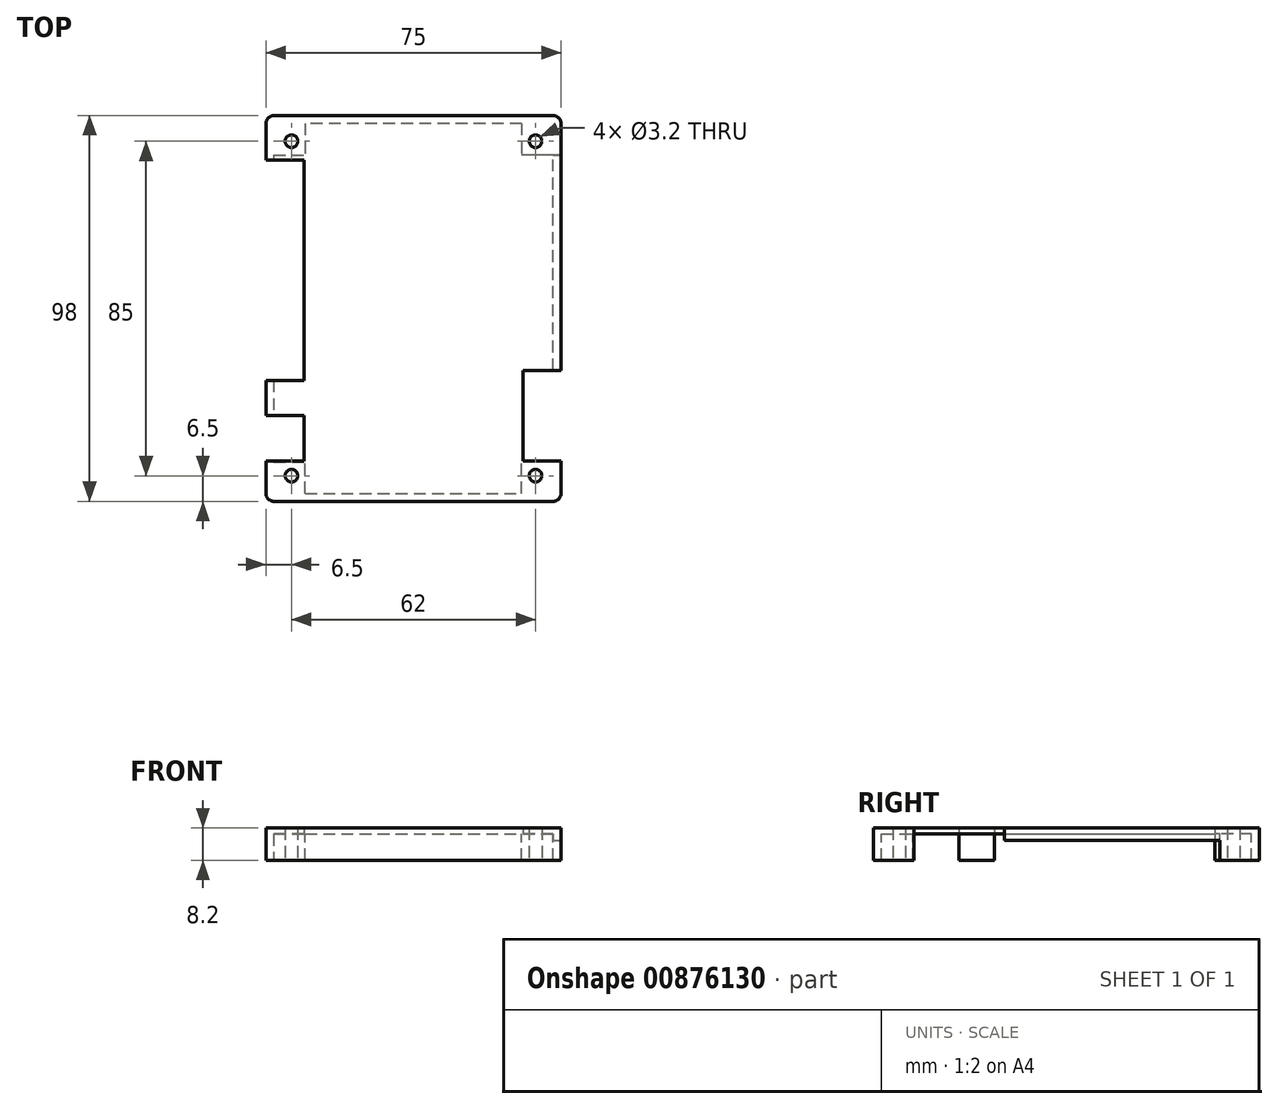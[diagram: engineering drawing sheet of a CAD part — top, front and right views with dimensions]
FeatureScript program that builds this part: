
annotation { "Feature Type Name" : "Feature", "Feature Type Description" : "" }
export const myFeature = defineFeature(function(context is Context, id is Id, definition is map)
    precondition{}
    {
        {
            var Q0;
            Q0=qCreatedBy(makeId("Top.planeOp"),FACE);
            var sketch = newSketch(context, id + "F0", { "sketchPlane" : qUnion([Q0])});
            skLineSegment(sketch, "E0", {"start": v(-9.05, 33.9) * mm, "end": v(-6.45, 33.9) * mm});
            skLineSegment(sketch, "E1", {"start": v(-6.45, 33.9) * mm, "end": v(-6.45, 30.1) * mm});
            skLineSegment(sketch, "E2", {"start": v(-6.45, 30.1) * mm, "end": v(-9.05, 30.1) * mm});
            skLineSegment(sketch, "E3", {"start": v(-9.05, 30.1) * mm, "end": v(-9.05, 33.9) * mm});
            skLineSegment(sketch, "E4", {"start": v(20.45, 33.9) * mm, "end": v(23.05, 33.9) * mm});
            skLineSegment(sketch, "E5", {"start": v(23.05, 33.9) * mm, "end": v(23.05, 30.1) * mm});
            skLineSegment(sketch, "E6", {"start": v(23.05, 30.1) * mm, "end": v(20.45, 30.1) * mm});
            skLineSegment(sketch, "E7", {"start": v(20.45, 30.1) * mm, "end": v(20.45, 33.9) * mm});
            skLineSegment(sketch, "E8", {"start": v(1.5, 35.5) * mm, "end": v(12.5, 35.5) * mm});
            skLineSegment(sketch, "E9", {"start": v(12.5, 35.5) * mm, "end": v(12.5, 28.5) * mm});
            skLineSegment(sketch, "E10", {"start": v(12.5, 28.5) * mm, "end": v(1.5, 28.5) * mm});
            skLineSegment(sketch, "E11", {"start": v(1.5, 28.5) * mm, "end": v(1.5, 35.5) * mm});
            skLineSegment(sketch, "E12", {"start": v(-5.5, 39) * mm, "end": v(-5.5, 37) * mm});
            skLineSegment(sketch, "E13", {"start": v(-4.5, 38) * mm, "end": v(-6.5, 38) * mm});
            skLineSegment(sketch, "E14", {"start": v(7, 32.5) * mm, "end": v(7, 31.5) * mm});
            skLineSegment(sketch, "E15", {"start": v(7.5, 32) * mm, "end": v(6.5, 32) * mm});
            skLineSegment(sketch, "E16", {"start": v(18, 40) * mm, "end": v(-4, 40) * mm});
            skLineSegment(sketch, "E17", {"start": v(-4, 40) * mm, "end": v(-4, 25.75) * mm});
            skLineSegment(sketch, "E18", {"start": v(-4, 25.75) * mm, "end": v(-2.25, 24) * mm});
            skLineSegment(sketch, "E19", {"start": v(-2.25, 24) * mm, "end": v(18, 24) * mm});
            skLineSegment(sketch, "E20", {"start": v(18, 24) * mm, "end": v(18, 40) * mm});
            skLineSegment(sketch, "E21", {"start": v(-7.2, 34.4) * mm, "end": v(-7.2, 36) * mm});
            skLineSegment(sketch, "E22", {"start": v(-7.2, 36) * mm, "end": v(-4, 36) * mm});
            skLineSegment(sketch, "E23", {"start": v(-7.2, 29.6) * mm, "end": v(-7.2, 28) * mm});
            skLineSegment(sketch, "E24", {"start": v(-7.2, 28) * mm, "end": v(-4, 28) * mm});
            skLineSegment(sketch, "E25", {"start": v(21.2, 29.6) * mm, "end": v(21.2, 28) * mm});
            skLineSegment(sketch, "E26", {"start": v(21.2, 28) * mm, "end": v(18, 28) * mm});
            skLineSegment(sketch, "E27", {"start": v(21.2, 34.4) * mm, "end": v(21.2, 36) * mm});
            skLineSegment(sketch, "E28", {"start": v(21.2, 36) * mm, "end": v(18, 36) * mm});
            skArc(sketch, "E29", {"start": v(13, 40) * mm, "mid": v(17, 32) * mm, "end": v(13, 24) * mm});
            skArc(sketch, "E30", {"start": v(1, 40) * mm, "mid": v(-3, 32) * mm, "end": v(1, 24) * mm});
            skArc(sketch, "E31", {"start": v(17, 32) * mm, "mid": v(7, 42) * mm, "end": v(-3, 32) * mm});
            skArc(sketch, "E32", {"start": v(-3, 32) * mm, "mid": v(7, 22) * mm, "end": v(17, 32) * mm});
            skCircle(sketch, "E33", {"center": v(29, 41) * mm, "radius": 1.65 * mm});
            skArc(sketch, "E34", {"start": v(29.64, 41) * mm, "mid": v(29, 41.63) * mm, "end": v(28.37, 41) * mm});
            skArc(sketch, "E35", {"start": v(28.37, 41) * mm, "mid": v(29, 40.37) * mm, "end": v(29.64, 41) * mm});
            skCircle(sketch, "E36", {"center": v(-33, 41) * mm, "radius": 1.65 * mm});
            skArc(sketch, "E37", {"start": v(-32.37, 41) * mm, "mid": v(-33, 41.63) * mm, "end": v(-33.63, 41) * mm});
            skArc(sketch, "E38", {"start": v(-33.63, 41) * mm, "mid": v(-33, 40.37) * mm, "end": v(-32.37, 41) * mm});
            skCircle(sketch, "E39", {"center": v(29, -44) * mm, "radius": 1.65 * mm});
            skArc(sketch, "E40", {"start": v(29.64, -44) * mm, "mid": v(29, -43.37) * mm, "end": v(28.37, -44) * mm});
            skArc(sketch, "E41", {"start": v(28.37, -44) * mm, "mid": v(29, -44.63) * mm, "end": v(29.64, -44) * mm});
            skCircle(sketch, "E42", {"center": v(-33, -44) * mm, "radius": 1.65 * mm});
            skArc(sketch, "E43", {"start": v(-32.37, -44) * mm, "mid": v(-33, -43.37) * mm, "end": v(-33.63, -44) * mm});
            skArc(sketch, "E44", {"start": v(-33.63, -44) * mm, "mid": v(-33, -44.63) * mm, "end": v(-32.37, -44) * mm});
            skLineSegment(sketch, "E45", {"start": v(-12.64, 32.77) * mm, "end": v(-12.64, 30.73) * mm});
            skLineSegment(sketch, "E46", {"start": v(-12.64, 30.73) * mm, "end": v(-14.16, 30.73) * mm});
            skLineSegment(sketch, "E47", {"start": v(-14.16, 30.73) * mm, "end": v(-14.16, 32.77) * mm});
            skLineSegment(sketch, "E48", {"start": v(-14.16, 32.77) * mm, "end": v(-12.64, 32.77) * mm});
            skLineSegment(sketch, "E49", {"start": v(-15.84, 32.77) * mm, "end": v(-15.84, 30.73) * mm});
            skLineSegment(sketch, "E50", {"start": v(-15.84, 30.73) * mm, "end": v(-17.36, 30.73) * mm});
            skLineSegment(sketch, "E51", {"start": v(-17.36, 30.73) * mm, "end": v(-17.36, 32.77) * mm});
            skLineSegment(sketch, "E52", {"start": v(-17.36, 32.77) * mm, "end": v(-15.84, 32.77) * mm});
            skLineSegment(sketch, "E53", {"start": v(-12.2, 30.35) * mm, "end": v(-12.2, 33.15) * mm});
            skLineSegment(sketch, "E54", {"start": v(-12.2, 33.15) * mm, "end": v(-17.8, 33.15) * mm});
            skLineSegment(sketch, "E55", {"start": v(-17.8, 33.15) * mm, "end": v(-17.8, 30.35) * mm});
            skLineSegment(sketch, "E56", {"start": v(-17.8, 30.35) * mm, "end": v(-12.2, 30.35) * mm});
            skLineSegment(sketch, "E57", {"start": v(-14.62, 31.75) * mm, "end": v(-15.38, 31.75) * mm});
            skLineSegment(sketch, "E58", {"start": v(-15, 31.37) * mm, "end": v(-15, 32.13) * mm});
            skLineSegment(sketch, "E59", {"start": v(-12.2, 33.15) * mm, "end": v(-12.56, 33.15) * mm});
            skLineSegment(sketch, "E60", {"start": v(-12.56, 33.15) * mm, "end": v(-12.56, 30.58) * mm});
            skLineSegment(sketch, "E61", {"start": v(-12.56, 30.58) * mm, "end": v(-12.56, 30.35) * mm});
            skLineSegment(sketch, "E62", {"start": v(-12.56, 30.35) * mm, "end": v(-12.2, 30.35) * mm});
            skLineSegment(sketch, "E63", {"start": v(-12.2, 30.35) * mm, "end": v(-12.2, 30.6) * mm});
            skLineSegment(sketch, "E64", {"start": v(-12.2, 30.6) * mm, "end": v(-12.2, 33.15) * mm});
            skLineSegment(sketch, "E65", {"start": v(-12.64, 29.52) * mm, "end": v(-12.64, 27.48) * mm});
            skLineSegment(sketch, "E66", {"start": v(-12.64, 27.48) * mm, "end": v(-14.16, 27.48) * mm});
            skLineSegment(sketch, "E67", {"start": v(-14.16, 27.48) * mm, "end": v(-14.16, 29.52) * mm});
            skLineSegment(sketch, "E68", {"start": v(-14.16, 29.52) * mm, "end": v(-12.64, 29.52) * mm});
            skLineSegment(sketch, "E69", {"start": v(-15.84, 29.52) * mm, "end": v(-15.84, 27.48) * mm});
            skLineSegment(sketch, "E70", {"start": v(-15.84, 27.48) * mm, "end": v(-17.36, 27.48) * mm});
            skLineSegment(sketch, "E71", {"start": v(-17.36, 27.48) * mm, "end": v(-17.36, 29.52) * mm});
            skLineSegment(sketch, "E72", {"start": v(-17.36, 29.52) * mm, "end": v(-15.84, 29.52) * mm});
            skLineSegment(sketch, "E73", {"start": v(-12.2, 27.1) * mm, "end": v(-12.2, 29.9) * mm});
            skLineSegment(sketch, "E74", {"start": v(-12.2, 29.9) * mm, "end": v(-17.8, 29.9) * mm});
            skLineSegment(sketch, "E75", {"start": v(-17.8, 29.9) * mm, "end": v(-17.8, 27.1) * mm});
            skLineSegment(sketch, "E76", {"start": v(-17.8, 27.1) * mm, "end": v(-12.2, 27.1) * mm});
            skLineSegment(sketch, "E77", {"start": v(-14.62, 28.5) * mm, "end": v(-15.38, 28.5) * mm});
            skLineSegment(sketch, "E78", {"start": v(-15, 28.12) * mm, "end": v(-15, 28.88) * mm});
            skLineSegment(sketch, "E79", {"start": v(-12.2, 29.9) * mm, "end": v(-12.56, 29.9) * mm});
            skLineSegment(sketch, "E80", {"start": v(-12.56, 29.9) * mm, "end": v(-12.56, 27.33) * mm});
            skLineSegment(sketch, "E81", {"start": v(-12.56, 27.33) * mm, "end": v(-12.56, 27.1) * mm});
            skLineSegment(sketch, "E82", {"start": v(-12.56, 27.1) * mm, "end": v(-12.2, 27.1) * mm});
            skLineSegment(sketch, "E83", {"start": v(-12.2, 27.1) * mm, "end": v(-12.2, 27.36) * mm});
            skLineSegment(sketch, "E84", {"start": v(-12.2, 27.36) * mm, "end": v(-12.2, 29.9) * mm});
            skLineSegment(sketch, "E85", {"start": v(-12.64, 16.77) * mm, "end": v(-12.64, 14.73) * mm});
            skLineSegment(sketch, "E86", {"start": v(-12.64, 14.73) * mm, "end": v(-14.16, 14.73) * mm});
            skLineSegment(sketch, "E87", {"start": v(-14.16, 14.73) * mm, "end": v(-14.16, 16.77) * mm});
            skLineSegment(sketch, "E88", {"start": v(-14.16, 16.77) * mm, "end": v(-12.64, 16.77) * mm});
            skLineSegment(sketch, "E89", {"start": v(-15.84, 16.77) * mm, "end": v(-15.84, 14.73) * mm});
            skLineSegment(sketch, "E90", {"start": v(-15.84, 14.73) * mm, "end": v(-17.36, 14.73) * mm});
            skLineSegment(sketch, "E91", {"start": v(-17.36, 14.73) * mm, "end": v(-17.36, 16.77) * mm});
            skLineSegment(sketch, "E92", {"start": v(-17.36, 16.77) * mm, "end": v(-15.84, 16.77) * mm});
            skLineSegment(sketch, "E93", {"start": v(-12.2, 14.35) * mm, "end": v(-12.2, 17.15) * mm});
            skLineSegment(sketch, "E94", {"start": v(-12.2, 17.15) * mm, "end": v(-17.8, 17.15) * mm});
            skLineSegment(sketch, "E95", {"start": v(-17.8, 17.15) * mm, "end": v(-17.8, 14.35) * mm});
            skLineSegment(sketch, "E96", {"start": v(-17.8, 14.35) * mm, "end": v(-12.2, 14.35) * mm});
            skLineSegment(sketch, "E97", {"start": v(-14.62, 15.75) * mm, "end": v(-15.38, 15.75) * mm});
            skLineSegment(sketch, "E98", {"start": v(-15, 15.37) * mm, "end": v(-15, 16.13) * mm});
            skLineSegment(sketch, "E99", {"start": v(-12.2, 17.15) * mm, "end": v(-12.56, 17.15) * mm});
            skLineSegment(sketch, "E100", {"start": v(-12.56, 17.15) * mm, "end": v(-12.56, 14.58) * mm});
            skLineSegment(sketch, "E101", {"start": v(-12.56, 14.58) * mm, "end": v(-12.56, 14.35) * mm});
            skLineSegment(sketch, "E102", {"start": v(-12.56, 14.35) * mm, "end": v(-12.2, 14.35) * mm});
            skLineSegment(sketch, "E103", {"start": v(-12.2, 14.35) * mm, "end": v(-12.2, 14.6) * mm});
            skLineSegment(sketch, "E104", {"start": v(-12.2, 14.6) * mm, "end": v(-12.2, 17.15) * mm});
            skLineSegment(sketch, "E105", {"start": v(-12.64, 13.52) * mm, "end": v(-12.64, 11.48) * mm});
            skLineSegment(sketch, "E106", {"start": v(-12.64, 11.48) * mm, "end": v(-14.16, 11.48) * mm});
            skLineSegment(sketch, "E107", {"start": v(-14.16, 11.48) * mm, "end": v(-14.16, 13.52) * mm});
            skLineSegment(sketch, "E108", {"start": v(-14.16, 13.52) * mm, "end": v(-12.64, 13.52) * mm});
            skLineSegment(sketch, "E109", {"start": v(-15.84, 13.52) * mm, "end": v(-15.84, 11.48) * mm});
            skLineSegment(sketch, "E110", {"start": v(-15.84, 11.48) * mm, "end": v(-17.36, 11.48) * mm});
            skLineSegment(sketch, "E111", {"start": v(-17.36, 11.48) * mm, "end": v(-17.36, 13.52) * mm});
            skLineSegment(sketch, "E112", {"start": v(-17.36, 13.52) * mm, "end": v(-15.84, 13.52) * mm});
            skLineSegment(sketch, "E113", {"start": v(-12.2, 11.1) * mm, "end": v(-12.2, 13.9) * mm});
            skLineSegment(sketch, "E114", {"start": v(-12.2, 13.9) * mm, "end": v(-17.8, 13.9) * mm});
            skLineSegment(sketch, "E115", {"start": v(-17.8, 13.9) * mm, "end": v(-17.8, 11.1) * mm});
            skLineSegment(sketch, "E116", {"start": v(-17.8, 11.1) * mm, "end": v(-12.2, 11.1) * mm});
            skLineSegment(sketch, "E117", {"start": v(-14.62, 12.5) * mm, "end": v(-15.38, 12.5) * mm});
            skLineSegment(sketch, "E118", {"start": v(-15, 12.12) * mm, "end": v(-15, 12.88) * mm});
            skLineSegment(sketch, "E119", {"start": v(-12.2, 13.9) * mm, "end": v(-12.56, 13.9) * mm});
            skLineSegment(sketch, "E120", {"start": v(-12.56, 13.9) * mm, "end": v(-12.56, 11.33) * mm});
            skLineSegment(sketch, "E121", {"start": v(-12.56, 11.33) * mm, "end": v(-12.56, 11.1) * mm});
            skLineSegment(sketch, "E122", {"start": v(-12.56, 11.1) * mm, "end": v(-12.2, 11.1) * mm});
            skLineSegment(sketch, "E123", {"start": v(-12.2, 11.1) * mm, "end": v(-12.2, 11.36) * mm});
            skLineSegment(sketch, "E124", {"start": v(-12.2, 11.36) * mm, "end": v(-12.2, 13.9) * mm});
            skLineSegment(sketch, "E125", {"start": v(-12.64, 0.77) * mm, "end": v(-12.64, -1.27) * mm});
            skLineSegment(sketch, "E126", {"start": v(-12.64, -1.27) * mm, "end": v(-14.16, -1.27) * mm});
            skLineSegment(sketch, "E127", {"start": v(-14.16, -1.27) * mm, "end": v(-14.16, 0.77) * mm});
            skLineSegment(sketch, "E128", {"start": v(-14.16, 0.77) * mm, "end": v(-12.64, 0.77) * mm});
            skLineSegment(sketch, "E129", {"start": v(-15.84, 0.77) * mm, "end": v(-15.84, -1.27) * mm});
            skLineSegment(sketch, "E130", {"start": v(-15.84, -1.27) * mm, "end": v(-17.36, -1.27) * mm});
            skLineSegment(sketch, "E131", {"start": v(-17.36, -1.27) * mm, "end": v(-17.36, 0.77) * mm});
            skLineSegment(sketch, "E132", {"start": v(-17.36, 0.77) * mm, "end": v(-15.84, 0.77) * mm});
            skLineSegment(sketch, "E133", {"start": v(-12.2, -1.65) * mm, "end": v(-12.2, 1.15) * mm});
            skLineSegment(sketch, "E134", {"start": v(-12.2, 1.15) * mm, "end": v(-17.8, 1.15) * mm});
            skLineSegment(sketch, "E135", {"start": v(-17.8, 1.15) * mm, "end": v(-17.8, -1.65) * mm});
            skLineSegment(sketch, "E136", {"start": v(-17.8, -1.65) * mm, "end": v(-12.2, -1.65) * mm});
            skLineSegment(sketch, "E137", {"start": v(-14.62, -0.25) * mm, "end": v(-15.38, -0.25) * mm});
            skLineSegment(sketch, "E138", {"start": v(-15, -0.63) * mm, "end": v(-15, 0.13) * mm});
            skLineSegment(sketch, "E139", {"start": v(-12.2, 1.15) * mm, "end": v(-12.56, 1.15) * mm});
            skLineSegment(sketch, "E140", {"start": v(-12.56, 1.15) * mm, "end": v(-12.56, -1.42) * mm});
            skLineSegment(sketch, "E141", {"start": v(-12.56, -1.42) * mm, "end": v(-12.56, -1.65) * mm});
            skLineSegment(sketch, "E142", {"start": v(-12.56, -1.65) * mm, "end": v(-12.2, -1.65) * mm});
            skLineSegment(sketch, "E143", {"start": v(-12.2, -1.65) * mm, "end": v(-12.2, -1.4) * mm});
            skLineSegment(sketch, "E144", {"start": v(-12.2, -1.4) * mm, "end": v(-12.2, 1.15) * mm});
            skLineSegment(sketch, "E145", {"start": v(-12.64, -2.48) * mm, "end": v(-12.64, -4.52) * mm});
            skLineSegment(sketch, "E146", {"start": v(-12.64, -4.52) * mm, "end": v(-14.16, -4.52) * mm});
            skLineSegment(sketch, "E147", {"start": v(-14.16, -4.52) * mm, "end": v(-14.16, -2.48) * mm});
            skLineSegment(sketch, "E148", {"start": v(-14.16, -2.48) * mm, "end": v(-12.64, -2.48) * mm});
            skLineSegment(sketch, "E149", {"start": v(-15.84, -2.48) * mm, "end": v(-15.84, -4.52) * mm});
            skLineSegment(sketch, "E150", {"start": v(-15.84, -4.52) * mm, "end": v(-17.36, -4.52) * mm});
            skLineSegment(sketch, "E151", {"start": v(-17.36, -4.52) * mm, "end": v(-17.36, -2.48) * mm});
            skLineSegment(sketch, "E152", {"start": v(-17.36, -2.48) * mm, "end": v(-15.84, -2.48) * mm});
            skLineSegment(sketch, "E153", {"start": v(-12.2, -4.9) * mm, "end": v(-12.2, -2.1) * mm});
            skLineSegment(sketch, "E154", {"start": v(-12.2, -2.1) * mm, "end": v(-17.8, -2.1) * mm});
            skLineSegment(sketch, "E155", {"start": v(-17.8, -2.1) * mm, "end": v(-17.8, -4.9) * mm});
            skLineSegment(sketch, "E156", {"start": v(-17.8, -4.9) * mm, "end": v(-12.2, -4.9) * mm});
            skLineSegment(sketch, "E157", {"start": v(-14.62, -3.5) * mm, "end": v(-15.38, -3.5) * mm});
            skLineSegment(sketch, "E158", {"start": v(-15, -3.88) * mm, "end": v(-15, -3.12) * mm});
            skLineSegment(sketch, "E159", {"start": v(-12.2, -2.1) * mm, "end": v(-12.56, -2.1) * mm});
            skLineSegment(sketch, "E160", {"start": v(-12.56, -2.1) * mm, "end": v(-12.56, -4.67) * mm});
            skLineSegment(sketch, "E161", {"start": v(-12.56, -4.67) * mm, "end": v(-12.56, -4.9) * mm});
            skLineSegment(sketch, "E162", {"start": v(-12.56, -4.9) * mm, "end": v(-12.2, -4.9) * mm});
            skLineSegment(sketch, "E163", {"start": v(-12.2, -4.9) * mm, "end": v(-12.2, -4.64) * mm});
            skLineSegment(sketch, "E164", {"start": v(-12.2, -4.64) * mm, "end": v(-12.2, -2.1) * mm});
            skLineSegment(sketch, "E165", {"start": v(-12.64, -15.23) * mm, "end": v(-12.64, -17.27) * mm});
            skLineSegment(sketch, "E166", {"start": v(-12.64, -17.27) * mm, "end": v(-14.16, -17.27) * mm});
            skLineSegment(sketch, "E167", {"start": v(-14.16, -17.27) * mm, "end": v(-14.16, -15.23) * mm});
            skLineSegment(sketch, "E168", {"start": v(-14.16, -15.23) * mm, "end": v(-12.64, -15.23) * mm});
            skLineSegment(sketch, "E169", {"start": v(-15.84, -15.23) * mm, "end": v(-15.84, -17.27) * mm});
            skLineSegment(sketch, "E170", {"start": v(-15.84, -17.27) * mm, "end": v(-17.36, -17.27) * mm});
            skLineSegment(sketch, "E171", {"start": v(-17.36, -17.27) * mm, "end": v(-17.36, -15.23) * mm});
            skLineSegment(sketch, "E172", {"start": v(-17.36, -15.23) * mm, "end": v(-15.84, -15.23) * mm});
            skLineSegment(sketch, "E173", {"start": v(-12.2, -17.65) * mm, "end": v(-12.2, -14.85) * mm});
            skLineSegment(sketch, "E174", {"start": v(-12.2, -14.85) * mm, "end": v(-17.8, -14.85) * mm});
            skLineSegment(sketch, "E175", {"start": v(-17.8, -14.85) * mm, "end": v(-17.8, -17.65) * mm});
            skLineSegment(sketch, "E176", {"start": v(-17.8, -17.65) * mm, "end": v(-12.2, -17.65) * mm});
            skLineSegment(sketch, "E177", {"start": v(-14.62, -16.25) * mm, "end": v(-15.38, -16.25) * mm});
            skLineSegment(sketch, "E178", {"start": v(-15, -16.63) * mm, "end": v(-15, -15.87) * mm});
            skLineSegment(sketch, "E179", {"start": v(-12.2, -14.85) * mm, "end": v(-12.56, -14.85) * mm});
            skLineSegment(sketch, "E180", {"start": v(-12.56, -14.85) * mm, "end": v(-12.56, -17.42) * mm});
            skLineSegment(sketch, "E181", {"start": v(-12.56, -17.42) * mm, "end": v(-12.56, -17.65) * mm});
            skLineSegment(sketch, "E182", {"start": v(-12.56, -17.65) * mm, "end": v(-12.2, -17.65) * mm});
            skLineSegment(sketch, "E183", {"start": v(-12.2, -17.65) * mm, "end": v(-12.2, -17.4) * mm});
            skLineSegment(sketch, "E184", {"start": v(-12.2, -17.4) * mm, "end": v(-12.2, -14.85) * mm});
            skLineSegment(sketch, "E185", {"start": v(-5.5, -3.75) * mm, "end": v(-7.5, -3.75) * mm});
            skLineSegment(sketch, "E186", {"start": v(-7.5, -3.75) * mm, "end": v(-7.5, 1.75) * mm});
            skLineSegment(sketch, "E187", {"start": v(-7.5, 1.75) * mm, "end": v(-5.5, 1.75) * mm});
            skLineSegment(sketch, "E188", {"start": v(-5.5, 1.75) * mm, "end": v(-5.5, -3.75) * mm});
            skLineSegment(sketch, "E189", {"start": v(-5.5, 5.25) * mm, "end": v(-7.5, 5.25) * mm});
            skLineSegment(sketch, "E190", {"start": v(-7.5, 5.25) * mm, "end": v(-7.5, 10.75) * mm});
            skLineSegment(sketch, "E191", {"start": v(-7.5, 10.75) * mm, "end": v(-5.5, 10.75) * mm});
            skLineSegment(sketch, "E192", {"start": v(-5.5, 10.75) * mm, "end": v(-5.5, 5.25) * mm});
            skLineSegment(sketch, "E193", {"start": v(-9, -1.5) * mm, "end": v(-9, 8.5) * mm});
            skArc(sketch, "E194", {"start": v(-7.75, -2.75) * mm, "mid": v(-8.63, -2.38) * mm, "end": v(-9, -1.5) * mm});
            skArc(sketch, "E195", {"start": v(-7.75, 9.75) * mm, "mid": v(-8.63, 9.38) * mm, "end": v(-9, 8.5) * mm});
            skLineSegment(sketch, "E196", {"start": v(-4, 8.5) * mm, "end": v(-4, -1.5) * mm});
            skArc(sketch, "E197", {"start": v(-5.25, -2.75) * mm, "mid": v(-4.37, -2.38) * mm, "end": v(-4, -1.5) * mm});
            skArc(sketch, "E198", {"start": v(-5.25, 9.75) * mm, "mid": v(-4.37, 9.38) * mm, "end": v(-4, 8.5) * mm});
            skLineSegment(sketch, "E199", {"start": v(-6.5, 3) * mm, "end": v(-6.5, 4) * mm});
            skLineSegment(sketch, "E200", {"start": v(-7, 3.5) * mm, "end": v(-6, 3.5) * mm});
            skLineSegment(sketch, "E201", {"start": v(-9.45, -36.25) * mm, "end": v(-9.45, -37.75) * mm});
            skLineSegment(sketch, "E202", {"start": v(-9.45, -37.75) * mm, "end": v(-11.05, -37.75) * mm});
            skLineSegment(sketch, "E203", {"start": v(-11.05, -37.75) * mm, "end": v(-11.05, -36.25) * mm});
            skLineSegment(sketch, "E204", {"start": v(-11.05, -36.25) * mm, "end": v(-9.45, -36.25) * mm});
            skLineSegment(sketch, "E205", {"start": v(-11.95, -36.25) * mm, "end": v(-11.95, -37.75) * mm});
            skLineSegment(sketch, "E206", {"start": v(-11.95, -37.75) * mm, "end": v(-13.55, -37.75) * mm});
            skLineSegment(sketch, "E207", {"start": v(-13.55, -37.75) * mm, "end": v(-13.55, -36.25) * mm});
            skLineSegment(sketch, "E208", {"start": v(-13.55, -36.25) * mm, "end": v(-11.95, -36.25) * mm});
            skLineSegment(sketch, "E209", {"start": v(-9, -38) * mm, "end": v(-9, -36) * mm});
            skLineSegment(sketch, "E210", {"start": v(-9, -36) * mm, "end": v(-13.75, -36) * mm});
            skLineSegment(sketch, "E211", {"start": v(-13.75, -36) * mm, "end": v(-13.75, -38) * mm});
            skLineSegment(sketch, "E212", {"start": v(-13.75, -38) * mm, "end": v(-9, -38) * mm});
            skLineSegment(sketch, "E213", {"start": v(-9.25, -38) * mm, "end": v(-9.25, -36) * mm});
            skArc(sketch, "E214", {"start": v(-11.25, -37) * mm, "mid": v(-11.5, -36.75) * mm, "end": v(-11.75, -37) * mm});
            skArc(sketch, "E215", {"start": v(-11.75, -37) * mm, "mid": v(-11.5, -37.25) * mm, "end": v(-11.25, -37) * mm});
            skLineSegment(sketch, "E216", {"start": v(-9.12, -38) * mm, "end": v(-9.12, -36) * mm});
            skLineSegment(sketch, "E217", {"start": v(-8.5, -38.25) * mm, "end": v(-9, -38.25) * mm});
            skLineSegment(sketch, "E218", {"start": v(-8.75, -38.5) * mm, "end": v(-8.75, -38) * mm});
            skLineSegment(sketch, "E219", {"start": v(-9.45, -33.75) * mm, "end": v(-9.45, -35.25) * mm});
            skLineSegment(sketch, "E220", {"start": v(-9.45, -35.25) * mm, "end": v(-11.05, -35.25) * mm});
            skLineSegment(sketch, "E221", {"start": v(-11.05, -35.25) * mm, "end": v(-11.05, -33.75) * mm});
            skLineSegment(sketch, "E222", {"start": v(-11.05, -33.75) * mm, "end": v(-9.45, -33.75) * mm});
            skLineSegment(sketch, "E223", {"start": v(-11.95, -33.75) * mm, "end": v(-11.95, -35.25) * mm});
            skLineSegment(sketch, "E224", {"start": v(-11.95, -35.25) * mm, "end": v(-13.55, -35.25) * mm});
            skLineSegment(sketch, "E225", {"start": v(-13.55, -35.25) * mm, "end": v(-13.55, -33.75) * mm});
            skLineSegment(sketch, "E226", {"start": v(-13.55, -33.75) * mm, "end": v(-11.95, -33.75) * mm});
            skLineSegment(sketch, "E227", {"start": v(-9, -35.5) * mm, "end": v(-9, -33.5) * mm});
            skLineSegment(sketch, "E228", {"start": v(-9, -33.5) * mm, "end": v(-13.75, -33.5) * mm});
            skLineSegment(sketch, "E229", {"start": v(-13.75, -33.5) * mm, "end": v(-13.75, -35.5) * mm});
            skLineSegment(sketch, "E230", {"start": v(-13.75, -35.5) * mm, "end": v(-9, -35.5) * mm});
            skLineSegment(sketch, "E231", {"start": v(-9.25, -35.5) * mm, "end": v(-9.25, -33.5) * mm});
            skArc(sketch, "E232", {"start": v(-11.25, -34.5) * mm, "mid": v(-11.5, -34.25) * mm, "end": v(-11.75, -34.5) * mm});
            skArc(sketch, "E233", {"start": v(-11.75, -34.5) * mm, "mid": v(-11.5, -34.75) * mm, "end": v(-11.25, -34.5) * mm});
            skLineSegment(sketch, "E234", {"start": v(-9.12, -35.5) * mm, "end": v(-9.12, -33.5) * mm});
            skLineSegment(sketch, "E235", {"start": v(-8.5, -35.75) * mm, "end": v(-9, -35.75) * mm});
            skLineSegment(sketch, "E236", {"start": v(-8.75, -36) * mm, "end": v(-8.75, -35.5) * mm});
            skLineSegment(sketch, "E237", {"start": v(-1.95, -34) * mm, "end": v(-1.95, -38) * mm});
            skLineSegment(sketch, "E238", {"start": v(-1.95, -38) * mm, "end": v(-3.45, -38) * mm});
            skLineSegment(sketch, "E239", {"start": v(-3.45, -38) * mm, "end": v(-3.45, -34) * mm});
            skLineSegment(sketch, "E240", {"start": v(-3.45, -34) * mm, "end": v(-1.95, -34) * mm});
            skLineSegment(sketch, "E241", {"start": v(-5.55, -34) * mm, "end": v(-5.55, -38) * mm});
            skLineSegment(sketch, "E242", {"start": v(-5.55, -38) * mm, "end": v(-7.05, -38) * mm});
            skLineSegment(sketch, "E243", {"start": v(-7.05, -38) * mm, "end": v(-7.05, -34) * mm});
            skLineSegment(sketch, "E244", {"start": v(-7.05, -34) * mm, "end": v(-5.55, -34) * mm});
            skLineSegment(sketch, "E245", {"start": v(-4, -36) * mm, "end": v(-5, -36) * mm});
            skLineSegment(sketch, "E246", {"start": v(-4.5, -36.5) * mm, "end": v(-4.5, -35.5) * mm});
            skLineSegment(sketch, "E247", {"start": v(-1.75, -38.5) * mm, "end": v(-1.75, -33.5) * mm});
            skLineSegment(sketch, "E248", {"start": v(-1.75, -33.5) * mm, "end": v(-7.25, -33.5) * mm});
            skLineSegment(sketch, "E249", {"start": v(-7.25, -33.5) * mm, "end": v(-7.25, -38.5) * mm});
            skLineSegment(sketch, "E250", {"start": v(-7.25, -38.5) * mm, "end": v(-1.75, -38.5) * mm});
            skLineSegment(sketch, "E251", {"start": v(-29.15, -38.15) * mm, "end": v(-29.15, -35.85) * mm});
            skLineSegment(sketch, "E252", {"start": v(-29.15, -35.85) * mm, "end": v(-26.85, -35.85) * mm});
            skLineSegment(sketch, "E253", {"start": v(-26.85, -35.85) * mm, "end": v(-26.85, -38.15) * mm});
            skLineSegment(sketch, "E254", {"start": v(-26.85, -38.15) * mm, "end": v(-29.15, -38.15) * mm});
            skLineSegment(sketch, "E255", {"start": v(-25.15, -38.15) * mm, "end": v(-25.15, -35.85) * mm});
            skLineSegment(sketch, "E256", {"start": v(-25.15, -35.85) * mm, "end": v(-22.85, -35.85) * mm});
            skLineSegment(sketch, "E257", {"start": v(-22.85, -35.85) * mm, "end": v(-22.85, -38.15) * mm});
            skLineSegment(sketch, "E258", {"start": v(-22.85, -38.15) * mm, "end": v(-25.15, -38.15) * mm});
            skLineSegment(sketch, "E259", {"start": v(-26.5, -37) * mm, "end": v(-25.5, -37) * mm});
            skLineSegment(sketch, "E260", {"start": v(-26, -36.5) * mm, "end": v(-26, -37.5) * mm});
            skLineSegment(sketch, "E261", {"start": v(-29.75, -35) * mm, "end": v(-22.5, -35) * mm});
            skLineSegment(sketch, "E262", {"start": v(-22.5, -35) * mm, "end": v(-22.5, -39) * mm});
            skLineSegment(sketch, "E263", {"start": v(-22.5, -39) * mm, "end": v(-29.75, -39) * mm});
            skLineSegment(sketch, "E264", {"start": v(-29.75, -39) * mm, "end": v(-29.75, -35) * mm});
            skLineSegment(sketch, "E265", {"start": v(-29.75, -35.25) * mm, "end": v(-29.75, -38.75) * mm});
            skLineSegment(sketch, "E266", {"start": v(-29.75, -38.75) * mm, "end": v(-29.75, -39) * mm});
            skLineSegment(sketch, "E267", {"start": v(-29.75, -39) * mm, "end": v(-29.25, -39) * mm});
            skLineSegment(sketch, "E268", {"start": v(-29.25, -39) * mm, "end": v(-29.25, -38.75) * mm});
            skLineSegment(sketch, "E269", {"start": v(-29.25, -38.75) * mm, "end": v(-29.25, -38.25) * mm});
            skLineSegment(sketch, "E270", {"start": v(-29.25, -38.25) * mm, "end": v(-29.25, -35.75) * mm});
            skLineSegment(sketch, "E271", {"start": v(-29.25, -35.75) * mm, "end": v(-29.25, -35.25) * mm});
            skLineSegment(sketch, "E272", {"start": v(-29.25, -35.25) * mm, "end": v(-29.25, -35) * mm});
            skLineSegment(sketch, "E273", {"start": v(-29.25, -35) * mm, "end": v(-29.5, -35) * mm});
            skLineSegment(sketch, "E274", {"start": v(-29.5, -35) * mm, "end": v(-29.75, -35) * mm});
            skLineSegment(sketch, "E275", {"start": v(-29.75, -35) * mm, "end": v(-29.75, -35.25) * mm});
            skLineSegment(sketch, "E276", {"start": v(-29.15, -33.65) * mm, "end": v(-29.15, -31.35) * mm});
            skLineSegment(sketch, "E277", {"start": v(-29.15, -31.35) * mm, "end": v(-26.85, -31.35) * mm});
            skLineSegment(sketch, "E278", {"start": v(-26.85, -31.35) * mm, "end": v(-26.85, -33.65) * mm});
            skLineSegment(sketch, "E279", {"start": v(-26.85, -33.65) * mm, "end": v(-29.15, -33.65) * mm});
            skLineSegment(sketch, "E280", {"start": v(-25.15, -33.65) * mm, "end": v(-25.15, -31.35) * mm});
            skLineSegment(sketch, "E281", {"start": v(-25.15, -31.35) * mm, "end": v(-22.85, -31.35) * mm});
            skLineSegment(sketch, "E282", {"start": v(-22.85, -31.35) * mm, "end": v(-22.85, -33.65) * mm});
            skLineSegment(sketch, "E283", {"start": v(-22.85, -33.65) * mm, "end": v(-25.15, -33.65) * mm});
            skLineSegment(sketch, "E284", {"start": v(-26.5, -32.5) * mm, "end": v(-25.5, -32.5) * mm});
            skLineSegment(sketch, "E285", {"start": v(-26, -32) * mm, "end": v(-26, -33) * mm});
            skLineSegment(sketch, "E286", {"start": v(-29.75, -30.5) * mm, "end": v(-22.5, -30.5) * mm});
            skLineSegment(sketch, "E287", {"start": v(-22.5, -30.5) * mm, "end": v(-22.5, -34.5) * mm});
            skLineSegment(sketch, "E288", {"start": v(-22.5, -34.5) * mm, "end": v(-29.75, -34.5) * mm});
            skLineSegment(sketch, "E289", {"start": v(-29.75, -34.5) * mm, "end": v(-29.75, -30.5) * mm});
            skLineSegment(sketch, "E290", {"start": v(-29.75, -30.75) * mm, "end": v(-29.75, -34.25) * mm});
            skLineSegment(sketch, "E291", {"start": v(-29.75, -34.25) * mm, "end": v(-29.75, -34.5) * mm});
            skLineSegment(sketch, "E292", {"start": v(-29.75, -34.5) * mm, "end": v(-29.25, -34.5) * mm});
            skLineSegment(sketch, "E293", {"start": v(-29.25, -34.5) * mm, "end": v(-29.25, -34.25) * mm});
            skLineSegment(sketch, "E294", {"start": v(-29.25, -34.25) * mm, "end": v(-29.25, -33.75) * mm});
            skLineSegment(sketch, "E295", {"start": v(-29.25, -33.75) * mm, "end": v(-29.25, -31.25) * mm});
            skLineSegment(sketch, "E296", {"start": v(-29.25, -31.25) * mm, "end": v(-29.25, -30.75) * mm});
            skLineSegment(sketch, "E297", {"start": v(-29.25, -30.75) * mm, "end": v(-29.25, -30.5) * mm});
            skLineSegment(sketch, "E298", {"start": v(-29.25, -30.5) * mm, "end": v(-29.5, -30.5) * mm});
            skLineSegment(sketch, "E299", {"start": v(-29.5, -30.5) * mm, "end": v(-29.75, -30.5) * mm});
            skLineSegment(sketch, "E300", {"start": v(-29.75, -30.5) * mm, "end": v(-29.75, -30.75) * mm});
            skCircle(sketch, "E301", {"center": v(-33, 30.5) * mm, "radius": 1.5 * mm});
            skCircle(sketch, "E302", {"center": v(-33, 34) * mm, "radius": 1.5 * mm});
            skLineSegment(sketch, "E303", {"start": v(-30.3, 35.75) * mm, "end": v(-36.8, 35.75) * mm});
            skLineSegment(sketch, "E304", {"start": v(-36.8, 35.75) * mm, "end": v(-36.8, 28.75) * mm});
            skLineSegment(sketch, "E305", {"start": v(-36.8, 28.75) * mm, "end": v(-30.3, 28.75) * mm});
            skLineSegment(sketch, "E306", {"start": v(-30.3, 28.75) * mm, "end": v(-30.3, 35.75) * mm});
            skLineSegment(sketch, "E307", {"start": v(-36.25, 35.75) * mm, "end": v(-36.25, 28.75) * mm});
            skLineSegment(sketch, "E308", {"start": v(-35.25, 35.75) * mm, "end": v(-35.25, 28.75) * mm});
            skLineSegment(sketch, "E309", {"start": v(-35, 35.75) * mm, "end": v(-35, 36.15) * mm});
            skLineSegment(sketch, "E310", {"start": v(-35, 36.15) * mm, "end": v(-34.25, 36.15) * mm});
            skLineSegment(sketch, "E311", {"start": v(-34.25, 36.15) * mm, "end": v(-34.25, 35.75) * mm});
            skCircle(sketch, "E312", {"center": v(-33, 22.5) * mm, "radius": 1.5 * mm});
            skCircle(sketch, "E313", {"center": v(-33, 26) * mm, "radius": 1.5 * mm});
            skLineSegment(sketch, "E314", {"start": v(-30.3, 27.75) * mm, "end": v(-36.8, 27.75) * mm});
            skLineSegment(sketch, "E315", {"start": v(-36.8, 27.75) * mm, "end": v(-36.8, 20.75) * mm});
            skLineSegment(sketch, "E316", {"start": v(-36.8, 20.75) * mm, "end": v(-30.3, 20.75) * mm});
            skLineSegment(sketch, "E317", {"start": v(-30.3, 20.75) * mm, "end": v(-30.3, 27.75) * mm});
            skLineSegment(sketch, "E318", {"start": v(-36.25, 27.75) * mm, "end": v(-36.25, 20.75) * mm});
            skLineSegment(sketch, "E319", {"start": v(-35.25, 27.75) * mm, "end": v(-35.25, 20.75) * mm});
            skLineSegment(sketch, "E320", {"start": v(-35, 27.75) * mm, "end": v(-35, 28.15) * mm});
            skLineSegment(sketch, "E321", {"start": v(-35, 28.15) * mm, "end": v(-34.25, 28.15) * mm});
            skLineSegment(sketch, "E322", {"start": v(-34.25, 28.15) * mm, "end": v(-34.25, 27.75) * mm});
            skCircle(sketch, "E323", {"center": v(-33, -1.5) * mm, "radius": 1.5 * mm});
            skCircle(sketch, "E324", {"center": v(-33, 2) * mm, "radius": 1.5 * mm});
            skLineSegment(sketch, "E325", {"start": v(-30.3, 3.75) * mm, "end": v(-36.8, 3.75) * mm});
            skLineSegment(sketch, "E326", {"start": v(-36.8, 3.75) * mm, "end": v(-36.8, -3.25) * mm});
            skLineSegment(sketch, "E327", {"start": v(-36.8, -3.25) * mm, "end": v(-30.3, -3.25) * mm});
            skLineSegment(sketch, "E328", {"start": v(-30.3, -3.25) * mm, "end": v(-30.3, 3.75) * mm});
            skLineSegment(sketch, "E329", {"start": v(-36.25, 3.75) * mm, "end": v(-36.25, -3.25) * mm});
            skLineSegment(sketch, "E330", {"start": v(-35.25, 3.75) * mm, "end": v(-35.25, -3.25) * mm});
            skLineSegment(sketch, "E331", {"start": v(-35, 3.75) * mm, "end": v(-35, 4.15) * mm});
            skLineSegment(sketch, "E332", {"start": v(-35, 4.15) * mm, "end": v(-34.25, 4.15) * mm});
            skLineSegment(sketch, "E333", {"start": v(-34.25, 4.15) * mm, "end": v(-34.25, 3.75) * mm});
            skCircle(sketch, "E334", {"center": v(29, -34.5) * mm, "radius": 1.5 * mm});
            skCircle(sketch, "E335", {"center": v(29, -38) * mm, "radius": 1.5 * mm});
            skLineSegment(sketch, "E336", {"start": v(26.3, -39.75) * mm, "end": v(32.8, -39.75) * mm});
            skLineSegment(sketch, "E337", {"start": v(32.8, -39.75) * mm, "end": v(32.8, -32.75) * mm});
            skLineSegment(sketch, "E338", {"start": v(32.8, -32.75) * mm, "end": v(26.3, -32.75) * mm});
            skLineSegment(sketch, "E339", {"start": v(26.3, -32.75) * mm, "end": v(26.3, -39.75) * mm});
            skLineSegment(sketch, "E340", {"start": v(32.25, -39.75) * mm, "end": v(32.25, -32.75) * mm});
            skLineSegment(sketch, "E341", {"start": v(31.25, -39.75) * mm, "end": v(31.25, -32.75) * mm});
            skLineSegment(sketch, "E342", {"start": v(31, -39.75) * mm, "end": v(31, -40.15) * mm});
            skLineSegment(sketch, "E343", {"start": v(31, -40.15) * mm, "end": v(30.25, -40.15) * mm});
            skLineSegment(sketch, "E344", {"start": v(30.25, -40.15) * mm, "end": v(30.25, -39.75) * mm});
            skCircle(sketch, "E345", {"center": v(-33, -17.5) * mm, "radius": 1.5 * mm});
            skCircle(sketch, "E346", {"center": v(-33, -14) * mm, "radius": 1.5 * mm});
            skLineSegment(sketch, "E347", {"start": v(-30.3, -12.25) * mm, "end": v(-36.8, -12.25) * mm});
            skLineSegment(sketch, "E348", {"start": v(-36.8, -12.25) * mm, "end": v(-36.8, -19.25) * mm});
            skLineSegment(sketch, "E349", {"start": v(-36.8, -19.25) * mm, "end": v(-30.3, -19.25) * mm});
            skLineSegment(sketch, "E350", {"start": v(-30.3, -19.25) * mm, "end": v(-30.3, -12.25) * mm});
            skLineSegment(sketch, "E351", {"start": v(-36.25, -12.25) * mm, "end": v(-36.25, -19.25) * mm});
            skLineSegment(sketch, "E352", {"start": v(-35.25, -12.25) * mm, "end": v(-35.25, -19.25) * mm});
            skLineSegment(sketch, "E353", {"start": v(-35, -12.25) * mm, "end": v(-35, -11.85) * mm});
            skLineSegment(sketch, "E354", {"start": v(-35, -11.85) * mm, "end": v(-34.25, -11.85) * mm});
            skLineSegment(sketch, "E355", {"start": v(-34.25, -11.85) * mm, "end": v(-34.25, -12.25) * mm});
            skCircle(sketch, "E356", {"center": v(-33, 14.5) * mm, "radius": 1.5 * mm});
            skCircle(sketch, "E357", {"center": v(-33, 18) * mm, "radius": 1.5 * mm});
            skLineSegment(sketch, "E358", {"start": v(-30.3, 19.75) * mm, "end": v(-36.8, 19.75) * mm});
            skLineSegment(sketch, "E359", {"start": v(-36.8, 19.75) * mm, "end": v(-36.8, 12.75) * mm});
            skLineSegment(sketch, "E360", {"start": v(-36.8, 12.75) * mm, "end": v(-30.3, 12.75) * mm});
            skLineSegment(sketch, "E361", {"start": v(-30.3, 12.75) * mm, "end": v(-30.3, 19.75) * mm});
            skLineSegment(sketch, "E362", {"start": v(-36.25, 19.75) * mm, "end": v(-36.25, 12.75) * mm});
            skLineSegment(sketch, "E363", {"start": v(-35.25, 19.75) * mm, "end": v(-35.25, 12.75) * mm});
            skLineSegment(sketch, "E364", {"start": v(-35, 19.75) * mm, "end": v(-35, 20.15) * mm});
            skLineSegment(sketch, "E365", {"start": v(-35, 20.15) * mm, "end": v(-34.25, 20.15) * mm});
            skLineSegment(sketch, "E366", {"start": v(-34.25, 20.15) * mm, "end": v(-34.25, 19.75) * mm});
            skCircle(sketch, "E367", {"center": v(-33, 6.5) * mm, "radius": 1.5 * mm});
            skCircle(sketch, "E368", {"center": v(-33, 10) * mm, "radius": 1.5 * mm});
            skLineSegment(sketch, "E369", {"start": v(-30.3, 11.75) * mm, "end": v(-36.8, 11.75) * mm});
            skLineSegment(sketch, "E370", {"start": v(-36.8, 11.75) * mm, "end": v(-36.8, 4.75) * mm});
            skLineSegment(sketch, "E371", {"start": v(-36.8, 4.75) * mm, "end": v(-30.3, 4.75) * mm});
            skLineSegment(sketch, "E372", {"start": v(-30.3, 4.75) * mm, "end": v(-30.3, 11.75) * mm});
            skLineSegment(sketch, "E373", {"start": v(-36.25, 11.75) * mm, "end": v(-36.25, 4.75) * mm});
            skLineSegment(sketch, "E374", {"start": v(-35.25, 11.75) * mm, "end": v(-35.25, 4.75) * mm});
            skLineSegment(sketch, "E375", {"start": v(-35, 11.75) * mm, "end": v(-35, 12.15) * mm});
            skLineSegment(sketch, "E376", {"start": v(-35, 12.15) * mm, "end": v(-34.25, 12.15) * mm});
            skLineSegment(sketch, "E377", {"start": v(-34.25, 12.15) * mm, "end": v(-34.25, 11.75) * mm});
            skCircle(sketch, "E378", {"center": v(-33, -9.5) * mm, "radius": 1.5 * mm});
            skCircle(sketch, "E379", {"center": v(-33, -6) * mm, "radius": 1.5 * mm});
            skLineSegment(sketch, "E380", {"start": v(-30.3, -4.25) * mm, "end": v(-36.8, -4.25) * mm});
            skLineSegment(sketch, "E381", {"start": v(-36.8, -4.25) * mm, "end": v(-36.8, -11.25) * mm});
            skLineSegment(sketch, "E382", {"start": v(-36.8, -11.25) * mm, "end": v(-30.3, -11.25) * mm});
            skLineSegment(sketch, "E383", {"start": v(-30.3, -11.25) * mm, "end": v(-30.3, -4.25) * mm});
            skLineSegment(sketch, "E384", {"start": v(-36.25, -4.25) * mm, "end": v(-36.25, -11.25) * mm});
            skLineSegment(sketch, "E385", {"start": v(-35.25, -4.25) * mm, "end": v(-35.25, -11.25) * mm});
            skLineSegment(sketch, "E386", {"start": v(-35, -4.25) * mm, "end": v(-35, -3.85) * mm});
            skLineSegment(sketch, "E387", {"start": v(-35, -3.85) * mm, "end": v(-34.25, -3.85) * mm});
            skLineSegment(sketch, "E388", {"start": v(-34.25, -3.85) * mm, "end": v(-34.25, -4.25) * mm});
            skCircle(sketch, "E389", {"center": v(-33, -34.5) * mm, "radius": 1.5 * mm});
            skCircle(sketch, "E390", {"center": v(-33, -31) * mm, "radius": 1.5 * mm});
            skCircle(sketch, "E391", {"center": v(-33, -38) * mm, "radius": 1.5 * mm});
            skLineSegment(sketch, "E392", {"start": v(-30.3, -29.25) * mm, "end": v(-36.8, -29.25) * mm});
            skLineSegment(sketch, "E393", {"start": v(-36.8, -29.25) * mm, "end": v(-36.8, -39.75) * mm});
            skLineSegment(sketch, "E394", {"start": v(-36.8, -39.75) * mm, "end": v(-30.3, -39.75) * mm});
            skLineSegment(sketch, "E395", {"start": v(-30.3, -39.75) * mm, "end": v(-30.3, -29.25) * mm});
            skLineSegment(sketch, "E396", {"start": v(-36.25, -29.25) * mm, "end": v(-36.25, -39.75) * mm});
            skLineSegment(sketch, "E397", {"start": v(-35.25, -29.25) * mm, "end": v(-35.25, -39.75) * mm});
            skLineSegment(sketch, "E398", {"start": v(-35, -29.25) * mm, "end": v(-35, -28.85) * mm});
            skLineSegment(sketch, "E399", {"start": v(-35, -28.85) * mm, "end": v(-34.25, -28.85) * mm});
            skLineSegment(sketch, "E400", {"start": v(-34.25, -28.85) * mm, "end": v(-34.25, -29.25) * mm});
            skLineSegment(sketch, "E401", {"start": v(29.26, -0.76) * mm, "end": v(27.74, -0.76) * mm});
            skLineSegment(sketch, "E402", {"start": v(27.74, -0.76) * mm, "end": v(27.74, 0.76) * mm});
            skLineSegment(sketch, "E403", {"start": v(27.74, 0.76) * mm, "end": v(29.26, 0.76) * mm});
            skLineSegment(sketch, "E404", {"start": v(29.26, 0.76) * mm, "end": v(29.26, -0.76) * mm});
            skCircle(sketch, "E405", {"center": v(28.5, 2.5) * mm, "radius": 0.76 * mm});
            skCircle(sketch, "E406", {"center": v(28.5, 5) * mm, "radius": 0.76 * mm});
            skCircle(sketch, "E407", {"center": v(28.5, 7.5) * mm, "radius": 0.76 * mm});
            skLineSegment(sketch, "E408", {"start": v(28.2, -2.5) * mm, "end": v(35.1, -2.5) * mm});
            skLineSegment(sketch, "E409", {"start": v(35.1, -2.5) * mm, "end": v(35.1, 10) * mm});
            skLineSegment(sketch, "E410", {"start": v(35.1, 10) * mm, "end": v(27.2, 10) * mm});
            skLineSegment(sketch, "E411", {"start": v(27.2, 10) * mm, "end": v(27.2, -1.5) * mm});
            skLineSegment(sketch, "E412", {"start": v(27.2, -1.5) * mm, "end": v(28.2, -2.5) * mm});
            skLineSegment(sketch, "E413", {"start": v(29.26, 12.74) * mm, "end": v(27.74, 12.74) * mm});
            skLineSegment(sketch, "E414", {"start": v(27.74, 12.74) * mm, "end": v(27.74, 14.26) * mm});
            skLineSegment(sketch, "E415", {"start": v(27.74, 14.26) * mm, "end": v(29.26, 14.26) * mm});
            skLineSegment(sketch, "E416", {"start": v(29.26, 14.26) * mm, "end": v(29.26, 12.74) * mm});
            skCircle(sketch, "E417", {"center": v(28.5, 16) * mm, "radius": 0.76 * mm});
            skCircle(sketch, "E418", {"center": v(28.5, 18.5) * mm, "radius": 0.76 * mm});
            skCircle(sketch, "E419", {"center": v(28.5, 21) * mm, "radius": 0.76 * mm});
            skLineSegment(sketch, "E420", {"start": v(28.2, 11) * mm, "end": v(35.1, 11) * mm});
            skLineSegment(sketch, "E421", {"start": v(35.1, 11) * mm, "end": v(35.1, 23.5) * mm});
            skLineSegment(sketch, "E422", {"start": v(35.1, 23.5) * mm, "end": v(27.2, 23.5) * mm});
            skLineSegment(sketch, "E423", {"start": v(27.2, 23.5) * mm, "end": v(27.2, 12) * mm});
            skLineSegment(sketch, "E424", {"start": v(27.2, 12) * mm, "end": v(28.2, 11) * mm});
            skLineSegment(sketch, "E425", {"start": v(29.26, 26.24) * mm, "end": v(27.74, 26.24) * mm});
            skLineSegment(sketch, "E426", {"start": v(27.74, 26.24) * mm, "end": v(27.74, 27.76) * mm});
            skLineSegment(sketch, "E427", {"start": v(27.74, 27.76) * mm, "end": v(29.26, 27.76) * mm});
            skLineSegment(sketch, "E428", {"start": v(29.26, 27.76) * mm, "end": v(29.26, 26.24) * mm});
            skCircle(sketch, "E429", {"center": v(28.5, 29.5) * mm, "radius": 0.76 * mm});
            skCircle(sketch, "E430", {"center": v(28.5, 32) * mm, "radius": 0.76 * mm});
            skCircle(sketch, "E431", {"center": v(28.5, 34.5) * mm, "radius": 0.76 * mm});
            skLineSegment(sketch, "E432", {"start": v(28.2, 24.5) * mm, "end": v(35.1, 24.5) * mm});
            skLineSegment(sketch, "E433", {"start": v(35.1, 24.5) * mm, "end": v(35.1, 37) * mm});
            skLineSegment(sketch, "E434", {"start": v(35.1, 37) * mm, "end": v(27.2, 37) * mm});
            skLineSegment(sketch, "E435", {"start": v(27.2, 37) * mm, "end": v(27.2, 25.5) * mm});
            skLineSegment(sketch, "E436", {"start": v(27.2, 25.5) * mm, "end": v(28.2, 24.5) * mm});
            skLineSegment(sketch, "E437", {"start": v(29.26, -14.26) * mm, "end": v(27.74, -14.26) * mm});
            skLineSegment(sketch, "E438", {"start": v(27.74, -14.26) * mm, "end": v(27.74, -12.74) * mm});
            skLineSegment(sketch, "E439", {"start": v(27.74, -12.74) * mm, "end": v(29.26, -12.74) * mm});
            skLineSegment(sketch, "E440", {"start": v(29.26, -12.74) * mm, "end": v(29.26, -14.26) * mm});
            skCircle(sketch, "E441", {"center": v(28.5, -11) * mm, "radius": 0.76 * mm});
            skCircle(sketch, "E442", {"center": v(28.5, -8.5) * mm, "radius": 0.76 * mm});
            skCircle(sketch, "E443", {"center": v(28.5, -6) * mm, "radius": 0.76 * mm});
            skLineSegment(sketch, "E444", {"start": v(28.2, -16) * mm, "end": v(35.1, -16) * mm});
            skLineSegment(sketch, "E445", {"start": v(35.1, -16) * mm, "end": v(35.1, -3.5) * mm});
            skLineSegment(sketch, "E446", {"start": v(35.1, -3.5) * mm, "end": v(27.2, -3.5) * mm});
            skLineSegment(sketch, "E447", {"start": v(27.2, -3.5) * mm, "end": v(27.2, -15) * mm});
            skLineSegment(sketch, "E448", {"start": v(27.2, -15) * mm, "end": v(28.2, -16) * mm});
            skCircle(sketch, "E449", {"center": v(29, -26.5) * mm, "radius": 1.5 * mm});
            skCircle(sketch, "E450", {"center": v(29, -30) * mm, "radius": 1.5 * mm});
            skCircle(sketch, "E451", {"center": v(29, -23) * mm, "radius": 1.5 * mm});
            skCircle(sketch, "E452", {"center": v(29, -19.5) * mm, "radius": 1.5 * mm});
            skLineSegment(sketch, "E453", {"start": v(26.3, -31.75) * mm, "end": v(32.8, -31.75) * mm});
            skLineSegment(sketch, "E454", {"start": v(32.8, -31.75) * mm, "end": v(32.8, -17.75) * mm});
            skLineSegment(sketch, "E455", {"start": v(32.8, -17.75) * mm, "end": v(26.3, -17.75) * mm});
            skLineSegment(sketch, "E456", {"start": v(26.3, -17.75) * mm, "end": v(26.3, -31.75) * mm});
            skLineSegment(sketch, "E457", {"start": v(32.25, -31.75) * mm, "end": v(32.25, -17.75) * mm});
            skLineSegment(sketch, "E458", {"start": v(31.25, -31.75) * mm, "end": v(31.25, -17.75) * mm});
            skLineSegment(sketch, "E459", {"start": v(31, -31.75) * mm, "end": v(31, -32.15) * mm});
            skLineSegment(sketch, "E460", {"start": v(31, -32.15) * mm, "end": v(30.25, -32.15) * mm});
            skLineSegment(sketch, "E461", {"start": v(30.25, -32.15) * mm, "end": v(30.25, -31.75) * mm});
            skLineSegment(sketch, "E462", {"start": v(16.24, 17.24) * mm, "end": v(16.24, 18.76) * mm});
            skLineSegment(sketch, "E463", {"start": v(16.24, 18.76) * mm, "end": v(17.76, 18.76) * mm});
            skLineSegment(sketch, "E464", {"start": v(17.76, 18.76) * mm, "end": v(17.76, 17.24) * mm});
            skLineSegment(sketch, "E465", {"start": v(17.76, 17.24) * mm, "end": v(16.24, 17.24) * mm});
            skCircle(sketch, "E466", {"center": v(14.5, 18) * mm, "radius": 0.76 * mm});
            skCircle(sketch, "E467", {"center": v(12, 18) * mm, "radius": 0.76 * mm});
            skCircle(sketch, "E468", {"center": v(9.5, 18) * mm, "radius": 0.76 * mm});
            skLineSegment(sketch, "E469", {"start": v(7.05, 14.62) * mm, "end": v(19.45, 14.62) * mm});
            skLineSegment(sketch, "E470", {"start": v(19.45, 14.62) * mm, "end": v(19.45, 19.52) * mm});
            skLineSegment(sketch, "E471", {"start": v(19.45, 19.52) * mm, "end": v(7.05, 19.52) * mm});
            skLineSegment(sketch, "E472", {"start": v(7.05, 19.52) * mm, "end": v(7.05, 14.62) * mm});
            skLineSegment(sketch, "E473", {"start": v(8.05, 19.52) * mm, "end": v(7.05, 18.52) * mm});
            skLineSegment(sketch, "E474", {"start": v(18.45, 19.52) * mm, "end": v(19.45, 18.52) * mm});
            skLineSegment(sketch, "E475", {"start": v(16.35, -39.1) * mm, "end": v(13.65, -39.1) * mm});
            skLineSegment(sketch, "E476", {"start": v(13.65, -39.1) * mm, "end": v(13.65, -37.9) * mm});
            skLineSegment(sketch, "E477", {"start": v(13.65, -37.9) * mm, "end": v(16.35, -37.9) * mm});
            skLineSegment(sketch, "E478", {"start": v(16.35, -37.9) * mm, "end": v(16.35, -39.1) * mm});
            skLineSegment(sketch, "E479", {"start": v(16.35, -36.1) * mm, "end": v(13.65, -36.1) * mm});
            skLineSegment(sketch, "E480", {"start": v(13.65, -36.1) * mm, "end": v(13.65, -34.9) * mm});
            skLineSegment(sketch, "E481", {"start": v(13.65, -34.9) * mm, "end": v(16.35, -34.9) * mm});
            skLineSegment(sketch, "E482", {"start": v(16.35, -34.9) * mm, "end": v(16.35, -36.1) * mm});
            skArc(sketch, "E483", {"start": v(16.6, -39) * mm, "mid": v(16.5, -39.25) * mm, "end": v(16.25, -39.35) * mm});
            skLineSegment(sketch, "E484", {"start": v(13.75, -39.35) * mm, "end": v(16.25, -39.35) * mm});
            skArc(sketch, "E485", {"start": v(13.75, -39.35) * mm, "mid": v(13.5, -39.25) * mm, "end": v(13.4, -39) * mm});
            skLineSegment(sketch, "E486", {"start": v(16.6, -35) * mm, "end": v(16.6, -39) * mm});
            skLineSegment(sketch, "E487", {"start": v(13.4, -39) * mm, "end": v(13.4, -35) * mm});
            skArc(sketch, "E488", {"start": v(15.2, -37) * mm, "mid": v(15, -36.8) * mm, "end": v(14.8, -37) * mm});
            skArc(sketch, "E489", {"start": v(14.8, -37) * mm, "mid": v(15, -37.2) * mm, "end": v(15.2, -37) * mm});
            skArc(sketch, "E490", {"start": v(16.25, -34.65) * mm, "mid": v(16.5, -34.75) * mm, "end": v(16.6, -35) * mm});
            skArc(sketch, "E491", {"start": v(13.4, -35) * mm, "mid": v(13.5, -34.75) * mm, "end": v(13.75, -34.65) * mm});
            skLineSegment(sketch, "E492", {"start": v(16.25, -34.65) * mm, "end": v(13.75, -34.65) * mm});
            skLineSegment(sketch, "E493", {"start": v(20.35, -39.1) * mm, "end": v(17.65, -39.1) * mm});
            skLineSegment(sketch, "E494", {"start": v(17.65, -39.1) * mm, "end": v(17.65, -37.9) * mm});
            skLineSegment(sketch, "E495", {"start": v(17.65, -37.9) * mm, "end": v(20.35, -37.9) * mm});
            skLineSegment(sketch, "E496", {"start": v(20.35, -37.9) * mm, "end": v(20.35, -39.1) * mm});
            skLineSegment(sketch, "E497", {"start": v(20.35, -36.1) * mm, "end": v(17.65, -36.1) * mm});
            skLineSegment(sketch, "E498", {"start": v(17.65, -36.1) * mm, "end": v(17.65, -34.9) * mm});
            skLineSegment(sketch, "E499", {"start": v(17.65, -34.9) * mm, "end": v(20.35, -34.9) * mm});
            skLineSegment(sketch, "E500", {"start": v(20.35, -34.9) * mm, "end": v(20.35, -36.1) * mm});
            skArc(sketch, "E501", {"start": v(20.6, -39) * mm, "mid": v(20.5, -39.25) * mm, "end": v(20.25, -39.35) * mm});
            skLineSegment(sketch, "E502", {"start": v(17.75, -39.35) * mm, "end": v(20.25, -39.35) * mm});
            skArc(sketch, "E503", {"start": v(17.75, -39.35) * mm, "mid": v(17.5, -39.25) * mm, "end": v(17.4, -39) * mm});
            skLineSegment(sketch, "E504", {"start": v(20.6, -35) * mm, "end": v(20.6, -39) * mm});
            skLineSegment(sketch, "E505", {"start": v(17.4, -39) * mm, "end": v(17.4, -35) * mm});
            skArc(sketch, "E506", {"start": v(19.2, -37) * mm, "mid": v(19, -36.8) * mm, "end": v(18.8, -37) * mm});
            skArc(sketch, "E507", {"start": v(18.8, -37) * mm, "mid": v(19, -37.2) * mm, "end": v(19.2, -37) * mm});
            skArc(sketch, "E508", {"start": v(20.25, -34.65) * mm, "mid": v(20.5, -34.75) * mm, "end": v(20.6, -35) * mm});
            skArc(sketch, "E509", {"start": v(17.4, -35) * mm, "mid": v(17.5, -34.75) * mm, "end": v(17.75, -34.65) * mm});
            skLineSegment(sketch, "E510", {"start": v(20.25, -34.65) * mm, "end": v(17.75, -34.65) * mm});
            skLineSegment(sketch, "E511", {"start": v(12.35, -39.1) * mm, "end": v(9.65, -39.1) * mm});
            skLineSegment(sketch, "E512", {"start": v(9.65, -39.1) * mm, "end": v(9.65, -37.9) * mm});
            skLineSegment(sketch, "E513", {"start": v(9.65, -37.9) * mm, "end": v(12.35, -37.9) * mm});
            skLineSegment(sketch, "E514", {"start": v(12.35, -37.9) * mm, "end": v(12.35, -39.1) * mm});
            skLineSegment(sketch, "E515", {"start": v(12.35, -36.1) * mm, "end": v(9.65, -36.1) * mm});
            skLineSegment(sketch, "E516", {"start": v(9.65, -36.1) * mm, "end": v(9.65, -34.9) * mm});
            skLineSegment(sketch, "E517", {"start": v(9.65, -34.9) * mm, "end": v(12.35, -34.9) * mm});
            skLineSegment(sketch, "E518", {"start": v(12.35, -34.9) * mm, "end": v(12.35, -36.1) * mm});
            skArc(sketch, "E519", {"start": v(12.6, -39) * mm, "mid": v(12.5, -39.25) * mm, "end": v(12.25, -39.35) * mm});
            skLineSegment(sketch, "E520", {"start": v(9.75, -39.35) * mm, "end": v(12.25, -39.35) * mm});
            skArc(sketch, "E521", {"start": v(9.75, -39.35) * mm, "mid": v(9.5, -39.25) * mm, "end": v(9.4, -39) * mm});
            skLineSegment(sketch, "E522", {"start": v(12.6, -35) * mm, "end": v(12.6, -39) * mm});
            skLineSegment(sketch, "E523", {"start": v(9.4, -39) * mm, "end": v(9.4, -35) * mm});
            skArc(sketch, "E524", {"start": v(11.2, -37) * mm, "mid": v(11, -36.8) * mm, "end": v(10.8, -37) * mm});
            skArc(sketch, "E525", {"start": v(10.8, -37) * mm, "mid": v(11, -37.2) * mm, "end": v(11.2, -37) * mm});
            skArc(sketch, "E526", {"start": v(12.25, -34.65) * mm, "mid": v(12.5, -34.75) * mm, "end": v(12.6, -35) * mm});
            skArc(sketch, "E527", {"start": v(9.4, -35) * mm, "mid": v(9.5, -34.75) * mm, "end": v(9.75, -34.65) * mm});
            skLineSegment(sketch, "E528", {"start": v(12.25, -34.65) * mm, "end": v(9.75, -34.65) * mm});
            skLineSegment(sketch, "E529", {"start": v(-9.4, -38.65) * mm, "end": v(-9.4, -41.35) * mm});
            skLineSegment(sketch, "E530", {"start": v(-9.4, -41.35) * mm, "end": v(-10.6, -41.35) * mm});
            skLineSegment(sketch, "E531", {"start": v(-10.6, -41.35) * mm, "end": v(-10.6, -38.65) * mm});
            skLineSegment(sketch, "E532", {"start": v(-10.6, -38.65) * mm, "end": v(-9.4, -38.65) * mm});
            skLineSegment(sketch, "E533", {"start": v(-12.4, -38.65) * mm, "end": v(-12.4, -41.35) * mm});
            skLineSegment(sketch, "E534", {"start": v(-12.4, -41.35) * mm, "end": v(-13.6, -41.35) * mm});
            skLineSegment(sketch, "E535", {"start": v(-13.6, -41.35) * mm, "end": v(-13.6, -38.65) * mm});
            skLineSegment(sketch, "E536", {"start": v(-13.6, -38.65) * mm, "end": v(-12.4, -38.65) * mm});
            skArc(sketch, "E537", {"start": v(-9.5, -38.4) * mm, "mid": v(-9.25, -38.5) * mm, "end": v(-9.15, -38.75) * mm});
            skLineSegment(sketch, "E538", {"start": v(-9.15, -41.25) * mm, "end": v(-9.15, -38.75) * mm});
            skArc(sketch, "E539", {"start": v(-9.15, -41.25) * mm, "mid": v(-9.25, -41.5) * mm, "end": v(-9.5, -41.6) * mm});
            skLineSegment(sketch, "E540", {"start": v(-13.5, -38.4) * mm, "end": v(-9.5, -38.4) * mm});
            skLineSegment(sketch, "E541", {"start": v(-9.5, -41.6) * mm, "end": v(-13.5, -41.6) * mm});
            skArc(sketch, "E542", {"start": v(-11.3, -40) * mm, "mid": v(-11.5, -39.8) * mm, "end": v(-11.7, -40) * mm});
            skArc(sketch, "E543", {"start": v(-11.7, -40) * mm, "mid": v(-11.5, -40.2) * mm, "end": v(-11.3, -40) * mm});
            skArc(sketch, "E544", {"start": v(-13.85, -38.75) * mm, "mid": v(-13.75, -38.5) * mm, "end": v(-13.5, -38.4) * mm});
            skArc(sketch, "E545", {"start": v(-13.5, -41.6) * mm, "mid": v(-13.75, -41.5) * mm, "end": v(-13.85, -41.25) * mm});
            skLineSegment(sketch, "E546", {"start": v(-13.85, -38.75) * mm, "end": v(-13.85, -41.25) * mm});
            skLineSegment(sketch, "E547", {"start": v(3.35, -46.1) * mm, "end": v(0.65, -46.1) * mm});
            skLineSegment(sketch, "E548", {"start": v(0.65, -46.1) * mm, "end": v(0.65, -44.9) * mm});
            skLineSegment(sketch, "E549", {"start": v(0.65, -44.9) * mm, "end": v(3.35, -44.9) * mm});
            skLineSegment(sketch, "E550", {"start": v(3.35, -44.9) * mm, "end": v(3.35, -46.1) * mm});
            skLineSegment(sketch, "E551", {"start": v(3.35, -43.1) * mm, "end": v(0.65, -43.1) * mm});
            skLineSegment(sketch, "E552", {"start": v(0.65, -43.1) * mm, "end": v(0.65, -41.9) * mm});
            skLineSegment(sketch, "E553", {"start": v(0.65, -41.9) * mm, "end": v(3.35, -41.9) * mm});
            skLineSegment(sketch, "E554", {"start": v(3.35, -41.9) * mm, "end": v(3.35, -43.1) * mm});
            skArc(sketch, "E555", {"start": v(3.6, -46) * mm, "mid": v(3.5, -46.25) * mm, "end": v(3.25, -46.35) * mm});
            skLineSegment(sketch, "E556", {"start": v(0.75, -46.35) * mm, "end": v(3.25, -46.35) * mm});
            skArc(sketch, "E557", {"start": v(0.75, -46.35) * mm, "mid": v(0.5, -46.25) * mm, "end": v(0.4, -46) * mm});
            skLineSegment(sketch, "E558", {"start": v(3.6, -42) * mm, "end": v(3.6, -46) * mm});
            skLineSegment(sketch, "E559", {"start": v(0.4, -46) * mm, "end": v(0.4, -42) * mm});
            skArc(sketch, "E560", {"start": v(2.2, -44) * mm, "mid": v(2, -43.8) * mm, "end": v(1.8, -44) * mm});
            skArc(sketch, "E561", {"start": v(1.8, -44) * mm, "mid": v(2, -44.2) * mm, "end": v(2.2, -44) * mm});
            skArc(sketch, "E562", {"start": v(3.25, -41.65) * mm, "mid": v(3.5, -41.75) * mm, "end": v(3.6, -42) * mm});
            skArc(sketch, "E563", {"start": v(0.4, -42) * mm, "mid": v(0.5, -41.75) * mm, "end": v(0.75, -41.65) * mm});
            skLineSegment(sketch, "E564", {"start": v(3.25, -41.65) * mm, "end": v(0.75, -41.65) * mm});
            skLineSegment(sketch, "E565", {"start": v(15.1, -10.65) * mm, "end": v(15.1, -13.35) * mm});
            skLineSegment(sketch, "E566", {"start": v(15.1, -13.35) * mm, "end": v(13.9, -13.35) * mm});
            skLineSegment(sketch, "E567", {"start": v(13.9, -13.35) * mm, "end": v(13.9, -10.65) * mm});
            skLineSegment(sketch, "E568", {"start": v(13.9, -10.65) * mm, "end": v(15.1, -10.65) * mm});
            skLineSegment(sketch, "E569", {"start": v(12.1, -10.65) * mm, "end": v(12.1, -13.35) * mm});
            skLineSegment(sketch, "E570", {"start": v(12.1, -13.35) * mm, "end": v(10.9, -13.35) * mm});
            skLineSegment(sketch, "E571", {"start": v(10.9, -13.35) * mm, "end": v(10.9, -10.65) * mm});
            skLineSegment(sketch, "E572", {"start": v(10.9, -10.65) * mm, "end": v(12.1, -10.65) * mm});
            skArc(sketch, "E573", {"start": v(15, -10.4) * mm, "mid": v(15.25, -10.5) * mm, "end": v(15.35, -10.75) * mm});
            skLineSegment(sketch, "E574", {"start": v(15.35, -13.25) * mm, "end": v(15.35, -10.75) * mm});
            skArc(sketch, "E575", {"start": v(15.35, -13.25) * mm, "mid": v(15.25, -13.5) * mm, "end": v(15, -13.6) * mm});
            skLineSegment(sketch, "E576", {"start": v(11, -10.4) * mm, "end": v(15, -10.4) * mm});
            skLineSegment(sketch, "E577", {"start": v(15, -13.6) * mm, "end": v(11, -13.6) * mm});
            skArc(sketch, "E578", {"start": v(13.2, -12) * mm, "mid": v(13, -11.8) * mm, "end": v(12.8, -12) * mm});
            skArc(sketch, "E579", {"start": v(12.8, -12) * mm, "mid": v(13, -12.2) * mm, "end": v(13.2, -12) * mm});
            skArc(sketch, "E580", {"start": v(10.65, -10.75) * mm, "mid": v(10.75, -10.5) * mm, "end": v(11, -10.4) * mm});
            skArc(sketch, "E581", {"start": v(11, -13.6) * mm, "mid": v(10.75, -13.5) * mm, "end": v(10.65, -13.25) * mm});
            skLineSegment(sketch, "E582", {"start": v(10.65, -10.75) * mm, "end": v(10.65, -13.25) * mm});
            skLineSegment(sketch, "E583", {"start": v(24.15, -32.15) * mm, "end": v(21.85, -32.15) * mm});
            skLineSegment(sketch, "E584", {"start": v(21.85, -32.15) * mm, "end": v(21.85, -29.85) * mm});
            skLineSegment(sketch, "E585", {"start": v(21.85, -29.85) * mm, "end": v(24.15, -29.85) * mm});
            skLineSegment(sketch, "E586", {"start": v(24.15, -29.85) * mm, "end": v(24.15, -32.15) * mm});
            skLineSegment(sketch, "E587", {"start": v(24.15, -28.15) * mm, "end": v(21.85, -28.15) * mm});
            skLineSegment(sketch, "E588", {"start": v(21.85, -28.15) * mm, "end": v(21.85, -25.85) * mm});
            skLineSegment(sketch, "E589", {"start": v(21.85, -25.85) * mm, "end": v(24.15, -25.85) * mm});
            skLineSegment(sketch, "E590", {"start": v(24.15, -25.85) * mm, "end": v(24.15, -28.15) * mm});
            skLineSegment(sketch, "E591", {"start": v(23, -29) * mm, "end": v(23.62, -29.63) * mm});
            skLineSegment(sketch, "E592", {"start": v(23.62, -29.63) * mm, "end": v(22.38, -29.63) * mm});
            skLineSegment(sketch, "E593", {"start": v(22.38, -29.63) * mm, "end": v(23, -29) * mm});
            skLineSegment(sketch, "E594", {"start": v(22, -28.75) * mm, "end": v(22.25, -29) * mm});
            skLineSegment(sketch, "E595", {"start": v(22.25, -29) * mm, "end": v(23.75, -29) * mm});
            skLineSegment(sketch, "E596", {"start": v(23.75, -29) * mm, "end": v(24, -29.25) * mm});
            skLineSegment(sketch, "E597", {"start": v(21, -32.38) * mm, "end": v(21, -25.63) * mm});
            skLineSegment(sketch, "E598", {"start": v(21, -25.63) * mm, "end": v(25, -25.63) * mm});
            skLineSegment(sketch, "E599", {"start": v(25, -25.63) * mm, "end": v(25, -32.38) * mm});
            skLineSegment(sketch, "E600", {"start": v(25, -32.38) * mm, "end": v(21, -32.38) * mm});
            skLineSegment(sketch, "E601", {"start": v(23, -29) * mm, "end": v(22.38, -28.38) * mm});
            skLineSegment(sketch, "E602", {"start": v(22.38, -28.38) * mm, "end": v(23.62, -28.38) * mm});
            skLineSegment(sketch, "E603", {"start": v(23.62, -28.38) * mm, "end": v(23, -29) * mm});
            skLineSegment(sketch, "E604", {"start": v(21.85, -17.85) * mm, "end": v(24.15, -17.85) * mm});
            skLineSegment(sketch, "E605", {"start": v(24.15, -17.85) * mm, "end": v(24.15, -20.15) * mm});
            skLineSegment(sketch, "E606", {"start": v(24.15, -20.15) * mm, "end": v(21.85, -20.15) * mm});
            skLineSegment(sketch, "E607", {"start": v(21.85, -20.15) * mm, "end": v(21.85, -17.85) * mm});
            skLineSegment(sketch, "E608", {"start": v(21.85, -21.85) * mm, "end": v(24.15, -21.85) * mm});
            skLineSegment(sketch, "E609", {"start": v(24.15, -21.85) * mm, "end": v(24.15, -24.15) * mm});
            skLineSegment(sketch, "E610", {"start": v(24.15, -24.15) * mm, "end": v(21.85, -24.15) * mm});
            skLineSegment(sketch, "E611", {"start": v(21.85, -24.15) * mm, "end": v(21.85, -21.85) * mm});
            skLineSegment(sketch, "E612", {"start": v(23, -21) * mm, "end": v(22.38, -20.38) * mm});
            skLineSegment(sketch, "E613", {"start": v(22.38, -20.38) * mm, "end": v(23.62, -20.38) * mm});
            skLineSegment(sketch, "E614", {"start": v(23.62, -20.38) * mm, "end": v(23, -21) * mm});
            skLineSegment(sketch, "E615", {"start": v(24, -21.25) * mm, "end": v(23.75, -21) * mm});
            skLineSegment(sketch, "E616", {"start": v(23.75, -21) * mm, "end": v(22.25, -21) * mm});
            skLineSegment(sketch, "E617", {"start": v(22.25, -21) * mm, "end": v(22, -20.75) * mm});
            skLineSegment(sketch, "E618", {"start": v(25, -17.62) * mm, "end": v(25, -24.38) * mm});
            skLineSegment(sketch, "E619", {"start": v(25, -24.38) * mm, "end": v(21, -24.38) * mm});
            skLineSegment(sketch, "E620", {"start": v(21, -24.38) * mm, "end": v(21, -17.62) * mm});
            skLineSegment(sketch, "E621", {"start": v(21, -17.62) * mm, "end": v(25, -17.62) * mm});
            skLineSegment(sketch, "E622", {"start": v(23, -21) * mm, "end": v(23.62, -21.63) * mm});
            skLineSegment(sketch, "E623", {"start": v(23.62, -21.63) * mm, "end": v(22.38, -21.63) * mm});
            skLineSegment(sketch, "E624", {"start": v(22.38, -21.63) * mm, "end": v(23, -21) * mm});
            skLineSegment(sketch, "E625", {"start": v(-6.4, -43.15) * mm, "end": v(-5.2, -43.15) * mm});
            skLineSegment(sketch, "E626", {"start": v(-5.2, -43.15) * mm, "end": v(-5.2, -43.85) * mm});
            skLineSegment(sketch, "E627", {"start": v(-5.2, -43.85) * mm, "end": v(-6.4, -43.85) * mm});
            skLineSegment(sketch, "E628", {"start": v(-6.4, -43.85) * mm, "end": v(-6.4, -43.15) * mm});
            skLineSegment(sketch, "E629", {"start": v(-6.4, -42.2) * mm, "end": v(-5.2, -42.2) * mm});
            skLineSegment(sketch, "E630", {"start": v(-5.2, -42.2) * mm, "end": v(-5.2, -42.9) * mm});
            skLineSegment(sketch, "E631", {"start": v(-5.2, -42.9) * mm, "end": v(-6.4, -42.9) * mm});
            skLineSegment(sketch, "E632", {"start": v(-6.4, -42.9) * mm, "end": v(-6.4, -42.2) * mm});
            skLineSegment(sketch, "E633", {"start": v(-6.4, -44.1) * mm, "end": v(-5.2, -44.1) * mm});
            skLineSegment(sketch, "E634", {"start": v(-5.2, -44.1) * mm, "end": v(-5.2, -44.8) * mm});
            skLineSegment(sketch, "E635", {"start": v(-5.2, -44.8) * mm, "end": v(-6.4, -44.8) * mm});
            skLineSegment(sketch, "E636", {"start": v(-6.4, -44.8) * mm, "end": v(-6.4, -44.1) * mm});
            skLineSegment(sketch, "E637", {"start": v(-3.8, -42.2) * mm, "end": v(-2.6, -42.2) * mm});
            skLineSegment(sketch, "E638", {"start": v(-2.6, -42.2) * mm, "end": v(-2.6, -42.9) * mm});
            skLineSegment(sketch, "E639", {"start": v(-2.6, -42.9) * mm, "end": v(-3.8, -42.9) * mm});
            skLineSegment(sketch, "E640", {"start": v(-3.8, -42.9) * mm, "end": v(-3.8, -42.2) * mm});
            skLineSegment(sketch, "E641", {"start": v(-3.8, -43.15) * mm, "end": v(-2.6, -43.15) * mm});
            skLineSegment(sketch, "E642", {"start": v(-2.6, -43.15) * mm, "end": v(-2.6, -43.85) * mm});
            skLineSegment(sketch, "E643", {"start": v(-2.6, -43.85) * mm, "end": v(-3.8, -43.85) * mm});
            skLineSegment(sketch, "E644", {"start": v(-3.8, -43.85) * mm, "end": v(-3.8, -43.15) * mm});
            skLineSegment(sketch, "E645", {"start": v(-3.8, -44.1) * mm, "end": v(-2.6, -44.1) * mm});
            skLineSegment(sketch, "E646", {"start": v(-2.6, -44.1) * mm, "end": v(-2.6, -44.8) * mm});
            skLineSegment(sketch, "E647", {"start": v(-2.6, -44.8) * mm, "end": v(-3.8, -44.8) * mm});
            skLineSegment(sketch, "E648", {"start": v(-3.8, -44.8) * mm, "end": v(-3.8, -44.1) * mm});
            skLineSegment(sketch, "E649", {"start": v(-4.5, -43) * mm, "end": v(-4.5, -44) * mm});
            skLineSegment(sketch, "E650", {"start": v(-4, -43.5) * mm, "end": v(-5, -43.5) * mm});
            skLineSegment(sketch, "E651", {"start": v(-3, -42) * mm, "end": v(-3, -41.88) * mm});
            skLineSegment(sketch, "E652", {"start": v(-3, -41.88) * mm, "end": v(-6, -41.88) * mm});
            skLineSegment(sketch, "E653", {"start": v(-6, -41.88) * mm, "end": v(-6, -42) * mm});
            skLineSegment(sketch, "E654", {"start": v(-3, -45) * mm, "end": v(-3, -45.12) * mm});
            skLineSegment(sketch, "E655", {"start": v(-3, -45.12) * mm, "end": v(-6, -45.12) * mm});
            skLineSegment(sketch, "E656", {"start": v(-6, -45.12) * mm, "end": v(-6, -45) * mm});
            skArc(sketch, "E657", {"start": v(-6.25, -41.75) * mm, "mid": v(-6.5, -41.5) * mm, "end": v(-6.75, -41.75) * mm});
            skArc(sketch, "E658", {"start": v(-6.75, -41.75) * mm, "mid": v(-6.5, -42) * mm, "end": v(-6.25, -41.75) * mm});
            skLineSegment(sketch, "E659", {"start": v(0.44, 6) * mm, "end": v(1.96, 6) * mm});
            skArc(sketch, "E660", {"start": v(1.96, 6) * mm, "mid": v(2.15, 5.8) * mm, "end": v(1.96, 5.61) * mm});
            skLineSegment(sketch, "E661", {"start": v(1.96, 5.61) * mm, "end": v(0.44, 5.61) * mm});
            skArc(sketch, "E662", {"start": v(0.44, 5.61) * mm, "mid": v(0.25, 5.8) * mm, "end": v(0.44, 6) * mm});
            skLineSegment(sketch, "E663", {"start": v(1.96, -2) * mm, "end": v(0.44, -2) * mm});
            skArc(sketch, "E664", {"start": v(0.44, -2) * mm, "mid": v(0.25, -1.8) * mm, "end": v(0.44, -1.61) * mm});
            skLineSegment(sketch, "E665", {"start": v(0.44, -1.61) * mm, "end": v(1.96, -1.61) * mm});
            skArc(sketch, "E666", {"start": v(1.96, -1.61) * mm, "mid": v(2.15, -1.8) * mm, "end": v(1.96, -2) * mm});
            skLineSegment(sketch, "E667", {"start": v(3, -4.56) * mm, "end": v(3, -3.04) * mm});
            skArc(sketch, "E668", {"start": v(3, -3.04) * mm, "mid": v(3.2, -2.85) * mm, "end": v(3.39, -3.04) * mm});
            skLineSegment(sketch, "E669", {"start": v(3.39, -3.04) * mm, "end": v(3.39, -4.56) * mm});
            skArc(sketch, "E670", {"start": v(3.39, -4.56) * mm, "mid": v(3.2, -4.75) * mm, "end": v(3, -4.56) * mm});
            skLineSegment(sketch, "E671", {"start": v(11, -3.04) * mm, "end": v(11, -4.56) * mm});
            skArc(sketch, "E672", {"start": v(11, -4.56) * mm, "mid": v(10.8, -4.75) * mm, "end": v(10.61, -4.56) * mm});
            skLineSegment(sketch, "E673", {"start": v(10.61, -4.56) * mm, "end": v(10.61, -3.04) * mm});
            skArc(sketch, "E674", {"start": v(10.61, -3.04) * mm, "mid": v(10.8, -2.85) * mm, "end": v(11, -3.04) * mm});
            skLineSegment(sketch, "E675", {"start": v(13.56, -2) * mm, "end": v(12.04, -2) * mm});
            skArc(sketch, "E676", {"start": v(12.04, -2) * mm, "mid": v(11.85, -1.8) * mm, "end": v(12.04, -1.61) * mm});
            skLineSegment(sketch, "E677", {"start": v(12.04, -1.61) * mm, "end": v(13.56, -1.61) * mm});
            skArc(sketch, "E678", {"start": v(13.56, -1.61) * mm, "mid": v(13.75, -1.8) * mm, "end": v(13.56, -2) * mm});
            skLineSegment(sketch, "E679", {"start": v(12.04, 6) * mm, "end": v(13.56, 6) * mm});
            skArc(sketch, "E680", {"start": v(13.56, 6) * mm, "mid": v(13.75, 5.8) * mm, "end": v(13.56, 5.61) * mm});
            skLineSegment(sketch, "E681", {"start": v(13.56, 5.61) * mm, "end": v(12.04, 5.61) * mm});
            skArc(sketch, "E682", {"start": v(12.04, 5.61) * mm, "mid": v(11.85, 5.8) * mm, "end": v(12.04, 6) * mm});
            skLineSegment(sketch, "E683", {"start": v(11, 8.56) * mm, "end": v(11, 7.04) * mm});
            skArc(sketch, "E684", {"start": v(11, 7.04) * mm, "mid": v(10.8, 6.85) * mm, "end": v(10.61, 7.04) * mm});
            skLineSegment(sketch, "E685", {"start": v(10.61, 7.04) * mm, "end": v(10.61, 8.56) * mm});
            skArc(sketch, "E686", {"start": v(10.61, 8.56) * mm, "mid": v(10.8, 8.75) * mm, "end": v(11, 8.56) * mm});
            skLineSegment(sketch, "E687", {"start": v(3, 7.04) * mm, "end": v(3, 8.56) * mm});
            skArc(sketch, "E688", {"start": v(3, 8.56) * mm, "mid": v(3.2, 8.75) * mm, "end": v(3.39, 8.56) * mm});
            skLineSegment(sketch, "E689", {"start": v(3.39, 8.56) * mm, "end": v(3.39, 7.04) * mm});
            skArc(sketch, "E690", {"start": v(3.39, 7.04) * mm, "mid": v(3.2, 6.85) * mm, "end": v(3, 7.04) * mm});
            skLineSegment(sketch, "E691", {"start": v(0.37, 5.38) * mm, "end": v(2.03, 5.38) * mm});
            skArc(sketch, "E692", {"start": v(2.03, 5.38) * mm, "mid": v(2.15, 5.25) * mm, "end": v(2.03, 5.12) * mm});
            skLineSegment(sketch, "E693", {"start": v(2.03, 5.12) * mm, "end": v(0.37, 5.12) * mm});
            skArc(sketch, "E694", {"start": v(0.37, 5.12) * mm, "mid": v(0.25, 5.25) * mm, "end": v(0.37, 5.38) * mm});
            skLineSegment(sketch, "E695", {"start": v(0.37, 4.88) * mm, "end": v(2.03, 4.88) * mm});
            skArc(sketch, "E696", {"start": v(2.03, 4.88) * mm, "mid": v(2.15, 4.75) * mm, "end": v(2.03, 4.62) * mm});
            skLineSegment(sketch, "E697", {"start": v(2.03, 4.62) * mm, "end": v(0.37, 4.62) * mm});
            skArc(sketch, "E698", {"start": v(0.37, 4.62) * mm, "mid": v(0.25, 4.75) * mm, "end": v(0.37, 4.88) * mm});
            skLineSegment(sketch, "E699", {"start": v(0.37, 4.38) * mm, "end": v(2.03, 4.38) * mm});
            skArc(sketch, "E700", {"start": v(2.03, 4.38) * mm, "mid": v(2.15, 4.25) * mm, "end": v(2.03, 4.12) * mm});
            skLineSegment(sketch, "E701", {"start": v(2.03, 4.12) * mm, "end": v(0.37, 4.12) * mm});
            skArc(sketch, "E702", {"start": v(0.37, 4.12) * mm, "mid": v(0.25, 4.25) * mm, "end": v(0.37, 4.38) * mm});
            skLineSegment(sketch, "E703", {"start": v(0.37, 3.88) * mm, "end": v(2.03, 3.88) * mm});
            skArc(sketch, "E704", {"start": v(2.03, 3.88) * mm, "mid": v(2.15, 3.75) * mm, "end": v(2.03, 3.62) * mm});
            skLineSegment(sketch, "E705", {"start": v(2.03, 3.62) * mm, "end": v(0.37, 3.62) * mm});
            skArc(sketch, "E706", {"start": v(0.37, 3.62) * mm, "mid": v(0.25, 3.75) * mm, "end": v(0.37, 3.88) * mm});
            skLineSegment(sketch, "E707", {"start": v(0.37, 3.38) * mm, "end": v(2.03, 3.38) * mm});
            skArc(sketch, "E708", {"start": v(2.03, 3.38) * mm, "mid": v(2.15, 3.25) * mm, "end": v(2.03, 3.12) * mm});
            skLineSegment(sketch, "E709", {"start": v(2.03, 3.12) * mm, "end": v(0.37, 3.12) * mm});
            skArc(sketch, "E710", {"start": v(0.37, 3.12) * mm, "mid": v(0.25, 3.25) * mm, "end": v(0.37, 3.38) * mm});
            skLineSegment(sketch, "E711", {"start": v(0.37, 2.88) * mm, "end": v(2.03, 2.88) * mm});
            skArc(sketch, "E712", {"start": v(2.03, 2.88) * mm, "mid": v(2.15, 2.75) * mm, "end": v(2.03, 2.62) * mm});
            skLineSegment(sketch, "E713", {"start": v(2.03, 2.62) * mm, "end": v(0.37, 2.62) * mm});
            skArc(sketch, "E714", {"start": v(0.37, 2.62) * mm, "mid": v(0.25, 2.75) * mm, "end": v(0.37, 2.88) * mm});
            skLineSegment(sketch, "E715", {"start": v(0.37, 2.38) * mm, "end": v(2.03, 2.38) * mm});
            skArc(sketch, "E716", {"start": v(2.03, 2.38) * mm, "mid": v(2.15, 2.25) * mm, "end": v(2.03, 2.12) * mm});
            skLineSegment(sketch, "E717", {"start": v(2.03, 2.12) * mm, "end": v(0.37, 2.12) * mm});
            skArc(sketch, "E718", {"start": v(0.37, 2.12) * mm, "mid": v(0.25, 2.25) * mm, "end": v(0.37, 2.38) * mm});
            skLineSegment(sketch, "E719", {"start": v(0.37, 1.88) * mm, "end": v(2.03, 1.88) * mm});
            skArc(sketch, "E720", {"start": v(2.03, 1.88) * mm, "mid": v(2.15, 1.75) * mm, "end": v(2.03, 1.62) * mm});
            skLineSegment(sketch, "E721", {"start": v(2.03, 1.62) * mm, "end": v(0.37, 1.62) * mm});
            skArc(sketch, "E722", {"start": v(0.37, 1.62) * mm, "mid": v(0.25, 1.75) * mm, "end": v(0.37, 1.88) * mm});
            skLineSegment(sketch, "E723", {"start": v(0.37, 1.38) * mm, "end": v(2.03, 1.38) * mm});
            skArc(sketch, "E724", {"start": v(2.03, 1.38) * mm, "mid": v(2.15, 1.25) * mm, "end": v(2.03, 1.12) * mm});
            skLineSegment(sketch, "E725", {"start": v(2.03, 1.12) * mm, "end": v(0.37, 1.12) * mm});
            skArc(sketch, "E726", {"start": v(0.37, 1.12) * mm, "mid": v(0.25, 1.25) * mm, "end": v(0.37, 1.38) * mm});
            skLineSegment(sketch, "E727", {"start": v(0.37, 0.88) * mm, "end": v(2.03, 0.88) * mm});
            skArc(sketch, "E728", {"start": v(2.03, 0.88) * mm, "mid": v(2.15, 0.75) * mm, "end": v(2.03, 0.62) * mm});
            skLineSegment(sketch, "E729", {"start": v(2.03, 0.62) * mm, "end": v(0.37, 0.62) * mm});
            skArc(sketch, "E730", {"start": v(0.37, 0.62) * mm, "mid": v(0.25, 0.75) * mm, "end": v(0.37, 0.88) * mm});
            skLineSegment(sketch, "E731", {"start": v(0.37, 0.38) * mm, "end": v(2.03, 0.38) * mm});
            skArc(sketch, "E732", {"start": v(2.03, 0.38) * mm, "mid": v(2.15, 0.25) * mm, "end": v(2.03, 0.12) * mm});
            skLineSegment(sketch, "E733", {"start": v(2.03, 0.12) * mm, "end": v(0.37, 0.12) * mm});
            skArc(sketch, "E734", {"start": v(0.37, 0.12) * mm, "mid": v(0.25, 0.25) * mm, "end": v(0.37, 0.38) * mm});
            skLineSegment(sketch, "E735", {"start": v(0.37, -0.12) * mm, "end": v(2.03, -0.12) * mm});
            skArc(sketch, "E736", {"start": v(2.03, -0.12) * mm, "mid": v(2.15, -0.25) * mm, "end": v(2.03, -0.38) * mm});
            skLineSegment(sketch, "E737", {"start": v(2.03, -0.38) * mm, "end": v(0.37, -0.38) * mm});
            skArc(sketch, "E738", {"start": v(0.37, -0.38) * mm, "mid": v(0.25, -0.25) * mm, "end": v(0.37, -0.12) * mm});
            skLineSegment(sketch, "E739", {"start": v(0.37, -0.62) * mm, "end": v(2.03, -0.62) * mm});
            skArc(sketch, "E740", {"start": v(2.03, -0.62) * mm, "mid": v(2.15, -0.75) * mm, "end": v(2.03, -0.88) * mm});
            skLineSegment(sketch, "E741", {"start": v(2.03, -0.88) * mm, "end": v(0.37, -0.88) * mm});
            skArc(sketch, "E742", {"start": v(0.37, -0.88) * mm, "mid": v(0.25, -0.75) * mm, "end": v(0.37, -0.62) * mm});
            skLineSegment(sketch, "E743", {"start": v(0.37, -1.12) * mm, "end": v(2.03, -1.12) * mm});
            skArc(sketch, "E744", {"start": v(2.03, -1.12) * mm, "mid": v(2.15, -1.25) * mm, "end": v(2.03, -1.38) * mm});
            skLineSegment(sketch, "E745", {"start": v(2.03, -1.38) * mm, "end": v(0.37, -1.38) * mm});
            skArc(sketch, "E746", {"start": v(0.37, -1.38) * mm, "mid": v(0.25, -1.25) * mm, "end": v(0.37, -1.12) * mm});
            skLineSegment(sketch, "E747", {"start": v(11.97, -1.12) * mm, "end": v(13.63, -1.12) * mm});
            skArc(sketch, "E748", {"start": v(13.63, -1.12) * mm, "mid": v(13.75, -1.25) * mm, "end": v(13.63, -1.38) * mm});
            skLineSegment(sketch, "E749", {"start": v(13.63, -1.38) * mm, "end": v(11.97, -1.38) * mm});
            skArc(sketch, "E750", {"start": v(11.97, -1.38) * mm, "mid": v(11.85, -1.25) * mm, "end": v(11.97, -1.12) * mm});
            skLineSegment(sketch, "E751", {"start": v(11.97, -0.62) * mm, "end": v(13.63, -0.62) * mm});
            skArc(sketch, "E752", {"start": v(13.63, -0.62) * mm, "mid": v(13.75, -0.75) * mm, "end": v(13.63, -0.88) * mm});
            skLineSegment(sketch, "E753", {"start": v(13.63, -0.88) * mm, "end": v(11.97, -0.88) * mm});
            skArc(sketch, "E754", {"start": v(11.97, -0.88) * mm, "mid": v(11.85, -0.75) * mm, "end": v(11.97, -0.62) * mm});
            skLineSegment(sketch, "E755", {"start": v(11.97, -0.12) * mm, "end": v(13.63, -0.12) * mm});
            skArc(sketch, "E756", {"start": v(13.63, -0.12) * mm, "mid": v(13.75, -0.25) * mm, "end": v(13.63, -0.38) * mm});
            skLineSegment(sketch, "E757", {"start": v(13.63, -0.38) * mm, "end": v(11.97, -0.38) * mm});
            skArc(sketch, "E758", {"start": v(11.97, -0.38) * mm, "mid": v(11.85, -0.25) * mm, "end": v(11.97, -0.12) * mm});
            skLineSegment(sketch, "E759", {"start": v(11.97, 0.38) * mm, "end": v(13.63, 0.38) * mm});
            skArc(sketch, "E760", {"start": v(13.63, 0.38) * mm, "mid": v(13.75, 0.25) * mm, "end": v(13.63, 0.12) * mm});
            skLineSegment(sketch, "E761", {"start": v(13.63, 0.12) * mm, "end": v(11.97, 0.12) * mm});
            skArc(sketch, "E762", {"start": v(11.97, 0.12) * mm, "mid": v(11.85, 0.25) * mm, "end": v(11.97, 0.38) * mm});
            skLineSegment(sketch, "E763", {"start": v(11.97, 0.88) * mm, "end": v(13.63, 0.88) * mm});
            skArc(sketch, "E764", {"start": v(13.63, 0.88) * mm, "mid": v(13.75, 0.75) * mm, "end": v(13.63, 0.62) * mm});
            skLineSegment(sketch, "E765", {"start": v(13.63, 0.62) * mm, "end": v(11.97, 0.62) * mm});
            skArc(sketch, "E766", {"start": v(11.97, 0.62) * mm, "mid": v(11.85, 0.75) * mm, "end": v(11.97, 0.88) * mm});
            skLineSegment(sketch, "E767", {"start": v(11.97, 1.38) * mm, "end": v(13.63, 1.38) * mm});
            skArc(sketch, "E768", {"start": v(13.63, 1.38) * mm, "mid": v(13.75, 1.25) * mm, "end": v(13.63, 1.12) * mm});
            skLineSegment(sketch, "E769", {"start": v(13.63, 1.12) * mm, "end": v(11.97, 1.12) * mm});
            skArc(sketch, "E770", {"start": v(11.97, 1.12) * mm, "mid": v(11.85, 1.25) * mm, "end": v(11.97, 1.38) * mm});
            skLineSegment(sketch, "E771", {"start": v(11.97, 1.88) * mm, "end": v(13.63, 1.88) * mm});
            skArc(sketch, "E772", {"start": v(13.63, 1.88) * mm, "mid": v(13.75, 1.75) * mm, "end": v(13.63, 1.62) * mm});
            skLineSegment(sketch, "E773", {"start": v(13.63, 1.62) * mm, "end": v(11.97, 1.62) * mm});
            skArc(sketch, "E774", {"start": v(11.97, 1.62) * mm, "mid": v(11.85, 1.75) * mm, "end": v(11.97, 1.88) * mm});
            skLineSegment(sketch, "E775", {"start": v(11.97, 2.38) * mm, "end": v(13.63, 2.38) * mm});
            skArc(sketch, "E776", {"start": v(13.63, 2.38) * mm, "mid": v(13.75, 2.25) * mm, "end": v(13.63, 2.12) * mm});
            skLineSegment(sketch, "E777", {"start": v(13.63, 2.12) * mm, "end": v(11.97, 2.12) * mm});
            skArc(sketch, "E778", {"start": v(11.97, 2.12) * mm, "mid": v(11.85, 2.25) * mm, "end": v(11.97, 2.38) * mm});
            skLineSegment(sketch, "E779", {"start": v(11.97, 2.88) * mm, "end": v(13.63, 2.88) * mm});
            skArc(sketch, "E780", {"start": v(13.63, 2.88) * mm, "mid": v(13.75, 2.75) * mm, "end": v(13.63, 2.62) * mm});
            skLineSegment(sketch, "E781", {"start": v(13.63, 2.62) * mm, "end": v(11.97, 2.62) * mm});
            skArc(sketch, "E782", {"start": v(11.97, 2.62) * mm, "mid": v(11.85, 2.75) * mm, "end": v(11.97, 2.88) * mm});
            skLineSegment(sketch, "E783", {"start": v(11.97, 3.38) * mm, "end": v(13.63, 3.38) * mm});
            skArc(sketch, "E784", {"start": v(13.63, 3.38) * mm, "mid": v(13.75, 3.25) * mm, "end": v(13.63, 3.12) * mm});
            skLineSegment(sketch, "E785", {"start": v(13.63, 3.12) * mm, "end": v(11.97, 3.12) * mm});
            skArc(sketch, "E786", {"start": v(11.97, 3.12) * mm, "mid": v(11.85, 3.25) * mm, "end": v(11.97, 3.38) * mm});
            skLineSegment(sketch, "E787", {"start": v(11.97, 3.88) * mm, "end": v(13.63, 3.88) * mm});
            skArc(sketch, "E788", {"start": v(13.63, 3.88) * mm, "mid": v(13.75, 3.75) * mm, "end": v(13.63, 3.62) * mm});
            skLineSegment(sketch, "E789", {"start": v(13.63, 3.62) * mm, "end": v(11.97, 3.62) * mm});
            skArc(sketch, "E790", {"start": v(11.97, 3.62) * mm, "mid": v(11.85, 3.75) * mm, "end": v(11.97, 3.88) * mm});
            skLineSegment(sketch, "E791", {"start": v(11.97, 4.38) * mm, "end": v(13.63, 4.38) * mm});
            skArc(sketch, "E792", {"start": v(13.63, 4.38) * mm, "mid": v(13.75, 4.25) * mm, "end": v(13.63, 4.12) * mm});
            skLineSegment(sketch, "E793", {"start": v(13.63, 4.12) * mm, "end": v(11.97, 4.12) * mm});
            skArc(sketch, "E794", {"start": v(11.97, 4.12) * mm, "mid": v(11.85, 4.25) * mm, "end": v(11.97, 4.38) * mm});
            skLineSegment(sketch, "E795", {"start": v(11.97, 4.88) * mm, "end": v(13.63, 4.88) * mm});
            skArc(sketch, "E796", {"start": v(13.63, 4.88) * mm, "mid": v(13.75, 4.75) * mm, "end": v(13.63, 4.62) * mm});
            skLineSegment(sketch, "E797", {"start": v(13.63, 4.62) * mm, "end": v(11.97, 4.62) * mm});
            skArc(sketch, "E798", {"start": v(11.97, 4.62) * mm, "mid": v(11.85, 4.75) * mm, "end": v(11.97, 4.88) * mm});
            skLineSegment(sketch, "E799", {"start": v(11.97, 5.38) * mm, "end": v(13.63, 5.38) * mm});
            skArc(sketch, "E800", {"start": v(13.63, 5.38) * mm, "mid": v(13.75, 5.25) * mm, "end": v(13.63, 5.12) * mm});
            skLineSegment(sketch, "E801", {"start": v(13.63, 5.12) * mm, "end": v(11.97, 5.12) * mm});
            skArc(sketch, "E802", {"start": v(11.97, 5.12) * mm, "mid": v(11.85, 5.25) * mm, "end": v(11.97, 5.38) * mm});
            skLineSegment(sketch, "E803", {"start": v(3.88, -2.97) * mm, "end": v(3.88, -4.63) * mm});
            skArc(sketch, "E804", {"start": v(3.88, -4.63) * mm, "mid": v(3.75, -4.75) * mm, "end": v(3.62, -4.63) * mm});
            skLineSegment(sketch, "E805", {"start": v(3.62, -4.63) * mm, "end": v(3.62, -2.97) * mm});
            skArc(sketch, "E806", {"start": v(3.62, -2.97) * mm, "mid": v(3.75, -2.85) * mm, "end": v(3.88, -2.97) * mm});
            skLineSegment(sketch, "E807", {"start": v(4.38, -2.97) * mm, "end": v(4.38, -4.63) * mm});
            skArc(sketch, "E808", {"start": v(4.38, -4.63) * mm, "mid": v(4.25, -4.75) * mm, "end": v(4.12, -4.63) * mm});
            skLineSegment(sketch, "E809", {"start": v(4.12, -4.63) * mm, "end": v(4.12, -2.97) * mm});
            skArc(sketch, "E810", {"start": v(4.12, -2.97) * mm, "mid": v(4.25, -2.85) * mm, "end": v(4.38, -2.97) * mm});
            skLineSegment(sketch, "E811", {"start": v(4.88, -2.97) * mm, "end": v(4.88, -4.63) * mm});
            skArc(sketch, "E812", {"start": v(4.88, -4.63) * mm, "mid": v(4.75, -4.75) * mm, "end": v(4.62, -4.63) * mm});
            skLineSegment(sketch, "E813", {"start": v(4.62, -4.63) * mm, "end": v(4.62, -2.97) * mm});
            skArc(sketch, "E814", {"start": v(4.62, -2.97) * mm, "mid": v(4.75, -2.85) * mm, "end": v(4.88, -2.97) * mm});
            skLineSegment(sketch, "E815", {"start": v(5.38, -2.97) * mm, "end": v(5.38, -4.63) * mm});
            skArc(sketch, "E816", {"start": v(5.38, -4.63) * mm, "mid": v(5.25, -4.75) * mm, "end": v(5.12, -4.63) * mm});
            skLineSegment(sketch, "E817", {"start": v(5.12, -4.63) * mm, "end": v(5.12, -2.97) * mm});
            skArc(sketch, "E818", {"start": v(5.12, -2.97) * mm, "mid": v(5.25, -2.85) * mm, "end": v(5.38, -2.97) * mm});
            skLineSegment(sketch, "E819", {"start": v(5.88, -2.97) * mm, "end": v(5.88, -4.63) * mm});
            skArc(sketch, "E820", {"start": v(5.88, -4.63) * mm, "mid": v(5.75, -4.75) * mm, "end": v(5.62, -4.63) * mm});
            skLineSegment(sketch, "E821", {"start": v(5.62, -4.63) * mm, "end": v(5.62, -2.97) * mm});
            skArc(sketch, "E822", {"start": v(5.62, -2.97) * mm, "mid": v(5.75, -2.85) * mm, "end": v(5.88, -2.97) * mm});
            skLineSegment(sketch, "E823", {"start": v(6.38, -2.97) * mm, "end": v(6.38, -4.63) * mm});
            skArc(sketch, "E824", {"start": v(6.38, -4.63) * mm, "mid": v(6.25, -4.75) * mm, "end": v(6.12, -4.63) * mm});
            skLineSegment(sketch, "E825", {"start": v(6.12, -4.63) * mm, "end": v(6.12, -2.97) * mm});
            skArc(sketch, "E826", {"start": v(6.12, -2.97) * mm, "mid": v(6.25, -2.85) * mm, "end": v(6.38, -2.97) * mm});
            skLineSegment(sketch, "E827", {"start": v(6.88, -2.97) * mm, "end": v(6.88, -4.63) * mm});
            skArc(sketch, "E828", {"start": v(6.88, -4.63) * mm, "mid": v(6.75, -4.75) * mm, "end": v(6.62, -4.63) * mm});
            skLineSegment(sketch, "E829", {"start": v(6.62, -4.63) * mm, "end": v(6.62, -2.97) * mm});
            skArc(sketch, "E830", {"start": v(6.62, -2.97) * mm, "mid": v(6.75, -2.85) * mm, "end": v(6.88, -2.97) * mm});
            skLineSegment(sketch, "E831", {"start": v(7.38, -2.97) * mm, "end": v(7.38, -4.63) * mm});
            skArc(sketch, "E832", {"start": v(7.38, -4.63) * mm, "mid": v(7.25, -4.75) * mm, "end": v(7.12, -4.63) * mm});
            skLineSegment(sketch, "E833", {"start": v(7.12, -4.63) * mm, "end": v(7.12, -2.97) * mm});
            skArc(sketch, "E834", {"start": v(7.12, -2.97) * mm, "mid": v(7.25, -2.85) * mm, "end": v(7.38, -2.97) * mm});
            skLineSegment(sketch, "E835", {"start": v(7.88, -2.97) * mm, "end": v(7.88, -4.63) * mm});
            skArc(sketch, "E836", {"start": v(7.88, -4.63) * mm, "mid": v(7.75, -4.75) * mm, "end": v(7.62, -4.63) * mm});
            skLineSegment(sketch, "E837", {"start": v(7.62, -4.63) * mm, "end": v(7.62, -2.97) * mm});
            skArc(sketch, "E838", {"start": v(7.62, -2.97) * mm, "mid": v(7.75, -2.85) * mm, "end": v(7.88, -2.97) * mm});
            skLineSegment(sketch, "E839", {"start": v(8.38, -2.97) * mm, "end": v(8.38, -4.63) * mm});
            skArc(sketch, "E840", {"start": v(8.38, -4.63) * mm, "mid": v(8.25, -4.75) * mm, "end": v(8.12, -4.63) * mm});
            skLineSegment(sketch, "E841", {"start": v(8.12, -4.63) * mm, "end": v(8.12, -2.97) * mm});
            skArc(sketch, "E842", {"start": v(8.12, -2.97) * mm, "mid": v(8.25, -2.85) * mm, "end": v(8.38, -2.97) * mm});
            skLineSegment(sketch, "E843", {"start": v(8.88, -2.97) * mm, "end": v(8.88, -4.63) * mm});
            skArc(sketch, "E844", {"start": v(8.88, -4.63) * mm, "mid": v(8.75, -4.75) * mm, "end": v(8.62, -4.63) * mm});
            skLineSegment(sketch, "E845", {"start": v(8.62, -4.63) * mm, "end": v(8.62, -2.97) * mm});
            skArc(sketch, "E846", {"start": v(8.62, -2.97) * mm, "mid": v(8.75, -2.85) * mm, "end": v(8.88, -2.97) * mm});
            skLineSegment(sketch, "E847", {"start": v(9.38, -2.97) * mm, "end": v(9.38, -4.63) * mm});
            skArc(sketch, "E848", {"start": v(9.38, -4.63) * mm, "mid": v(9.25, -4.75) * mm, "end": v(9.12, -4.63) * mm});
            skLineSegment(sketch, "E849", {"start": v(9.12, -4.63) * mm, "end": v(9.12, -2.97) * mm});
            skArc(sketch, "E850", {"start": v(9.12, -2.97) * mm, "mid": v(9.25, -2.85) * mm, "end": v(9.38, -2.97) * mm});
            skLineSegment(sketch, "E851", {"start": v(9.88, -2.97) * mm, "end": v(9.88, -4.63) * mm});
            skArc(sketch, "E852", {"start": v(9.88, -4.63) * mm, "mid": v(9.75, -4.75) * mm, "end": v(9.62, -4.63) * mm});
            skLineSegment(sketch, "E853", {"start": v(9.62, -4.63) * mm, "end": v(9.62, -2.97) * mm});
            skArc(sketch, "E854", {"start": v(9.62, -2.97) * mm, "mid": v(9.75, -2.85) * mm, "end": v(9.88, -2.97) * mm});
            skLineSegment(sketch, "E855", {"start": v(10.38, -2.97) * mm, "end": v(10.38, -4.63) * mm});
            skArc(sketch, "E856", {"start": v(10.38, -4.63) * mm, "mid": v(10.25, -4.75) * mm, "end": v(10.12, -4.63) * mm});
            skLineSegment(sketch, "E857", {"start": v(10.12, -4.63) * mm, "end": v(10.12, -2.97) * mm});
            skArc(sketch, "E858", {"start": v(10.12, -2.97) * mm, "mid": v(10.25, -2.85) * mm, "end": v(10.38, -2.97) * mm});
            skLineSegment(sketch, "E859", {"start": v(10.38, 8.63) * mm, "end": v(10.38, 6.97) * mm});
            skArc(sketch, "E860", {"start": v(10.38, 6.97) * mm, "mid": v(10.25, 6.85) * mm, "end": v(10.12, 6.97) * mm});
            skLineSegment(sketch, "E861", {"start": v(10.12, 6.97) * mm, "end": v(10.12, 8.63) * mm});
            skArc(sketch, "E862", {"start": v(10.12, 8.63) * mm, "mid": v(10.25, 8.75) * mm, "end": v(10.38, 8.63) * mm});
            skLineSegment(sketch, "E863", {"start": v(9.88, 8.63) * mm, "end": v(9.88, 6.97) * mm});
            skArc(sketch, "E864", {"start": v(9.88, 6.97) * mm, "mid": v(9.75, 6.85) * mm, "end": v(9.62, 6.97) * mm});
            skLineSegment(sketch, "E865", {"start": v(9.62, 6.97) * mm, "end": v(9.62, 8.63) * mm});
            skArc(sketch, "E866", {"start": v(9.62, 8.63) * mm, "mid": v(9.75, 8.75) * mm, "end": v(9.88, 8.63) * mm});
            skLineSegment(sketch, "E867", {"start": v(9.38, 8.63) * mm, "end": v(9.38, 6.97) * mm});
            skArc(sketch, "E868", {"start": v(9.38, 6.97) * mm, "mid": v(9.25, 6.85) * mm, "end": v(9.12, 6.97) * mm});
            skLineSegment(sketch, "E869", {"start": v(9.12, 6.97) * mm, "end": v(9.12, 8.63) * mm});
            skArc(sketch, "E870", {"start": v(9.12, 8.63) * mm, "mid": v(9.25, 8.75) * mm, "end": v(9.38, 8.63) * mm});
            skLineSegment(sketch, "E871", {"start": v(8.88, 8.63) * mm, "end": v(8.88, 6.97) * mm});
            skArc(sketch, "E872", {"start": v(8.88, 6.97) * mm, "mid": v(8.75, 6.85) * mm, "end": v(8.62, 6.97) * mm});
            skLineSegment(sketch, "E873", {"start": v(8.62, 6.97) * mm, "end": v(8.62, 8.63) * mm});
            skArc(sketch, "E874", {"start": v(8.62, 8.63) * mm, "mid": v(8.75, 8.75) * mm, "end": v(8.88, 8.63) * mm});
            skLineSegment(sketch, "E875", {"start": v(8.38, 8.63) * mm, "end": v(8.38, 6.97) * mm});
            skArc(sketch, "E876", {"start": v(8.38, 6.97) * mm, "mid": v(8.25, 6.85) * mm, "end": v(8.12, 6.97) * mm});
            skLineSegment(sketch, "E877", {"start": v(8.12, 6.97) * mm, "end": v(8.12, 8.63) * mm});
            skArc(sketch, "E878", {"start": v(8.12, 8.63) * mm, "mid": v(8.25, 8.75) * mm, "end": v(8.38, 8.63) * mm});
            skLineSegment(sketch, "E879", {"start": v(7.88, 8.63) * mm, "end": v(7.88, 6.97) * mm});
            skArc(sketch, "E880", {"start": v(7.88, 6.97) * mm, "mid": v(7.75, 6.85) * mm, "end": v(7.62, 6.97) * mm});
            skLineSegment(sketch, "E881", {"start": v(7.62, 6.97) * mm, "end": v(7.62, 8.63) * mm});
            skArc(sketch, "E882", {"start": v(7.62, 8.63) * mm, "mid": v(7.75, 8.75) * mm, "end": v(7.88, 8.63) * mm});
            skLineSegment(sketch, "E883", {"start": v(7.38, 8.63) * mm, "end": v(7.38, 6.97) * mm});
            skArc(sketch, "E884", {"start": v(7.38, 6.97) * mm, "mid": v(7.25, 6.85) * mm, "end": v(7.12, 6.97) * mm});
            skLineSegment(sketch, "E885", {"start": v(7.12, 6.97) * mm, "end": v(7.12, 8.63) * mm});
            skArc(sketch, "E886", {"start": v(7.12, 8.63) * mm, "mid": v(7.25, 8.75) * mm, "end": v(7.38, 8.63) * mm});
            skLineSegment(sketch, "E887", {"start": v(6.88, 8.63) * mm, "end": v(6.88, 6.97) * mm});
            skArc(sketch, "E888", {"start": v(6.88, 6.97) * mm, "mid": v(6.75, 6.85) * mm, "end": v(6.62, 6.97) * mm});
            skLineSegment(sketch, "E889", {"start": v(6.62, 6.97) * mm, "end": v(6.62, 8.63) * mm});
            skArc(sketch, "E890", {"start": v(6.62, 8.63) * mm, "mid": v(6.75, 8.75) * mm, "end": v(6.88, 8.63) * mm});
            skLineSegment(sketch, "E891", {"start": v(6.38, 8.63) * mm, "end": v(6.38, 6.97) * mm});
            skArc(sketch, "E892", {"start": v(6.38, 6.97) * mm, "mid": v(6.25, 6.85) * mm, "end": v(6.12, 6.97) * mm});
            skLineSegment(sketch, "E893", {"start": v(6.12, 6.97) * mm, "end": v(6.12, 8.63) * mm});
            skArc(sketch, "E894", {"start": v(6.12, 8.63) * mm, "mid": v(6.25, 8.75) * mm, "end": v(6.38, 8.63) * mm});
            skLineSegment(sketch, "E895", {"start": v(5.88, 8.63) * mm, "end": v(5.88, 6.97) * mm});
            skArc(sketch, "E896", {"start": v(5.88, 6.97) * mm, "mid": v(5.75, 6.85) * mm, "end": v(5.62, 6.97) * mm});
            skLineSegment(sketch, "E897", {"start": v(5.62, 6.97) * mm, "end": v(5.62, 8.63) * mm});
            skArc(sketch, "E898", {"start": v(5.62, 8.63) * mm, "mid": v(5.75, 8.75) * mm, "end": v(5.88, 8.63) * mm});
            skLineSegment(sketch, "E899", {"start": v(5.38, 8.63) * mm, "end": v(5.38, 6.97) * mm});
            skArc(sketch, "E900", {"start": v(5.38, 6.97) * mm, "mid": v(5.25, 6.85) * mm, "end": v(5.12, 6.97) * mm});
            skLineSegment(sketch, "E901", {"start": v(5.12, 6.97) * mm, "end": v(5.12, 8.63) * mm});
            skArc(sketch, "E902", {"start": v(5.12, 8.63) * mm, "mid": v(5.25, 8.75) * mm, "end": v(5.38, 8.63) * mm});
            skLineSegment(sketch, "E903", {"start": v(4.88, 8.63) * mm, "end": v(4.88, 6.97) * mm});
            skArc(sketch, "E904", {"start": v(4.88, 6.97) * mm, "mid": v(4.75, 6.85) * mm, "end": v(4.62, 6.97) * mm});
            skLineSegment(sketch, "E905", {"start": v(4.62, 6.97) * mm, "end": v(4.62, 8.63) * mm});
            skArc(sketch, "E906", {"start": v(4.62, 8.63) * mm, "mid": v(4.75, 8.75) * mm, "end": v(4.88, 8.63) * mm});
            skLineSegment(sketch, "E907", {"start": v(4.38, 8.63) * mm, "end": v(4.38, 6.97) * mm});
            skArc(sketch, "E908", {"start": v(4.38, 6.97) * mm, "mid": v(4.25, 6.85) * mm, "end": v(4.12, 6.97) * mm});
            skLineSegment(sketch, "E909", {"start": v(4.12, 6.97) * mm, "end": v(4.12, 8.63) * mm});
            skArc(sketch, "E910", {"start": v(4.12, 8.63) * mm, "mid": v(4.25, 8.75) * mm, "end": v(4.38, 8.63) * mm});
            skLineSegment(sketch, "E911", {"start": v(3.88, 8.63) * mm, "end": v(3.88, 6.97) * mm});
            skArc(sketch, "E912", {"start": v(3.88, 6.97) * mm, "mid": v(3.75, 6.85) * mm, "end": v(3.62, 6.97) * mm});
            skLineSegment(sketch, "E913", {"start": v(3.62, 6.97) * mm, "end": v(3.62, 8.63) * mm});
            skArc(sketch, "E914", {"start": v(3.62, 8.63) * mm, "mid": v(3.75, 8.75) * mm, "end": v(3.88, 8.63) * mm});
            skLineSegment(sketch, "E915", {"start": v(6.4, 2) * mm, "end": v(7.6, 2) * mm});
            skLineSegment(sketch, "E916", {"start": v(7, 2.6) * mm, "end": v(7, 1.4) * mm});
            skLineSegment(sketch, "E917", {"start": v(0, 3.75) * mm, "end": v(-0.5, 3.75) * mm});
            skLineSegment(sketch, "E918", {"start": v(0, -1.25) * mm, "end": v(-0.5, -1.25) * mm});
            skArc(sketch, "E919", {"start": v(0, 5.75) * mm, "mid": v(-0.25, 6) * mm, "end": v(-0.5, 5.75) * mm});
            skArc(sketch, "E920", {"start": v(-0.5, 5.75) * mm, "mid": v(-0.25, 5.5) * mm, "end": v(0, 5.75) * mm});
            skLineSegment(sketch, "E921", {"start": v(7.25, -5) * mm, "end": v(7.25, -5.5) * mm});
            skLineSegment(sketch, "E922", {"start": v(14, -0.75) * mm, "end": v(14.5, -0.75) * mm});
            skLineSegment(sketch, "E923", {"start": v(14, 4.25) * mm, "end": v(14.5, 4.25) * mm});
            skLineSegment(sketch, "E924", {"start": v(3, 6.5) * mm, "end": v(2.5, 6) * mm});
            skLineSegment(sketch, "E925", {"start": v(2.5, 6) * mm, "end": v(2.5, -2.5) * mm});
            skLineSegment(sketch, "E926", {"start": v(2.5, -2.5) * mm, "end": v(11.5, -2.5) * mm});
            skLineSegment(sketch, "E927", {"start": v(11.5, -2.5) * mm, "end": v(11.5, 6.5) * mm});
            skLineSegment(sketch, "E928", {"start": v(11.5, 6.5) * mm, "end": v(3, 6.5) * mm});
            skArc(sketch, "E929", {"start": v(4, 5.5) * mm, "mid": v(3.5, 6) * mm, "end": v(3, 5.5) * mm});
            skArc(sketch, "E930", {"start": v(3, 5.5) * mm, "mid": v(3.5, 5) * mm, "end": v(4, 5.5) * mm});
            skLineSegment(sketch, "E931", {"start": v(0, 1.25) * mm, "end": v(-0.5, 1.5) * mm});
            skLineSegment(sketch, "E932", {"start": v(-0.5, 1.5) * mm, "end": v(-0.5, 1) * mm});
            skLineSegment(sketch, "E933", {"start": v(-0.5, 1) * mm, "end": v(0, 1.25) * mm});
            skLineSegment(sketch, "E934", {"start": v(4.75, -5) * mm, "end": v(4.5, -5.5) * mm});
            skLineSegment(sketch, "E935", {"start": v(4.5, -5.5) * mm, "end": v(5, -5.5) * mm});
            skLineSegment(sketch, "E936", {"start": v(5, -5.5) * mm, "end": v(4.75, -5) * mm});
            skLineSegment(sketch, "E937", {"start": v(9.75, -5) * mm, "end": v(9.5, -5.5) * mm});
            skLineSegment(sketch, "E938", {"start": v(9.5, -5.5) * mm, "end": v(10, -5.5) * mm});
            skLineSegment(sketch, "E939", {"start": v(10, -5.5) * mm, "end": v(9.75, -5) * mm});
            skLineSegment(sketch, "E940", {"start": v(14, 1.75) * mm, "end": v(14.5, 2) * mm});
            skLineSegment(sketch, "E941", {"start": v(14.5, 2) * mm, "end": v(14.5, 1.5) * mm});
            skLineSegment(sketch, "E942", {"start": v(14.5, 1.5) * mm, "end": v(14, 1.75) * mm});
            skLineSegment(sketch, "E943", {"start": v(13.97, -20.8) * mm, "end": v(12.44, -20.8) * mm});
            skArc(sketch, "E944", {"start": v(12.44, -20.8) * mm, "mid": v(12.2, -20.55) * mm, "end": v(12.44, -20.3) * mm});
            skLineSegment(sketch, "E945", {"start": v(12.44, -20.3) * mm, "end": v(13.97, -20.3) * mm});
            skArc(sketch, "E946", {"start": v(13.97, -20.3) * mm, "mid": v(14.22, -20.55) * mm, "end": v(13.97, -20.8) * mm});
            skLineSegment(sketch, "E947", {"start": v(13.97, -22.08) * mm, "end": v(12.44, -22.08) * mm});
            skArc(sketch, "E948", {"start": v(12.44, -22.08) * mm, "mid": v(12.2, -21.82) * mm, "end": v(12.44, -21.57) * mm});
            skLineSegment(sketch, "E949", {"start": v(12.44, -21.57) * mm, "end": v(13.97, -21.57) * mm});
            skArc(sketch, "E950", {"start": v(13.97, -21.57) * mm, "mid": v(14.22, -21.82) * mm, "end": v(13.97, -22.08) * mm});
            skLineSegment(sketch, "E951", {"start": v(13.97, -23.35) * mm, "end": v(12.44, -23.35) * mm});
            skArc(sketch, "E952", {"start": v(12.44, -23.35) * mm, "mid": v(12.2, -23.1) * mm, "end": v(12.44, -22.84) * mm});
            skLineSegment(sketch, "E953", {"start": v(12.44, -22.84) * mm, "end": v(13.97, -22.84) * mm});
            skArc(sketch, "E954", {"start": v(13.97, -22.84) * mm, "mid": v(14.22, -23.1) * mm, "end": v(13.97, -23.35) * mm});
            skLineSegment(sketch, "E955", {"start": v(13.97, -24.62) * mm, "end": v(12.44, -24.62) * mm});
            skArc(sketch, "E956", {"start": v(12.44, -24.62) * mm, "mid": v(12.2, -24.36) * mm, "end": v(12.44, -24.11) * mm});
            skLineSegment(sketch, "E957", {"start": v(12.44, -24.11) * mm, "end": v(13.97, -24.11) * mm});
            skArc(sketch, "E958", {"start": v(13.97, -24.11) * mm, "mid": v(14.22, -24.36) * mm, "end": v(13.97, -24.62) * mm});
            skLineSegment(sketch, "E959", {"start": v(13.97, -25.89) * mm, "end": v(12.44, -25.89) * mm});
            skArc(sketch, "E960", {"start": v(12.44, -25.89) * mm, "mid": v(12.2, -25.64) * mm, "end": v(12.44, -25.38) * mm});
            skLineSegment(sketch, "E961", {"start": v(12.44, -25.38) * mm, "end": v(13.97, -25.38) * mm});
            skArc(sketch, "E962", {"start": v(13.97, -25.38) * mm, "mid": v(14.22, -25.64) * mm, "end": v(13.97, -25.89) * mm});
            skLineSegment(sketch, "E963", {"start": v(13.97, -27.16) * mm, "end": v(12.44, -27.16) * mm});
            skArc(sketch, "E964", {"start": v(12.44, -27.16) * mm, "mid": v(12.2, -26.9) * mm, "end": v(12.44, -26.65) * mm});
            skLineSegment(sketch, "E965", {"start": v(12.44, -26.65) * mm, "end": v(13.97, -26.65) * mm});
            skArc(sketch, "E966", {"start": v(13.97, -26.65) * mm, "mid": v(14.22, -26.9) * mm, "end": v(13.97, -27.16) * mm});
            skLineSegment(sketch, "E967", {"start": v(13.97, -28.43) * mm, "end": v(12.44, -28.43) * mm});
            skArc(sketch, "E968", {"start": v(12.44, -28.43) * mm, "mid": v(12.2, -28.18) * mm, "end": v(12.44, -27.92) * mm});
            skLineSegment(sketch, "E969", {"start": v(12.44, -27.92) * mm, "end": v(13.97, -27.92) * mm});
            skArc(sketch, "E970", {"start": v(13.97, -27.92) * mm, "mid": v(14.22, -28.18) * mm, "end": v(13.97, -28.43) * mm});
            skLineSegment(sketch, "E971", {"start": v(13.97, -29.7) * mm, "end": v(12.44, -29.7) * mm});
            skArc(sketch, "E972", {"start": v(12.44, -29.7) * mm, "mid": v(12.2, -29.45) * mm, "end": v(12.44, -29.2) * mm});
            skLineSegment(sketch, "E973", {"start": v(12.44, -29.2) * mm, "end": v(13.97, -29.2) * mm});
            skArc(sketch, "E974", {"start": v(13.97, -29.2) * mm, "mid": v(14.22, -29.45) * mm, "end": v(13.97, -29.7) * mm});
            skLineSegment(sketch, "E975", {"start": v(19.56, -29.7) * mm, "end": v(18.03, -29.7) * mm});
            skArc(sketch, "E976", {"start": v(18.03, -29.7) * mm, "mid": v(17.78, -29.45) * mm, "end": v(18.03, -29.2) * mm});
            skLineSegment(sketch, "E977", {"start": v(18.03, -29.2) * mm, "end": v(19.56, -29.2) * mm});
            skArc(sketch, "E978", {"start": v(19.56, -29.2) * mm, "mid": v(19.8, -29.45) * mm, "end": v(19.56, -29.7) * mm});
            skLineSegment(sketch, "E979", {"start": v(19.56, -28.43) * mm, "end": v(18.03, -28.43) * mm});
            skArc(sketch, "E980", {"start": v(18.03, -28.43) * mm, "mid": v(17.78, -28.18) * mm, "end": v(18.03, -27.92) * mm});
            skLineSegment(sketch, "E981", {"start": v(18.03, -27.92) * mm, "end": v(19.56, -27.92) * mm});
            skArc(sketch, "E982", {"start": v(19.56, -27.92) * mm, "mid": v(19.8, -28.18) * mm, "end": v(19.56, -28.43) * mm});
            skLineSegment(sketch, "E983", {"start": v(19.56, -27.16) * mm, "end": v(18.03, -27.16) * mm});
            skArc(sketch, "E984", {"start": v(18.03, -27.16) * mm, "mid": v(17.78, -26.9) * mm, "end": v(18.03, -26.65) * mm});
            skLineSegment(sketch, "E985", {"start": v(18.03, -26.65) * mm, "end": v(19.56, -26.65) * mm});
            skArc(sketch, "E986", {"start": v(19.56, -26.65) * mm, "mid": v(19.8, -26.9) * mm, "end": v(19.56, -27.16) * mm});
            skLineSegment(sketch, "E987", {"start": v(19.56, -25.89) * mm, "end": v(18.03, -25.89) * mm});
            skArc(sketch, "E988", {"start": v(18.03, -25.89) * mm, "mid": v(17.78, -25.64) * mm, "end": v(18.03, -25.38) * mm});
            skLineSegment(sketch, "E989", {"start": v(18.03, -25.38) * mm, "end": v(19.56, -25.38) * mm});
            skArc(sketch, "E990", {"start": v(19.56, -25.38) * mm, "mid": v(19.8, -25.64) * mm, "end": v(19.56, -25.89) * mm});
            skLineSegment(sketch, "E991", {"start": v(19.56, -24.62) * mm, "end": v(18.03, -24.62) * mm});
            skArc(sketch, "E992", {"start": v(18.03, -24.62) * mm, "mid": v(17.78, -24.36) * mm, "end": v(18.03, -24.11) * mm});
            skLineSegment(sketch, "E993", {"start": v(18.03, -24.11) * mm, "end": v(19.56, -24.11) * mm});
            skArc(sketch, "E994", {"start": v(19.56, -24.11) * mm, "mid": v(19.8, -24.36) * mm, "end": v(19.56, -24.62) * mm});
            skLineSegment(sketch, "E995", {"start": v(19.56, -23.35) * mm, "end": v(18.03, -23.35) * mm});
            skArc(sketch, "E996", {"start": v(18.03, -23.35) * mm, "mid": v(17.78, -23.1) * mm, "end": v(18.03, -22.84) * mm});
            skLineSegment(sketch, "E997", {"start": v(18.03, -22.84) * mm, "end": v(19.56, -22.84) * mm});
            skArc(sketch, "E998", {"start": v(19.56, -22.84) * mm, "mid": v(19.8, -23.1) * mm, "end": v(19.56, -23.35) * mm});
            skLineSegment(sketch, "E999", {"start": v(19.56, -22.08) * mm, "end": v(18.03, -22.08) * mm});
            skArc(sketch, "E1000", {"start": v(18.03, -22.08) * mm, "mid": v(17.78, -21.82) * mm, "end": v(18.03, -21.57) * mm});
            skLineSegment(sketch, "E1001", {"start": v(18.03, -21.57) * mm, "end": v(19.56, -21.57) * mm});
            skArc(sketch, "E1002", {"start": v(19.56, -21.57) * mm, "mid": v(19.8, -21.82) * mm, "end": v(19.56, -22.08) * mm});
            skLineSegment(sketch, "E1003", {"start": v(19.56, -20.8) * mm, "end": v(18.03, -20.8) * mm});
            skArc(sketch, "E1004", {"start": v(18.03, -20.8) * mm, "mid": v(17.78, -20.55) * mm, "end": v(18.03, -20.3) * mm});
            skLineSegment(sketch, "E1005", {"start": v(18.03, -20.3) * mm, "end": v(19.56, -20.3) * mm});
            skArc(sketch, "E1006", {"start": v(19.56, -20.3) * mm, "mid": v(19.8, -20.55) * mm, "end": v(19.56, -20.8) * mm});
            skLineSegment(sketch, "E1007", {"start": v(12.06, -25.64) * mm, "end": v(11.55, -25.64) * mm});
            skLineSegment(sketch, "E1008", {"start": v(16.63, -19.92) * mm, "end": v(16, -20.55) * mm});
            skLineSegment(sketch, "E1009", {"start": v(16, -20.55) * mm, "end": v(15.37, -19.92) * mm});
            skLineSegment(sketch, "E1010", {"start": v(16, -24.36) * mm, "end": v(16, -25.64) * mm});
            skLineSegment(sketch, "E1011", {"start": v(16.63, -25) * mm, "end": v(15.37, -25) * mm});
            skLineSegment(sketch, "E1012", {"start": v(20.45, -21.82) * mm, "end": v(19.94, -21.82) * mm});
            skArc(sketch, "E1013", {"start": v(12.06, -20.55) * mm, "mid": v(11.8, -20.3) * mm, "end": v(11.55, -20.55) * mm});
            skArc(sketch, "E1014", {"start": v(11.55, -20.55) * mm, "mid": v(11.8, -20.8) * mm, "end": v(12.06, -20.55) * mm});
            skLineSegment(sketch, "E1015", {"start": v(19.94, -28.18) * mm, "end": v(20.45, -27.92) * mm});
            skLineSegment(sketch, "E1016", {"start": v(20.45, -27.92) * mm, "end": v(20.45, -28.43) * mm});
            skLineSegment(sketch, "E1017", {"start": v(20.45, -28.43) * mm, "end": v(19.94, -28.18) * mm});
            skLineSegment(sketch, "E1018", {"start": v(14.6, -19.92) * mm, "end": v(17.4, -19.92) * mm});
            skLineSegment(sketch, "E1019", {"start": v(17.4, -19.92) * mm, "end": v(17.4, -30.08) * mm});
            skLineSegment(sketch, "E1020", {"start": v(17.4, -30.08) * mm, "end": v(14.6, -30.08) * mm});
            skLineSegment(sketch, "E1021", {"start": v(14.6, -30.08) * mm, "end": v(14.6, -19.92) * mm});
            skLineSegment(sketch, "E1022", {"start": v(1.6, 13.05) * mm, "end": v(-0.4, 13.05) * mm});
            skLineSegment(sketch, "E1023", {"start": v(-0.4, 13.05) * mm, "end": v(-0.4, 14.35) * mm});
            skLineSegment(sketch, "E1024", {"start": v(-0.4, 14.35) * mm, "end": v(1.6, 14.35) * mm});
            skLineSegment(sketch, "E1025", {"start": v(1.6, 14.35) * mm, "end": v(1.6, 13.05) * mm});
            skLineSegment(sketch, "E1026", {"start": v(-1.6, 13.05) * mm, "end": v(-3.6, 13.05) * mm});
            skLineSegment(sketch, "E1027", {"start": v(-3.6, 13.05) * mm, "end": v(-3.6, 14.35) * mm});
            skLineSegment(sketch, "E1028", {"start": v(-3.6, 14.35) * mm, "end": v(-1.6, 14.35) * mm});
            skLineSegment(sketch, "E1029", {"start": v(-1.6, 14.35) * mm, "end": v(-1.6, 13.05) * mm});
            skLineSegment(sketch, "E1030", {"start": v(-1.6, 18.65) * mm, "end": v(-3.6, 18.65) * mm});
            skLineSegment(sketch, "E1031", {"start": v(-3.6, 18.65) * mm, "end": v(-3.6, 19.95) * mm});
            skLineSegment(sketch, "E1032", {"start": v(-3.6, 19.95) * mm, "end": v(-1.6, 19.95) * mm});
            skLineSegment(sketch, "E1033", {"start": v(-1.6, 19.95) * mm, "end": v(-1.6, 18.65) * mm});
            skLineSegment(sketch, "E1034", {"start": v(1.6, 18.65) * mm, "end": v(-0.4, 18.65) * mm});
            skLineSegment(sketch, "E1035", {"start": v(-0.4, 18.65) * mm, "end": v(-0.4, 19.95) * mm});
            skLineSegment(sketch, "E1036", {"start": v(-0.4, 19.95) * mm, "end": v(1.6, 19.95) * mm});
            skLineSegment(sketch, "E1037", {"start": v(1.6, 19.95) * mm, "end": v(1.6, 18.65) * mm});
            skLineSegment(sketch, "E1038", {"start": v(-3, 12.9) * mm, "end": v(-3, 12.5) * mm});
            skLineSegment(sketch, "E1039", {"start": v(-3, 12.5) * mm, "end": v(1, 12.5) * mm});
            skLineSegment(sketch, "E1040", {"start": v(1, 12.5) * mm, "end": v(1, 12.9) * mm});
            skLineSegment(sketch, "E1041", {"start": v(-3, 14.5) * mm, "end": v(-3, 18.5) * mm});
            skLineSegment(sketch, "E1042", {"start": v(-3, 20.1) * mm, "end": v(-3, 20.5) * mm});
            skLineSegment(sketch, "E1043", {"start": v(-3, 20.5) * mm, "end": v(1, 20.5) * mm});
            skLineSegment(sketch, "E1044", {"start": v(1, 20.5) * mm, "end": v(1, 20.1) * mm});
            skLineSegment(sketch, "E1045", {"start": v(1, 18.5) * mm, "end": v(1, 14.5) * mm});
            skLineSegment(sketch, "E1046", {"start": v(-1, 16) * mm, "end": v(-1, 17) * mm});
            skLineSegment(sketch, "E1047", {"start": v(-1.5, 16.5) * mm, "end": v(-0.5, 16.5) * mm});
            skLineSegment(sketch, "E1048", {"start": v(-1.25, 14.75) * mm, "end": v(-0.75, 14.75) * mm});
            skLineSegment(sketch, "E1049", {"start": v(-0.75, 14.75) * mm, "end": v(-0.75, 15.75) * mm});
            skLineSegment(sketch, "E1050", {"start": v(-0.75, 15.75) * mm, "end": v(-1.25, 15.75) * mm});
            skLineSegment(sketch, "E1051", {"start": v(-1.25, 15.75) * mm, "end": v(-1.25, 14.75) * mm});
            skLineSegment(sketch, "E1052", {"start": v(-1.63, 14.75) * mm, "end": v(-1.63, 15.75) * mm});
            skLineSegment(sketch, "E1053", {"start": v(-0.38, 14.75) * mm, "end": v(-0.38, 15.75) * mm});
            skLineSegment(sketch, "E1054", {"start": v(-0.38, 15.25) * mm, "end": v(0.5, 15.25) * mm});
            skLineSegment(sketch, "E1055", {"start": v(0.5, 15.25) * mm, "end": v(0.5, 14.5) * mm});
            skLineSegment(sketch, "E1056", {"start": v(-1.63, 15.25) * mm, "end": v(-2.5, 15.25) * mm});
            skLineSegment(sketch, "E1057", {"start": v(-2.5, 15.25) * mm, "end": v(-2.5, 14.5) * mm});
            skLineSegment(sketch, "E1058", {"start": v(25, 3.75) * mm, "end": v(26, 3.75) * mm});
            skLineSegment(sketch, "E1059", {"start": v(26, 3.75) * mm, "end": v(26, 2.75) * mm});
            skLineSegment(sketch, "E1060", {"start": v(26, 2.75) * mm, "end": v(25, 2.75) * mm});
            skLineSegment(sketch, "E1061", {"start": v(25, 2.75) * mm, "end": v(25, 3.75) * mm});
            skLineSegment(sketch, "E1062", {"start": v(25, 2.25) * mm, "end": v(26, 2.25) * mm});
            skLineSegment(sketch, "E1063", {"start": v(26, 2.25) * mm, "end": v(26, 1.25) * mm});
            skLineSegment(sketch, "E1064", {"start": v(26, 1.25) * mm, "end": v(25, 1.25) * mm});
            skLineSegment(sketch, "E1065", {"start": v(25, 1.25) * mm, "end": v(25, 2.25) * mm});
            skLineSegment(sketch, "E1066", {"start": v(26.2, 2.7) * mm, "end": v(26.2, 4) * mm});
            skLineSegment(sketch, "E1067", {"start": v(26.2, 4) * mm, "end": v(24.8, 4) * mm});
            skLineSegment(sketch, "E1068", {"start": v(24.8, 4) * mm, "end": v(24.8, 2.7) * mm});
            skArc(sketch, "E1069", {"start": v(24.8, 2.7) * mm, "mid": v(25, 2.5) * mm, "end": v(24.8, 2.3) * mm});
            skArc(sketch, "E1070", {"start": v(25.6, 2.5) * mm, "mid": v(25.5, 2.6) * mm, "end": v(25.4, 2.5) * mm});
            skArc(sketch, "E1071", {"start": v(25.4, 2.5) * mm, "mid": v(25.5, 2.4) * mm, "end": v(25.6, 2.5) * mm});
            skArc(sketch, "E1072", {"start": v(26.2, 2.7) * mm, "mid": v(26, 2.5) * mm, "end": v(26.2, 2.3) * mm});
            skLineSegment(sketch, "E1073", {"start": v(24.8, 2.3) * mm, "end": v(24.8, 1) * mm});
            skLineSegment(sketch, "E1074", {"start": v(24.8, 1) * mm, "end": v(26.2, 1) * mm});
            skLineSegment(sketch, "E1075", {"start": v(26.2, 1) * mm, "end": v(26.2, 2.3) * mm});
            skLineSegment(sketch, "E1076", {"start": v(-26.75, 33.75) * mm, "end": v(-26.75, 34.75) * mm});
            skLineSegment(sketch, "E1077", {"start": v(-26.75, 34.75) * mm, "end": v(-25.75, 34.75) * mm});
            skLineSegment(sketch, "E1078", {"start": v(-25.75, 34.75) * mm, "end": v(-25.75, 33.75) * mm});
            skLineSegment(sketch, "E1079", {"start": v(-25.75, 33.75) * mm, "end": v(-26.75, 33.75) * mm});
            skLineSegment(sketch, "E1080", {"start": v(-25.25, 33.75) * mm, "end": v(-25.25, 34.75) * mm});
            skLineSegment(sketch, "E1081", {"start": v(-25.25, 34.75) * mm, "end": v(-24.25, 34.75) * mm});
            skLineSegment(sketch, "E1082", {"start": v(-24.25, 34.75) * mm, "end": v(-24.25, 33.75) * mm});
            skLineSegment(sketch, "E1083", {"start": v(-24.25, 33.75) * mm, "end": v(-25.25, 33.75) * mm});
            skLineSegment(sketch, "E1084", {"start": v(-25.7, 34.95) * mm, "end": v(-27, 34.95) * mm});
            skLineSegment(sketch, "E1085", {"start": v(-27, 34.95) * mm, "end": v(-27, 33.55) * mm});
            skLineSegment(sketch, "E1086", {"start": v(-27, 33.55) * mm, "end": v(-25.7, 33.55) * mm});
            skArc(sketch, "E1087", {"start": v(-25.7, 33.55) * mm, "mid": v(-25.5, 33.75) * mm, "end": v(-25.3, 33.55) * mm});
            skArc(sketch, "E1088", {"start": v(-25.4, 34.25) * mm, "mid": v(-25.5, 34.35) * mm, "end": v(-25.6, 34.25) * mm});
            skArc(sketch, "E1089", {"start": v(-25.6, 34.25) * mm, "mid": v(-25.5, 34.15) * mm, "end": v(-25.4, 34.25) * mm});
            skArc(sketch, "E1090", {"start": v(-25.7, 34.95) * mm, "mid": v(-25.5, 34.75) * mm, "end": v(-25.3, 34.95) * mm});
            skLineSegment(sketch, "E1091", {"start": v(-25.3, 33.55) * mm, "end": v(-24, 33.55) * mm});
            skLineSegment(sketch, "E1092", {"start": v(-24, 33.55) * mm, "end": v(-24, 34.95) * mm});
            skLineSegment(sketch, "E1093", {"start": v(-24, 34.95) * mm, "end": v(-25.3, 34.95) * mm});
            skLineSegment(sketch, "E1094", {"start": v(-9.75, 21.5) * mm, "end": v(-9.75, 22.5) * mm});
            skLineSegment(sketch, "E1095", {"start": v(-9.75, 22.5) * mm, "end": v(-8.75, 22.5) * mm});
            skLineSegment(sketch, "E1096", {"start": v(-8.75, 22.5) * mm, "end": v(-8.75, 21.5) * mm});
            skLineSegment(sketch, "E1097", {"start": v(-8.75, 21.5) * mm, "end": v(-9.75, 21.5) * mm});
            skLineSegment(sketch, "E1098", {"start": v(-8.25, 21.5) * mm, "end": v(-8.25, 22.5) * mm});
            skLineSegment(sketch, "E1099", {"start": v(-8.25, 22.5) * mm, "end": v(-7.25, 22.5) * mm});
            skLineSegment(sketch, "E1100", {"start": v(-7.25, 22.5) * mm, "end": v(-7.25, 21.5) * mm});
            skLineSegment(sketch, "E1101", {"start": v(-7.25, 21.5) * mm, "end": v(-8.25, 21.5) * mm});
            skLineSegment(sketch, "E1102", {"start": v(-8.7, 22.7) * mm, "end": v(-10, 22.7) * mm});
            skLineSegment(sketch, "E1103", {"start": v(-10, 22.7) * mm, "end": v(-10, 21.3) * mm});
            skLineSegment(sketch, "E1104", {"start": v(-10, 21.3) * mm, "end": v(-8.7, 21.3) * mm});
            skArc(sketch, "E1105", {"start": v(-8.7, 21.3) * mm, "mid": v(-8.5, 21.5) * mm, "end": v(-8.3, 21.3) * mm});
            skArc(sketch, "E1106", {"start": v(-8.4, 22) * mm, "mid": v(-8.5, 22.1) * mm, "end": v(-8.6, 22) * mm});
            skArc(sketch, "E1107", {"start": v(-8.6, 22) * mm, "mid": v(-8.5, 21.9) * mm, "end": v(-8.4, 22) * mm});
            skArc(sketch, "E1108", {"start": v(-8.7, 22.7) * mm, "mid": v(-8.5, 22.5) * mm, "end": v(-8.3, 22.7) * mm});
            skLineSegment(sketch, "E1109", {"start": v(-8.3, 21.3) * mm, "end": v(-7, 21.3) * mm});
            skLineSegment(sketch, "E1110", {"start": v(-7, 21.3) * mm, "end": v(-7, 22.7) * mm});
            skLineSegment(sketch, "E1111", {"start": v(-7, 22.7) * mm, "end": v(-8.3, 22.7) * mm});
            skLineSegment(sketch, "E1112", {"start": v(-12.25, -7) * mm, "end": v(-12.25, -6) * mm});
            skLineSegment(sketch, "E1113", {"start": v(-12.25, -6) * mm, "end": v(-11.25, -6) * mm});
            skLineSegment(sketch, "E1114", {"start": v(-11.25, -6) * mm, "end": v(-11.25, -7) * mm});
            skLineSegment(sketch, "E1115", {"start": v(-11.25, -7) * mm, "end": v(-12.25, -7) * mm});
            skLineSegment(sketch, "E1116", {"start": v(-10.75, -7) * mm, "end": v(-10.75, -6) * mm});
            skLineSegment(sketch, "E1117", {"start": v(-10.75, -6) * mm, "end": v(-9.75, -6) * mm});
            skLineSegment(sketch, "E1118", {"start": v(-9.75, -6) * mm, "end": v(-9.75, -7) * mm});
            skLineSegment(sketch, "E1119", {"start": v(-9.75, -7) * mm, "end": v(-10.75, -7) * mm});
            skLineSegment(sketch, "E1120", {"start": v(-11.2, -5.8) * mm, "end": v(-12.5, -5.8) * mm});
            skLineSegment(sketch, "E1121", {"start": v(-12.5, -5.8) * mm, "end": v(-12.5, -7.2) * mm});
            skLineSegment(sketch, "E1122", {"start": v(-12.5, -7.2) * mm, "end": v(-11.2, -7.2) * mm});
            skArc(sketch, "E1123", {"start": v(-11.2, -7.2) * mm, "mid": v(-11, -7) * mm, "end": v(-10.8, -7.2) * mm});
            skArc(sketch, "E1124", {"start": v(-10.9, -6.5) * mm, "mid": v(-11, -6.4) * mm, "end": v(-11.1, -6.5) * mm});
            skArc(sketch, "E1125", {"start": v(-11.1, -6.5) * mm, "mid": v(-11, -6.6) * mm, "end": v(-10.9, -6.5) * mm});
            skArc(sketch, "E1126", {"start": v(-11.2, -5.8) * mm, "mid": v(-11, -6) * mm, "end": v(-10.8, -5.8) * mm});
            skLineSegment(sketch, "E1127", {"start": v(-10.8, -7.2) * mm, "end": v(-9.5, -7.2) * mm});
            skLineSegment(sketch, "E1128", {"start": v(-9.5, -7.2) * mm, "end": v(-9.5, -5.8) * mm});
            skLineSegment(sketch, "E1129", {"start": v(-9.5, -5.8) * mm, "end": v(-10.8, -5.8) * mm});
            skLineSegment(sketch, "E1130", {"start": v(-1.25, -40) * mm, "end": v(-1.25, -41) * mm});
            skLineSegment(sketch, "E1131", {"start": v(-1.25, -41) * mm, "end": v(-2.25, -41) * mm});
            skLineSegment(sketch, "E1132", {"start": v(-2.25, -41) * mm, "end": v(-2.25, -40) * mm});
            skLineSegment(sketch, "E1133", {"start": v(-2.25, -40) * mm, "end": v(-1.25, -40) * mm});
            skLineSegment(sketch, "E1134", {"start": v(-2.75, -40) * mm, "end": v(-2.75, -41) * mm});
            skLineSegment(sketch, "E1135", {"start": v(-2.75, -41) * mm, "end": v(-3.75, -41) * mm});
            skLineSegment(sketch, "E1136", {"start": v(-3.75, -41) * mm, "end": v(-3.75, -40) * mm});
            skLineSegment(sketch, "E1137", {"start": v(-3.75, -40) * mm, "end": v(-2.75, -40) * mm});
            skLineSegment(sketch, "E1138", {"start": v(-2.3, -41.2) * mm, "end": v(-1, -41.2) * mm});
            skLineSegment(sketch, "E1139", {"start": v(-1, -41.2) * mm, "end": v(-1, -39.8) * mm});
            skLineSegment(sketch, "E1140", {"start": v(-1, -39.8) * mm, "end": v(-2.3, -39.8) * mm});
            skArc(sketch, "E1141", {"start": v(-2.3, -39.8) * mm, "mid": v(-2.5, -40) * mm, "end": v(-2.7, -39.8) * mm});
            skArc(sketch, "E1142", {"start": v(-2.4, -40.5) * mm, "mid": v(-2.5, -40.4) * mm, "end": v(-2.6, -40.5) * mm});
            skArc(sketch, "E1143", {"start": v(-2.6, -40.5) * mm, "mid": v(-2.5, -40.6) * mm, "end": v(-2.4, -40.5) * mm});
            skArc(sketch, "E1144", {"start": v(-2.3, -41.2) * mm, "mid": v(-2.5, -41) * mm, "end": v(-2.7, -41.2) * mm});
            skLineSegment(sketch, "E1145", {"start": v(-2.7, -39.8) * mm, "end": v(-4, -39.8) * mm});
            skLineSegment(sketch, "E1146", {"start": v(-4, -39.8) * mm, "end": v(-4, -41.2) * mm});
            skLineSegment(sketch, "E1147", {"start": v(-4, -41.2) * mm, "end": v(-2.7, -41.2) * mm});
            skLineSegment(sketch, "E1148", {"start": v(-5.75, -17) * mm, "end": v(-5.75, -18) * mm});
            skLineSegment(sketch, "E1149", {"start": v(-5.75, -18) * mm, "end": v(-6.75, -18) * mm});
            skLineSegment(sketch, "E1150", {"start": v(-6.75, -18) * mm, "end": v(-6.75, -17) * mm});
            skLineSegment(sketch, "E1151", {"start": v(-6.75, -17) * mm, "end": v(-5.75, -17) * mm});
            skLineSegment(sketch, "E1152", {"start": v(-7.25, -17) * mm, "end": v(-7.25, -18) * mm});
            skLineSegment(sketch, "E1153", {"start": v(-7.25, -18) * mm, "end": v(-8.25, -18) * mm});
            skLineSegment(sketch, "E1154", {"start": v(-8.25, -18) * mm, "end": v(-8.25, -17) * mm});
            skLineSegment(sketch, "E1155", {"start": v(-8.25, -17) * mm, "end": v(-7.25, -17) * mm});
            skLineSegment(sketch, "E1156", {"start": v(-6.8, -18.2) * mm, "end": v(-5.5, -18.2) * mm});
            skLineSegment(sketch, "E1157", {"start": v(-5.5, -18.2) * mm, "end": v(-5.5, -16.8) * mm});
            skLineSegment(sketch, "E1158", {"start": v(-5.5, -16.8) * mm, "end": v(-6.8, -16.8) * mm});
            skArc(sketch, "E1159", {"start": v(-6.8, -16.8) * mm, "mid": v(-7, -17) * mm, "end": v(-7.2, -16.8) * mm});
            skArc(sketch, "E1160", {"start": v(-6.9, -17.5) * mm, "mid": v(-7, -17.4) * mm, "end": v(-7.1, -17.5) * mm});
            skArc(sketch, "E1161", {"start": v(-7.1, -17.5) * mm, "mid": v(-7, -17.6) * mm, "end": v(-6.9, -17.5) * mm});
            skArc(sketch, "E1162", {"start": v(-6.8, -18.2) * mm, "mid": v(-7, -18) * mm, "end": v(-7.2, -18.2) * mm});
            skLineSegment(sketch, "E1163", {"start": v(-7.2, -16.8) * mm, "end": v(-8.5, -16.8) * mm});
            skLineSegment(sketch, "E1164", {"start": v(-8.5, -16.8) * mm, "end": v(-8.5, -18.2) * mm});
            skLineSegment(sketch, "E1165", {"start": v(-8.5, -18.2) * mm, "end": v(-7.2, -18.2) * mm});
            skLineSegment(sketch, "E1166", {"start": v(-21.5, 33) * mm, "end": v(-20.5, 33) * mm});
            skLineSegment(sketch, "E1167", {"start": v(-20.5, 33) * mm, "end": v(-20.5, 32) * mm});
            skLineSegment(sketch, "E1168", {"start": v(-20.5, 32) * mm, "end": v(-21.5, 32) * mm});
            skLineSegment(sketch, "E1169", {"start": v(-21.5, 32) * mm, "end": v(-21.5, 33) * mm});
            skLineSegment(sketch, "E1170", {"start": v(-21.5, 31.5) * mm, "end": v(-20.5, 31.5) * mm});
            skLineSegment(sketch, "E1171", {"start": v(-20.5, 31.5) * mm, "end": v(-20.5, 30.5) * mm});
            skLineSegment(sketch, "E1172", {"start": v(-20.5, 30.5) * mm, "end": v(-21.5, 30.5) * mm});
            skLineSegment(sketch, "E1173", {"start": v(-21.5, 30.5) * mm, "end": v(-21.5, 31.5) * mm});
            skLineSegment(sketch, "E1174", {"start": v(-20.3, 31.95) * mm, "end": v(-20.3, 33.25) * mm});
            skLineSegment(sketch, "E1175", {"start": v(-20.3, 33.25) * mm, "end": v(-21.7, 33.25) * mm});
            skLineSegment(sketch, "E1176", {"start": v(-21.7, 33.25) * mm, "end": v(-21.7, 31.95) * mm});
            skArc(sketch, "E1177", {"start": v(-21.7, 31.95) * mm, "mid": v(-21.5, 31.75) * mm, "end": v(-21.7, 31.55) * mm});
            skArc(sketch, "E1178", {"start": v(-20.9, 31.75) * mm, "mid": v(-21, 31.85) * mm, "end": v(-21.1, 31.75) * mm});
            skArc(sketch, "E1179", {"start": v(-21.1, 31.75) * mm, "mid": v(-21, 31.65) * mm, "end": v(-20.9, 31.75) * mm});
            skArc(sketch, "E1180", {"start": v(-20.3, 31.95) * mm, "mid": v(-20.5, 31.75) * mm, "end": v(-20.3, 31.55) * mm});
            skLineSegment(sketch, "E1181", {"start": v(-21.7, 31.55) * mm, "end": v(-21.7, 30.25) * mm});
            skLineSegment(sketch, "E1182", {"start": v(-21.7, 30.25) * mm, "end": v(-20.3, 30.25) * mm});
            skLineSegment(sketch, "E1183", {"start": v(-20.3, 30.25) * mm, "end": v(-20.3, 31.55) * mm});
            skLineSegment(sketch, "E1184", {"start": v(-20.5, 27.25) * mm, "end": v(-21.5, 27.25) * mm});
            skLineSegment(sketch, "E1185", {"start": v(-21.5, 27.25) * mm, "end": v(-21.5, 28.25) * mm});
            skLineSegment(sketch, "E1186", {"start": v(-21.5, 28.25) * mm, "end": v(-20.5, 28.25) * mm});
            skLineSegment(sketch, "E1187", {"start": v(-20.5, 28.25) * mm, "end": v(-20.5, 27.25) * mm});
            skLineSegment(sketch, "E1188", {"start": v(-20.5, 28.75) * mm, "end": v(-21.5, 28.75) * mm});
            skLineSegment(sketch, "E1189", {"start": v(-21.5, 28.75) * mm, "end": v(-21.5, 29.75) * mm});
            skLineSegment(sketch, "E1190", {"start": v(-21.5, 29.75) * mm, "end": v(-20.5, 29.75) * mm});
            skLineSegment(sketch, "E1191", {"start": v(-20.5, 29.75) * mm, "end": v(-20.5, 28.75) * mm});
            skLineSegment(sketch, "E1192", {"start": v(-21.7, 28.3) * mm, "end": v(-21.7, 27) * mm});
            skLineSegment(sketch, "E1193", {"start": v(-21.7, 27) * mm, "end": v(-20.3, 27) * mm});
            skLineSegment(sketch, "E1194", {"start": v(-20.3, 27) * mm, "end": v(-20.3, 28.3) * mm});
            skArc(sketch, "E1195", {"start": v(-20.3, 28.3) * mm, "mid": v(-20.5, 28.5) * mm, "end": v(-20.3, 28.7) * mm});
            skArc(sketch, "E1196", {"start": v(-20.9, 28.5) * mm, "mid": v(-21, 28.6) * mm, "end": v(-21.1, 28.5) * mm});
            skArc(sketch, "E1197", {"start": v(-21.1, 28.5) * mm, "mid": v(-21, 28.4) * mm, "end": v(-20.9, 28.5) * mm});
            skArc(sketch, "E1198", {"start": v(-21.7, 28.3) * mm, "mid": v(-21.5, 28.5) * mm, "end": v(-21.7, 28.7) * mm});
            skLineSegment(sketch, "E1199", {"start": v(-20.3, 28.7) * mm, "end": v(-20.3, 30) * mm});
            skLineSegment(sketch, "E1200", {"start": v(-20.3, 30) * mm, "end": v(-21.7, 30) * mm});
            skLineSegment(sketch, "E1201", {"start": v(-21.7, 30) * mm, "end": v(-21.7, 28.7) * mm});
            skLineSegment(sketch, "E1202", {"start": v(-21.5, 17) * mm, "end": v(-20.5, 17) * mm});
            skLineSegment(sketch, "E1203", {"start": v(-20.5, 17) * mm, "end": v(-20.5, 16) * mm});
            skLineSegment(sketch, "E1204", {"start": v(-20.5, 16) * mm, "end": v(-21.5, 16) * mm});
            skLineSegment(sketch, "E1205", {"start": v(-21.5, 16) * mm, "end": v(-21.5, 17) * mm});
            skLineSegment(sketch, "E1206", {"start": v(-21.5, 15.5) * mm, "end": v(-20.5, 15.5) * mm});
            skLineSegment(sketch, "E1207", {"start": v(-20.5, 15.5) * mm, "end": v(-20.5, 14.5) * mm});
            skLineSegment(sketch, "E1208", {"start": v(-20.5, 14.5) * mm, "end": v(-21.5, 14.5) * mm});
            skLineSegment(sketch, "E1209", {"start": v(-21.5, 14.5) * mm, "end": v(-21.5, 15.5) * mm});
            skLineSegment(sketch, "E1210", {"start": v(-20.3, 15.95) * mm, "end": v(-20.3, 17.25) * mm});
            skLineSegment(sketch, "E1211", {"start": v(-20.3, 17.25) * mm, "end": v(-21.7, 17.25) * mm});
            skLineSegment(sketch, "E1212", {"start": v(-21.7, 17.25) * mm, "end": v(-21.7, 15.95) * mm});
            skArc(sketch, "E1213", {"start": v(-21.7, 15.95) * mm, "mid": v(-21.5, 15.75) * mm, "end": v(-21.7, 15.55) * mm});
            skArc(sketch, "E1214", {"start": v(-20.9, 15.75) * mm, "mid": v(-21, 15.85) * mm, "end": v(-21.1, 15.75) * mm});
            skArc(sketch, "E1215", {"start": v(-21.1, 15.75) * mm, "mid": v(-21, 15.65) * mm, "end": v(-20.9, 15.75) * mm});
            skArc(sketch, "E1216", {"start": v(-20.3, 15.95) * mm, "mid": v(-20.5, 15.75) * mm, "end": v(-20.3, 15.55) * mm});
            skLineSegment(sketch, "E1217", {"start": v(-21.7, 15.55) * mm, "end": v(-21.7, 14.25) * mm});
            skLineSegment(sketch, "E1218", {"start": v(-21.7, 14.25) * mm, "end": v(-20.3, 14.25) * mm});
            skLineSegment(sketch, "E1219", {"start": v(-20.3, 14.25) * mm, "end": v(-20.3, 15.55) * mm});
            skLineSegment(sketch, "E1220", {"start": v(-20.5, 11.25) * mm, "end": v(-21.5, 11.25) * mm});
            skLineSegment(sketch, "E1221", {"start": v(-21.5, 11.25) * mm, "end": v(-21.5, 12.25) * mm});
            skLineSegment(sketch, "E1222", {"start": v(-21.5, 12.25) * mm, "end": v(-20.5, 12.25) * mm});
            skLineSegment(sketch, "E1223", {"start": v(-20.5, 12.25) * mm, "end": v(-20.5, 11.25) * mm});
            skLineSegment(sketch, "E1224", {"start": v(-20.5, 12.75) * mm, "end": v(-21.5, 12.75) * mm});
            skLineSegment(sketch, "E1225", {"start": v(-21.5, 12.75) * mm, "end": v(-21.5, 13.75) * mm});
            skLineSegment(sketch, "E1226", {"start": v(-21.5, 13.75) * mm, "end": v(-20.5, 13.75) * mm});
            skLineSegment(sketch, "E1227", {"start": v(-20.5, 13.75) * mm, "end": v(-20.5, 12.75) * mm});
            skLineSegment(sketch, "E1228", {"start": v(-21.7, 12.3) * mm, "end": v(-21.7, 11) * mm});
            skLineSegment(sketch, "E1229", {"start": v(-21.7, 11) * mm, "end": v(-20.3, 11) * mm});
            skLineSegment(sketch, "E1230", {"start": v(-20.3, 11) * mm, "end": v(-20.3, 12.3) * mm});
            skArc(sketch, "E1231", {"start": v(-20.3, 12.3) * mm, "mid": v(-20.5, 12.5) * mm, "end": v(-20.3, 12.7) * mm});
            skArc(sketch, "E1232", {"start": v(-20.9, 12.5) * mm, "mid": v(-21, 12.6) * mm, "end": v(-21.1, 12.5) * mm});
            skArc(sketch, "E1233", {"start": v(-21.1, 12.5) * mm, "mid": v(-21, 12.4) * mm, "end": v(-20.9, 12.5) * mm});
            skArc(sketch, "E1234", {"start": v(-21.7, 12.3) * mm, "mid": v(-21.5, 12.5) * mm, "end": v(-21.7, 12.7) * mm});
            skLineSegment(sketch, "E1235", {"start": v(-20.3, 12.7) * mm, "end": v(-20.3, 14) * mm});
            skLineSegment(sketch, "E1236", {"start": v(-20.3, 14) * mm, "end": v(-21.7, 14) * mm});
            skLineSegment(sketch, "E1237", {"start": v(-21.7, 14) * mm, "end": v(-21.7, 12.7) * mm});
            skLineSegment(sketch, "E1238", {"start": v(-21.5, 1) * mm, "end": v(-20.5, 1) * mm});
            skLineSegment(sketch, "E1239", {"start": v(-20.5, 1) * mm, "end": v(-20.5, 0) * mm});
            skLineSegment(sketch, "E1240", {"start": v(-20.5, 0) * mm, "end": v(-21.5, 0) * mm});
            skLineSegment(sketch, "E1241", {"start": v(-21.5, 0) * mm, "end": v(-21.5, 1) * mm});
            skLineSegment(sketch, "E1242", {"start": v(-21.5, -0.5) * mm, "end": v(-20.5, -0.5) * mm});
            skLineSegment(sketch, "E1243", {"start": v(-20.5, -0.5) * mm, "end": v(-20.5, -1.5) * mm});
            skLineSegment(sketch, "E1244", {"start": v(-20.5, -1.5) * mm, "end": v(-21.5, -1.5) * mm});
            skLineSegment(sketch, "E1245", {"start": v(-21.5, -1.5) * mm, "end": v(-21.5, -0.5) * mm});
            skLineSegment(sketch, "E1246", {"start": v(-20.3, -0.05) * mm, "end": v(-20.3, 1.25) * mm});
            skLineSegment(sketch, "E1247", {"start": v(-20.3, 1.25) * mm, "end": v(-21.7, 1.25) * mm});
            skLineSegment(sketch, "E1248", {"start": v(-21.7, 1.25) * mm, "end": v(-21.7, -0.05) * mm});
            skArc(sketch, "E1249", {"start": v(-21.7, -0.05) * mm, "mid": v(-21.5, -0.25) * mm, "end": v(-21.7, -0.45) * mm});
            skArc(sketch, "E1250", {"start": v(-20.9, -0.25) * mm, "mid": v(-21, -0.15) * mm, "end": v(-21.1, -0.25) * mm});
            skArc(sketch, "E1251", {"start": v(-21.1, -0.25) * mm, "mid": v(-21, -0.35) * mm, "end": v(-20.9, -0.25) * mm});
            skArc(sketch, "E1252", {"start": v(-20.3, -0.05) * mm, "mid": v(-20.5, -0.25) * mm, "end": v(-20.3, -0.45) * mm});
            skLineSegment(sketch, "E1253", {"start": v(-21.7, -0.45) * mm, "end": v(-21.7, -1.75) * mm});
            skLineSegment(sketch, "E1254", {"start": v(-21.7, -1.75) * mm, "end": v(-20.3, -1.75) * mm});
            skLineSegment(sketch, "E1255", {"start": v(-20.3, -1.75) * mm, "end": v(-20.3, -0.45) * mm});
            skLineSegment(sketch, "E1256", {"start": v(-20.5, -4.75) * mm, "end": v(-21.5, -4.75) * mm});
            skLineSegment(sketch, "E1257", {"start": v(-21.5, -4.75) * mm, "end": v(-21.5, -3.75) * mm});
            skLineSegment(sketch, "E1258", {"start": v(-21.5, -3.75) * mm, "end": v(-20.5, -3.75) * mm});
            skLineSegment(sketch, "E1259", {"start": v(-20.5, -3.75) * mm, "end": v(-20.5, -4.75) * mm});
            skLineSegment(sketch, "E1260", {"start": v(-20.5, -3.25) * mm, "end": v(-21.5, -3.25) * mm});
            skLineSegment(sketch, "E1261", {"start": v(-21.5, -3.25) * mm, "end": v(-21.5, -2.25) * mm});
            skLineSegment(sketch, "E1262", {"start": v(-21.5, -2.25) * mm, "end": v(-20.5, -2.25) * mm});
            skLineSegment(sketch, "E1263", {"start": v(-20.5, -2.25) * mm, "end": v(-20.5, -3.25) * mm});
            skLineSegment(sketch, "E1264", {"start": v(-21.7, -3.7) * mm, "end": v(-21.7, -5) * mm});
            skLineSegment(sketch, "E1265", {"start": v(-21.7, -5) * mm, "end": v(-20.3, -5) * mm});
            skLineSegment(sketch, "E1266", {"start": v(-20.3, -5) * mm, "end": v(-20.3, -3.7) * mm});
            skArc(sketch, "E1267", {"start": v(-20.3, -3.7) * mm, "mid": v(-20.5, -3.5) * mm, "end": v(-20.3, -3.3) * mm});
            skArc(sketch, "E1268", {"start": v(-20.9, -3.5) * mm, "mid": v(-21, -3.4) * mm, "end": v(-21.1, -3.5) * mm});
            skArc(sketch, "E1269", {"start": v(-21.1, -3.5) * mm, "mid": v(-21, -3.6) * mm, "end": v(-20.9, -3.5) * mm});
            skArc(sketch, "E1270", {"start": v(-21.7, -3.7) * mm, "mid": v(-21.5, -3.5) * mm, "end": v(-21.7, -3.3) * mm});
            skLineSegment(sketch, "E1271", {"start": v(-20.3, -3.3) * mm, "end": v(-20.3, -2) * mm});
            skLineSegment(sketch, "E1272", {"start": v(-20.3, -2) * mm, "end": v(-21.7, -2) * mm});
            skLineSegment(sketch, "E1273", {"start": v(-21.7, -2) * mm, "end": v(-21.7, -3.3) * mm});
            skLineSegment(sketch, "E1274", {"start": v(21.5, -10.5) * mm, "end": v(20.5, -10.5) * mm});
            skLineSegment(sketch, "E1275", {"start": v(20.5, -10.5) * mm, "end": v(20.5, -9.5) * mm});
            skLineSegment(sketch, "E1276", {"start": v(20.5, -9.5) * mm, "end": v(21.5, -9.5) * mm});
            skLineSegment(sketch, "E1277", {"start": v(21.5, -9.5) * mm, "end": v(21.5, -10.5) * mm});
            skLineSegment(sketch, "E1278", {"start": v(21.5, -9) * mm, "end": v(20.5, -9) * mm});
            skLineSegment(sketch, "E1279", {"start": v(20.5, -9) * mm, "end": v(20.5, -8) * mm});
            skLineSegment(sketch, "E1280", {"start": v(20.5, -8) * mm, "end": v(21.5, -8) * mm});
            skLineSegment(sketch, "E1281", {"start": v(21.5, -8) * mm, "end": v(21.5, -9) * mm});
            skLineSegment(sketch, "E1282", {"start": v(20.3, -9.45) * mm, "end": v(20.3, -10.75) * mm});
            skLineSegment(sketch, "E1283", {"start": v(20.3, -10.75) * mm, "end": v(21.7, -10.75) * mm});
            skLineSegment(sketch, "E1284", {"start": v(21.7, -10.75) * mm, "end": v(21.7, -9.45) * mm});
            skArc(sketch, "E1285", {"start": v(21.7, -9.45) * mm, "mid": v(21.5, -9.25) * mm, "end": v(21.7, -9.05) * mm});
            skArc(sketch, "E1286", {"start": v(21.1, -9.25) * mm, "mid": v(21, -9.15) * mm, "end": v(20.9, -9.25) * mm});
            skArc(sketch, "E1287", {"start": v(20.9, -9.25) * mm, "mid": v(21, -9.35) * mm, "end": v(21.1, -9.25) * mm});
            skArc(sketch, "E1288", {"start": v(20.3, -9.45) * mm, "mid": v(20.5, -9.25) * mm, "end": v(20.3, -9.05) * mm});
            skLineSegment(sketch, "E1289", {"start": v(21.7, -9.05) * mm, "end": v(21.7, -7.75) * mm});
            skLineSegment(sketch, "E1290", {"start": v(21.7, -7.75) * mm, "end": v(20.3, -7.75) * mm});
            skLineSegment(sketch, "E1291", {"start": v(20.3, -7.75) * mm, "end": v(20.3, -9.05) * mm});
            skLineSegment(sketch, "E1292", {"start": v(-10.5, -42.25) * mm, "end": v(-9.5, -42.25) * mm});
            skLineSegment(sketch, "E1293", {"start": v(-9.5, -42.25) * mm, "end": v(-9.5, -43.25) * mm});
            skLineSegment(sketch, "E1294", {"start": v(-9.5, -43.25) * mm, "end": v(-10.5, -43.25) * mm});
            skLineSegment(sketch, "E1295", {"start": v(-10.5, -43.25) * mm, "end": v(-10.5, -42.25) * mm});
            skLineSegment(sketch, "E1296", {"start": v(-10.5, -43.75) * mm, "end": v(-9.5, -43.75) * mm});
            skLineSegment(sketch, "E1297", {"start": v(-9.5, -43.75) * mm, "end": v(-9.5, -44.75) * mm});
            skLineSegment(sketch, "E1298", {"start": v(-9.5, -44.75) * mm, "end": v(-10.5, -44.75) * mm});
            skLineSegment(sketch, "E1299", {"start": v(-10.5, -44.75) * mm, "end": v(-10.5, -43.75) * mm});
            skLineSegment(sketch, "E1300", {"start": v(-9.3, -43.3) * mm, "end": v(-9.3, -42) * mm});
            skLineSegment(sketch, "E1301", {"start": v(-9.3, -42) * mm, "end": v(-10.7, -42) * mm});
            skLineSegment(sketch, "E1302", {"start": v(-10.7, -42) * mm, "end": v(-10.7, -43.3) * mm});
            skArc(sketch, "E1303", {"start": v(-10.7, -43.3) * mm, "mid": v(-10.5, -43.5) * mm, "end": v(-10.7, -43.7) * mm});
            skArc(sketch, "E1304", {"start": v(-9.9, -43.5) * mm, "mid": v(-10, -43.4) * mm, "end": v(-10.1, -43.5) * mm});
            skArc(sketch, "E1305", {"start": v(-10.1, -43.5) * mm, "mid": v(-10, -43.6) * mm, "end": v(-9.9, -43.5) * mm});
            skArc(sketch, "E1306", {"start": v(-9.3, -43.3) * mm, "mid": v(-9.5, -43.5) * mm, "end": v(-9.3, -43.7) * mm});
            skLineSegment(sketch, "E1307", {"start": v(-10.7, -43.7) * mm, "end": v(-10.7, -45) * mm});
            skLineSegment(sketch, "E1308", {"start": v(-10.7, -45) * mm, "end": v(-9.3, -45) * mm});
            skLineSegment(sketch, "E1309", {"start": v(-9.3, -45) * mm, "end": v(-9.3, -43.7) * mm});
            skLineSegment(sketch, "E1310", {"start": v(-11, -44.75) * mm, "end": v(-12, -44.75) * mm});
            skLineSegment(sketch, "E1311", {"start": v(-12, -44.75) * mm, "end": v(-12, -43.75) * mm});
            skLineSegment(sketch, "E1312", {"start": v(-12, -43.75) * mm, "end": v(-11, -43.75) * mm});
            skLineSegment(sketch, "E1313", {"start": v(-11, -43.75) * mm, "end": v(-11, -44.75) * mm});
            skLineSegment(sketch, "E1314", {"start": v(-11, -43.25) * mm, "end": v(-12, -43.25) * mm});
            skLineSegment(sketch, "E1315", {"start": v(-12, -43.25) * mm, "end": v(-12, -42.25) * mm});
            skLineSegment(sketch, "E1316", {"start": v(-12, -42.25) * mm, "end": v(-11, -42.25) * mm});
            skLineSegment(sketch, "E1317", {"start": v(-11, -42.25) * mm, "end": v(-11, -43.25) * mm});
            skLineSegment(sketch, "E1318", {"start": v(-12.2, -43.7) * mm, "end": v(-12.2, -45) * mm});
            skLineSegment(sketch, "E1319", {"start": v(-12.2, -45) * mm, "end": v(-10.8, -45) * mm});
            skLineSegment(sketch, "E1320", {"start": v(-10.8, -45) * mm, "end": v(-10.8, -43.7) * mm});
            skArc(sketch, "E1321", {"start": v(-10.8, -43.7) * mm, "mid": v(-11, -43.5) * mm, "end": v(-10.8, -43.3) * mm});
            skArc(sketch, "E1322", {"start": v(-11.4, -43.5) * mm, "mid": v(-11.5, -43.4) * mm, "end": v(-11.6, -43.5) * mm});
            skArc(sketch, "E1323", {"start": v(-11.6, -43.5) * mm, "mid": v(-11.5, -43.6) * mm, "end": v(-11.4, -43.5) * mm});
            skArc(sketch, "E1324", {"start": v(-12.2, -43.7) * mm, "mid": v(-12, -43.5) * mm, "end": v(-12.2, -43.3) * mm});
            skLineSegment(sketch, "E1325", {"start": v(-10.8, -43.3) * mm, "end": v(-10.8, -42) * mm});
            skLineSegment(sketch, "E1326", {"start": v(-10.8, -42) * mm, "end": v(-12.2, -42) * mm});
            skLineSegment(sketch, "E1327", {"start": v(-12.2, -42) * mm, "end": v(-12.2, -43.3) * mm});
            skLineSegment(sketch, "E1328", {"start": v(-9, -42.25) * mm, "end": v(-8, -42.25) * mm});
            skLineSegment(sketch, "E1329", {"start": v(-8, -42.25) * mm, "end": v(-8, -43.25) * mm});
            skLineSegment(sketch, "E1330", {"start": v(-8, -43.25) * mm, "end": v(-9, -43.25) * mm});
            skLineSegment(sketch, "E1331", {"start": v(-9, -43.25) * mm, "end": v(-9, -42.25) * mm});
            skLineSegment(sketch, "E1332", {"start": v(-9, -43.75) * mm, "end": v(-8, -43.75) * mm});
            skLineSegment(sketch, "E1333", {"start": v(-8, -43.75) * mm, "end": v(-8, -44.75) * mm});
            skLineSegment(sketch, "E1334", {"start": v(-8, -44.75) * mm, "end": v(-9, -44.75) * mm});
            skLineSegment(sketch, "E1335", {"start": v(-9, -44.75) * mm, "end": v(-9, -43.75) * mm});
            skLineSegment(sketch, "E1336", {"start": v(-7.8, -43.3) * mm, "end": v(-7.8, -42) * mm});
            skLineSegment(sketch, "E1337", {"start": v(-7.8, -42) * mm, "end": v(-9.2, -42) * mm});
            skLineSegment(sketch, "E1338", {"start": v(-9.2, -42) * mm, "end": v(-9.2, -43.3) * mm});
            skArc(sketch, "E1339", {"start": v(-9.2, -43.3) * mm, "mid": v(-9, -43.5) * mm, "end": v(-9.2, -43.7) * mm});
            skArc(sketch, "E1340", {"start": v(-8.4, -43.5) * mm, "mid": v(-8.5, -43.4) * mm, "end": v(-8.6, -43.5) * mm});
            skArc(sketch, "E1341", {"start": v(-8.6, -43.5) * mm, "mid": v(-8.5, -43.6) * mm, "end": v(-8.4, -43.5) * mm});
            skArc(sketch, "E1342", {"start": v(-7.8, -43.3) * mm, "mid": v(-8, -43.5) * mm, "end": v(-7.8, -43.7) * mm});
            skLineSegment(sketch, "E1343", {"start": v(-9.2, -43.7) * mm, "end": v(-9.2, -45) * mm});
            skLineSegment(sketch, "E1344", {"start": v(-9.2, -45) * mm, "end": v(-7.8, -45) * mm});
            skLineSegment(sketch, "E1345", {"start": v(-7.8, -45) * mm, "end": v(-7.8, -43.7) * mm});
            skLineSegment(sketch, "E1346", {"start": v(-0.5, -45.25) * mm, "end": v(-1.5, -45.25) * mm});
            skLineSegment(sketch, "E1347", {"start": v(-1.5, -45.25) * mm, "end": v(-1.5, -44.25) * mm});
            skLineSegment(sketch, "E1348", {"start": v(-1.5, -44.25) * mm, "end": v(-0.5, -44.25) * mm});
            skLineSegment(sketch, "E1349", {"start": v(-0.5, -44.25) * mm, "end": v(-0.5, -45.25) * mm});
            skLineSegment(sketch, "E1350", {"start": v(-0.5, -43.75) * mm, "end": v(-1.5, -43.75) * mm});
            skLineSegment(sketch, "E1351", {"start": v(-1.5, -43.75) * mm, "end": v(-1.5, -42.75) * mm});
            skLineSegment(sketch, "E1352", {"start": v(-1.5, -42.75) * mm, "end": v(-0.5, -42.75) * mm});
            skLineSegment(sketch, "E1353", {"start": v(-0.5, -42.75) * mm, "end": v(-0.5, -43.75) * mm});
            skLineSegment(sketch, "E1354", {"start": v(-1.7, -44.2) * mm, "end": v(-1.7, -45.5) * mm});
            skLineSegment(sketch, "E1355", {"start": v(-1.7, -45.5) * mm, "end": v(-0.3, -45.5) * mm});
            skLineSegment(sketch, "E1356", {"start": v(-0.3, -45.5) * mm, "end": v(-0.3, -44.2) * mm});
            skArc(sketch, "E1357", {"start": v(-0.3, -44.2) * mm, "mid": v(-0.5, -44) * mm, "end": v(-0.3, -43.8) * mm});
            skArc(sketch, "E1358", {"start": v(-0.9, -44) * mm, "mid": v(-1, -43.9) * mm, "end": v(-1.1, -44) * mm});
            skArc(sketch, "E1359", {"start": v(-1.1, -44) * mm, "mid": v(-1, -44.1) * mm, "end": v(-0.9, -44) * mm});
            skArc(sketch, "E1360", {"start": v(-1.7, -44.2) * mm, "mid": v(-1.5, -44) * mm, "end": v(-1.7, -43.8) * mm});
            skLineSegment(sketch, "E1361", {"start": v(-0.3, -43.8) * mm, "end": v(-0.3, -42.5) * mm});
            skLineSegment(sketch, "E1362", {"start": v(-0.3, -42.5) * mm, "end": v(-1.7, -42.5) * mm});
            skLineSegment(sketch, "E1363", {"start": v(-1.7, -42.5) * mm, "end": v(-1.7, -43.8) * mm});
            skLineSegment(sketch, "E1364", {"start": v(-20.25, -44) * mm, "end": v(-20.25, -43) * mm});
            skLineSegment(sketch, "E1365", {"start": v(-20.25, -43) * mm, "end": v(-19.25, -43) * mm});
            skLineSegment(sketch, "E1366", {"start": v(-19.25, -43) * mm, "end": v(-19.25, -44) * mm});
            skLineSegment(sketch, "E1367", {"start": v(-19.25, -44) * mm, "end": v(-20.25, -44) * mm});
            skLineSegment(sketch, "E1368", {"start": v(-18.75, -44) * mm, "end": v(-18.75, -43) * mm});
            skLineSegment(sketch, "E1369", {"start": v(-18.75, -43) * mm, "end": v(-17.75, -43) * mm});
            skLineSegment(sketch, "E1370", {"start": v(-17.75, -43) * mm, "end": v(-17.75, -44) * mm});
            skLineSegment(sketch, "E1371", {"start": v(-17.75, -44) * mm, "end": v(-18.75, -44) * mm});
            skLineSegment(sketch, "E1372", {"start": v(-19.2, -42.8) * mm, "end": v(-20.5, -42.8) * mm});
            skLineSegment(sketch, "E1373", {"start": v(-20.5, -42.8) * mm, "end": v(-20.5, -44.2) * mm});
            skLineSegment(sketch, "E1374", {"start": v(-20.5, -44.2) * mm, "end": v(-19.2, -44.2) * mm});
            skArc(sketch, "E1375", {"start": v(-19.2, -44.2) * mm, "mid": v(-19, -44) * mm, "end": v(-18.8, -44.2) * mm});
            skArc(sketch, "E1376", {"start": v(-18.9, -43.5) * mm, "mid": v(-19, -43.4) * mm, "end": v(-19.1, -43.5) * mm});
            skArc(sketch, "E1377", {"start": v(-19.1, -43.5) * mm, "mid": v(-19, -43.6) * mm, "end": v(-18.9, -43.5) * mm});
            skArc(sketch, "E1378", {"start": v(-19.2, -42.8) * mm, "mid": v(-19, -43) * mm, "end": v(-18.8, -42.8) * mm});
            skLineSegment(sketch, "E1379", {"start": v(-18.8, -44.2) * mm, "end": v(-17.5, -44.2) * mm});
            skLineSegment(sketch, "E1380", {"start": v(-17.5, -44.2) * mm, "end": v(-17.5, -42.8) * mm});
            skLineSegment(sketch, "E1381", {"start": v(-17.5, -42.8) * mm, "end": v(-18.8, -42.8) * mm});
            skLineSegment(sketch, "E1382", {"start": v(-26.75, 9.75) * mm, "end": v(-26.75, 10.75) * mm});
            skLineSegment(sketch, "E1383", {"start": v(-26.75, 10.75) * mm, "end": v(-25.75, 10.75) * mm});
            skLineSegment(sketch, "E1384", {"start": v(-25.75, 10.75) * mm, "end": v(-25.75, 9.75) * mm});
            skLineSegment(sketch, "E1385", {"start": v(-25.75, 9.75) * mm, "end": v(-26.75, 9.75) * mm});
            skLineSegment(sketch, "E1386", {"start": v(-25.25, 9.75) * mm, "end": v(-25.25, 10.75) * mm});
            skLineSegment(sketch, "E1387", {"start": v(-25.25, 10.75) * mm, "end": v(-24.25, 10.75) * mm});
            skLineSegment(sketch, "E1388", {"start": v(-24.25, 10.75) * mm, "end": v(-24.25, 9.75) * mm});
            skLineSegment(sketch, "E1389", {"start": v(-24.25, 9.75) * mm, "end": v(-25.25, 9.75) * mm});
            skLineSegment(sketch, "E1390", {"start": v(-25.7, 10.95) * mm, "end": v(-27, 10.95) * mm});
            skLineSegment(sketch, "E1391", {"start": v(-27, 10.95) * mm, "end": v(-27, 9.55) * mm});
            skLineSegment(sketch, "E1392", {"start": v(-27, 9.55) * mm, "end": v(-25.7, 9.55) * mm});
            skArc(sketch, "E1393", {"start": v(-25.7, 9.55) * mm, "mid": v(-25.5, 9.75) * mm, "end": v(-25.3, 9.55) * mm});
            skArc(sketch, "E1394", {"start": v(-25.4, 10.25) * mm, "mid": v(-25.5, 10.35) * mm, "end": v(-25.6, 10.25) * mm});
            skArc(sketch, "E1395", {"start": v(-25.6, 10.25) * mm, "mid": v(-25.5, 10.15) * mm, "end": v(-25.4, 10.25) * mm});
            skArc(sketch, "E1396", {"start": v(-25.7, 10.95) * mm, "mid": v(-25.5, 10.75) * mm, "end": v(-25.3, 10.95) * mm});
            skLineSegment(sketch, "E1397", {"start": v(-25.3, 9.55) * mm, "end": v(-24, 9.55) * mm});
            skLineSegment(sketch, "E1398", {"start": v(-24, 9.55) * mm, "end": v(-24, 10.95) * mm});
            skLineSegment(sketch, "E1399", {"start": v(-24, 10.95) * mm, "end": v(-25.3, 10.95) * mm});
            skLineSegment(sketch, "E1400", {"start": v(-24.25, 6.25) * mm, "end": v(-24.25, 5.25) * mm});
            skLineSegment(sketch, "E1401", {"start": v(-24.25, 5.25) * mm, "end": v(-25.25, 5.25) * mm});
            skLineSegment(sketch, "E1402", {"start": v(-25.25, 5.25) * mm, "end": v(-25.25, 6.25) * mm});
            skLineSegment(sketch, "E1403", {"start": v(-25.25, 6.25) * mm, "end": v(-24.25, 6.25) * mm});
            skLineSegment(sketch, "E1404", {"start": v(-25.75, 6.25) * mm, "end": v(-25.75, 5.25) * mm});
            skLineSegment(sketch, "E1405", {"start": v(-25.75, 5.25) * mm, "end": v(-26.75, 5.25) * mm});
            skLineSegment(sketch, "E1406", {"start": v(-26.75, 5.25) * mm, "end": v(-26.75, 6.25) * mm});
            skLineSegment(sketch, "E1407", {"start": v(-26.75, 6.25) * mm, "end": v(-25.75, 6.25) * mm});
            skLineSegment(sketch, "E1408", {"start": v(-25.3, 5.05) * mm, "end": v(-24, 5.05) * mm});
            skLineSegment(sketch, "E1409", {"start": v(-24, 5.05) * mm, "end": v(-24, 6.45) * mm});
            skLineSegment(sketch, "E1410", {"start": v(-24, 6.45) * mm, "end": v(-25.3, 6.45) * mm});
            skArc(sketch, "E1411", {"start": v(-25.3, 6.45) * mm, "mid": v(-25.5, 6.25) * mm, "end": v(-25.7, 6.45) * mm});
            skArc(sketch, "E1412", {"start": v(-25.4, 5.75) * mm, "mid": v(-25.5, 5.85) * mm, "end": v(-25.6, 5.75) * mm});
            skArc(sketch, "E1413", {"start": v(-25.6, 5.75) * mm, "mid": v(-25.5, 5.65) * mm, "end": v(-25.4, 5.75) * mm});
            skArc(sketch, "E1414", {"start": v(-25.3, 5.05) * mm, "mid": v(-25.5, 5.25) * mm, "end": v(-25.7, 5.05) * mm});
            skLineSegment(sketch, "E1415", {"start": v(-25.7, 6.45) * mm, "end": v(-27, 6.45) * mm});
            skLineSegment(sketch, "E1416", {"start": v(-27, 6.45) * mm, "end": v(-27, 5.05) * mm});
            skLineSegment(sketch, "E1417", {"start": v(-27, 5.05) * mm, "end": v(-25.7, 5.05) * mm});
            skLineSegment(sketch, "E1418", {"start": v(20.5, -12.25) * mm, "end": v(21.5, -12.25) * mm});
            skLineSegment(sketch, "E1419", {"start": v(21.5, -12.25) * mm, "end": v(21.5, -13.25) * mm});
            skLineSegment(sketch, "E1420", {"start": v(21.5, -13.25) * mm, "end": v(20.5, -13.25) * mm});
            skLineSegment(sketch, "E1421", {"start": v(20.5, -13.25) * mm, "end": v(20.5, -12.25) * mm});
            skLineSegment(sketch, "E1422", {"start": v(20.5, -13.75) * mm, "end": v(21.5, -13.75) * mm});
            skLineSegment(sketch, "E1423", {"start": v(21.5, -13.75) * mm, "end": v(21.5, -14.75) * mm});
            skLineSegment(sketch, "E1424", {"start": v(21.5, -14.75) * mm, "end": v(20.5, -14.75) * mm});
            skLineSegment(sketch, "E1425", {"start": v(20.5, -14.75) * mm, "end": v(20.5, -13.75) * mm});
            skLineSegment(sketch, "E1426", {"start": v(21.7, -13.3) * mm, "end": v(21.7, -12) * mm});
            skLineSegment(sketch, "E1427", {"start": v(21.7, -12) * mm, "end": v(20.3, -12) * mm});
            skLineSegment(sketch, "E1428", {"start": v(20.3, -12) * mm, "end": v(20.3, -13.3) * mm});
            skArc(sketch, "E1429", {"start": v(20.3, -13.3) * mm, "mid": v(20.5, -13.5) * mm, "end": v(20.3, -13.7) * mm});
            skArc(sketch, "E1430", {"start": v(21.1, -13.5) * mm, "mid": v(21, -13.4) * mm, "end": v(20.9, -13.5) * mm});
            skArc(sketch, "E1431", {"start": v(20.9, -13.5) * mm, "mid": v(21, -13.6) * mm, "end": v(21.1, -13.5) * mm});
            skArc(sketch, "E1432", {"start": v(21.7, -13.3) * mm, "mid": v(21.5, -13.5) * mm, "end": v(21.7, -13.7) * mm});
            skLineSegment(sketch, "E1433", {"start": v(20.3, -13.7) * mm, "end": v(20.3, -15) * mm});
            skLineSegment(sketch, "E1434", {"start": v(20.3, -15) * mm, "end": v(21.7, -15) * mm});
            skLineSegment(sketch, "E1435", {"start": v(21.7, -15) * mm, "end": v(21.7, -13.7) * mm});
            skLineSegment(sketch, "E1436", {"start": v(20.5, -2.25) * mm, "end": v(21.5, -2.25) * mm});
            skLineSegment(sketch, "E1437", {"start": v(21.5, -2.25) * mm, "end": v(21.5, -3.25) * mm});
            skLineSegment(sketch, "E1438", {"start": v(21.5, -3.25) * mm, "end": v(20.5, -3.25) * mm});
            skLineSegment(sketch, "E1439", {"start": v(20.5, -3.25) * mm, "end": v(20.5, -2.25) * mm});
            skLineSegment(sketch, "E1440", {"start": v(20.5, -3.75) * mm, "end": v(21.5, -3.75) * mm});
            skLineSegment(sketch, "E1441", {"start": v(21.5, -3.75) * mm, "end": v(21.5, -4.75) * mm});
            skLineSegment(sketch, "E1442", {"start": v(21.5, -4.75) * mm, "end": v(20.5, -4.75) * mm});
            skLineSegment(sketch, "E1443", {"start": v(20.5, -4.75) * mm, "end": v(20.5, -3.75) * mm});
            skLineSegment(sketch, "E1444", {"start": v(21.7, -3.3) * mm, "end": v(21.7, -2) * mm});
            skLineSegment(sketch, "E1445", {"start": v(21.7, -2) * mm, "end": v(20.3, -2) * mm});
            skLineSegment(sketch, "E1446", {"start": v(20.3, -2) * mm, "end": v(20.3, -3.3) * mm});
            skArc(sketch, "E1447", {"start": v(20.3, -3.3) * mm, "mid": v(20.5, -3.5) * mm, "end": v(20.3, -3.7) * mm});
            skArc(sketch, "E1448", {"start": v(21.1, -3.5) * mm, "mid": v(21, -3.4) * mm, "end": v(20.9, -3.5) * mm});
            skArc(sketch, "E1449", {"start": v(20.9, -3.5) * mm, "mid": v(21, -3.6) * mm, "end": v(21.1, -3.5) * mm});
            skArc(sketch, "E1450", {"start": v(21.7, -3.3) * mm, "mid": v(21.5, -3.5) * mm, "end": v(21.7, -3.7) * mm});
            skLineSegment(sketch, "E1451", {"start": v(20.3, -3.7) * mm, "end": v(20.3, -5) * mm});
            skLineSegment(sketch, "E1452", {"start": v(20.3, -5) * mm, "end": v(21.7, -5) * mm});
            skLineSegment(sketch, "E1453", {"start": v(21.7, -5) * mm, "end": v(21.7, -3.7) * mm});
            skLineSegment(sketch, "E1454", {"start": v(25, 30.75) * mm, "end": v(26, 30.75) * mm});
            skLineSegment(sketch, "E1455", {"start": v(26, 30.75) * mm, "end": v(26, 29.75) * mm});
            skLineSegment(sketch, "E1456", {"start": v(26, 29.75) * mm, "end": v(25, 29.75) * mm});
            skLineSegment(sketch, "E1457", {"start": v(25, 29.75) * mm, "end": v(25, 30.75) * mm});
            skLineSegment(sketch, "E1458", {"start": v(25, 29.25) * mm, "end": v(26, 29.25) * mm});
            skLineSegment(sketch, "E1459", {"start": v(26, 29.25) * mm, "end": v(26, 28.25) * mm});
            skLineSegment(sketch, "E1460", {"start": v(26, 28.25) * mm, "end": v(25, 28.25) * mm});
            skLineSegment(sketch, "E1461", {"start": v(25, 28.25) * mm, "end": v(25, 29.25) * mm});
            skLineSegment(sketch, "E1462", {"start": v(26.2, 29.7) * mm, "end": v(26.2, 31) * mm});
            skLineSegment(sketch, "E1463", {"start": v(26.2, 31) * mm, "end": v(24.8, 31) * mm});
            skLineSegment(sketch, "E1464", {"start": v(24.8, 31) * mm, "end": v(24.8, 29.7) * mm});
            skArc(sketch, "E1465", {"start": v(24.8, 29.7) * mm, "mid": v(25, 29.5) * mm, "end": v(24.8, 29.3) * mm});
            skArc(sketch, "E1466", {"start": v(25.6, 29.5) * mm, "mid": v(25.5, 29.6) * mm, "end": v(25.4, 29.5) * mm});
            skArc(sketch, "E1467", {"start": v(25.4, 29.5) * mm, "mid": v(25.5, 29.4) * mm, "end": v(25.6, 29.5) * mm});
            skArc(sketch, "E1468", {"start": v(26.2, 29.7) * mm, "mid": v(26, 29.5) * mm, "end": v(26.2, 29.3) * mm});
            skLineSegment(sketch, "E1469", {"start": v(24.8, 29.3) * mm, "end": v(24.8, 28) * mm});
            skLineSegment(sketch, "E1470", {"start": v(24.8, 28) * mm, "end": v(26.2, 28) * mm});
            skLineSegment(sketch, "E1471", {"start": v(26.2, 28) * mm, "end": v(26.2, 29.3) * mm});
            skLineSegment(sketch, "E1472", {"start": v(25, 17.25) * mm, "end": v(26, 17.25) * mm});
            skLineSegment(sketch, "E1473", {"start": v(26, 17.25) * mm, "end": v(26, 16.25) * mm});
            skLineSegment(sketch, "E1474", {"start": v(26, 16.25) * mm, "end": v(25, 16.25) * mm});
            skLineSegment(sketch, "E1475", {"start": v(25, 16.25) * mm, "end": v(25, 17.25) * mm});
            skLineSegment(sketch, "E1476", {"start": v(25, 15.75) * mm, "end": v(26, 15.75) * mm});
            skLineSegment(sketch, "E1477", {"start": v(26, 15.75) * mm, "end": v(26, 14.75) * mm});
            skLineSegment(sketch, "E1478", {"start": v(26, 14.75) * mm, "end": v(25, 14.75) * mm});
            skLineSegment(sketch, "E1479", {"start": v(25, 14.75) * mm, "end": v(25, 15.75) * mm});
            skLineSegment(sketch, "E1480", {"start": v(26.2, 16.2) * mm, "end": v(26.2, 17.5) * mm});
            skLineSegment(sketch, "E1481", {"start": v(26.2, 17.5) * mm, "end": v(24.8, 17.5) * mm});
            skLineSegment(sketch, "E1482", {"start": v(24.8, 17.5) * mm, "end": v(24.8, 16.2) * mm});
            skArc(sketch, "E1483", {"start": v(24.8, 16.2) * mm, "mid": v(25, 16) * mm, "end": v(24.8, 15.8) * mm});
            skArc(sketch, "E1484", {"start": v(25.6, 16) * mm, "mid": v(25.5, 16.1) * mm, "end": v(25.4, 16) * mm});
            skArc(sketch, "E1485", {"start": v(25.4, 16) * mm, "mid": v(25.5, 15.9) * mm, "end": v(25.6, 16) * mm});
            skArc(sketch, "E1486", {"start": v(26.2, 16.2) * mm, "mid": v(26, 16) * mm, "end": v(26.2, 15.8) * mm});
            skLineSegment(sketch, "E1487", {"start": v(24.8, 15.8) * mm, "end": v(24.8, 14.5) * mm});
            skLineSegment(sketch, "E1488", {"start": v(24.8, 14.5) * mm, "end": v(26.2, 14.5) * mm});
            skLineSegment(sketch, "E1489", {"start": v(26.2, 14.5) * mm, "end": v(26.2, 15.8) * mm});
            skLineSegment(sketch, "E1490", {"start": v(22.75, -7) * mm, "end": v(22.75, -6) * mm});
            skLineSegment(sketch, "E1491", {"start": v(22.75, -6) * mm, "end": v(23.75, -6) * mm});
            skLineSegment(sketch, "E1492", {"start": v(23.75, -6) * mm, "end": v(23.75, -7) * mm});
            skLineSegment(sketch, "E1493", {"start": v(23.75, -7) * mm, "end": v(22.75, -7) * mm});
            skLineSegment(sketch, "E1494", {"start": v(24.25, -7) * mm, "end": v(24.25, -6) * mm});
            skLineSegment(sketch, "E1495", {"start": v(24.25, -6) * mm, "end": v(25.25, -6) * mm});
            skLineSegment(sketch, "E1496", {"start": v(25.25, -6) * mm, "end": v(25.25, -7) * mm});
            skLineSegment(sketch, "E1497", {"start": v(25.25, -7) * mm, "end": v(24.25, -7) * mm});
            skLineSegment(sketch, "E1498", {"start": v(23.8, -5.8) * mm, "end": v(22.5, -5.8) * mm});
            skLineSegment(sketch, "E1499", {"start": v(22.5, -5.8) * mm, "end": v(22.5, -7.2) * mm});
            skLineSegment(sketch, "E1500", {"start": v(22.5, -7.2) * mm, "end": v(23.8, -7.2) * mm});
            skArc(sketch, "E1501", {"start": v(23.8, -7.2) * mm, "mid": v(24, -7) * mm, "end": v(24.2, -7.2) * mm});
            skArc(sketch, "E1502", {"start": v(24.1, -6.5) * mm, "mid": v(24, -6.4) * mm, "end": v(23.9, -6.5) * mm});
            skArc(sketch, "E1503", {"start": v(23.9, -6.5) * mm, "mid": v(24, -6.6) * mm, "end": v(24.1, -6.5) * mm});
            skArc(sketch, "E1504", {"start": v(23.8, -5.8) * mm, "mid": v(24, -6) * mm, "end": v(24.2, -5.8) * mm});
            skLineSegment(sketch, "E1505", {"start": v(24.2, -7.2) * mm, "end": v(25.5, -7.2) * mm});
            skLineSegment(sketch, "E1506", {"start": v(25.5, -7.2) * mm, "end": v(25.5, -5.8) * mm});
            skLineSegment(sketch, "E1507", {"start": v(25.5, -5.8) * mm, "end": v(24.2, -5.8) * mm});
            skLineSegment(sketch, "E1508", {"start": v(-24.25, -8.25) * mm, "end": v(-24.25, -9.25) * mm});
            skLineSegment(sketch, "E1509", {"start": v(-24.25, -9.25) * mm, "end": v(-25.25, -9.25) * mm});
            skLineSegment(sketch, "E1510", {"start": v(-25.25, -9.25) * mm, "end": v(-25.25, -8.25) * mm});
            skLineSegment(sketch, "E1511", {"start": v(-25.25, -8.25) * mm, "end": v(-24.25, -8.25) * mm});
            skLineSegment(sketch, "E1512", {"start": v(-25.75, -8.25) * mm, "end": v(-25.75, -9.25) * mm});
            skLineSegment(sketch, "E1513", {"start": v(-25.75, -9.25) * mm, "end": v(-26.75, -9.25) * mm});
            skLineSegment(sketch, "E1514", {"start": v(-26.75, -9.25) * mm, "end": v(-26.75, -8.25) * mm});
            skLineSegment(sketch, "E1515", {"start": v(-26.75, -8.25) * mm, "end": v(-25.75, -8.25) * mm});
            skLineSegment(sketch, "E1516", {"start": v(-25.3, -9.45) * mm, "end": v(-24, -9.45) * mm});
            skLineSegment(sketch, "E1517", {"start": v(-24, -9.45) * mm, "end": v(-24, -8.05) * mm});
            skLineSegment(sketch, "E1518", {"start": v(-24, -8.05) * mm, "end": v(-25.3, -8.05) * mm});
            skArc(sketch, "E1519", {"start": v(-25.3, -8.05) * mm, "mid": v(-25.5, -8.25) * mm, "end": v(-25.7, -8.05) * mm});
            skArc(sketch, "E1520", {"start": v(-25.4, -8.75) * mm, "mid": v(-25.5, -8.65) * mm, "end": v(-25.6, -8.75) * mm});
            skArc(sketch, "E1521", {"start": v(-25.6, -8.75) * mm, "mid": v(-25.5, -8.85) * mm, "end": v(-25.4, -8.75) * mm});
            skArc(sketch, "E1522", {"start": v(-25.3, -9.45) * mm, "mid": v(-25.5, -9.25) * mm, "end": v(-25.7, -9.45) * mm});
            skLineSegment(sketch, "E1523", {"start": v(-25.7, -8.05) * mm, "end": v(-27, -8.05) * mm});
            skLineSegment(sketch, "E1524", {"start": v(-27, -8.05) * mm, "end": v(-27, -9.45) * mm});
            skLineSegment(sketch, "E1525", {"start": v(-27, -9.45) * mm, "end": v(-25.7, -9.45) * mm});
            skLineSegment(sketch, "E1526", {"start": v(-24.25, 30.25) * mm, "end": v(-24.25, 29.25) * mm});
            skLineSegment(sketch, "E1527", {"start": v(-24.25, 29.25) * mm, "end": v(-25.25, 29.25) * mm});
            skLineSegment(sketch, "E1528", {"start": v(-25.25, 29.25) * mm, "end": v(-25.25, 30.25) * mm});
            skLineSegment(sketch, "E1529", {"start": v(-25.25, 30.25) * mm, "end": v(-24.25, 30.25) * mm});
            skLineSegment(sketch, "E1530", {"start": v(-25.75, 30.25) * mm, "end": v(-25.75, 29.25) * mm});
            skLineSegment(sketch, "E1531", {"start": v(-25.75, 29.25) * mm, "end": v(-26.75, 29.25) * mm});
            skLineSegment(sketch, "E1532", {"start": v(-26.75, 29.25) * mm, "end": v(-26.75, 30.25) * mm});
            skLineSegment(sketch, "E1533", {"start": v(-26.75, 30.25) * mm, "end": v(-25.75, 30.25) * mm});
            skLineSegment(sketch, "E1534", {"start": v(-25.3, 29.05) * mm, "end": v(-24, 29.05) * mm});
            skLineSegment(sketch, "E1535", {"start": v(-24, 29.05) * mm, "end": v(-24, 30.45) * mm});
            skLineSegment(sketch, "E1536", {"start": v(-24, 30.45) * mm, "end": v(-25.3, 30.45) * mm});
            skArc(sketch, "E1537", {"start": v(-25.3, 30.45) * mm, "mid": v(-25.5, 30.25) * mm, "end": v(-25.7, 30.45) * mm});
            skArc(sketch, "E1538", {"start": v(-25.4, 29.75) * mm, "mid": v(-25.5, 29.85) * mm, "end": v(-25.6, 29.75) * mm});
            skArc(sketch, "E1539", {"start": v(-25.6, 29.75) * mm, "mid": v(-25.5, 29.65) * mm, "end": v(-25.4, 29.75) * mm});
            skArc(sketch, "E1540", {"start": v(-25.3, 29.05) * mm, "mid": v(-25.5, 29.25) * mm, "end": v(-25.7, 29.05) * mm});
            skLineSegment(sketch, "E1541", {"start": v(-25.7, 30.45) * mm, "end": v(-27, 30.45) * mm});
            skLineSegment(sketch, "E1542", {"start": v(-27, 30.45) * mm, "end": v(-27, 29.05) * mm});
            skLineSegment(sketch, "E1543", {"start": v(-27, 29.05) * mm, "end": v(-25.7, 29.05) * mm});
            skLineSegment(sketch, "E1544", {"start": v(-26.75, 25.75) * mm, "end": v(-26.75, 26.75) * mm});
            skLineSegment(sketch, "E1545", {"start": v(-26.75, 26.75) * mm, "end": v(-25.75, 26.75) * mm});
            skLineSegment(sketch, "E1546", {"start": v(-25.75, 26.75) * mm, "end": v(-25.75, 25.75) * mm});
            skLineSegment(sketch, "E1547", {"start": v(-25.75, 25.75) * mm, "end": v(-26.75, 25.75) * mm});
            skLineSegment(sketch, "E1548", {"start": v(-25.25, 25.75) * mm, "end": v(-25.25, 26.75) * mm});
            skLineSegment(sketch, "E1549", {"start": v(-25.25, 26.75) * mm, "end": v(-24.25, 26.75) * mm});
            skLineSegment(sketch, "E1550", {"start": v(-24.25, 26.75) * mm, "end": v(-24.25, 25.75) * mm});
            skLineSegment(sketch, "E1551", {"start": v(-24.25, 25.75) * mm, "end": v(-25.25, 25.75) * mm});
            skLineSegment(sketch, "E1552", {"start": v(-25.7, 26.95) * mm, "end": v(-27, 26.95) * mm});
            skLineSegment(sketch, "E1553", {"start": v(-27, 26.95) * mm, "end": v(-27, 25.55) * mm});
            skLineSegment(sketch, "E1554", {"start": v(-27, 25.55) * mm, "end": v(-25.7, 25.55) * mm});
            skArc(sketch, "E1555", {"start": v(-25.7, 25.55) * mm, "mid": v(-25.5, 25.75) * mm, "end": v(-25.3, 25.55) * mm});
            skArc(sketch, "E1556", {"start": v(-25.4, 26.25) * mm, "mid": v(-25.5, 26.35) * mm, "end": v(-25.6, 26.25) * mm});
            skArc(sketch, "E1557", {"start": v(-25.6, 26.25) * mm, "mid": v(-25.5, 26.15) * mm, "end": v(-25.4, 26.25) * mm});
            skArc(sketch, "E1558", {"start": v(-25.7, 26.95) * mm, "mid": v(-25.5, 26.75) * mm, "end": v(-25.3, 26.95) * mm});
            skLineSegment(sketch, "E1559", {"start": v(-25.3, 25.55) * mm, "end": v(-24, 25.55) * mm});
            skLineSegment(sketch, "E1560", {"start": v(-24, 25.55) * mm, "end": v(-24, 26.95) * mm});
            skLineSegment(sketch, "E1561", {"start": v(-24, 26.95) * mm, "end": v(-25.3, 26.95) * mm});
            skLineSegment(sketch, "E1562", {"start": v(-24.25, 22.25) * mm, "end": v(-24.25, 21.25) * mm});
            skLineSegment(sketch, "E1563", {"start": v(-24.25, 21.25) * mm, "end": v(-25.25, 21.25) * mm});
            skLineSegment(sketch, "E1564", {"start": v(-25.25, 21.25) * mm, "end": v(-25.25, 22.25) * mm});
            skLineSegment(sketch, "E1565", {"start": v(-25.25, 22.25) * mm, "end": v(-24.25, 22.25) * mm});
            skLineSegment(sketch, "E1566", {"start": v(-25.75, 22.25) * mm, "end": v(-25.75, 21.25) * mm});
            skLineSegment(sketch, "E1567", {"start": v(-25.75, 21.25) * mm, "end": v(-26.75, 21.25) * mm});
            skLineSegment(sketch, "E1568", {"start": v(-26.75, 21.25) * mm, "end": v(-26.75, 22.25) * mm});
            skLineSegment(sketch, "E1569", {"start": v(-26.75, 22.25) * mm, "end": v(-25.75, 22.25) * mm});
            skLineSegment(sketch, "E1570", {"start": v(-25.3, 21.05) * mm, "end": v(-24, 21.05) * mm});
            skLineSegment(sketch, "E1571", {"start": v(-24, 21.05) * mm, "end": v(-24, 22.45) * mm});
            skLineSegment(sketch, "E1572", {"start": v(-24, 22.45) * mm, "end": v(-25.3, 22.45) * mm});
            skArc(sketch, "E1573", {"start": v(-25.3, 22.45) * mm, "mid": v(-25.5, 22.25) * mm, "end": v(-25.7, 22.45) * mm});
            skArc(sketch, "E1574", {"start": v(-25.4, 21.75) * mm, "mid": v(-25.5, 21.85) * mm, "end": v(-25.6, 21.75) * mm});
            skArc(sketch, "E1575", {"start": v(-25.6, 21.75) * mm, "mid": v(-25.5, 21.65) * mm, "end": v(-25.4, 21.75) * mm});
            skArc(sketch, "E1576", {"start": v(-25.3, 21.05) * mm, "mid": v(-25.5, 21.25) * mm, "end": v(-25.7, 21.05) * mm});
            skLineSegment(sketch, "E1577", {"start": v(-25.7, 22.45) * mm, "end": v(-27, 22.45) * mm});
            skLineSegment(sketch, "E1578", {"start": v(-27, 22.45) * mm, "end": v(-27, 21.05) * mm});
            skLineSegment(sketch, "E1579", {"start": v(-27, 21.05) * mm, "end": v(-25.7, 21.05) * mm});
            skLineSegment(sketch, "E1580", {"start": v(-26.75, 17.75) * mm, "end": v(-26.75, 18.75) * mm});
            skLineSegment(sketch, "E1581", {"start": v(-26.75, 18.75) * mm, "end": v(-25.75, 18.75) * mm});
            skLineSegment(sketch, "E1582", {"start": v(-25.75, 18.75) * mm, "end": v(-25.75, 17.75) * mm});
            skLineSegment(sketch, "E1583", {"start": v(-25.75, 17.75) * mm, "end": v(-26.75, 17.75) * mm});
            skLineSegment(sketch, "E1584", {"start": v(-25.25, 17.75) * mm, "end": v(-25.25, 18.75) * mm});
            skLineSegment(sketch, "E1585", {"start": v(-25.25, 18.75) * mm, "end": v(-24.25, 18.75) * mm});
            skLineSegment(sketch, "E1586", {"start": v(-24.25, 18.75) * mm, "end": v(-24.25, 17.75) * mm});
            skLineSegment(sketch, "E1587", {"start": v(-24.25, 17.75) * mm, "end": v(-25.25, 17.75) * mm});
            skLineSegment(sketch, "E1588", {"start": v(-25.7, 18.95) * mm, "end": v(-27, 18.95) * mm});
            skLineSegment(sketch, "E1589", {"start": v(-27, 18.95) * mm, "end": v(-27, 17.55) * mm});
            skLineSegment(sketch, "E1590", {"start": v(-27, 17.55) * mm, "end": v(-25.7, 17.55) * mm});
            skArc(sketch, "E1591", {"start": v(-25.7, 17.55) * mm, "mid": v(-25.5, 17.75) * mm, "end": v(-25.3, 17.55) * mm});
            skArc(sketch, "E1592", {"start": v(-25.4, 18.25) * mm, "mid": v(-25.5, 18.35) * mm, "end": v(-25.6, 18.25) * mm});
            skArc(sketch, "E1593", {"start": v(-25.6, 18.25) * mm, "mid": v(-25.5, 18.15) * mm, "end": v(-25.4, 18.25) * mm});
            skArc(sketch, "E1594", {"start": v(-25.7, 18.95) * mm, "mid": v(-25.5, 18.75) * mm, "end": v(-25.3, 18.95) * mm});
            skLineSegment(sketch, "E1595", {"start": v(-25.3, 17.55) * mm, "end": v(-24, 17.55) * mm});
            skLineSegment(sketch, "E1596", {"start": v(-24, 17.55) * mm, "end": v(-24, 18.95) * mm});
            skLineSegment(sketch, "E1597", {"start": v(-24, 18.95) * mm, "end": v(-25.3, 18.95) * mm});
            skLineSegment(sketch, "E1598", {"start": v(-24.25, 14.25) * mm, "end": v(-24.25, 13.25) * mm});
            skLineSegment(sketch, "E1599", {"start": v(-24.25, 13.25) * mm, "end": v(-25.25, 13.25) * mm});
            skLineSegment(sketch, "E1600", {"start": v(-25.25, 13.25) * mm, "end": v(-25.25, 14.25) * mm});
            skLineSegment(sketch, "E1601", {"start": v(-25.25, 14.25) * mm, "end": v(-24.25, 14.25) * mm});
            skLineSegment(sketch, "E1602", {"start": v(-25.75, 14.25) * mm, "end": v(-25.75, 13.25) * mm});
            skLineSegment(sketch, "E1603", {"start": v(-25.75, 13.25) * mm, "end": v(-26.75, 13.25) * mm});
            skLineSegment(sketch, "E1604", {"start": v(-26.75, 13.25) * mm, "end": v(-26.75, 14.25) * mm});
            skLineSegment(sketch, "E1605", {"start": v(-26.75, 14.25) * mm, "end": v(-25.75, 14.25) * mm});
            skLineSegment(sketch, "E1606", {"start": v(-25.3, 13.05) * mm, "end": v(-24, 13.05) * mm});
            skLineSegment(sketch, "E1607", {"start": v(-24, 13.05) * mm, "end": v(-24, 14.45) * mm});
            skLineSegment(sketch, "E1608", {"start": v(-24, 14.45) * mm, "end": v(-25.3, 14.45) * mm});
            skArc(sketch, "E1609", {"start": v(-25.3, 14.45) * mm, "mid": v(-25.5, 14.25) * mm, "end": v(-25.7, 14.45) * mm});
            skArc(sketch, "E1610", {"start": v(-25.4, 13.75) * mm, "mid": v(-25.5, 13.85) * mm, "end": v(-25.6, 13.75) * mm});
            skArc(sketch, "E1611", {"start": v(-25.6, 13.75) * mm, "mid": v(-25.5, 13.65) * mm, "end": v(-25.4, 13.75) * mm});
            skArc(sketch, "E1612", {"start": v(-25.3, 13.05) * mm, "mid": v(-25.5, 13.25) * mm, "end": v(-25.7, 13.05) * mm});
            skLineSegment(sketch, "E1613", {"start": v(-25.7, 14.45) * mm, "end": v(-27, 14.45) * mm});
            skLineSegment(sketch, "E1614", {"start": v(-27, 14.45) * mm, "end": v(-27, 13.05) * mm});
            skLineSegment(sketch, "E1615", {"start": v(-27, 13.05) * mm, "end": v(-25.7, 13.05) * mm});
            skLineSegment(sketch, "E1616", {"start": v(-26.75, 1.75) * mm, "end": v(-26.75, 2.75) * mm});
            skLineSegment(sketch, "E1617", {"start": v(-26.75, 2.75) * mm, "end": v(-25.75, 2.75) * mm});
            skLineSegment(sketch, "E1618", {"start": v(-25.75, 2.75) * mm, "end": v(-25.75, 1.75) * mm});
            skLineSegment(sketch, "E1619", {"start": v(-25.75, 1.75) * mm, "end": v(-26.75, 1.75) * mm});
            skLineSegment(sketch, "E1620", {"start": v(-25.25, 1.75) * mm, "end": v(-25.25, 2.75) * mm});
            skLineSegment(sketch, "E1621", {"start": v(-25.25, 2.75) * mm, "end": v(-24.25, 2.75) * mm});
            skLineSegment(sketch, "E1622", {"start": v(-24.25, 2.75) * mm, "end": v(-24.25, 1.75) * mm});
            skLineSegment(sketch, "E1623", {"start": v(-24.25, 1.75) * mm, "end": v(-25.25, 1.75) * mm});
            skLineSegment(sketch, "E1624", {"start": v(-25.7, 2.95) * mm, "end": v(-27, 2.95) * mm});
            skLineSegment(sketch, "E1625", {"start": v(-27, 2.95) * mm, "end": v(-27, 1.55) * mm});
            skLineSegment(sketch, "E1626", {"start": v(-27, 1.55) * mm, "end": v(-25.7, 1.55) * mm});
            skArc(sketch, "E1627", {"start": v(-25.7, 1.55) * mm, "mid": v(-25.5, 1.75) * mm, "end": v(-25.3, 1.55) * mm});
            skArc(sketch, "E1628", {"start": v(-25.4, 2.25) * mm, "mid": v(-25.5, 2.35) * mm, "end": v(-25.6, 2.25) * mm});
            skArc(sketch, "E1629", {"start": v(-25.6, 2.25) * mm, "mid": v(-25.5, 2.15) * mm, "end": v(-25.4, 2.25) * mm});
            skArc(sketch, "E1630", {"start": v(-25.7, 2.95) * mm, "mid": v(-25.5, 2.75) * mm, "end": v(-25.3, 2.95) * mm});
            skLineSegment(sketch, "E1631", {"start": v(-25.3, 1.55) * mm, "end": v(-24, 1.55) * mm});
            skLineSegment(sketch, "E1632", {"start": v(-24, 1.55) * mm, "end": v(-24, 2.95) * mm});
            skLineSegment(sketch, "E1633", {"start": v(-24, 2.95) * mm, "end": v(-25.3, 2.95) * mm});
            skLineSegment(sketch, "E1634", {"start": v(-24.25, -1.75) * mm, "end": v(-24.25, -2.75) * mm});
            skLineSegment(sketch, "E1635", {"start": v(-24.25, -2.75) * mm, "end": v(-25.25, -2.75) * mm});
            skLineSegment(sketch, "E1636", {"start": v(-25.25, -2.75) * mm, "end": v(-25.25, -1.75) * mm});
            skLineSegment(sketch, "E1637", {"start": v(-25.25, -1.75) * mm, "end": v(-24.25, -1.75) * mm});
            skLineSegment(sketch, "E1638", {"start": v(-25.75, -1.75) * mm, "end": v(-25.75, -2.75) * mm});
            skLineSegment(sketch, "E1639", {"start": v(-25.75, -2.75) * mm, "end": v(-26.75, -2.75) * mm});
            skLineSegment(sketch, "E1640", {"start": v(-26.75, -2.75) * mm, "end": v(-26.75, -1.75) * mm});
            skLineSegment(sketch, "E1641", {"start": v(-26.75, -1.75) * mm, "end": v(-25.75, -1.75) * mm});
            skLineSegment(sketch, "E1642", {"start": v(-25.3, -2.95) * mm, "end": v(-24, -2.95) * mm});
            skLineSegment(sketch, "E1643", {"start": v(-24, -2.95) * mm, "end": v(-24, -1.55) * mm});
            skLineSegment(sketch, "E1644", {"start": v(-24, -1.55) * mm, "end": v(-25.3, -1.55) * mm});
            skArc(sketch, "E1645", {"start": v(-25.3, -1.55) * mm, "mid": v(-25.5, -1.75) * mm, "end": v(-25.7, -1.55) * mm});
            skArc(sketch, "E1646", {"start": v(-25.4, -2.25) * mm, "mid": v(-25.5, -2.15) * mm, "end": v(-25.6, -2.25) * mm});
            skArc(sketch, "E1647", {"start": v(-25.6, -2.25) * mm, "mid": v(-25.5, -2.35) * mm, "end": v(-25.4, -2.25) * mm});
            skArc(sketch, "E1648", {"start": v(-25.3, -2.95) * mm, "mid": v(-25.5, -2.75) * mm, "end": v(-25.7, -2.95) * mm});
            skLineSegment(sketch, "E1649", {"start": v(-25.7, -1.55) * mm, "end": v(-27, -1.55) * mm});
            skLineSegment(sketch, "E1650", {"start": v(-27, -1.55) * mm, "end": v(-27, -2.95) * mm});
            skLineSegment(sketch, "E1651", {"start": v(-27, -2.95) * mm, "end": v(-25.7, -2.95) * mm});
            skLineSegment(sketch, "E1652", {"start": v(-26.75, -6.25) * mm, "end": v(-26.75, -5.25) * mm});
            skLineSegment(sketch, "E1653", {"start": v(-26.75, -5.25) * mm, "end": v(-25.75, -5.25) * mm});
            skLineSegment(sketch, "E1654", {"start": v(-25.75, -5.25) * mm, "end": v(-25.75, -6.25) * mm});
            skLineSegment(sketch, "E1655", {"start": v(-25.75, -6.25) * mm, "end": v(-26.75, -6.25) * mm});
            skLineSegment(sketch, "E1656", {"start": v(-25.25, -6.25) * mm, "end": v(-25.25, -5.25) * mm});
            skLineSegment(sketch, "E1657", {"start": v(-25.25, -5.25) * mm, "end": v(-24.25, -5.25) * mm});
            skLineSegment(sketch, "E1658", {"start": v(-24.25, -5.25) * mm, "end": v(-24.25, -6.25) * mm});
            skLineSegment(sketch, "E1659", {"start": v(-24.25, -6.25) * mm, "end": v(-25.25, -6.25) * mm});
            skLineSegment(sketch, "E1660", {"start": v(-25.7, -5.05) * mm, "end": v(-27, -5.05) * mm});
            skLineSegment(sketch, "E1661", {"start": v(-27, -5.05) * mm, "end": v(-27, -6.45) * mm});
            skLineSegment(sketch, "E1662", {"start": v(-27, -6.45) * mm, "end": v(-25.7, -6.45) * mm});
            skArc(sketch, "E1663", {"start": v(-25.7, -6.45) * mm, "mid": v(-25.5, -6.25) * mm, "end": v(-25.3, -6.45) * mm});
            skArc(sketch, "E1664", {"start": v(-25.4, -5.75) * mm, "mid": v(-25.5, -5.65) * mm, "end": v(-25.6, -5.75) * mm});
            skArc(sketch, "E1665", {"start": v(-25.6, -5.75) * mm, "mid": v(-25.5, -5.85) * mm, "end": v(-25.4, -5.75) * mm});
            skArc(sketch, "E1666", {"start": v(-25.7, -5.05) * mm, "mid": v(-25.5, -5.25) * mm, "end": v(-25.3, -5.05) * mm});
            skLineSegment(sketch, "E1667", {"start": v(-25.3, -6.45) * mm, "end": v(-24, -6.45) * mm});
            skLineSegment(sketch, "E1668", {"start": v(-24, -6.45) * mm, "end": v(-24, -5.05) * mm});
            skLineSegment(sketch, "E1669", {"start": v(-24, -5.05) * mm, "end": v(-25.3, -5.05) * mm});
            skLineSegment(sketch, "E1670", {"start": v(-24.25, -9.75) * mm, "end": v(-24.25, -10.75) * mm});
            skLineSegment(sketch, "E1671", {"start": v(-24.25, -10.75) * mm, "end": v(-25.25, -10.75) * mm});
            skLineSegment(sketch, "E1672", {"start": v(-25.25, -10.75) * mm, "end": v(-25.25, -9.75) * mm});
            skLineSegment(sketch, "E1673", {"start": v(-25.25, -9.75) * mm, "end": v(-24.25, -9.75) * mm});
            skLineSegment(sketch, "E1674", {"start": v(-25.75, -9.75) * mm, "end": v(-25.75, -10.75) * mm});
            skLineSegment(sketch, "E1675", {"start": v(-25.75, -10.75) * mm, "end": v(-26.75, -10.75) * mm});
            skLineSegment(sketch, "E1676", {"start": v(-26.75, -10.75) * mm, "end": v(-26.75, -9.75) * mm});
            skLineSegment(sketch, "E1677", {"start": v(-26.75, -9.75) * mm, "end": v(-25.75, -9.75) * mm});
            skLineSegment(sketch, "E1678", {"start": v(-25.3, -10.95) * mm, "end": v(-24, -10.95) * mm});
            skLineSegment(sketch, "E1679", {"start": v(-24, -10.95) * mm, "end": v(-24, -9.55) * mm});
            skLineSegment(sketch, "E1680", {"start": v(-24, -9.55) * mm, "end": v(-25.3, -9.55) * mm});
            skArc(sketch, "E1681", {"start": v(-25.3, -9.55) * mm, "mid": v(-25.5, -9.75) * mm, "end": v(-25.7, -9.55) * mm});
            skArc(sketch, "E1682", {"start": v(-25.4, -10.25) * mm, "mid": v(-25.5, -10.15) * mm, "end": v(-25.6, -10.25) * mm});
            skArc(sketch, "E1683", {"start": v(-25.6, -10.25) * mm, "mid": v(-25.5, -10.35) * mm, "end": v(-25.4, -10.25) * mm});
            skArc(sketch, "E1684", {"start": v(-25.3, -10.95) * mm, "mid": v(-25.5, -10.75) * mm, "end": v(-25.7, -10.95) * mm});
            skLineSegment(sketch, "E1685", {"start": v(-25.7, -9.55) * mm, "end": v(-27, -9.55) * mm});
            skLineSegment(sketch, "E1686", {"start": v(-27, -9.55) * mm, "end": v(-27, -10.95) * mm});
            skLineSegment(sketch, "E1687", {"start": v(-27, -10.95) * mm, "end": v(-25.7, -10.95) * mm});
            skLineSegment(sketch, "E1688", {"start": v(-24.25, 33.25) * mm, "end": v(-24.25, 32.25) * mm});
            skLineSegment(sketch, "E1689", {"start": v(-24.25, 32.25) * mm, "end": v(-25.25, 32.25) * mm});
            skLineSegment(sketch, "E1690", {"start": v(-25.25, 32.25) * mm, "end": v(-25.25, 33.25) * mm});
            skLineSegment(sketch, "E1691", {"start": v(-25.25, 33.25) * mm, "end": v(-24.25, 33.25) * mm});
            skLineSegment(sketch, "E1692", {"start": v(-25.75, 33.25) * mm, "end": v(-25.75, 32.25) * mm});
            skLineSegment(sketch, "E1693", {"start": v(-25.75, 32.25) * mm, "end": v(-26.75, 32.25) * mm});
            skLineSegment(sketch, "E1694", {"start": v(-26.75, 32.25) * mm, "end": v(-26.75, 33.25) * mm});
            skLineSegment(sketch, "E1695", {"start": v(-26.75, 33.25) * mm, "end": v(-25.75, 33.25) * mm});
            skLineSegment(sketch, "E1696", {"start": v(-25.3, 32.05) * mm, "end": v(-24, 32.05) * mm});
            skLineSegment(sketch, "E1697", {"start": v(-24, 32.05) * mm, "end": v(-24, 33.45) * mm});
            skLineSegment(sketch, "E1698", {"start": v(-24, 33.45) * mm, "end": v(-25.3, 33.45) * mm});
            skArc(sketch, "E1699", {"start": v(-25.3, 33.45) * mm, "mid": v(-25.5, 33.25) * mm, "end": v(-25.7, 33.45) * mm});
            skArc(sketch, "E1700", {"start": v(-25.4, 32.75) * mm, "mid": v(-25.5, 32.85) * mm, "end": v(-25.6, 32.75) * mm});
            skArc(sketch, "E1701", {"start": v(-25.6, 32.75) * mm, "mid": v(-25.5, 32.65) * mm, "end": v(-25.4, 32.75) * mm});
            skArc(sketch, "E1702", {"start": v(-25.3, 32.05) * mm, "mid": v(-25.5, 32.25) * mm, "end": v(-25.7, 32.05) * mm});
            skLineSegment(sketch, "E1703", {"start": v(-25.7, 33.45) * mm, "end": v(-27, 33.45) * mm});
            skLineSegment(sketch, "E1704", {"start": v(-27, 33.45) * mm, "end": v(-27, 32.05) * mm});
            skLineSegment(sketch, "E1705", {"start": v(-27, 32.05) * mm, "end": v(-25.7, 32.05) * mm});
            skLineSegment(sketch, "E1706", {"start": v(-24.25, 31.75) * mm, "end": v(-24.25, 30.75) * mm});
            skLineSegment(sketch, "E1707", {"start": v(-24.25, 30.75) * mm, "end": v(-25.25, 30.75) * mm});
            skLineSegment(sketch, "E1708", {"start": v(-25.25, 30.75) * mm, "end": v(-25.25, 31.75) * mm});
            skLineSegment(sketch, "E1709", {"start": v(-25.25, 31.75) * mm, "end": v(-24.25, 31.75) * mm});
            skLineSegment(sketch, "E1710", {"start": v(-25.75, 31.75) * mm, "end": v(-25.75, 30.75) * mm});
            skLineSegment(sketch, "E1711", {"start": v(-25.75, 30.75) * mm, "end": v(-26.75, 30.75) * mm});
            skLineSegment(sketch, "E1712", {"start": v(-26.75, 30.75) * mm, "end": v(-26.75, 31.75) * mm});
            skLineSegment(sketch, "E1713", {"start": v(-26.75, 31.75) * mm, "end": v(-25.75, 31.75) * mm});
            skLineSegment(sketch, "E1714", {"start": v(-25.3, 30.55) * mm, "end": v(-24, 30.55) * mm});
            skLineSegment(sketch, "E1715", {"start": v(-24, 30.55) * mm, "end": v(-24, 31.95) * mm});
            skLineSegment(sketch, "E1716", {"start": v(-24, 31.95) * mm, "end": v(-25.3, 31.95) * mm});
            skArc(sketch, "E1717", {"start": v(-25.3, 31.95) * mm, "mid": v(-25.5, 31.75) * mm, "end": v(-25.7, 31.95) * mm});
            skArc(sketch, "E1718", {"start": v(-25.4, 31.25) * mm, "mid": v(-25.5, 31.35) * mm, "end": v(-25.6, 31.25) * mm});
            skArc(sketch, "E1719", {"start": v(-25.6, 31.25) * mm, "mid": v(-25.5, 31.15) * mm, "end": v(-25.4, 31.25) * mm});
            skArc(sketch, "E1720", {"start": v(-25.3, 30.55) * mm, "mid": v(-25.5, 30.75) * mm, "end": v(-25.7, 30.55) * mm});
            skLineSegment(sketch, "E1721", {"start": v(-25.7, 31.95) * mm, "end": v(-27, 31.95) * mm});
            skLineSegment(sketch, "E1722", {"start": v(-27, 31.95) * mm, "end": v(-27, 30.55) * mm});
            skLineSegment(sketch, "E1723", {"start": v(-27, 30.55) * mm, "end": v(-25.7, 30.55) * mm});
            skLineSegment(sketch, "E1724", {"start": v(-24.25, 25.25) * mm, "end": v(-24.25, 24.25) * mm});
            skLineSegment(sketch, "E1725", {"start": v(-24.25, 24.25) * mm, "end": v(-25.25, 24.25) * mm});
            skLineSegment(sketch, "E1726", {"start": v(-25.25, 24.25) * mm, "end": v(-25.25, 25.25) * mm});
            skLineSegment(sketch, "E1727", {"start": v(-25.25, 25.25) * mm, "end": v(-24.25, 25.25) * mm});
            skLineSegment(sketch, "E1728", {"start": v(-25.75, 25.25) * mm, "end": v(-25.75, 24.25) * mm});
            skLineSegment(sketch, "E1729", {"start": v(-25.75, 24.25) * mm, "end": v(-26.75, 24.25) * mm});
            skLineSegment(sketch, "E1730", {"start": v(-26.75, 24.25) * mm, "end": v(-26.75, 25.25) * mm});
            skLineSegment(sketch, "E1731", {"start": v(-26.75, 25.25) * mm, "end": v(-25.75, 25.25) * mm});
            skLineSegment(sketch, "E1732", {"start": v(-25.3, 24.05) * mm, "end": v(-24, 24.05) * mm});
            skLineSegment(sketch, "E1733", {"start": v(-24, 24.05) * mm, "end": v(-24, 25.45) * mm});
            skLineSegment(sketch, "E1734", {"start": v(-24, 25.45) * mm, "end": v(-25.3, 25.45) * mm});
            skArc(sketch, "E1735", {"start": v(-25.3, 25.45) * mm, "mid": v(-25.5, 25.25) * mm, "end": v(-25.7, 25.45) * mm});
            skArc(sketch, "E1736", {"start": v(-25.4, 24.75) * mm, "mid": v(-25.5, 24.85) * mm, "end": v(-25.6, 24.75) * mm});
            skArc(sketch, "E1737", {"start": v(-25.6, 24.75) * mm, "mid": v(-25.5, 24.65) * mm, "end": v(-25.4, 24.75) * mm});
            skArc(sketch, "E1738", {"start": v(-25.3, 24.05) * mm, "mid": v(-25.5, 24.25) * mm, "end": v(-25.7, 24.05) * mm});
            skLineSegment(sketch, "E1739", {"start": v(-25.7, 25.45) * mm, "end": v(-27, 25.45) * mm});
            skLineSegment(sketch, "E1740", {"start": v(-27, 25.45) * mm, "end": v(-27, 24.05) * mm});
            skLineSegment(sketch, "E1741", {"start": v(-27, 24.05) * mm, "end": v(-25.7, 24.05) * mm});
            skLineSegment(sketch, "E1742", {"start": v(-24.25, 23.75) * mm, "end": v(-24.25, 22.75) * mm});
            skLineSegment(sketch, "E1743", {"start": v(-24.25, 22.75) * mm, "end": v(-25.25, 22.75) * mm});
            skLineSegment(sketch, "E1744", {"start": v(-25.25, 22.75) * mm, "end": v(-25.25, 23.75) * mm});
            skLineSegment(sketch, "E1745", {"start": v(-25.25, 23.75) * mm, "end": v(-24.25, 23.75) * mm});
            skLineSegment(sketch, "E1746", {"start": v(-25.75, 23.75) * mm, "end": v(-25.75, 22.75) * mm});
            skLineSegment(sketch, "E1747", {"start": v(-25.75, 22.75) * mm, "end": v(-26.75, 22.75) * mm});
            skLineSegment(sketch, "E1748", {"start": v(-26.75, 22.75) * mm, "end": v(-26.75, 23.75) * mm});
            skLineSegment(sketch, "E1749", {"start": v(-26.75, 23.75) * mm, "end": v(-25.75, 23.75) * mm});
            skLineSegment(sketch, "E1750", {"start": v(-25.3, 22.55) * mm, "end": v(-24, 22.55) * mm});
            skLineSegment(sketch, "E1751", {"start": v(-24, 22.55) * mm, "end": v(-24, 23.95) * mm});
            skLineSegment(sketch, "E1752", {"start": v(-24, 23.95) * mm, "end": v(-25.3, 23.95) * mm});
            skArc(sketch, "E1753", {"start": v(-25.3, 23.95) * mm, "mid": v(-25.5, 23.75) * mm, "end": v(-25.7, 23.95) * mm});
            skArc(sketch, "E1754", {"start": v(-25.4, 23.25) * mm, "mid": v(-25.5, 23.35) * mm, "end": v(-25.6, 23.25) * mm});
            skArc(sketch, "E1755", {"start": v(-25.6, 23.25) * mm, "mid": v(-25.5, 23.15) * mm, "end": v(-25.4, 23.25) * mm});
            skArc(sketch, "E1756", {"start": v(-25.3, 22.55) * mm, "mid": v(-25.5, 22.75) * mm, "end": v(-25.7, 22.55) * mm});
            skLineSegment(sketch, "E1757", {"start": v(-25.7, 23.95) * mm, "end": v(-27, 23.95) * mm});
            skLineSegment(sketch, "E1758", {"start": v(-27, 23.95) * mm, "end": v(-27, 22.55) * mm});
            skLineSegment(sketch, "E1759", {"start": v(-27, 22.55) * mm, "end": v(-25.7, 22.55) * mm});
            skLineSegment(sketch, "E1760", {"start": v(-24.25, 17.25) * mm, "end": v(-24.25, 16.25) * mm});
            skLineSegment(sketch, "E1761", {"start": v(-24.25, 16.25) * mm, "end": v(-25.25, 16.25) * mm});
            skLineSegment(sketch, "E1762", {"start": v(-25.25, 16.25) * mm, "end": v(-25.25, 17.25) * mm});
            skLineSegment(sketch, "E1763", {"start": v(-25.25, 17.25) * mm, "end": v(-24.25, 17.25) * mm});
            skLineSegment(sketch, "E1764", {"start": v(-25.75, 17.25) * mm, "end": v(-25.75, 16.25) * mm});
            skLineSegment(sketch, "E1765", {"start": v(-25.75, 16.25) * mm, "end": v(-26.75, 16.25) * mm});
            skLineSegment(sketch, "E1766", {"start": v(-26.75, 16.25) * mm, "end": v(-26.75, 17.25) * mm});
            skLineSegment(sketch, "E1767", {"start": v(-26.75, 17.25) * mm, "end": v(-25.75, 17.25) * mm});
            skLineSegment(sketch, "E1768", {"start": v(-25.3, 16.05) * mm, "end": v(-24, 16.05) * mm});
            skLineSegment(sketch, "E1769", {"start": v(-24, 16.05) * mm, "end": v(-24, 17.45) * mm});
            skLineSegment(sketch, "E1770", {"start": v(-24, 17.45) * mm, "end": v(-25.3, 17.45) * mm});
            skArc(sketch, "E1771", {"start": v(-25.3, 17.45) * mm, "mid": v(-25.5, 17.25) * mm, "end": v(-25.7, 17.45) * mm});
            skArc(sketch, "E1772", {"start": v(-25.4, 16.75) * mm, "mid": v(-25.5, 16.85) * mm, "end": v(-25.6, 16.75) * mm});
            skArc(sketch, "E1773", {"start": v(-25.6, 16.75) * mm, "mid": v(-25.5, 16.65) * mm, "end": v(-25.4, 16.75) * mm});
            skArc(sketch, "E1774", {"start": v(-25.3, 16.05) * mm, "mid": v(-25.5, 16.25) * mm, "end": v(-25.7, 16.05) * mm});
            skLineSegment(sketch, "E1775", {"start": v(-25.7, 17.45) * mm, "end": v(-27, 17.45) * mm});
            skLineSegment(sketch, "E1776", {"start": v(-27, 17.45) * mm, "end": v(-27, 16.05) * mm});
            skLineSegment(sketch, "E1777", {"start": v(-27, 16.05) * mm, "end": v(-25.7, 16.05) * mm});
            skLineSegment(sketch, "E1778", {"start": v(-24.25, 15.75) * mm, "end": v(-24.25, 14.75) * mm});
            skLineSegment(sketch, "E1779", {"start": v(-24.25, 14.75) * mm, "end": v(-25.25, 14.75) * mm});
            skLineSegment(sketch, "E1780", {"start": v(-25.25, 14.75) * mm, "end": v(-25.25, 15.75) * mm});
            skLineSegment(sketch, "E1781", {"start": v(-25.25, 15.75) * mm, "end": v(-24.25, 15.75) * mm});
            skLineSegment(sketch, "E1782", {"start": v(-25.75, 15.75) * mm, "end": v(-25.75, 14.75) * mm});
            skLineSegment(sketch, "E1783", {"start": v(-25.75, 14.75) * mm, "end": v(-26.75, 14.75) * mm});
            skLineSegment(sketch, "E1784", {"start": v(-26.75, 14.75) * mm, "end": v(-26.75, 15.75) * mm});
            skLineSegment(sketch, "E1785", {"start": v(-26.75, 15.75) * mm, "end": v(-25.75, 15.75) * mm});
            skLineSegment(sketch, "E1786", {"start": v(-25.3, 14.55) * mm, "end": v(-24, 14.55) * mm});
            skLineSegment(sketch, "E1787", {"start": v(-24, 14.55) * mm, "end": v(-24, 15.95) * mm});
            skLineSegment(sketch, "E1788", {"start": v(-24, 15.95) * mm, "end": v(-25.3, 15.95) * mm});
            skArc(sketch, "E1789", {"start": v(-25.3, 15.95) * mm, "mid": v(-25.5, 15.75) * mm, "end": v(-25.7, 15.95) * mm});
            skArc(sketch, "E1790", {"start": v(-25.4, 15.25) * mm, "mid": v(-25.5, 15.35) * mm, "end": v(-25.6, 15.25) * mm});
            skArc(sketch, "E1791", {"start": v(-25.6, 15.25) * mm, "mid": v(-25.5, 15.15) * mm, "end": v(-25.4, 15.25) * mm});
            skArc(sketch, "E1792", {"start": v(-25.3, 14.55) * mm, "mid": v(-25.5, 14.75) * mm, "end": v(-25.7, 14.55) * mm});
            skLineSegment(sketch, "E1793", {"start": v(-25.7, 15.95) * mm, "end": v(-27, 15.95) * mm});
            skLineSegment(sketch, "E1794", {"start": v(-27, 15.95) * mm, "end": v(-27, 14.55) * mm});
            skLineSegment(sketch, "E1795", {"start": v(-27, 14.55) * mm, "end": v(-25.7, 14.55) * mm});
            skLineSegment(sketch, "E1796", {"start": v(-24.25, 9.25) * mm, "end": v(-24.25, 8.25) * mm});
            skLineSegment(sketch, "E1797", {"start": v(-24.25, 8.25) * mm, "end": v(-25.25, 8.25) * mm});
            skLineSegment(sketch, "E1798", {"start": v(-25.25, 8.25) * mm, "end": v(-25.25, 9.25) * mm});
            skLineSegment(sketch, "E1799", {"start": v(-25.25, 9.25) * mm, "end": v(-24.25, 9.25) * mm});
            skLineSegment(sketch, "E1800", {"start": v(-25.75, 9.25) * mm, "end": v(-25.75, 8.25) * mm});
            skLineSegment(sketch, "E1801", {"start": v(-25.75, 8.25) * mm, "end": v(-26.75, 8.25) * mm});
            skLineSegment(sketch, "E1802", {"start": v(-26.75, 8.25) * mm, "end": v(-26.75, 9.25) * mm});
            skLineSegment(sketch, "E1803", {"start": v(-26.75, 9.25) * mm, "end": v(-25.75, 9.25) * mm});
            skLineSegment(sketch, "E1804", {"start": v(-25.3, 8.05) * mm, "end": v(-24, 8.05) * mm});
            skLineSegment(sketch, "E1805", {"start": v(-24, 8.05) * mm, "end": v(-24, 9.45) * mm});
            skLineSegment(sketch, "E1806", {"start": v(-24, 9.45) * mm, "end": v(-25.3, 9.45) * mm});
            skArc(sketch, "E1807", {"start": v(-25.3, 9.45) * mm, "mid": v(-25.5, 9.25) * mm, "end": v(-25.7, 9.45) * mm});
            skArc(sketch, "E1808", {"start": v(-25.4, 8.75) * mm, "mid": v(-25.5, 8.85) * mm, "end": v(-25.6, 8.75) * mm});
            skArc(sketch, "E1809", {"start": v(-25.6, 8.75) * mm, "mid": v(-25.5, 8.65) * mm, "end": v(-25.4, 8.75) * mm});
            skArc(sketch, "E1810", {"start": v(-25.3, 8.05) * mm, "mid": v(-25.5, 8.25) * mm, "end": v(-25.7, 8.05) * mm});
            skLineSegment(sketch, "E1811", {"start": v(-25.7, 9.45) * mm, "end": v(-27, 9.45) * mm});
            skLineSegment(sketch, "E1812", {"start": v(-27, 9.45) * mm, "end": v(-27, 8.05) * mm});
            skLineSegment(sketch, "E1813", {"start": v(-27, 8.05) * mm, "end": v(-25.7, 8.05) * mm});
            skLineSegment(sketch, "E1814", {"start": v(-24.25, 7.75) * mm, "end": v(-24.25, 6.75) * mm});
            skLineSegment(sketch, "E1815", {"start": v(-24.25, 6.75) * mm, "end": v(-25.25, 6.75) * mm});
            skLineSegment(sketch, "E1816", {"start": v(-25.25, 6.75) * mm, "end": v(-25.25, 7.75) * mm});
            skLineSegment(sketch, "E1817", {"start": v(-25.25, 7.75) * mm, "end": v(-24.25, 7.75) * mm});
            skLineSegment(sketch, "E1818", {"start": v(-25.75, 7.75) * mm, "end": v(-25.75, 6.75) * mm});
            skLineSegment(sketch, "E1819", {"start": v(-25.75, 6.75) * mm, "end": v(-26.75, 6.75) * mm});
            skLineSegment(sketch, "E1820", {"start": v(-26.75, 6.75) * mm, "end": v(-26.75, 7.75) * mm});
            skLineSegment(sketch, "E1821", {"start": v(-26.75, 7.75) * mm, "end": v(-25.75, 7.75) * mm});
            skLineSegment(sketch, "E1822", {"start": v(-25.3, 6.55) * mm, "end": v(-24, 6.55) * mm});
            skLineSegment(sketch, "E1823", {"start": v(-24, 6.55) * mm, "end": v(-24, 7.95) * mm});
            skLineSegment(sketch, "E1824", {"start": v(-24, 7.95) * mm, "end": v(-25.3, 7.95) * mm});
            skArc(sketch, "E1825", {"start": v(-25.3, 7.95) * mm, "mid": v(-25.5, 7.75) * mm, "end": v(-25.7, 7.95) * mm});
            skArc(sketch, "E1826", {"start": v(-25.4, 7.25) * mm, "mid": v(-25.5, 7.35) * mm, "end": v(-25.6, 7.25) * mm});
            skArc(sketch, "E1827", {"start": v(-25.6, 7.25) * mm, "mid": v(-25.5, 7.15) * mm, "end": v(-25.4, 7.25) * mm});
            skArc(sketch, "E1828", {"start": v(-25.3, 6.55) * mm, "mid": v(-25.5, 6.75) * mm, "end": v(-25.7, 6.55) * mm});
            skLineSegment(sketch, "E1829", {"start": v(-25.7, 7.95) * mm, "end": v(-27, 7.95) * mm});
            skLineSegment(sketch, "E1830", {"start": v(-27, 7.95) * mm, "end": v(-27, 6.55) * mm});
            skLineSegment(sketch, "E1831", {"start": v(-27, 6.55) * mm, "end": v(-25.7, 6.55) * mm});
            skLineSegment(sketch, "E1832", {"start": v(-24.25, 1.25) * mm, "end": v(-24.25, 0.25) * mm});
            skLineSegment(sketch, "E1833", {"start": v(-24.25, 0.25) * mm, "end": v(-25.25, 0.25) * mm});
            skLineSegment(sketch, "E1834", {"start": v(-25.25, 0.25) * mm, "end": v(-25.25, 1.25) * mm});
            skLineSegment(sketch, "E1835", {"start": v(-25.25, 1.25) * mm, "end": v(-24.25, 1.25) * mm});
            skLineSegment(sketch, "E1836", {"start": v(-25.75, 1.25) * mm, "end": v(-25.75, 0.25) * mm});
            skLineSegment(sketch, "E1837", {"start": v(-25.75, 0.25) * mm, "end": v(-26.75, 0.25) * mm});
            skLineSegment(sketch, "E1838", {"start": v(-26.75, 0.25) * mm, "end": v(-26.75, 1.25) * mm});
            skLineSegment(sketch, "E1839", {"start": v(-26.75, 1.25) * mm, "end": v(-25.75, 1.25) * mm});
            skLineSegment(sketch, "E1840", {"start": v(-25.3, 0.05) * mm, "end": v(-24, 0.05) * mm});
            skLineSegment(sketch, "E1841", {"start": v(-24, 0.05) * mm, "end": v(-24, 1.45) * mm});
            skLineSegment(sketch, "E1842", {"start": v(-24, 1.45) * mm, "end": v(-25.3, 1.45) * mm});
            skArc(sketch, "E1843", {"start": v(-25.3, 1.45) * mm, "mid": v(-25.5, 1.25) * mm, "end": v(-25.7, 1.45) * mm});
            skArc(sketch, "E1844", {"start": v(-25.4, 0.75) * mm, "mid": v(-25.5, 0.85) * mm, "end": v(-25.6, 0.75) * mm});
            skArc(sketch, "E1845", {"start": v(-25.6, 0.75) * mm, "mid": v(-25.5, 0.65) * mm, "end": v(-25.4, 0.75) * mm});
            skArc(sketch, "E1846", {"start": v(-25.3, 0.05) * mm, "mid": v(-25.5, 0.25) * mm, "end": v(-25.7, 0.05) * mm});
            skLineSegment(sketch, "E1847", {"start": v(-25.7, 1.45) * mm, "end": v(-27, 1.45) * mm});
            skLineSegment(sketch, "E1848", {"start": v(-27, 1.45) * mm, "end": v(-27, 0.05) * mm});
            skLineSegment(sketch, "E1849", {"start": v(-27, 0.05) * mm, "end": v(-25.7, 0.05) * mm});
            skLineSegment(sketch, "E1850", {"start": v(-24.25, -0.25) * mm, "end": v(-24.25, -1.25) * mm});
            skLineSegment(sketch, "E1851", {"start": v(-24.25, -1.25) * mm, "end": v(-25.25, -1.25) * mm});
            skLineSegment(sketch, "E1852", {"start": v(-25.25, -1.25) * mm, "end": v(-25.25, -0.25) * mm});
            skLineSegment(sketch, "E1853", {"start": v(-25.25, -0.25) * mm, "end": v(-24.25, -0.25) * mm});
            skLineSegment(sketch, "E1854", {"start": v(-25.75, -0.25) * mm, "end": v(-25.75, -1.25) * mm});
            skLineSegment(sketch, "E1855", {"start": v(-25.75, -1.25) * mm, "end": v(-26.75, -1.25) * mm});
            skLineSegment(sketch, "E1856", {"start": v(-26.75, -1.25) * mm, "end": v(-26.75, -0.25) * mm});
            skLineSegment(sketch, "E1857", {"start": v(-26.75, -0.25) * mm, "end": v(-25.75, -0.25) * mm});
            skLineSegment(sketch, "E1858", {"start": v(-25.3, -1.45) * mm, "end": v(-24, -1.45) * mm});
            skLineSegment(sketch, "E1859", {"start": v(-24, -1.45) * mm, "end": v(-24, -0.05) * mm});
            skLineSegment(sketch, "E1860", {"start": v(-24, -0.05) * mm, "end": v(-25.3, -0.05) * mm});
            skArc(sketch, "E1861", {"start": v(-25.3, -0.05) * mm, "mid": v(-25.5, -0.25) * mm, "end": v(-25.7, -0.05) * mm});
            skArc(sketch, "E1862", {"start": v(-25.4, -0.75) * mm, "mid": v(-25.5, -0.65) * mm, "end": v(-25.6, -0.75) * mm});
            skArc(sketch, "E1863", {"start": v(-25.6, -0.75) * mm, "mid": v(-25.5, -0.85) * mm, "end": v(-25.4, -0.75) * mm});
            skArc(sketch, "E1864", {"start": v(-25.3, -1.45) * mm, "mid": v(-25.5, -1.25) * mm, "end": v(-25.7, -1.45) * mm});
            skLineSegment(sketch, "E1865", {"start": v(-25.7, -0.05) * mm, "end": v(-27, -0.05) * mm});
            skLineSegment(sketch, "E1866", {"start": v(-27, -0.05) * mm, "end": v(-27, -1.45) * mm});
            skLineSegment(sketch, "E1867", {"start": v(-27, -1.45) * mm, "end": v(-25.7, -1.45) * mm});
            skLineSegment(sketch, "E1868", {"start": v(-24.25, -6.75) * mm, "end": v(-24.25, -7.75) * mm});
            skLineSegment(sketch, "E1869", {"start": v(-24.25, -7.75) * mm, "end": v(-25.25, -7.75) * mm});
            skLineSegment(sketch, "E1870", {"start": v(-25.25, -7.75) * mm, "end": v(-25.25, -6.75) * mm});
            skLineSegment(sketch, "E1871", {"start": v(-25.25, -6.75) * mm, "end": v(-24.25, -6.75) * mm});
            skLineSegment(sketch, "E1872", {"start": v(-25.75, -6.75) * mm, "end": v(-25.75, -7.75) * mm});
            skLineSegment(sketch, "E1873", {"start": v(-25.75, -7.75) * mm, "end": v(-26.75, -7.75) * mm});
            skLineSegment(sketch, "E1874", {"start": v(-26.75, -7.75) * mm, "end": v(-26.75, -6.75) * mm});
            skLineSegment(sketch, "E1875", {"start": v(-26.75, -6.75) * mm, "end": v(-25.75, -6.75) * mm});
            skLineSegment(sketch, "E1876", {"start": v(-25.3, -7.95) * mm, "end": v(-24, -7.95) * mm});
            skLineSegment(sketch, "E1877", {"start": v(-24, -7.95) * mm, "end": v(-24, -6.55) * mm});
            skLineSegment(sketch, "E1878", {"start": v(-24, -6.55) * mm, "end": v(-25.3, -6.55) * mm});
            skArc(sketch, "E1879", {"start": v(-25.3, -6.55) * mm, "mid": v(-25.5, -6.75) * mm, "end": v(-25.7, -6.55) * mm});
            skArc(sketch, "E1880", {"start": v(-25.4, -7.25) * mm, "mid": v(-25.5, -7.15) * mm, "end": v(-25.6, -7.25) * mm});
            skArc(sketch, "E1881", {"start": v(-25.6, -7.25) * mm, "mid": v(-25.5, -7.35) * mm, "end": v(-25.4, -7.25) * mm});
            skArc(sketch, "E1882", {"start": v(-25.3, -7.95) * mm, "mid": v(-25.5, -7.75) * mm, "end": v(-25.7, -7.95) * mm});
            skLineSegment(sketch, "E1883", {"start": v(-25.7, -6.55) * mm, "end": v(-27, -6.55) * mm});
            skLineSegment(sketch, "E1884", {"start": v(-27, -6.55) * mm, "end": v(-27, -7.95) * mm});
            skLineSegment(sketch, "E1885", {"start": v(-27, -7.95) * mm, "end": v(-25.7, -7.95) * mm});
            skLineSegment(sketch, "E1886", {"start": v(5, -40) * mm, "end": v(4, -40) * mm});
            skLineSegment(sketch, "E1887", {"start": v(4, -40) * mm, "end": v(4, -39) * mm});
            skLineSegment(sketch, "E1888", {"start": v(4, -39) * mm, "end": v(5, -39) * mm});
            skLineSegment(sketch, "E1889", {"start": v(5, -39) * mm, "end": v(5, -40) * mm});
            skLineSegment(sketch, "E1890", {"start": v(5, -38.5) * mm, "end": v(4, -38.5) * mm});
            skLineSegment(sketch, "E1891", {"start": v(4, -38.5) * mm, "end": v(4, -37.5) * mm});
            skLineSegment(sketch, "E1892", {"start": v(4, -37.5) * mm, "end": v(5, -37.5) * mm});
            skLineSegment(sketch, "E1893", {"start": v(5, -37.5) * mm, "end": v(5, -38.5) * mm});
            skLineSegment(sketch, "E1894", {"start": v(3.8, -38.95) * mm, "end": v(3.8, -40.25) * mm});
            skLineSegment(sketch, "E1895", {"start": v(3.8, -40.25) * mm, "end": v(5.2, -40.25) * mm});
            skLineSegment(sketch, "E1896", {"start": v(5.2, -40.25) * mm, "end": v(5.2, -38.95) * mm});
            skArc(sketch, "E1897", {"start": v(5.2, -38.95) * mm, "mid": v(5, -38.75) * mm, "end": v(5.2, -38.55) * mm});
            skArc(sketch, "E1898", {"start": v(4.6, -38.75) * mm, "mid": v(4.5, -38.65) * mm, "end": v(4.4, -38.75) * mm});
            skArc(sketch, "E1899", {"start": v(4.4, -38.75) * mm, "mid": v(4.5, -38.85) * mm, "end": v(4.6, -38.75) * mm});
            skArc(sketch, "E1900", {"start": v(3.8, -38.95) * mm, "mid": v(4, -38.75) * mm, "end": v(3.8, -38.55) * mm});
            skLineSegment(sketch, "E1901", {"start": v(5.2, -38.55) * mm, "end": v(5.2, -37.25) * mm});
            skLineSegment(sketch, "E1902", {"start": v(5.2, -37.25) * mm, "end": v(3.8, -37.25) * mm});
            skLineSegment(sketch, "E1903", {"start": v(3.8, -37.25) * mm, "end": v(3.8, -38.55) * mm});
            skLineSegment(sketch, "E1904", {"start": v(15, 13.75) * mm, "end": v(16, 13.75) * mm});
            skLineSegment(sketch, "E1905", {"start": v(16, 13.75) * mm, "end": v(16, 12.75) * mm});
            skLineSegment(sketch, "E1906", {"start": v(16, 12.75) * mm, "end": v(15, 12.75) * mm});
            skLineSegment(sketch, "E1907", {"start": v(15, 12.75) * mm, "end": v(15, 13.75) * mm});
            skLineSegment(sketch, "E1908", {"start": v(15, 12.25) * mm, "end": v(16, 12.25) * mm});
            skLineSegment(sketch, "E1909", {"start": v(16, 12.25) * mm, "end": v(16, 11.25) * mm});
            skLineSegment(sketch, "E1910", {"start": v(16, 11.25) * mm, "end": v(15, 11.25) * mm});
            skLineSegment(sketch, "E1911", {"start": v(15, 11.25) * mm, "end": v(15, 12.25) * mm});
            skLineSegment(sketch, "E1912", {"start": v(16.2, 12.7) * mm, "end": v(16.2, 14) * mm});
            skLineSegment(sketch, "E1913", {"start": v(16.2, 14) * mm, "end": v(14.8, 14) * mm});
            skLineSegment(sketch, "E1914", {"start": v(14.8, 14) * mm, "end": v(14.8, 12.7) * mm});
            skArc(sketch, "E1915", {"start": v(14.8, 12.7) * mm, "mid": v(15, 12.5) * mm, "end": v(14.8, 12.3) * mm});
            skArc(sketch, "E1916", {"start": v(15.6, 12.5) * mm, "mid": v(15.5, 12.6) * mm, "end": v(15.4, 12.5) * mm});
            skArc(sketch, "E1917", {"start": v(15.4, 12.5) * mm, "mid": v(15.5, 12.4) * mm, "end": v(15.6, 12.5) * mm});
            skArc(sketch, "E1918", {"start": v(16.2, 12.7) * mm, "mid": v(16, 12.5) * mm, "end": v(16.2, 12.3) * mm});
            skLineSegment(sketch, "E1919", {"start": v(14.8, 12.3) * mm, "end": v(14.8, 11) * mm});
            skLineSegment(sketch, "E1920", {"start": v(14.8, 11) * mm, "end": v(16.2, 11) * mm});
            skLineSegment(sketch, "E1921", {"start": v(16.2, 11) * mm, "end": v(16.2, 12.3) * mm});
            skLineSegment(sketch, "E1922", {"start": v(5, -10.75) * mm, "end": v(6, -10.75) * mm});
            skLineSegment(sketch, "E1923", {"start": v(6, -10.75) * mm, "end": v(6, -11.75) * mm});
            skLineSegment(sketch, "E1924", {"start": v(6, -11.75) * mm, "end": v(5, -11.75) * mm});
            skLineSegment(sketch, "E1925", {"start": v(5, -11.75) * mm, "end": v(5, -10.75) * mm});
            skLineSegment(sketch, "E1926", {"start": v(5, -12.25) * mm, "end": v(6, -12.25) * mm});
            skLineSegment(sketch, "E1927", {"start": v(6, -12.25) * mm, "end": v(6, -13.25) * mm});
            skLineSegment(sketch, "E1928", {"start": v(6, -13.25) * mm, "end": v(5, -13.25) * mm});
            skLineSegment(sketch, "E1929", {"start": v(5, -13.25) * mm, "end": v(5, -12.25) * mm});
            skLineSegment(sketch, "E1930", {"start": v(6.2, -11.8) * mm, "end": v(6.2, -10.5) * mm});
            skLineSegment(sketch, "E1931", {"start": v(6.2, -10.5) * mm, "end": v(4.8, -10.5) * mm});
            skLineSegment(sketch, "E1932", {"start": v(4.8, -10.5) * mm, "end": v(4.8, -11.8) * mm});
            skArc(sketch, "E1933", {"start": v(4.8, -11.8) * mm, "mid": v(5, -12) * mm, "end": v(4.8, -12.2) * mm});
            skArc(sketch, "E1934", {"start": v(5.6, -12) * mm, "mid": v(5.5, -11.9) * mm, "end": v(5.4, -12) * mm});
            skArc(sketch, "E1935", {"start": v(5.4, -12) * mm, "mid": v(5.5, -12.1) * mm, "end": v(5.6, -12) * mm});
            skArc(sketch, "E1936", {"start": v(6.2, -11.8) * mm, "mid": v(6, -12) * mm, "end": v(6.2, -12.2) * mm});
            skLineSegment(sketch, "E1937", {"start": v(4.8, -12.2) * mm, "end": v(4.8, -13.5) * mm});
            skLineSegment(sketch, "E1938", {"start": v(4.8, -13.5) * mm, "end": v(6.2, -13.5) * mm});
            skLineSegment(sketch, "E1939", {"start": v(6.2, -13.5) * mm, "end": v(6.2, -12.2) * mm});
            skLineSegment(sketch, "E1940", {"start": v(-5.5, -22.25) * mm, "end": v(-6.5, -22.25) * mm});
            skLineSegment(sketch, "E1941", {"start": v(-6.5, -22.25) * mm, "end": v(-6.5, -21.25) * mm});
            skLineSegment(sketch, "E1942", {"start": v(-6.5, -21.25) * mm, "end": v(-5.5, -21.25) * mm});
            skLineSegment(sketch, "E1943", {"start": v(-5.5, -21.25) * mm, "end": v(-5.5, -22.25) * mm});
            skLineSegment(sketch, "E1944", {"start": v(-5.5, -20.75) * mm, "end": v(-6.5, -20.75) * mm});
            skLineSegment(sketch, "E1945", {"start": v(-6.5, -20.75) * mm, "end": v(-6.5, -19.75) * mm});
            skLineSegment(sketch, "E1946", {"start": v(-6.5, -19.75) * mm, "end": v(-5.5, -19.75) * mm});
            skLineSegment(sketch, "E1947", {"start": v(-5.5, -19.75) * mm, "end": v(-5.5, -20.75) * mm});
            skLineSegment(sketch, "E1948", {"start": v(-6.7, -21.2) * mm, "end": v(-6.7, -22.5) * mm});
            skLineSegment(sketch, "E1949", {"start": v(-6.7, -22.5) * mm, "end": v(-5.3, -22.5) * mm});
            skLineSegment(sketch, "E1950", {"start": v(-5.3, -22.5) * mm, "end": v(-5.3, -21.2) * mm});
            skArc(sketch, "E1951", {"start": v(-5.3, -21.2) * mm, "mid": v(-5.5, -21) * mm, "end": v(-5.3, -20.8) * mm});
            skArc(sketch, "E1952", {"start": v(-5.9, -21) * mm, "mid": v(-6, -20.9) * mm, "end": v(-6.1, -21) * mm});
            skArc(sketch, "E1953", {"start": v(-6.1, -21) * mm, "mid": v(-6, -21.1) * mm, "end": v(-5.9, -21) * mm});
            skArc(sketch, "E1954", {"start": v(-6.7, -21.2) * mm, "mid": v(-6.5, -21) * mm, "end": v(-6.7, -20.8) * mm});
            skLineSegment(sketch, "E1955", {"start": v(-5.3, -20.8) * mm, "end": v(-5.3, -19.5) * mm});
            skLineSegment(sketch, "E1956", {"start": v(-5.3, -19.5) * mm, "end": v(-6.7, -19.5) * mm});
            skLineSegment(sketch, "E1957", {"start": v(-6.7, -19.5) * mm, "end": v(-6.7, -20.8) * mm});
            skLineSegment(sketch, "E1958", {"start": v(-24.25, -16.25) * mm, "end": v(-24.25, -17.25) * mm});
            skLineSegment(sketch, "E1959", {"start": v(-24.25, -17.25) * mm, "end": v(-25.25, -17.25) * mm});
            skLineSegment(sketch, "E1960", {"start": v(-25.25, -17.25) * mm, "end": v(-25.25, -16.25) * mm});
            skLineSegment(sketch, "E1961", {"start": v(-25.25, -16.25) * mm, "end": v(-24.25, -16.25) * mm});
            skLineSegment(sketch, "E1962", {"start": v(-25.75, -16.25) * mm, "end": v(-25.75, -17.25) * mm});
            skLineSegment(sketch, "E1963", {"start": v(-25.75, -17.25) * mm, "end": v(-26.75, -17.25) * mm});
            skLineSegment(sketch, "E1964", {"start": v(-26.75, -17.25) * mm, "end": v(-26.75, -16.25) * mm});
            skLineSegment(sketch, "E1965", {"start": v(-26.75, -16.25) * mm, "end": v(-25.75, -16.25) * mm});
            skLineSegment(sketch, "E1966", {"start": v(-25.3, -17.45) * mm, "end": v(-24, -17.45) * mm});
            skLineSegment(sketch, "E1967", {"start": v(-24, -17.45) * mm, "end": v(-24, -16.05) * mm});
            skLineSegment(sketch, "E1968", {"start": v(-24, -16.05) * mm, "end": v(-25.3, -16.05) * mm});
            skArc(sketch, "E1969", {"start": v(-25.3, -16.05) * mm, "mid": v(-25.5, -16.25) * mm, "end": v(-25.7, -16.05) * mm});
            skArc(sketch, "E1970", {"start": v(-25.4, -16.75) * mm, "mid": v(-25.5, -16.65) * mm, "end": v(-25.6, -16.75) * mm});
            skArc(sketch, "E1971", {"start": v(-25.6, -16.75) * mm, "mid": v(-25.5, -16.85) * mm, "end": v(-25.4, -16.75) * mm});
            skArc(sketch, "E1972", {"start": v(-25.3, -17.45) * mm, "mid": v(-25.5, -17.25) * mm, "end": v(-25.7, -17.45) * mm});
            skLineSegment(sketch, "E1973", {"start": v(-25.7, -16.05) * mm, "end": v(-27, -16.05) * mm});
            skLineSegment(sketch, "E1974", {"start": v(-27, -16.05) * mm, "end": v(-27, -17.45) * mm});
            skLineSegment(sketch, "E1975", {"start": v(-27, -17.45) * mm, "end": v(-25.7, -17.45) * mm});
            skLineSegment(sketch, "E1976", {"start": v(14, 11.25) * mm, "end": v(13, 11.25) * mm});
            skLineSegment(sketch, "E1977", {"start": v(13, 11.25) * mm, "end": v(13, 12.25) * mm});
            skLineSegment(sketch, "E1978", {"start": v(13, 12.25) * mm, "end": v(14, 12.25) * mm});
            skLineSegment(sketch, "E1979", {"start": v(14, 12.25) * mm, "end": v(14, 11.25) * mm});
            skLineSegment(sketch, "E1980", {"start": v(14, 12.75) * mm, "end": v(13, 12.75) * mm});
            skLineSegment(sketch, "E1981", {"start": v(13, 12.75) * mm, "end": v(13, 13.75) * mm});
            skLineSegment(sketch, "E1982", {"start": v(13, 13.75) * mm, "end": v(14, 13.75) * mm});
            skLineSegment(sketch, "E1983", {"start": v(14, 13.75) * mm, "end": v(14, 12.75) * mm});
            skLineSegment(sketch, "E1984", {"start": v(12.8, 12.3) * mm, "end": v(12.8, 11) * mm});
            skLineSegment(sketch, "E1985", {"start": v(12.8, 11) * mm, "end": v(14.2, 11) * mm});
            skLineSegment(sketch, "E1986", {"start": v(14.2, 11) * mm, "end": v(14.2, 12.3) * mm});
            skArc(sketch, "E1987", {"start": v(14.2, 12.3) * mm, "mid": v(14, 12.5) * mm, "end": v(14.2, 12.7) * mm});
            skArc(sketch, "E1988", {"start": v(13.6, 12.5) * mm, "mid": v(13.5, 12.6) * mm, "end": v(13.4, 12.5) * mm});
            skArc(sketch, "E1989", {"start": v(13.4, 12.5) * mm, "mid": v(13.5, 12.4) * mm, "end": v(13.6, 12.5) * mm});
            skArc(sketch, "E1990", {"start": v(12.8, 12.3) * mm, "mid": v(13, 12.5) * mm, "end": v(12.8, 12.7) * mm});
            skLineSegment(sketch, "E1991", {"start": v(14.2, 12.7) * mm, "end": v(14.2, 14) * mm});
            skLineSegment(sketch, "E1992", {"start": v(14.2, 14) * mm, "end": v(12.8, 14) * mm});
            skLineSegment(sketch, "E1993", {"start": v(12.8, 14) * mm, "end": v(12.8, 12.7) * mm});
            skLineSegment(sketch, "E1994", {"start": v(-1, 11.5) * mm, "end": v(-1, 10.5) * mm});
            skLineSegment(sketch, "E1995", {"start": v(-1, 10.5) * mm, "end": v(-2, 10.5) * mm});
            skLineSegment(sketch, "E1996", {"start": v(-2, 10.5) * mm, "end": v(-2, 11.5) * mm});
            skLineSegment(sketch, "E1997", {"start": v(-2, 11.5) * mm, "end": v(-1, 11.5) * mm});
            skLineSegment(sketch, "E1998", {"start": v(-2.5, 11.5) * mm, "end": v(-2.5, 10.5) * mm});
            skLineSegment(sketch, "E1999", {"start": v(-2.5, 10.5) * mm, "end": v(-3.5, 10.5) * mm});
            skLineSegment(sketch, "E2000", {"start": v(-3.5, 10.5) * mm, "end": v(-3.5, 11.5) * mm});
            skLineSegment(sketch, "E2001", {"start": v(-3.5, 11.5) * mm, "end": v(-2.5, 11.5) * mm});
            skLineSegment(sketch, "E2002", {"start": v(-2.05, 10.3) * mm, "end": v(-0.75, 10.3) * mm});
            skLineSegment(sketch, "E2003", {"start": v(-0.75, 10.3) * mm, "end": v(-0.75, 11.7) * mm});
            skLineSegment(sketch, "E2004", {"start": v(-0.75, 11.7) * mm, "end": v(-2.05, 11.7) * mm});
            skArc(sketch, "E2005", {"start": v(-2.05, 11.7) * mm, "mid": v(-2.25, 11.5) * mm, "end": v(-2.45, 11.7) * mm});
            skArc(sketch, "E2006", {"start": v(-2.15, 11) * mm, "mid": v(-2.25, 11.1) * mm, "end": v(-2.35, 11) * mm});
            skArc(sketch, "E2007", {"start": v(-2.35, 11) * mm, "mid": v(-2.25, 10.9) * mm, "end": v(-2.15, 11) * mm});
            skArc(sketch, "E2008", {"start": v(-2.05, 10.3) * mm, "mid": v(-2.25, 10.5) * mm, "end": v(-2.45, 10.3) * mm});
            skLineSegment(sketch, "E2009", {"start": v(-2.45, 11.7) * mm, "end": v(-3.75, 11.7) * mm});
            skLineSegment(sketch, "E2010", {"start": v(-3.75, 11.7) * mm, "end": v(-3.75, 10.3) * mm});
            skLineSegment(sketch, "E2011", {"start": v(-3.75, 10.3) * mm, "end": v(-2.45, 10.3) * mm});
            skLineSegment(sketch, "E2012", {"start": v(9.5, 11.25) * mm, "end": v(8.5, 11.25) * mm});
            skLineSegment(sketch, "E2013", {"start": v(8.5, 11.25) * mm, "end": v(8.5, 12.25) * mm});
            skLineSegment(sketch, "E2014", {"start": v(8.5, 12.25) * mm, "end": v(9.5, 12.25) * mm});
            skLineSegment(sketch, "E2015", {"start": v(9.5, 12.25) * mm, "end": v(9.5, 11.25) * mm});
            skLineSegment(sketch, "E2016", {"start": v(9.5, 12.75) * mm, "end": v(8.5, 12.75) * mm});
            skLineSegment(sketch, "E2017", {"start": v(8.5, 12.75) * mm, "end": v(8.5, 13.75) * mm});
            skLineSegment(sketch, "E2018", {"start": v(8.5, 13.75) * mm, "end": v(9.5, 13.75) * mm});
            skLineSegment(sketch, "E2019", {"start": v(9.5, 13.75) * mm, "end": v(9.5, 12.75) * mm});
            skLineSegment(sketch, "E2020", {"start": v(8.3, 12.3) * mm, "end": v(8.3, 11) * mm});
            skLineSegment(sketch, "E2021", {"start": v(8.3, 11) * mm, "end": v(9.7, 11) * mm});
            skLineSegment(sketch, "E2022", {"start": v(9.7, 11) * mm, "end": v(9.7, 12.3) * mm});
            skArc(sketch, "E2023", {"start": v(9.7, 12.3) * mm, "mid": v(9.5, 12.5) * mm, "end": v(9.7, 12.7) * mm});
            skArc(sketch, "E2024", {"start": v(9.1, 12.5) * mm, "mid": v(9, 12.6) * mm, "end": v(8.9, 12.5) * mm});
            skArc(sketch, "E2025", {"start": v(8.9, 12.5) * mm, "mid": v(9, 12.4) * mm, "end": v(9.1, 12.5) * mm});
            skArc(sketch, "E2026", {"start": v(8.3, 12.3) * mm, "mid": v(8.5, 12.5) * mm, "end": v(8.3, 12.7) * mm});
            skLineSegment(sketch, "E2027", {"start": v(9.7, 12.7) * mm, "end": v(9.7, 14) * mm});
            skLineSegment(sketch, "E2028", {"start": v(9.7, 14) * mm, "end": v(8.3, 14) * mm});
            skLineSegment(sketch, "E2029", {"start": v(8.3, 14) * mm, "end": v(8.3, 12.7) * mm});
            skLineSegment(sketch, "E2030", {"start": v(7, 13.75) * mm, "end": v(8, 13.75) * mm});
            skLineSegment(sketch, "E2031", {"start": v(8, 13.75) * mm, "end": v(8, 12.75) * mm});
            skLineSegment(sketch, "E2032", {"start": v(8, 12.75) * mm, "end": v(7, 12.75) * mm});
            skLineSegment(sketch, "E2033", {"start": v(7, 12.75) * mm, "end": v(7, 13.75) * mm});
            skLineSegment(sketch, "E2034", {"start": v(7, 12.25) * mm, "end": v(8, 12.25) * mm});
            skLineSegment(sketch, "E2035", {"start": v(8, 12.25) * mm, "end": v(8, 11.25) * mm});
            skLineSegment(sketch, "E2036", {"start": v(8, 11.25) * mm, "end": v(7, 11.25) * mm});
            skLineSegment(sketch, "E2037", {"start": v(7, 11.25) * mm, "end": v(7, 12.25) * mm});
            skLineSegment(sketch, "E2038", {"start": v(8.2, 12.7) * mm, "end": v(8.2, 14) * mm});
            skLineSegment(sketch, "E2039", {"start": v(8.2, 14) * mm, "end": v(6.8, 14) * mm});
            skLineSegment(sketch, "E2040", {"start": v(6.8, 14) * mm, "end": v(6.8, 12.7) * mm});
            skArc(sketch, "E2041", {"start": v(6.8, 12.7) * mm, "mid": v(7, 12.5) * mm, "end": v(6.8, 12.3) * mm});
            skArc(sketch, "E2042", {"start": v(7.6, 12.5) * mm, "mid": v(7.5, 12.6) * mm, "end": v(7.4, 12.5) * mm});
            skArc(sketch, "E2043", {"start": v(7.4, 12.5) * mm, "mid": v(7.5, 12.4) * mm, "end": v(7.6, 12.5) * mm});
            skArc(sketch, "E2044", {"start": v(8.2, 12.7) * mm, "mid": v(8, 12.5) * mm, "end": v(8.2, 12.3) * mm});
            skLineSegment(sketch, "E2045", {"start": v(6.8, 12.3) * mm, "end": v(6.8, 11) * mm});
            skLineSegment(sketch, "E2046", {"start": v(6.8, 11) * mm, "end": v(8.2, 11) * mm});
            skLineSegment(sketch, "E2047", {"start": v(8.2, 11) * mm, "end": v(8.2, 12.3) * mm});
            skLineSegment(sketch, "E2048", {"start": v(-6.5, -11.25) * mm, "end": v(-7.5, -11.25) * mm});
            skLineSegment(sketch, "E2049", {"start": v(-7.5, -11.25) * mm, "end": v(-7.5, -10.25) * mm});
            skLineSegment(sketch, "E2050", {"start": v(-7.5, -10.25) * mm, "end": v(-6.5, -10.25) * mm});
            skLineSegment(sketch, "E2051", {"start": v(-6.5, -10.25) * mm, "end": v(-6.5, -11.25) * mm});
            skLineSegment(sketch, "E2052", {"start": v(-6.5, -9.75) * mm, "end": v(-7.5, -9.75) * mm});
            skLineSegment(sketch, "E2053", {"start": v(-7.5, -9.75) * mm, "end": v(-7.5, -8.75) * mm});
            skLineSegment(sketch, "E2054", {"start": v(-7.5, -8.75) * mm, "end": v(-6.5, -8.75) * mm});
            skLineSegment(sketch, "E2055", {"start": v(-6.5, -8.75) * mm, "end": v(-6.5, -9.75) * mm});
            skLineSegment(sketch, "E2056", {"start": v(-7.7, -10.2) * mm, "end": v(-7.7, -11.5) * mm});
            skLineSegment(sketch, "E2057", {"start": v(-7.7, -11.5) * mm, "end": v(-6.3, -11.5) * mm});
            skLineSegment(sketch, "E2058", {"start": v(-6.3, -11.5) * mm, "end": v(-6.3, -10.2) * mm});
            skArc(sketch, "E2059", {"start": v(-6.3, -10.2) * mm, "mid": v(-6.5, -10) * mm, "end": v(-6.3, -9.8) * mm});
            skArc(sketch, "E2060", {"start": v(-6.9, -10) * mm, "mid": v(-7, -9.9) * mm, "end": v(-7.1, -10) * mm});
            skArc(sketch, "E2061", {"start": v(-7.1, -10) * mm, "mid": v(-7, -10.1) * mm, "end": v(-6.9, -10) * mm});
            skArc(sketch, "E2062", {"start": v(-7.7, -10.2) * mm, "mid": v(-7.5, -10) * mm, "end": v(-7.7, -9.8) * mm});
            skLineSegment(sketch, "E2063", {"start": v(-6.3, -9.8) * mm, "end": v(-6.3, -8.5) * mm});
            skLineSegment(sketch, "E2064", {"start": v(-6.3, -8.5) * mm, "end": v(-7.7, -8.5) * mm});
            skLineSegment(sketch, "E2065", {"start": v(-7.7, -8.5) * mm, "end": v(-7.7, -9.8) * mm});
            skLineSegment(sketch, "E2066", {"start": v(-13, -24.75) * mm, "end": v(-14, -24.75) * mm});
            skLineSegment(sketch, "E2067", {"start": v(-14, -24.75) * mm, "end": v(-14, -23.75) * mm});
            skLineSegment(sketch, "E2068", {"start": v(-14, -23.75) * mm, "end": v(-13, -23.75) * mm});
            skLineSegment(sketch, "E2069", {"start": v(-13, -23.75) * mm, "end": v(-13, -24.75) * mm});
            skLineSegment(sketch, "E2070", {"start": v(-13, -23.25) * mm, "end": v(-14, -23.25) * mm});
            skLineSegment(sketch, "E2071", {"start": v(-14, -23.25) * mm, "end": v(-14, -22.25) * mm});
            skLineSegment(sketch, "E2072", {"start": v(-14, -22.25) * mm, "end": v(-13, -22.25) * mm});
            skLineSegment(sketch, "E2073", {"start": v(-13, -22.25) * mm, "end": v(-13, -23.25) * mm});
            skLineSegment(sketch, "E2074", {"start": v(-14.2, -23.7) * mm, "end": v(-14.2, -25) * mm});
            skLineSegment(sketch, "E2075", {"start": v(-14.2, -25) * mm, "end": v(-12.8, -25) * mm});
            skLineSegment(sketch, "E2076", {"start": v(-12.8, -25) * mm, "end": v(-12.8, -23.7) * mm});
            skArc(sketch, "E2077", {"start": v(-12.8, -23.7) * mm, "mid": v(-13, -23.5) * mm, "end": v(-12.8, -23.3) * mm});
            skArc(sketch, "E2078", {"start": v(-13.4, -23.5) * mm, "mid": v(-13.5, -23.4) * mm, "end": v(-13.6, -23.5) * mm});
            skArc(sketch, "E2079", {"start": v(-13.6, -23.5) * mm, "mid": v(-13.5, -23.6) * mm, "end": v(-13.4, -23.5) * mm});
            skArc(sketch, "E2080", {"start": v(-14.2, -23.7) * mm, "mid": v(-14, -23.5) * mm, "end": v(-14.2, -23.3) * mm});
            skLineSegment(sketch, "E2081", {"start": v(-12.8, -23.3) * mm, "end": v(-12.8, -22) * mm});
            skLineSegment(sketch, "E2082", {"start": v(-12.8, -22) * mm, "end": v(-14.2, -22) * mm});
            skLineSegment(sketch, "E2083", {"start": v(-14.2, -22) * mm, "end": v(-14.2, -23.3) * mm});
            skLineSegment(sketch, "E2084", {"start": v(-12.5, -22.25) * mm, "end": v(-11.5, -22.25) * mm});
            skLineSegment(sketch, "E2085", {"start": v(-11.5, -22.25) * mm, "end": v(-11.5, -23.25) * mm});
            skLineSegment(sketch, "E2086", {"start": v(-11.5, -23.25) * mm, "end": v(-12.5, -23.25) * mm});
            skLineSegment(sketch, "E2087", {"start": v(-12.5, -23.25) * mm, "end": v(-12.5, -22.25) * mm});
            skLineSegment(sketch, "E2088", {"start": v(-12.5, -23.75) * mm, "end": v(-11.5, -23.75) * mm});
            skLineSegment(sketch, "E2089", {"start": v(-11.5, -23.75) * mm, "end": v(-11.5, -24.75) * mm});
            skLineSegment(sketch, "E2090", {"start": v(-11.5, -24.75) * mm, "end": v(-12.5, -24.75) * mm});
            skLineSegment(sketch, "E2091", {"start": v(-12.5, -24.75) * mm, "end": v(-12.5, -23.75) * mm});
            skLineSegment(sketch, "E2092", {"start": v(-11.3, -23.3) * mm, "end": v(-11.3, -22) * mm});
            skLineSegment(sketch, "E2093", {"start": v(-11.3, -22) * mm, "end": v(-12.7, -22) * mm});
            skLineSegment(sketch, "E2094", {"start": v(-12.7, -22) * mm, "end": v(-12.7, -23.3) * mm});
            skArc(sketch, "E2095", {"start": v(-12.7, -23.3) * mm, "mid": v(-12.5, -23.5) * mm, "end": v(-12.7, -23.7) * mm});
            skArc(sketch, "E2096", {"start": v(-11.9, -23.5) * mm, "mid": v(-12, -23.4) * mm, "end": v(-12.1, -23.5) * mm});
            skArc(sketch, "E2097", {"start": v(-12.1, -23.5) * mm, "mid": v(-12, -23.6) * mm, "end": v(-11.9, -23.5) * mm});
            skArc(sketch, "E2098", {"start": v(-11.3, -23.3) * mm, "mid": v(-11.5, -23.5) * mm, "end": v(-11.3, -23.7) * mm});
            skLineSegment(sketch, "E2099", {"start": v(-12.7, -23.7) * mm, "end": v(-12.7, -25) * mm});
            skLineSegment(sketch, "E2100", {"start": v(-12.7, -25) * mm, "end": v(-11.3, -25) * mm});
            skLineSegment(sketch, "E2101", {"start": v(-11.3, -25) * mm, "end": v(-11.3, -23.7) * mm});
            skLineSegment(sketch, "E2102", {"start": v(8.5, -10.75) * mm, "end": v(9.5, -10.75) * mm});
            skLineSegment(sketch, "E2103", {"start": v(9.5, -10.75) * mm, "end": v(9.5, -11.75) * mm});
            skLineSegment(sketch, "E2104", {"start": v(9.5, -11.75) * mm, "end": v(8.5, -11.75) * mm});
            skLineSegment(sketch, "E2105", {"start": v(8.5, -11.75) * mm, "end": v(8.5, -10.75) * mm});
            skLineSegment(sketch, "E2106", {"start": v(8.5, -12.25) * mm, "end": v(9.5, -12.25) * mm});
            skLineSegment(sketch, "E2107", {"start": v(9.5, -12.25) * mm, "end": v(9.5, -13.25) * mm});
            skLineSegment(sketch, "E2108", {"start": v(9.5, -13.25) * mm, "end": v(8.5, -13.25) * mm});
            skLineSegment(sketch, "E2109", {"start": v(8.5, -13.25) * mm, "end": v(8.5, -12.25) * mm});
            skLineSegment(sketch, "E2110", {"start": v(9.7, -11.8) * mm, "end": v(9.7, -10.5) * mm});
            skLineSegment(sketch, "E2111", {"start": v(9.7, -10.5) * mm, "end": v(8.3, -10.5) * mm});
            skLineSegment(sketch, "E2112", {"start": v(8.3, -10.5) * mm, "end": v(8.3, -11.8) * mm});
            skArc(sketch, "E2113", {"start": v(8.3, -11.8) * mm, "mid": v(8.5, -12) * mm, "end": v(8.3, -12.2) * mm});
            skArc(sketch, "E2114", {"start": v(9.1, -12) * mm, "mid": v(9, -11.9) * mm, "end": v(8.9, -12) * mm});
            skArc(sketch, "E2115", {"start": v(8.9, -12) * mm, "mid": v(9, -12.1) * mm, "end": v(9.1, -12) * mm});
            skArc(sketch, "E2116", {"start": v(9.7, -11.8) * mm, "mid": v(9.5, -12) * mm, "end": v(9.7, -12.2) * mm});
            skLineSegment(sketch, "E2117", {"start": v(8.3, -12.2) * mm, "end": v(8.3, -13.5) * mm});
            skLineSegment(sketch, "E2118", {"start": v(8.3, -13.5) * mm, "end": v(9.7, -13.5) * mm});
            skLineSegment(sketch, "E2119", {"start": v(9.7, -13.5) * mm, "end": v(9.7, -12.2) * mm});
            skLineSegment(sketch, "E2120", {"start": v(5, 11.25) * mm, "end": v(4, 11.25) * mm});
            skLineSegment(sketch, "E2121", {"start": v(4, 11.25) * mm, "end": v(4, 12.25) * mm});
            skLineSegment(sketch, "E2122", {"start": v(4, 12.25) * mm, "end": v(5, 12.25) * mm});
            skLineSegment(sketch, "E2123", {"start": v(5, 12.25) * mm, "end": v(5, 11.25) * mm});
            skLineSegment(sketch, "E2124", {"start": v(5, 12.75) * mm, "end": v(4, 12.75) * mm});
            skLineSegment(sketch, "E2125", {"start": v(4, 12.75) * mm, "end": v(4, 13.75) * mm});
            skLineSegment(sketch, "E2126", {"start": v(4, 13.75) * mm, "end": v(5, 13.75) * mm});
            skLineSegment(sketch, "E2127", {"start": v(5, 13.75) * mm, "end": v(5, 12.75) * mm});
            skLineSegment(sketch, "E2128", {"start": v(3.8, 12.3) * mm, "end": v(3.8, 11) * mm});
            skLineSegment(sketch, "E2129", {"start": v(3.8, 11) * mm, "end": v(5.2, 11) * mm});
            skLineSegment(sketch, "E2130", {"start": v(5.2, 11) * mm, "end": v(5.2, 12.3) * mm});
            skArc(sketch, "E2131", {"start": v(5.2, 12.3) * mm, "mid": v(5, 12.5) * mm, "end": v(5.2, 12.7) * mm});
            skArc(sketch, "E2132", {"start": v(4.6, 12.5) * mm, "mid": v(4.5, 12.6) * mm, "end": v(4.4, 12.5) * mm});
            skArc(sketch, "E2133", {"start": v(4.4, 12.5) * mm, "mid": v(4.5, 12.4) * mm, "end": v(4.6, 12.5) * mm});
            skArc(sketch, "E2134", {"start": v(3.8, 12.3) * mm, "mid": v(4, 12.5) * mm, "end": v(3.8, 12.7) * mm});
            skLineSegment(sketch, "E2135", {"start": v(5.2, 12.7) * mm, "end": v(5.2, 14) * mm});
            skLineSegment(sketch, "E2136", {"start": v(5.2, 14) * mm, "end": v(3.8, 14) * mm});
            skLineSegment(sketch, "E2137", {"start": v(3.8, 14) * mm, "end": v(3.8, 12.7) * mm});
            skLineSegment(sketch, "E2138", {"start": v(-24.25, -17.75) * mm, "end": v(-24.25, -18.75) * mm});
            skLineSegment(sketch, "E2139", {"start": v(-24.25, -18.75) * mm, "end": v(-25.25, -18.75) * mm});
            skLineSegment(sketch, "E2140", {"start": v(-25.25, -18.75) * mm, "end": v(-25.25, -17.75) * mm});
            skLineSegment(sketch, "E2141", {"start": v(-25.25, -17.75) * mm, "end": v(-24.25, -17.75) * mm});
            skLineSegment(sketch, "E2142", {"start": v(-25.75, -17.75) * mm, "end": v(-25.75, -18.75) * mm});
            skLineSegment(sketch, "E2143", {"start": v(-25.75, -18.75) * mm, "end": v(-26.75, -18.75) * mm});
            skLineSegment(sketch, "E2144", {"start": v(-26.75, -18.75) * mm, "end": v(-26.75, -17.75) * mm});
            skLineSegment(sketch, "E2145", {"start": v(-26.75, -17.75) * mm, "end": v(-25.75, -17.75) * mm});
            skLineSegment(sketch, "E2146", {"start": v(-25.3, -18.95) * mm, "end": v(-24, -18.95) * mm});
            skLineSegment(sketch, "E2147", {"start": v(-24, -18.95) * mm, "end": v(-24, -17.55) * mm});
            skLineSegment(sketch, "E2148", {"start": v(-24, -17.55) * mm, "end": v(-25.3, -17.55) * mm});
            skArc(sketch, "E2149", {"start": v(-25.3, -17.55) * mm, "mid": v(-25.5, -17.75) * mm, "end": v(-25.7, -17.55) * mm});
            skArc(sketch, "E2150", {"start": v(-25.4, -18.25) * mm, "mid": v(-25.5, -18.15) * mm, "end": v(-25.6, -18.25) * mm});
            skArc(sketch, "E2151", {"start": v(-25.6, -18.25) * mm, "mid": v(-25.5, -18.35) * mm, "end": v(-25.4, -18.25) * mm});
            skArc(sketch, "E2152", {"start": v(-25.3, -18.95) * mm, "mid": v(-25.5, -18.75) * mm, "end": v(-25.7, -18.95) * mm});
            skLineSegment(sketch, "E2153", {"start": v(-25.7, -17.55) * mm, "end": v(-27, -17.55) * mm});
            skLineSegment(sketch, "E2154", {"start": v(-27, -17.55) * mm, "end": v(-27, -18.95) * mm});
            skLineSegment(sketch, "E2155", {"start": v(-27, -18.95) * mm, "end": v(-25.7, -18.95) * mm});
            skLineSegment(sketch, "E2156", {"start": v(-26.75, -14.25) * mm, "end": v(-26.75, -13.25) * mm});
            skLineSegment(sketch, "E2157", {"start": v(-26.75, -13.25) * mm, "end": v(-25.75, -13.25) * mm});
            skLineSegment(sketch, "E2158", {"start": v(-25.75, -13.25) * mm, "end": v(-25.75, -14.25) * mm});
            skLineSegment(sketch, "E2159", {"start": v(-25.75, -14.25) * mm, "end": v(-26.75, -14.25) * mm});
            skLineSegment(sketch, "E2160", {"start": v(-25.25, -14.25) * mm, "end": v(-25.25, -13.25) * mm});
            skLineSegment(sketch, "E2161", {"start": v(-25.25, -13.25) * mm, "end": v(-24.25, -13.25) * mm});
            skLineSegment(sketch, "E2162", {"start": v(-24.25, -13.25) * mm, "end": v(-24.25, -14.25) * mm});
            skLineSegment(sketch, "E2163", {"start": v(-24.25, -14.25) * mm, "end": v(-25.25, -14.25) * mm});
            skLineSegment(sketch, "E2164", {"start": v(-25.7, -13.05) * mm, "end": v(-27, -13.05) * mm});
            skLineSegment(sketch, "E2165", {"start": v(-27, -13.05) * mm, "end": v(-27, -14.45) * mm});
            skLineSegment(sketch, "E2166", {"start": v(-27, -14.45) * mm, "end": v(-25.7, -14.45) * mm});
            skArc(sketch, "E2167", {"start": v(-25.7, -14.45) * mm, "mid": v(-25.5, -14.25) * mm, "end": v(-25.3, -14.45) * mm});
            skArc(sketch, "E2168", {"start": v(-25.4, -13.75) * mm, "mid": v(-25.5, -13.65) * mm, "end": v(-25.6, -13.75) * mm});
            skArc(sketch, "E2169", {"start": v(-25.6, -13.75) * mm, "mid": v(-25.5, -13.85) * mm, "end": v(-25.4, -13.75) * mm});
            skArc(sketch, "E2170", {"start": v(-25.7, -13.05) * mm, "mid": v(-25.5, -13.25) * mm, "end": v(-25.3, -13.05) * mm});
            skLineSegment(sketch, "E2171", {"start": v(-25.3, -14.45) * mm, "end": v(-24, -14.45) * mm});
            skLineSegment(sketch, "E2172", {"start": v(-24, -14.45) * mm, "end": v(-24, -13.05) * mm});
            skLineSegment(sketch, "E2173", {"start": v(-24, -13.05) * mm, "end": v(-25.3, -13.05) * mm});
            skLineSegment(sketch, "E2174", {"start": v(6.75, -10.75) * mm, "end": v(7.75, -10.75) * mm});
            skLineSegment(sketch, "E2175", {"start": v(7.75, -10.75) * mm, "end": v(7.75, -11.75) * mm});
            skLineSegment(sketch, "E2176", {"start": v(7.75, -11.75) * mm, "end": v(6.75, -11.75) * mm});
            skLineSegment(sketch, "E2177", {"start": v(6.75, -11.75) * mm, "end": v(6.75, -10.75) * mm});
            skLineSegment(sketch, "E2178", {"start": v(6.75, -12.25) * mm, "end": v(7.75, -12.25) * mm});
            skLineSegment(sketch, "E2179", {"start": v(7.75, -12.25) * mm, "end": v(7.75, -13.25) * mm});
            skLineSegment(sketch, "E2180", {"start": v(7.75, -13.25) * mm, "end": v(6.75, -13.25) * mm});
            skLineSegment(sketch, "E2181", {"start": v(6.75, -13.25) * mm, "end": v(6.75, -12.25) * mm});
            skLineSegment(sketch, "E2182", {"start": v(7.95, -11.8) * mm, "end": v(7.95, -10.5) * mm});
            skLineSegment(sketch, "E2183", {"start": v(7.95, -10.5) * mm, "end": v(6.55, -10.5) * mm});
            skLineSegment(sketch, "E2184", {"start": v(6.55, -10.5) * mm, "end": v(6.55, -11.8) * mm});
            skArc(sketch, "E2185", {"start": v(6.55, -11.8) * mm, "mid": v(6.75, -12) * mm, "end": v(6.55, -12.2) * mm});
            skArc(sketch, "E2186", {"start": v(7.35, -12) * mm, "mid": v(7.25, -11.9) * mm, "end": v(7.15, -12) * mm});
            skArc(sketch, "E2187", {"start": v(7.15, -12) * mm, "mid": v(7.25, -12.1) * mm, "end": v(7.35, -12) * mm});
            skArc(sketch, "E2188", {"start": v(7.95, -11.8) * mm, "mid": v(7.75, -12) * mm, "end": v(7.95, -12.2) * mm});
            skLineSegment(sketch, "E2189", {"start": v(6.55, -12.2) * mm, "end": v(6.55, -13.5) * mm});
            skLineSegment(sketch, "E2190", {"start": v(6.55, -13.5) * mm, "end": v(7.95, -13.5) * mm});
            skLineSegment(sketch, "E2191", {"start": v(7.95, -13.5) * mm, "end": v(7.95, -12.2) * mm});
            skLineSegment(sketch, "E2192", {"start": v(-2.5, 2.25) * mm, "end": v(-3.5, 2.25) * mm});
            skLineSegment(sketch, "E2193", {"start": v(-3.5, 2.25) * mm, "end": v(-3.5, 3.25) * mm});
            skLineSegment(sketch, "E2194", {"start": v(-3.5, 3.25) * mm, "end": v(-2.5, 3.25) * mm});
            skLineSegment(sketch, "E2195", {"start": v(-2.5, 3.25) * mm, "end": v(-2.5, 2.25) * mm});
            skLineSegment(sketch, "E2196", {"start": v(-2.5, 3.75) * mm, "end": v(-3.5, 3.75) * mm});
            skLineSegment(sketch, "E2197", {"start": v(-3.5, 3.75) * mm, "end": v(-3.5, 4.75) * mm});
            skLineSegment(sketch, "E2198", {"start": v(-3.5, 4.75) * mm, "end": v(-2.5, 4.75) * mm});
            skLineSegment(sketch, "E2199", {"start": v(-2.5, 4.75) * mm, "end": v(-2.5, 3.75) * mm});
            skLineSegment(sketch, "E2200", {"start": v(-3.7, 3.3) * mm, "end": v(-3.7, 2) * mm});
            skLineSegment(sketch, "E2201", {"start": v(-3.7, 2) * mm, "end": v(-2.3, 2) * mm});
            skLineSegment(sketch, "E2202", {"start": v(-2.3, 2) * mm, "end": v(-2.3, 3.3) * mm});
            skArc(sketch, "E2203", {"start": v(-2.3, 3.3) * mm, "mid": v(-2.5, 3.5) * mm, "end": v(-2.3, 3.7) * mm});
            skArc(sketch, "E2204", {"start": v(-2.9, 3.5) * mm, "mid": v(-3, 3.6) * mm, "end": v(-3.1, 3.5) * mm});
            skArc(sketch, "E2205", {"start": v(-3.1, 3.5) * mm, "mid": v(-3, 3.4) * mm, "end": v(-2.9, 3.5) * mm});
            skArc(sketch, "E2206", {"start": v(-3.7, 3.3) * mm, "mid": v(-3.5, 3.5) * mm, "end": v(-3.7, 3.7) * mm});
            skLineSegment(sketch, "E2207", {"start": v(-2.3, 3.7) * mm, "end": v(-2.3, 5) * mm});
            skLineSegment(sketch, "E2208", {"start": v(-2.3, 5) * mm, "end": v(-3.7, 5) * mm});
            skLineSegment(sketch, "E2209", {"start": v(-3.7, 5) * mm, "end": v(-3.7, 3.7) * mm});
            skLineSegment(sketch, "E2210", {"start": v(-21.5, -15) * mm, "end": v(-20.5, -15) * mm});
            skLineSegment(sketch, "E2211", {"start": v(-20.5, -15) * mm, "end": v(-20.5, -16) * mm});
            skLineSegment(sketch, "E2212", {"start": v(-20.5, -16) * mm, "end": v(-21.5, -16) * mm});
            skLineSegment(sketch, "E2213", {"start": v(-21.5, -16) * mm, "end": v(-21.5, -15) * mm});
            skLineSegment(sketch, "E2214", {"start": v(-21.5, -16.5) * mm, "end": v(-20.5, -16.5) * mm});
            skLineSegment(sketch, "E2215", {"start": v(-20.5, -16.5) * mm, "end": v(-20.5, -17.5) * mm});
            skLineSegment(sketch, "E2216", {"start": v(-20.5, -17.5) * mm, "end": v(-21.5, -17.5) * mm});
            skLineSegment(sketch, "E2217", {"start": v(-21.5, -17.5) * mm, "end": v(-21.5, -16.5) * mm});
            skLineSegment(sketch, "E2218", {"start": v(-20.3, -16.05) * mm, "end": v(-20.3, -14.75) * mm});
            skLineSegment(sketch, "E2219", {"start": v(-20.3, -14.75) * mm, "end": v(-21.7, -14.75) * mm});
            skLineSegment(sketch, "E2220", {"start": v(-21.7, -14.75) * mm, "end": v(-21.7, -16.05) * mm});
            skArc(sketch, "E2221", {"start": v(-21.7, -16.05) * mm, "mid": v(-21.5, -16.25) * mm, "end": v(-21.7, -16.45) * mm});
            skArc(sketch, "E2222", {"start": v(-20.9, -16.25) * mm, "mid": v(-21, -16.15) * mm, "end": v(-21.1, -16.25) * mm});
            skArc(sketch, "E2223", {"start": v(-21.1, -16.25) * mm, "mid": v(-21, -16.35) * mm, "end": v(-20.9, -16.25) * mm});
            skArc(sketch, "E2224", {"start": v(-20.3, -16.05) * mm, "mid": v(-20.5, -16.25) * mm, "end": v(-20.3, -16.45) * mm});
            skLineSegment(sketch, "E2225", {"start": v(-21.7, -16.45) * mm, "end": v(-21.7, -17.75) * mm});
            skLineSegment(sketch, "E2226", {"start": v(-21.7, -17.75) * mm, "end": v(-20.3, -17.75) * mm});
            skLineSegment(sketch, "E2227", {"start": v(-20.3, -17.75) * mm, "end": v(-20.3, -16.45) * mm});
            skLineSegment(sketch, "E2228", {"start": v(-24.25, -14.75) * mm, "end": v(-24.25, -15.75) * mm});
            skLineSegment(sketch, "E2229", {"start": v(-24.25, -15.75) * mm, "end": v(-25.25, -15.75) * mm});
            skLineSegment(sketch, "E2230", {"start": v(-25.25, -15.75) * mm, "end": v(-25.25, -14.75) * mm});
            skLineSegment(sketch, "E2231", {"start": v(-25.25, -14.75) * mm, "end": v(-24.25, -14.75) * mm});
            skLineSegment(sketch, "E2232", {"start": v(-25.75, -14.75) * mm, "end": v(-25.75, -15.75) * mm});
            skLineSegment(sketch, "E2233", {"start": v(-25.75, -15.75) * mm, "end": v(-26.75, -15.75) * mm});
            skLineSegment(sketch, "E2234", {"start": v(-26.75, -15.75) * mm, "end": v(-26.75, -14.75) * mm});
            skLineSegment(sketch, "E2235", {"start": v(-26.75, -14.75) * mm, "end": v(-25.75, -14.75) * mm});
            skLineSegment(sketch, "E2236", {"start": v(-25.3, -15.95) * mm, "end": v(-24, -15.95) * mm});
            skLineSegment(sketch, "E2237", {"start": v(-24, -15.95) * mm, "end": v(-24, -14.55) * mm});
            skLineSegment(sketch, "E2238", {"start": v(-24, -14.55) * mm, "end": v(-25.3, -14.55) * mm});
            skArc(sketch, "E2239", {"start": v(-25.3, -14.55) * mm, "mid": v(-25.5, -14.75) * mm, "end": v(-25.7, -14.55) * mm});
            skArc(sketch, "E2240", {"start": v(-25.4, -15.25) * mm, "mid": v(-25.5, -15.15) * mm, "end": v(-25.6, -15.25) * mm});
            skArc(sketch, "E2241", {"start": v(-25.6, -15.25) * mm, "mid": v(-25.5, -15.35) * mm, "end": v(-25.4, -15.25) * mm});
            skArc(sketch, "E2242", {"start": v(-25.3, -15.95) * mm, "mid": v(-25.5, -15.75) * mm, "end": v(-25.7, -15.95) * mm});
            skLineSegment(sketch, "E2243", {"start": v(-25.7, -14.55) * mm, "end": v(-27, -14.55) * mm});
            skLineSegment(sketch, "E2244", {"start": v(-27, -14.55) * mm, "end": v(-27, -15.95) * mm});
            skLineSegment(sketch, "E2245", {"start": v(-27, -15.95) * mm, "end": v(-25.7, -15.95) * mm});
            skLineSegment(sketch, "E2246", {"start": v(8.5, -7.3) * mm, "end": v(9.5, -7.3) * mm});
            skLineSegment(sketch, "E2247", {"start": v(9.5, -7.3) * mm, "end": v(9.5, -8.18) * mm});
            skLineSegment(sketch, "E2248", {"start": v(9.5, -8.18) * mm, "end": v(8.5, -8.18) * mm});
            skLineSegment(sketch, "E2249", {"start": v(8.5, -8.18) * mm, "end": v(8.5, -7.3) * mm});
            skLineSegment(sketch, "E2250", {"start": v(8.5, -8.82) * mm, "end": v(9.5, -8.82) * mm});
            skLineSegment(sketch, "E2251", {"start": v(9.5, -8.82) * mm, "end": v(9.5, -9.7) * mm});
            skLineSegment(sketch, "E2252", {"start": v(9.5, -9.7) * mm, "end": v(8.5, -9.7) * mm});
            skLineSegment(sketch, "E2253", {"start": v(8.5, -9.7) * mm, "end": v(8.5, -8.82) * mm});
            skArc(sketch, "E2254", {"start": v(9.13, -8.5) * mm, "mid": v(9, -8.37) * mm, "end": v(8.87, -8.5) * mm});
            skArc(sketch, "E2255", {"start": v(8.87, -8.5) * mm, "mid": v(9, -8.63) * mm, "end": v(9.13, -8.5) * mm});
            skLineSegment(sketch, "E2256", {"start": v(9.7, -6.8) * mm, "end": v(9.7, -9.9) * mm});
            skLineSegment(sketch, "E2257", {"start": v(9.7, -9.9) * mm, "end": v(8.3, -9.9) * mm});
            skLineSegment(sketch, "E2258", {"start": v(8.3, -9.9) * mm, "end": v(8.3, -6.8) * mm});
            skLineSegment(sketch, "E2259", {"start": v(8.3, -6.8) * mm, "end": v(9.7, -6.8) * mm});
            skLineSegment(sketch, "E2260", {"start": v(9.7, -6.8) * mm, "end": v(9.7, -6.95) * mm});
            skLineSegment(sketch, "E2261", {"start": v(9.7, -6.95) * mm, "end": v(8.3, -6.95) * mm});
            skLineSegment(sketch, "E2262", {"start": v(9.7, -7.1) * mm, "end": v(8.3, -7.1) * mm});
            skLineSegment(sketch, "E2263", {"start": v(6.74, -7.3) * mm, "end": v(7.76, -7.3) * mm});
            skLineSegment(sketch, "E2264", {"start": v(7.76, -7.3) * mm, "end": v(7.76, -8.18) * mm});
            skLineSegment(sketch, "E2265", {"start": v(7.76, -8.18) * mm, "end": v(6.74, -8.18) * mm});
            skLineSegment(sketch, "E2266", {"start": v(6.74, -8.18) * mm, "end": v(6.74, -7.3) * mm});
            skLineSegment(sketch, "E2267", {"start": v(6.74, -8.82) * mm, "end": v(7.76, -8.82) * mm});
            skLineSegment(sketch, "E2268", {"start": v(7.76, -8.82) * mm, "end": v(7.76, -9.7) * mm});
            skLineSegment(sketch, "E2269", {"start": v(7.76, -9.7) * mm, "end": v(6.74, -9.7) * mm});
            skLineSegment(sketch, "E2270", {"start": v(6.74, -9.7) * mm, "end": v(6.74, -8.82) * mm});
            skArc(sketch, "E2271", {"start": v(7.38, -8.5) * mm, "mid": v(7.25, -8.37) * mm, "end": v(7.12, -8.5) * mm});
            skArc(sketch, "E2272", {"start": v(7.12, -8.5) * mm, "mid": v(7.25, -8.63) * mm, "end": v(7.38, -8.5) * mm});
            skLineSegment(sketch, "E2273", {"start": v(7.95, -6.8) * mm, "end": v(7.95, -9.9) * mm});
            skLineSegment(sketch, "E2274", {"start": v(7.95, -9.9) * mm, "end": v(6.55, -9.9) * mm});
            skLineSegment(sketch, "E2275", {"start": v(6.55, -9.9) * mm, "end": v(6.55, -6.8) * mm});
            skLineSegment(sketch, "E2276", {"start": v(6.55, -6.8) * mm, "end": v(7.95, -6.8) * mm});
            skLineSegment(sketch, "E2277", {"start": v(7.95, -6.8) * mm, "end": v(7.95, -6.95) * mm});
            skLineSegment(sketch, "E2278", {"start": v(7.95, -6.95) * mm, "end": v(6.55, -6.95) * mm});
            skLineSegment(sketch, "E2279", {"start": v(7.95, -7.1) * mm, "end": v(6.55, -7.1) * mm});
            skLineSegment(sketch, "E2280", {"start": v(4, -34.04) * mm, "end": v(5, -34.04) * mm});
            skLineSegment(sketch, "E2281", {"start": v(5, -34.04) * mm, "end": v(5, -34.93) * mm});
            skLineSegment(sketch, "E2282", {"start": v(5, -34.93) * mm, "end": v(4, -34.93) * mm});
            skLineSegment(sketch, "E2283", {"start": v(4, -34.93) * mm, "end": v(4, -34.04) * mm});
            skLineSegment(sketch, "E2284", {"start": v(4, -35.57) * mm, "end": v(5, -35.57) * mm});
            skLineSegment(sketch, "E2285", {"start": v(5, -35.57) * mm, "end": v(5, -36.46) * mm});
            skLineSegment(sketch, "E2286", {"start": v(5, -36.46) * mm, "end": v(4, -36.46) * mm});
            skLineSegment(sketch, "E2287", {"start": v(4, -36.46) * mm, "end": v(4, -35.57) * mm});
            skArc(sketch, "E2288", {"start": v(4.63, -35.25) * mm, "mid": v(4.5, -35.12) * mm, "end": v(4.37, -35.25) * mm});
            skArc(sketch, "E2289", {"start": v(4.37, -35.25) * mm, "mid": v(4.5, -35.38) * mm, "end": v(4.63, -35.25) * mm});
            skLineSegment(sketch, "E2290", {"start": v(5.2, -33.55) * mm, "end": v(5.2, -36.65) * mm});
            skLineSegment(sketch, "E2291", {"start": v(5.2, -36.65) * mm, "end": v(3.8, -36.65) * mm});
            skLineSegment(sketch, "E2292", {"start": v(3.8, -36.65) * mm, "end": v(3.8, -33.55) * mm});
            skLineSegment(sketch, "E2293", {"start": v(3.8, -33.55) * mm, "end": v(5.2, -33.55) * mm});
            skLineSegment(sketch, "E2294", {"start": v(5.2, -33.55) * mm, "end": v(5.2, -33.7) * mm});
            skLineSegment(sketch, "E2295", {"start": v(5.2, -33.7) * mm, "end": v(3.8, -33.7) * mm});
            skLineSegment(sketch, "E2296", {"start": v(5.2, -33.85) * mm, "end": v(3.8, -33.85) * mm});
            skLineSegment(sketch, "E2297", {"start": v(5, -7.3) * mm, "end": v(6, -7.3) * mm});
            skLineSegment(sketch, "E2298", {"start": v(6, -7.3) * mm, "end": v(6, -8.18) * mm});
            skLineSegment(sketch, "E2299", {"start": v(6, -8.18) * mm, "end": v(5, -8.18) * mm});
            skLineSegment(sketch, "E2300", {"start": v(5, -8.18) * mm, "end": v(5, -7.3) * mm});
            skLineSegment(sketch, "E2301", {"start": v(5, -8.82) * mm, "end": v(6, -8.82) * mm});
            skLineSegment(sketch, "E2302", {"start": v(6, -8.82) * mm, "end": v(6, -9.7) * mm});
            skLineSegment(sketch, "E2303", {"start": v(6, -9.7) * mm, "end": v(5, -9.7) * mm});
            skLineSegment(sketch, "E2304", {"start": v(5, -9.7) * mm, "end": v(5, -8.82) * mm});
            skArc(sketch, "E2305", {"start": v(5.63, -8.5) * mm, "mid": v(5.5, -8.37) * mm, "end": v(5.37, -8.5) * mm});
            skArc(sketch, "E2306", {"start": v(5.37, -8.5) * mm, "mid": v(5.5, -8.63) * mm, "end": v(5.63, -8.5) * mm});
            skLineSegment(sketch, "E2307", {"start": v(6.2, -6.8) * mm, "end": v(6.2, -9.9) * mm});
            skLineSegment(sketch, "E2308", {"start": v(6.2, -9.9) * mm, "end": v(4.8, -9.9) * mm});
            skLineSegment(sketch, "E2309", {"start": v(4.8, -9.9) * mm, "end": v(4.8, -6.8) * mm});
            skLineSegment(sketch, "E2310", {"start": v(4.8, -6.8) * mm, "end": v(6.2, -6.8) * mm});
            skLineSegment(sketch, "E2311", {"start": v(6.2, -6.8) * mm, "end": v(6.2, -6.95) * mm});
            skLineSegment(sketch, "E2312", {"start": v(6.2, -6.95) * mm, "end": v(4.8, -6.95) * mm});
            skLineSegment(sketch, "E2313", {"start": v(6.2, -7.1) * mm, "end": v(4.8, -7.1) * mm});
            skLineSegment(sketch, "E2314", {"start": v(22, -34) * mm, "end": v(24, -34) * mm});
            skLineSegment(sketch, "E2315", {"start": v(24, -34) * mm, "end": v(24, -36) * mm});
            skLineSegment(sketch, "E2316", {"start": v(24, -36) * mm, "end": v(22, -36) * mm});
            skLineSegment(sketch, "E2317", {"start": v(22, -36) * mm, "end": v(22, -34) * mm});
            skLineSegment(sketch, "E2318", {"start": v(22, -38) * mm, "end": v(24, -38) * mm});
            skLineSegment(sketch, "E2319", {"start": v(24, -38) * mm, "end": v(24, -40) * mm});
            skLineSegment(sketch, "E2320", {"start": v(24, -40) * mm, "end": v(22, -40) * mm});
            skLineSegment(sketch, "E2321", {"start": v(22, -40) * mm, "end": v(22, -38) * mm});
            skLineSegment(sketch, "E2322", {"start": v(23, -36.5) * mm, "end": v(23, -37.5) * mm});
            skLineSegment(sketch, "E2323", {"start": v(23.5, -37) * mm, "end": v(22.5, -37) * mm});
            skLineSegment(sketch, "E2324", {"start": v(24.75, -33.25) * mm, "end": v(24.75, -40.25) * mm});
            skLineSegment(sketch, "E2325", {"start": v(24.75, -40.25) * mm, "end": v(21.25, -40.25) * mm});
            skLineSegment(sketch, "E2326", {"start": v(21.25, -40.25) * mm, "end": v(21.25, -33.25) * mm});
            skLineSegment(sketch, "E2327", {"start": v(21.25, -33.25) * mm, "end": v(24.75, -33.25) * mm});
            skLineSegment(sketch, "E2328", {"start": v(24.75, -33.75) * mm, "end": v(24.75, -33.25) * mm});
            skLineSegment(sketch, "E2329", {"start": v(24.75, -33.25) * mm, "end": v(21.25, -33.25) * mm});
            skLineSegment(sketch, "E2330", {"start": v(21.25, -33.25) * mm, "end": v(21.25, -33.75) * mm});
            skLineSegment(sketch, "E2331", {"start": v(21.25, -33.75) * mm, "end": v(21.75, -33.75) * mm});
            skLineSegment(sketch, "E2332", {"start": v(21.75, -33.75) * mm, "end": v(24.25, -33.75) * mm});
            skLineSegment(sketch, "E2333", {"start": v(24.25, -33.75) * mm, "end": v(24.75, -33.75) * mm});
            skLineSegment(sketch, "E2334", {"start": v(0.5, -34) * mm, "end": v(2.5, -34) * mm});
            skLineSegment(sketch, "E2335", {"start": v(2.5, -34) * mm, "end": v(2.5, -36) * mm});
            skLineSegment(sketch, "E2336", {"start": v(2.5, -36) * mm, "end": v(0.5, -36) * mm});
            skLineSegment(sketch, "E2337", {"start": v(0.5, -36) * mm, "end": v(0.5, -34) * mm});
            skLineSegment(sketch, "E2338", {"start": v(0.5, -38) * mm, "end": v(2.5, -38) * mm});
            skLineSegment(sketch, "E2339", {"start": v(2.5, -38) * mm, "end": v(2.5, -40) * mm});
            skLineSegment(sketch, "E2340", {"start": v(2.5, -40) * mm, "end": v(0.5, -40) * mm});
            skLineSegment(sketch, "E2341", {"start": v(0.5, -40) * mm, "end": v(0.5, -38) * mm});
            skLineSegment(sketch, "E2342", {"start": v(1.5, -36.5) * mm, "end": v(1.5, -37.5) * mm});
            skLineSegment(sketch, "E2343", {"start": v(2, -37) * mm, "end": v(1, -37) * mm});
            skLineSegment(sketch, "E2344", {"start": v(3.25, -33.25) * mm, "end": v(3.25, -40.25) * mm});
            skLineSegment(sketch, "E2345", {"start": v(3.25, -40.25) * mm, "end": v(-0.25, -40.25) * mm});
            skLineSegment(sketch, "E2346", {"start": v(-0.25, -40.25) * mm, "end": v(-0.25, -33.25) * mm});
            skLineSegment(sketch, "E2347", {"start": v(-0.25, -33.25) * mm, "end": v(3.25, -33.25) * mm});
            skLineSegment(sketch, "E2348", {"start": v(3.25, -33.75) * mm, "end": v(3.25, -33.25) * mm});
            skLineSegment(sketch, "E2349", {"start": v(3.25, -33.25) * mm, "end": v(-0.25, -33.25) * mm});
            skLineSegment(sketch, "E2350", {"start": v(-0.25, -33.25) * mm, "end": v(-0.25, -33.75) * mm});
            skLineSegment(sketch, "E2351", {"start": v(-0.25, -33.75) * mm, "end": v(0.25, -33.75) * mm});
            skLineSegment(sketch, "E2352", {"start": v(0.25, -33.75) * mm, "end": v(2.75, -33.75) * mm});
            skLineSegment(sketch, "E2353", {"start": v(2.75, -33.75) * mm, "end": v(3.25, -33.75) * mm});
            skLineSegment(sketch, "E2354", {"start": v(-7.57, -23.72) * mm, "end": v(-7.57, -25) * mm});
            skLineSegment(sketch, "E2355", {"start": v(-7.57, -25) * mm, "end": v(-8.33, -25) * mm});
            skLineSegment(sketch, "E2356", {"start": v(-8.33, -25) * mm, "end": v(-8.33, -23.72) * mm});
            skLineSegment(sketch, "E2357", {"start": v(-8.33, -23.72) * mm, "end": v(-7.57, -23.72) * mm});
            skLineSegment(sketch, "E2358", {"start": v(-5.67, -23.72) * mm, "end": v(-5.67, -25) * mm});
            skLineSegment(sketch, "E2359", {"start": v(-5.67, -25) * mm, "end": v(-6.43, -25) * mm});
            skLineSegment(sketch, "E2360", {"start": v(-6.43, -25) * mm, "end": v(-6.43, -23.72) * mm});
            skLineSegment(sketch, "E2361", {"start": v(-6.43, -23.72) * mm, "end": v(-5.67, -23.72) * mm});
            skLineSegment(sketch, "E2362", {"start": v(-6.62, -26) * mm, "end": v(-6.62, -27.28) * mm});
            skLineSegment(sketch, "E2363", {"start": v(-6.62, -27.28) * mm, "end": v(-7.38, -27.28) * mm});
            skLineSegment(sketch, "E2364", {"start": v(-7.38, -27.28) * mm, "end": v(-7.38, -26) * mm});
            skLineSegment(sketch, "E2365", {"start": v(-7.38, -26) * mm, "end": v(-6.62, -26) * mm});
            skArc(sketch, "E2366", {"start": v(-6.75, -25.5) * mm, "mid": v(-7, -25.25) * mm, "end": v(-7.25, -25.5) * mm});
            skArc(sketch, "E2367", {"start": v(-7.25, -25.5) * mm, "mid": v(-7, -25.75) * mm, "end": v(-6.75, -25.5) * mm});
            skLineSegment(sketch, "E2368", {"start": v(-5.38, -27.5) * mm, "end": v(-8.62, -27.5) * mm});
            skLineSegment(sketch, "E2369", {"start": v(-8.62, -27.5) * mm, "end": v(-8.62, -23.5) * mm});
            skLineSegment(sketch, "E2370", {"start": v(-8.62, -23.5) * mm, "end": v(-5.62, -23.5) * mm});
            skLineSegment(sketch, "E2371", {"start": v(-5.62, -23.5) * mm, "end": v(-5.38, -23.75) * mm});
            skLineSegment(sketch, "E2372", {"start": v(-5.38, -23.75) * mm, "end": v(-5.38, -27.5) * mm});
            skLineSegment(sketch, "E2373", {"start": v(-20.65, -40.03) * mm, "end": v(-20.65, -41.56) * mm});
            skArc(sketch, "E2374", {"start": v(-20.65, -41.56) * mm, "mid": v(-20.9, -41.8) * mm, "end": v(-21.16, -41.56) * mm});
            skLineSegment(sketch, "E2375", {"start": v(-21.16, -41.56) * mm, "end": v(-21.16, -40.03) * mm});
            skArc(sketch, "E2376", {"start": v(-21.16, -40.03) * mm, "mid": v(-20.9, -39.78) * mm, "end": v(-20.65, -40.03) * mm});
            skLineSegment(sketch, "E2377", {"start": v(-19.38, -40.03) * mm, "end": v(-19.38, -41.56) * mm});
            skArc(sketch, "E2378", {"start": v(-19.38, -41.56) * mm, "mid": v(-19.64, -41.8) * mm, "end": v(-19.89, -41.56) * mm});
            skLineSegment(sketch, "E2379", {"start": v(-19.89, -41.56) * mm, "end": v(-19.89, -40.03) * mm});
            skArc(sketch, "E2380", {"start": v(-19.89, -40.03) * mm, "mid": v(-19.64, -39.78) * mm, "end": v(-19.38, -40.03) * mm});
            skLineSegment(sketch, "E2381", {"start": v(-18.11, -40.03) * mm, "end": v(-18.11, -41.56) * mm});
            skArc(sketch, "E2382", {"start": v(-18.11, -41.56) * mm, "mid": v(-18.36, -41.8) * mm, "end": v(-18.62, -41.56) * mm});
            skLineSegment(sketch, "E2383", {"start": v(-18.62, -41.56) * mm, "end": v(-18.62, -40.03) * mm});
            skArc(sketch, "E2384", {"start": v(-18.62, -40.03) * mm, "mid": v(-18.36, -39.78) * mm, "end": v(-18.11, -40.03) * mm});
            skLineSegment(sketch, "E2385", {"start": v(-16.84, -40.03) * mm, "end": v(-16.84, -41.56) * mm});
            skArc(sketch, "E2386", {"start": v(-16.84, -41.56) * mm, "mid": v(-17.1, -41.8) * mm, "end": v(-17.35, -41.56) * mm});
            skLineSegment(sketch, "E2387", {"start": v(-17.35, -41.56) * mm, "end": v(-17.35, -40.03) * mm});
            skArc(sketch, "E2388", {"start": v(-17.35, -40.03) * mm, "mid": v(-17.1, -39.78) * mm, "end": v(-16.84, -40.03) * mm});
            skLineSegment(sketch, "E2389", {"start": v(-16.84, -34.44) * mm, "end": v(-16.84, -35.97) * mm});
            skArc(sketch, "E2390", {"start": v(-16.84, -35.97) * mm, "mid": v(-17.1, -36.22) * mm, "end": v(-17.35, -35.97) * mm});
            skLineSegment(sketch, "E2391", {"start": v(-17.35, -35.97) * mm, "end": v(-17.35, -34.44) * mm});
            skArc(sketch, "E2392", {"start": v(-17.35, -34.44) * mm, "mid": v(-17.1, -34.2) * mm, "end": v(-16.84, -34.44) * mm});
            skLineSegment(sketch, "E2393", {"start": v(-18.11, -34.44) * mm, "end": v(-18.11, -35.97) * mm});
            skArc(sketch, "E2394", {"start": v(-18.11, -35.97) * mm, "mid": v(-18.36, -36.22) * mm, "end": v(-18.62, -35.97) * mm});
            skLineSegment(sketch, "E2395", {"start": v(-18.62, -35.97) * mm, "end": v(-18.62, -34.44) * mm});
            skArc(sketch, "E2396", {"start": v(-18.62, -34.44) * mm, "mid": v(-18.36, -34.2) * mm, "end": v(-18.11, -34.44) * mm});
            skLineSegment(sketch, "E2397", {"start": v(-19.38, -34.44) * mm, "end": v(-19.38, -35.97) * mm});
            skArc(sketch, "E2398", {"start": v(-19.38, -35.97) * mm, "mid": v(-19.64, -36.22) * mm, "end": v(-19.89, -35.97) * mm});
            skLineSegment(sketch, "E2399", {"start": v(-19.89, -35.97) * mm, "end": v(-19.89, -34.44) * mm});
            skArc(sketch, "E2400", {"start": v(-19.89, -34.44) * mm, "mid": v(-19.64, -34.2) * mm, "end": v(-19.38, -34.44) * mm});
            skLineSegment(sketch, "E2401", {"start": v(-20.65, -34.44) * mm, "end": v(-20.65, -35.97) * mm});
            skArc(sketch, "E2402", {"start": v(-20.65, -35.97) * mm, "mid": v(-20.9, -36.22) * mm, "end": v(-21.16, -35.97) * mm});
            skLineSegment(sketch, "E2403", {"start": v(-21.16, -35.97) * mm, "end": v(-21.16, -34.44) * mm});
            skArc(sketch, "E2404", {"start": v(-21.16, -34.44) * mm, "mid": v(-20.9, -34.2) * mm, "end": v(-20.65, -34.44) * mm});
            skLineSegment(sketch, "E2405", {"start": v(-17.1, -33.55) * mm, "end": v(-17.1, -34.06) * mm});
            skLineSegment(sketch, "E2406", {"start": v(-21.54, -37.37) * mm, "end": v(-20.9, -38) * mm});
            skLineSegment(sketch, "E2407", {"start": v(-20.9, -38) * mm, "end": v(-21.54, -38.63) * mm});
            skLineSegment(sketch, "E2408", {"start": v(-19.64, -38) * mm, "end": v(-18.36, -38) * mm});
            skLineSegment(sketch, "E2409", {"start": v(-19, -37.37) * mm, "end": v(-19, -38.63) * mm});
            skArc(sketch, "E2410", {"start": v(-20.65, -42.2) * mm, "mid": v(-20.9, -41.94) * mm, "end": v(-21.16, -42.2) * mm});
            skArc(sketch, "E2411", {"start": v(-21.16, -42.2) * mm, "mid": v(-20.9, -42.45) * mm, "end": v(-20.65, -42.2) * mm});
            skLineSegment(sketch, "E2412", {"start": v(-21.54, -39.4) * mm, "end": v(-21.54, -36.6) * mm});
            skLineSegment(sketch, "E2413", {"start": v(-21.54, -36.6) * mm, "end": v(-16.46, -36.6) * mm});
            skLineSegment(sketch, "E2414", {"start": v(-16.46, -36.6) * mm, "end": v(-16.46, -39.4) * mm});
            skLineSegment(sketch, "E2415", {"start": v(-16.46, -39.4) * mm, "end": v(-21.54, -39.4) * mm});
            skLineSegment(sketch, "E2416", {"start": v(-20.65, 3.97) * mm, "end": v(-20.65, 2.44) * mm});
            skArc(sketch, "E2417", {"start": v(-20.65, 2.44) * mm, "mid": v(-20.9, 2.2) * mm, "end": v(-21.16, 2.44) * mm});
            skLineSegment(sketch, "E2418", {"start": v(-21.16, 2.44) * mm, "end": v(-21.16, 3.97) * mm});
            skArc(sketch, "E2419", {"start": v(-21.16, 3.97) * mm, "mid": v(-20.9, 4.22) * mm, "end": v(-20.65, 3.97) * mm});
            skLineSegment(sketch, "E2420", {"start": v(-19.38, 3.97) * mm, "end": v(-19.38, 2.44) * mm});
            skArc(sketch, "E2421", {"start": v(-19.38, 2.44) * mm, "mid": v(-19.64, 2.2) * mm, "end": v(-19.89, 2.44) * mm});
            skLineSegment(sketch, "E2422", {"start": v(-19.89, 2.44) * mm, "end": v(-19.89, 3.97) * mm});
            skArc(sketch, "E2423", {"start": v(-19.89, 3.97) * mm, "mid": v(-19.64, 4.22) * mm, "end": v(-19.38, 3.97) * mm});
            skLineSegment(sketch, "E2424", {"start": v(-18.11, 3.97) * mm, "end": v(-18.11, 2.44) * mm});
            skArc(sketch, "E2425", {"start": v(-18.11, 2.44) * mm, "mid": v(-18.36, 2.2) * mm, "end": v(-18.62, 2.44) * mm});
            skLineSegment(sketch, "E2426", {"start": v(-18.62, 2.44) * mm, "end": v(-18.62, 3.97) * mm});
            skArc(sketch, "E2427", {"start": v(-18.62, 3.97) * mm, "mid": v(-18.36, 4.22) * mm, "end": v(-18.11, 3.97) * mm});
            skLineSegment(sketch, "E2428", {"start": v(-16.84, 3.97) * mm, "end": v(-16.84, 2.44) * mm});
            skArc(sketch, "E2429", {"start": v(-16.84, 2.44) * mm, "mid": v(-17.1, 2.2) * mm, "end": v(-17.35, 2.44) * mm});
            skLineSegment(sketch, "E2430", {"start": v(-17.35, 2.44) * mm, "end": v(-17.35, 3.97) * mm});
            skArc(sketch, "E2431", {"start": v(-17.35, 3.97) * mm, "mid": v(-17.1, 4.22) * mm, "end": v(-16.84, 3.97) * mm});
            skLineSegment(sketch, "E2432", {"start": v(-16.84, 9.56) * mm, "end": v(-16.84, 8.03) * mm});
            skArc(sketch, "E2433", {"start": v(-16.84, 8.03) * mm, "mid": v(-17.1, 7.78) * mm, "end": v(-17.35, 8.03) * mm});
            skLineSegment(sketch, "E2434", {"start": v(-17.35, 8.03) * mm, "end": v(-17.35, 9.56) * mm});
            skArc(sketch, "E2435", {"start": v(-17.35, 9.56) * mm, "mid": v(-17.1, 9.8) * mm, "end": v(-16.84, 9.56) * mm});
            skLineSegment(sketch, "E2436", {"start": v(-18.11, 9.56) * mm, "end": v(-18.11, 8.03) * mm});
            skArc(sketch, "E2437", {"start": v(-18.11, 8.03) * mm, "mid": v(-18.36, 7.78) * mm, "end": v(-18.62, 8.03) * mm});
            skLineSegment(sketch, "E2438", {"start": v(-18.62, 8.03) * mm, "end": v(-18.62, 9.56) * mm});
            skArc(sketch, "E2439", {"start": v(-18.62, 9.56) * mm, "mid": v(-18.36, 9.8) * mm, "end": v(-18.11, 9.56) * mm});
            skLineSegment(sketch, "E2440", {"start": v(-19.38, 9.56) * mm, "end": v(-19.38, 8.03) * mm});
            skArc(sketch, "E2441", {"start": v(-19.38, 8.03) * mm, "mid": v(-19.64, 7.78) * mm, "end": v(-19.89, 8.03) * mm});
            skLineSegment(sketch, "E2442", {"start": v(-19.89, 8.03) * mm, "end": v(-19.89, 9.56) * mm});
            skArc(sketch, "E2443", {"start": v(-19.89, 9.56) * mm, "mid": v(-19.64, 9.8) * mm, "end": v(-19.38, 9.56) * mm});
            skLineSegment(sketch, "E2444", {"start": v(-20.65, 9.56) * mm, "end": v(-20.65, 8.03) * mm});
            skArc(sketch, "E2445", {"start": v(-20.65, 8.03) * mm, "mid": v(-20.9, 7.78) * mm, "end": v(-21.16, 8.03) * mm});
            skLineSegment(sketch, "E2446", {"start": v(-21.16, 8.03) * mm, "end": v(-21.16, 9.56) * mm});
            skArc(sketch, "E2447", {"start": v(-21.16, 9.56) * mm, "mid": v(-20.9, 9.8) * mm, "end": v(-20.65, 9.56) * mm});
            skLineSegment(sketch, "E2448", {"start": v(-17.1, 10.45) * mm, "end": v(-17.1, 9.94) * mm});
            skLineSegment(sketch, "E2449", {"start": v(-21.54, 6.63) * mm, "end": v(-20.9, 6) * mm});
            skLineSegment(sketch, "E2450", {"start": v(-20.9, 6) * mm, "end": v(-21.54, 5.37) * mm});
            skLineSegment(sketch, "E2451", {"start": v(-19.64, 6) * mm, "end": v(-18.36, 6) * mm});
            skLineSegment(sketch, "E2452", {"start": v(-19, 6.63) * mm, "end": v(-19, 5.37) * mm});
            skArc(sketch, "E2453", {"start": v(-20.65, 1.8) * mm, "mid": v(-20.9, 2.06) * mm, "end": v(-21.16, 1.8) * mm});
            skArc(sketch, "E2454", {"start": v(-21.16, 1.8) * mm, "mid": v(-20.9, 1.55) * mm, "end": v(-20.65, 1.8) * mm});
            skLineSegment(sketch, "E2455", {"start": v(-21.54, 4.6) * mm, "end": v(-21.54, 7.4) * mm});
            skLineSegment(sketch, "E2456", {"start": v(-21.54, 7.4) * mm, "end": v(-16.46, 7.4) * mm});
            skLineSegment(sketch, "E2457", {"start": v(-16.46, 7.4) * mm, "end": v(-16.46, 4.6) * mm});
            skLineSegment(sketch, "E2458", {"start": v(-16.46, 4.6) * mm, "end": v(-21.54, 4.6) * mm});
            skLineSegment(sketch, "E2459", {"start": v(-20.65, 19.97) * mm, "end": v(-20.65, 18.44) * mm});
            skArc(sketch, "E2460", {"start": v(-20.65, 18.44) * mm, "mid": v(-20.9, 18.2) * mm, "end": v(-21.16, 18.44) * mm});
            skLineSegment(sketch, "E2461", {"start": v(-21.16, 18.44) * mm, "end": v(-21.16, 19.97) * mm});
            skArc(sketch, "E2462", {"start": v(-21.16, 19.97) * mm, "mid": v(-20.9, 20.22) * mm, "end": v(-20.65, 19.97) * mm});
            skLineSegment(sketch, "E2463", {"start": v(-19.38, 19.97) * mm, "end": v(-19.38, 18.44) * mm});
            skArc(sketch, "E2464", {"start": v(-19.38, 18.44) * mm, "mid": v(-19.64, 18.2) * mm, "end": v(-19.89, 18.44) * mm});
            skLineSegment(sketch, "E2465", {"start": v(-19.89, 18.44) * mm, "end": v(-19.89, 19.97) * mm});
            skArc(sketch, "E2466", {"start": v(-19.89, 19.97) * mm, "mid": v(-19.64, 20.22) * mm, "end": v(-19.38, 19.97) * mm});
            skLineSegment(sketch, "E2467", {"start": v(-18.11, 19.97) * mm, "end": v(-18.11, 18.44) * mm});
            skArc(sketch, "E2468", {"start": v(-18.11, 18.44) * mm, "mid": v(-18.36, 18.2) * mm, "end": v(-18.62, 18.44) * mm});
            skLineSegment(sketch, "E2469", {"start": v(-18.62, 18.44) * mm, "end": v(-18.62, 19.97) * mm});
            skArc(sketch, "E2470", {"start": v(-18.62, 19.97) * mm, "mid": v(-18.36, 20.22) * mm, "end": v(-18.11, 19.97) * mm});
            skLineSegment(sketch, "E2471", {"start": v(-16.84, 19.97) * mm, "end": v(-16.84, 18.44) * mm});
            skArc(sketch, "E2472", {"start": v(-16.84, 18.44) * mm, "mid": v(-17.1, 18.2) * mm, "end": v(-17.35, 18.44) * mm});
            skLineSegment(sketch, "E2473", {"start": v(-17.35, 18.44) * mm, "end": v(-17.35, 19.97) * mm});
            skArc(sketch, "E2474", {"start": v(-17.35, 19.97) * mm, "mid": v(-17.1, 20.22) * mm, "end": v(-16.84, 19.97) * mm});
            skLineSegment(sketch, "E2475", {"start": v(-16.84, 25.56) * mm, "end": v(-16.84, 24.03) * mm});
            skArc(sketch, "E2476", {"start": v(-16.84, 24.03) * mm, "mid": v(-17.1, 23.78) * mm, "end": v(-17.35, 24.03) * mm});
            skLineSegment(sketch, "E2477", {"start": v(-17.35, 24.03) * mm, "end": v(-17.35, 25.56) * mm});
            skArc(sketch, "E2478", {"start": v(-17.35, 25.56) * mm, "mid": v(-17.1, 25.8) * mm, "end": v(-16.84, 25.56) * mm});
            skLineSegment(sketch, "E2479", {"start": v(-18.11, 25.56) * mm, "end": v(-18.11, 24.03) * mm});
            skArc(sketch, "E2480", {"start": v(-18.11, 24.03) * mm, "mid": v(-18.36, 23.78) * mm, "end": v(-18.62, 24.03) * mm});
            skLineSegment(sketch, "E2481", {"start": v(-18.62, 24.03) * mm, "end": v(-18.62, 25.56) * mm});
            skArc(sketch, "E2482", {"start": v(-18.62, 25.56) * mm, "mid": v(-18.36, 25.8) * mm, "end": v(-18.11, 25.56) * mm});
            skLineSegment(sketch, "E2483", {"start": v(-19.38, 25.56) * mm, "end": v(-19.38, 24.03) * mm});
            skArc(sketch, "E2484", {"start": v(-19.38, 24.03) * mm, "mid": v(-19.64, 23.78) * mm, "end": v(-19.89, 24.03) * mm});
            skLineSegment(sketch, "E2485", {"start": v(-19.89, 24.03) * mm, "end": v(-19.89, 25.56) * mm});
            skArc(sketch, "E2486", {"start": v(-19.89, 25.56) * mm, "mid": v(-19.64, 25.8) * mm, "end": v(-19.38, 25.56) * mm});
            skLineSegment(sketch, "E2487", {"start": v(-20.65, 25.56) * mm, "end": v(-20.65, 24.03) * mm});
            skArc(sketch, "E2488", {"start": v(-20.65, 24.03) * mm, "mid": v(-20.9, 23.78) * mm, "end": v(-21.16, 24.03) * mm});
            skLineSegment(sketch, "E2489", {"start": v(-21.16, 24.03) * mm, "end": v(-21.16, 25.56) * mm});
            skArc(sketch, "E2490", {"start": v(-21.16, 25.56) * mm, "mid": v(-20.9, 25.8) * mm, "end": v(-20.65, 25.56) * mm});
            skLineSegment(sketch, "E2491", {"start": v(-17.1, 26.44) * mm, "end": v(-17.1, 25.94) * mm});
            skLineSegment(sketch, "E2492", {"start": v(-21.54, 22.64) * mm, "end": v(-20.9, 22) * mm});
            skLineSegment(sketch, "E2493", {"start": v(-20.9, 22) * mm, "end": v(-21.54, 21.36) * mm});
            skLineSegment(sketch, "E2494", {"start": v(-19.64, 22) * mm, "end": v(-18.36, 22) * mm});
            skLineSegment(sketch, "E2495", {"start": v(-19, 22.64) * mm, "end": v(-19, 21.36) * mm});
            skArc(sketch, "E2496", {"start": v(-20.65, 17.8) * mm, "mid": v(-20.9, 18.06) * mm, "end": v(-21.16, 17.8) * mm});
            skArc(sketch, "E2497", {"start": v(-21.16, 17.8) * mm, "mid": v(-20.9, 17.55) * mm, "end": v(-20.65, 17.8) * mm});
            skLineSegment(sketch, "E2498", {"start": v(-21.54, 20.6) * mm, "end": v(-21.54, 23.4) * mm});
            skLineSegment(sketch, "E2499", {"start": v(-21.54, 23.4) * mm, "end": v(-16.46, 23.4) * mm});
            skLineSegment(sketch, "E2500", {"start": v(-16.46, 23.4) * mm, "end": v(-16.46, 20.6) * mm});
            skLineSegment(sketch, "E2501", {"start": v(-16.46, 20.6) * mm, "end": v(-21.54, 20.6) * mm});
            skLineSegment(sketch, "E2502", {"start": v(-20.65, 35.97) * mm, "end": v(-20.65, 34.44) * mm});
            skArc(sketch, "E2503", {"start": v(-20.65, 34.44) * mm, "mid": v(-20.9, 34.2) * mm, "end": v(-21.16, 34.44) * mm});
            skLineSegment(sketch, "E2504", {"start": v(-21.16, 34.44) * mm, "end": v(-21.16, 35.97) * mm});
            skArc(sketch, "E2505", {"start": v(-21.16, 35.97) * mm, "mid": v(-20.9, 36.22) * mm, "end": v(-20.65, 35.97) * mm});
            skLineSegment(sketch, "E2506", {"start": v(-19.38, 35.97) * mm, "end": v(-19.38, 34.44) * mm});
            skArc(sketch, "E2507", {"start": v(-19.38, 34.44) * mm, "mid": v(-19.64, 34.2) * mm, "end": v(-19.89, 34.44) * mm});
            skLineSegment(sketch, "E2508", {"start": v(-19.89, 34.44) * mm, "end": v(-19.89, 35.97) * mm});
            skArc(sketch, "E2509", {"start": v(-19.89, 35.97) * mm, "mid": v(-19.64, 36.22) * mm, "end": v(-19.38, 35.97) * mm});
            skLineSegment(sketch, "E2510", {"start": v(-18.11, 35.97) * mm, "end": v(-18.11, 34.44) * mm});
            skArc(sketch, "E2511", {"start": v(-18.11, 34.44) * mm, "mid": v(-18.36, 34.2) * mm, "end": v(-18.62, 34.44) * mm});
            skLineSegment(sketch, "E2512", {"start": v(-18.62, 34.44) * mm, "end": v(-18.62, 35.97) * mm});
            skArc(sketch, "E2513", {"start": v(-18.62, 35.97) * mm, "mid": v(-18.36, 36.22) * mm, "end": v(-18.11, 35.97) * mm});
            skLineSegment(sketch, "E2514", {"start": v(-16.84, 35.97) * mm, "end": v(-16.84, 34.44) * mm});
            skArc(sketch, "E2515", {"start": v(-16.84, 34.44) * mm, "mid": v(-17.1, 34.2) * mm, "end": v(-17.35, 34.44) * mm});
            skLineSegment(sketch, "E2516", {"start": v(-17.35, 34.44) * mm, "end": v(-17.35, 35.97) * mm});
            skArc(sketch, "E2517", {"start": v(-17.35, 35.97) * mm, "mid": v(-17.1, 36.22) * mm, "end": v(-16.84, 35.97) * mm});
            skLineSegment(sketch, "E2518", {"start": v(-16.84, 41.56) * mm, "end": v(-16.84, 40.03) * mm});
            skArc(sketch, "E2519", {"start": v(-16.84, 40.03) * mm, "mid": v(-17.1, 39.78) * mm, "end": v(-17.35, 40.03) * mm});
            skLineSegment(sketch, "E2520", {"start": v(-17.35, 40.03) * mm, "end": v(-17.35, 41.56) * mm});
            skArc(sketch, "E2521", {"start": v(-17.35, 41.56) * mm, "mid": v(-17.1, 41.8) * mm, "end": v(-16.84, 41.56) * mm});
            skLineSegment(sketch, "E2522", {"start": v(-18.11, 41.56) * mm, "end": v(-18.11, 40.03) * mm});
            skArc(sketch, "E2523", {"start": v(-18.11, 40.03) * mm, "mid": v(-18.36, 39.78) * mm, "end": v(-18.62, 40.03) * mm});
            skLineSegment(sketch, "E2524", {"start": v(-18.62, 40.03) * mm, "end": v(-18.62, 41.56) * mm});
            skArc(sketch, "E2525", {"start": v(-18.62, 41.56) * mm, "mid": v(-18.36, 41.8) * mm, "end": v(-18.11, 41.56) * mm});
            skLineSegment(sketch, "E2526", {"start": v(-19.38, 41.56) * mm, "end": v(-19.38, 40.03) * mm});
            skArc(sketch, "E2527", {"start": v(-19.38, 40.03) * mm, "mid": v(-19.64, 39.78) * mm, "end": v(-19.89, 40.03) * mm});
            skLineSegment(sketch, "E2528", {"start": v(-19.89, 40.03) * mm, "end": v(-19.89, 41.56) * mm});
            skArc(sketch, "E2529", {"start": v(-19.89, 41.56) * mm, "mid": v(-19.64, 41.8) * mm, "end": v(-19.38, 41.56) * mm});
            skLineSegment(sketch, "E2530", {"start": v(-20.65, 41.56) * mm, "end": v(-20.65, 40.03) * mm});
            skArc(sketch, "E2531", {"start": v(-20.65, 40.03) * mm, "mid": v(-20.9, 39.78) * mm, "end": v(-21.16, 40.03) * mm});
            skLineSegment(sketch, "E2532", {"start": v(-21.16, 40.03) * mm, "end": v(-21.16, 41.56) * mm});
            skArc(sketch, "E2533", {"start": v(-21.16, 41.56) * mm, "mid": v(-20.9, 41.8) * mm, "end": v(-20.65, 41.56) * mm});
            skLineSegment(sketch, "E2534", {"start": v(-17.1, 42.44) * mm, "end": v(-17.1, 41.94) * mm});
            skLineSegment(sketch, "E2535", {"start": v(-21.54, 38.64) * mm, "end": v(-20.9, 38) * mm});
            skLineSegment(sketch, "E2536", {"start": v(-20.9, 38) * mm, "end": v(-21.54, 37.36) * mm});
            skLineSegment(sketch, "E2537", {"start": v(-19.64, 38) * mm, "end": v(-18.36, 38) * mm});
            skLineSegment(sketch, "E2538", {"start": v(-19, 38.64) * mm, "end": v(-19, 37.36) * mm});
            skArc(sketch, "E2539", {"start": v(-20.65, 33.8) * mm, "mid": v(-20.9, 34.06) * mm, "end": v(-21.16, 33.8) * mm});
            skArc(sketch, "E2540", {"start": v(-21.16, 33.8) * mm, "mid": v(-20.9, 33.55) * mm, "end": v(-20.65, 33.8) * mm});
            skLineSegment(sketch, "E2541", {"start": v(-21.54, 36.6) * mm, "end": v(-21.54, 39.4) * mm});
            skLineSegment(sketch, "E2542", {"start": v(-21.54, 39.4) * mm, "end": v(-16.46, 39.4) * mm});
            skLineSegment(sketch, "E2543", {"start": v(-16.46, 39.4) * mm, "end": v(-16.46, 36.6) * mm});
            skLineSegment(sketch, "E2544", {"start": v(-16.46, 36.6) * mm, "end": v(-21.54, 36.6) * mm});
            skLineSegment(sketch, "E2545", {"start": v(-20.65, -12.03) * mm, "end": v(-20.65, -13.56) * mm});
            skArc(sketch, "E2546", {"start": v(-20.65, -13.56) * mm, "mid": v(-20.9, -13.8) * mm, "end": v(-21.16, -13.56) * mm});
            skLineSegment(sketch, "E2547", {"start": v(-21.16, -13.56) * mm, "end": v(-21.16, -12.03) * mm});
            skArc(sketch, "E2548", {"start": v(-21.16, -12.03) * mm, "mid": v(-20.9, -11.78) * mm, "end": v(-20.65, -12.03) * mm});
            skLineSegment(sketch, "E2549", {"start": v(-19.38, -12.03) * mm, "end": v(-19.38, -13.56) * mm});
            skArc(sketch, "E2550", {"start": v(-19.38, -13.56) * mm, "mid": v(-19.64, -13.8) * mm, "end": v(-19.89, -13.56) * mm});
            skLineSegment(sketch, "E2551", {"start": v(-19.89, -13.56) * mm, "end": v(-19.89, -12.03) * mm});
            skArc(sketch, "E2552", {"start": v(-19.89, -12.03) * mm, "mid": v(-19.64, -11.78) * mm, "end": v(-19.38, -12.03) * mm});
            skLineSegment(sketch, "E2553", {"start": v(-18.11, -12.03) * mm, "end": v(-18.11, -13.56) * mm});
            skArc(sketch, "E2554", {"start": v(-18.11, -13.56) * mm, "mid": v(-18.36, -13.8) * mm, "end": v(-18.62, -13.56) * mm});
            skLineSegment(sketch, "E2555", {"start": v(-18.62, -13.56) * mm, "end": v(-18.62, -12.03) * mm});
            skArc(sketch, "E2556", {"start": v(-18.62, -12.03) * mm, "mid": v(-18.36, -11.78) * mm, "end": v(-18.11, -12.03) * mm});
            skLineSegment(sketch, "E2557", {"start": v(-16.84, -12.03) * mm, "end": v(-16.84, -13.56) * mm});
            skArc(sketch, "E2558", {"start": v(-16.84, -13.56) * mm, "mid": v(-17.1, -13.8) * mm, "end": v(-17.35, -13.56) * mm});
            skLineSegment(sketch, "E2559", {"start": v(-17.35, -13.56) * mm, "end": v(-17.35, -12.03) * mm});
            skArc(sketch, "E2560", {"start": v(-17.35, -12.03) * mm, "mid": v(-17.1, -11.78) * mm, "end": v(-16.84, -12.03) * mm});
            skLineSegment(sketch, "E2561", {"start": v(-16.84, -6.44) * mm, "end": v(-16.84, -7.97) * mm});
            skArc(sketch, "E2562", {"start": v(-16.84, -7.97) * mm, "mid": v(-17.1, -8.22) * mm, "end": v(-17.35, -7.97) * mm});
            skLineSegment(sketch, "E2563", {"start": v(-17.35, -7.97) * mm, "end": v(-17.35, -6.44) * mm});
            skArc(sketch, "E2564", {"start": v(-17.35, -6.44) * mm, "mid": v(-17.1, -6.2) * mm, "end": v(-16.84, -6.44) * mm});
            skLineSegment(sketch, "E2565", {"start": v(-18.11, -6.44) * mm, "end": v(-18.11, -7.97) * mm});
            skArc(sketch, "E2566", {"start": v(-18.11, -7.97) * mm, "mid": v(-18.36, -8.22) * mm, "end": v(-18.62, -7.97) * mm});
            skLineSegment(sketch, "E2567", {"start": v(-18.62, -7.97) * mm, "end": v(-18.62, -6.44) * mm});
            skArc(sketch, "E2568", {"start": v(-18.62, -6.44) * mm, "mid": v(-18.36, -6.2) * mm, "end": v(-18.11, -6.44) * mm});
            skLineSegment(sketch, "E2569", {"start": v(-19.38, -6.44) * mm, "end": v(-19.38, -7.97) * mm});
            skArc(sketch, "E2570", {"start": v(-19.38, -7.97) * mm, "mid": v(-19.64, -8.22) * mm, "end": v(-19.89, -7.97) * mm});
            skLineSegment(sketch, "E2571", {"start": v(-19.89, -7.97) * mm, "end": v(-19.89, -6.44) * mm});
            skArc(sketch, "E2572", {"start": v(-19.89, -6.44) * mm, "mid": v(-19.64, -6.2) * mm, "end": v(-19.38, -6.44) * mm});
            skLineSegment(sketch, "E2573", {"start": v(-20.65, -6.44) * mm, "end": v(-20.65, -7.97) * mm});
            skArc(sketch, "E2574", {"start": v(-20.65, -7.97) * mm, "mid": v(-20.9, -8.22) * mm, "end": v(-21.16, -7.97) * mm});
            skLineSegment(sketch, "E2575", {"start": v(-21.16, -7.97) * mm, "end": v(-21.16, -6.44) * mm});
            skArc(sketch, "E2576", {"start": v(-21.16, -6.44) * mm, "mid": v(-20.9, -6.2) * mm, "end": v(-20.65, -6.44) * mm});
            skLineSegment(sketch, "E2577", {"start": v(-17.1, -5.55) * mm, "end": v(-17.1, -6.06) * mm});
            skLineSegment(sketch, "E2578", {"start": v(-21.54, -9.37) * mm, "end": v(-20.9, -10) * mm});
            skLineSegment(sketch, "E2579", {"start": v(-20.9, -10) * mm, "end": v(-21.54, -10.63) * mm});
            skLineSegment(sketch, "E2580", {"start": v(-19.64, -10) * mm, "end": v(-18.36, -10) * mm});
            skLineSegment(sketch, "E2581", {"start": v(-19, -9.37) * mm, "end": v(-19, -10.63) * mm});
            skArc(sketch, "E2582", {"start": v(-20.65, -14.2) * mm, "mid": v(-20.9, -13.94) * mm, "end": v(-21.16, -14.2) * mm});
            skArc(sketch, "E2583", {"start": v(-21.16, -14.2) * mm, "mid": v(-20.9, -14.45) * mm, "end": v(-20.65, -14.2) * mm});
            skLineSegment(sketch, "E2584", {"start": v(-21.54, -11.4) * mm, "end": v(-21.54, -8.6) * mm});
            skLineSegment(sketch, "E2585", {"start": v(-21.54, -8.6) * mm, "end": v(-16.46, -8.6) * mm});
            skLineSegment(sketch, "E2586", {"start": v(-16.46, -8.6) * mm, "end": v(-16.46, -11.4) * mm});
            skLineSegment(sketch, "E2587", {"start": v(-16.46, -11.4) * mm, "end": v(-21.54, -11.4) * mm});
            skLineSegment(sketch, "E2588", {"start": v(-20.65, -25.03) * mm, "end": v(-20.65, -26.56) * mm});
            skArc(sketch, "E2589", {"start": v(-20.65, -26.56) * mm, "mid": v(-20.9, -26.81) * mm, "end": v(-21.16, -26.56) * mm});
            skLineSegment(sketch, "E2590", {"start": v(-21.16, -26.56) * mm, "end": v(-21.16, -25.03) * mm});
            skArc(sketch, "E2591", {"start": v(-21.16, -25.03) * mm, "mid": v(-20.9, -24.78) * mm, "end": v(-20.65, -25.03) * mm});
            skLineSegment(sketch, "E2592", {"start": v(-19.38, -25.03) * mm, "end": v(-19.38, -26.56) * mm});
            skArc(sketch, "E2593", {"start": v(-19.38, -26.56) * mm, "mid": v(-19.64, -26.81) * mm, "end": v(-19.89, -26.56) * mm});
            skLineSegment(sketch, "E2594", {"start": v(-19.89, -26.56) * mm, "end": v(-19.89, -25.03) * mm});
            skArc(sketch, "E2595", {"start": v(-19.89, -25.03) * mm, "mid": v(-19.64, -24.78) * mm, "end": v(-19.38, -25.03) * mm});
            skLineSegment(sketch, "E2596", {"start": v(-18.11, -25.03) * mm, "end": v(-18.11, -26.56) * mm});
            skArc(sketch, "E2597", {"start": v(-18.11, -26.56) * mm, "mid": v(-18.36, -26.81) * mm, "end": v(-18.62, -26.56) * mm});
            skLineSegment(sketch, "E2598", {"start": v(-18.62, -26.56) * mm, "end": v(-18.62, -25.03) * mm});
            skArc(sketch, "E2599", {"start": v(-18.62, -25.03) * mm, "mid": v(-18.36, -24.78) * mm, "end": v(-18.11, -25.03) * mm});
            skLineSegment(sketch, "E2600", {"start": v(-16.84, -25.03) * mm, "end": v(-16.84, -26.56) * mm});
            skArc(sketch, "E2601", {"start": v(-16.84, -26.56) * mm, "mid": v(-17.1, -26.81) * mm, "end": v(-17.35, -26.56) * mm});
            skLineSegment(sketch, "E2602", {"start": v(-17.35, -26.56) * mm, "end": v(-17.35, -25.03) * mm});
            skArc(sketch, "E2603", {"start": v(-17.35, -25.03) * mm, "mid": v(-17.1, -24.78) * mm, "end": v(-16.84, -25.03) * mm});
            skLineSegment(sketch, "E2604", {"start": v(-16.84, -19.44) * mm, "end": v(-16.84, -20.97) * mm});
            skArc(sketch, "E2605", {"start": v(-16.84, -20.97) * mm, "mid": v(-17.1, -21.22) * mm, "end": v(-17.35, -20.97) * mm});
            skLineSegment(sketch, "E2606", {"start": v(-17.35, -20.97) * mm, "end": v(-17.35, -19.44) * mm});
            skArc(sketch, "E2607", {"start": v(-17.35, -19.44) * mm, "mid": v(-17.1, -19.19) * mm, "end": v(-16.84, -19.44) * mm});
            skLineSegment(sketch, "E2608", {"start": v(-18.11, -19.44) * mm, "end": v(-18.11, -20.97) * mm});
            skArc(sketch, "E2609", {"start": v(-18.11, -20.97) * mm, "mid": v(-18.36, -21.22) * mm, "end": v(-18.62, -20.97) * mm});
            skLineSegment(sketch, "E2610", {"start": v(-18.62, -20.97) * mm, "end": v(-18.62, -19.44) * mm});
            skArc(sketch, "E2611", {"start": v(-18.62, -19.44) * mm, "mid": v(-18.36, -19.19) * mm, "end": v(-18.11, -19.44) * mm});
            skLineSegment(sketch, "E2612", {"start": v(-19.38, -19.44) * mm, "end": v(-19.38, -20.97) * mm});
            skArc(sketch, "E2613", {"start": v(-19.38, -20.97) * mm, "mid": v(-19.64, -21.22) * mm, "end": v(-19.89, -20.97) * mm});
            skLineSegment(sketch, "E2614", {"start": v(-19.89, -20.97) * mm, "end": v(-19.89, -19.44) * mm});
            skArc(sketch, "E2615", {"start": v(-19.89, -19.44) * mm, "mid": v(-19.64, -19.19) * mm, "end": v(-19.38, -19.44) * mm});
            skLineSegment(sketch, "E2616", {"start": v(-20.65, -19.44) * mm, "end": v(-20.65, -20.97) * mm});
            skArc(sketch, "E2617", {"start": v(-20.65, -20.97) * mm, "mid": v(-20.9, -21.22) * mm, "end": v(-21.16, -20.97) * mm});
            skLineSegment(sketch, "E2618", {"start": v(-21.16, -20.97) * mm, "end": v(-21.16, -19.44) * mm});
            skArc(sketch, "E2619", {"start": v(-21.16, -19.44) * mm, "mid": v(-20.9, -19.19) * mm, "end": v(-20.65, -19.44) * mm});
            skLineSegment(sketch, "E2620", {"start": v(-17.1, -18.55) * mm, "end": v(-17.1, -19.06) * mm});
            skLineSegment(sketch, "E2621", {"start": v(-21.54, -22.36) * mm, "end": v(-20.9, -23) * mm});
            skLineSegment(sketch, "E2622", {"start": v(-20.9, -23) * mm, "end": v(-21.54, -23.64) * mm});
            skLineSegment(sketch, "E2623", {"start": v(-19.64, -23) * mm, "end": v(-18.36, -23) * mm});
            skLineSegment(sketch, "E2624", {"start": v(-19, -22.36) * mm, "end": v(-19, -23.64) * mm});
            skArc(sketch, "E2625", {"start": v(-20.65, -27.2) * mm, "mid": v(-20.9, -26.94) * mm, "end": v(-21.16, -27.2) * mm});
            skArc(sketch, "E2626", {"start": v(-21.16, -27.2) * mm, "mid": v(-20.9, -27.45) * mm, "end": v(-20.65, -27.2) * mm});
            skLineSegment(sketch, "E2627", {"start": v(-21.54, -24.4) * mm, "end": v(-21.54, -21.6) * mm});
            skLineSegment(sketch, "E2628", {"start": v(-21.54, -21.6) * mm, "end": v(-16.46, -21.6) * mm});
            skLineSegment(sketch, "E2629", {"start": v(-16.46, -21.6) * mm, "end": v(-16.46, -24.4) * mm});
            skLineSegment(sketch, "E2630", {"start": v(-16.46, -24.4) * mm, "end": v(-21.54, -24.4) * mm});
            skLineSegment(sketch, "E2631", {"start": v(-25.9, -21) * mm, "end": v(-24.1, -21) * mm});
            skLineSegment(sketch, "E2632", {"start": v(-24.1, -21) * mm, "end": v(-24.1, -22) * mm});
            skLineSegment(sketch, "E2633", {"start": v(-24.1, -22) * mm, "end": v(-25.9, -22) * mm});
            skLineSegment(sketch, "E2634", {"start": v(-25.9, -22) * mm, "end": v(-25.9, -21) * mm});
            skLineSegment(sketch, "E2635", {"start": v(-25.9, -24) * mm, "end": v(-24.1, -24) * mm});
            skLineSegment(sketch, "E2636", {"start": v(-24.1, -24) * mm, "end": v(-24.1, -25) * mm});
            skLineSegment(sketch, "E2637", {"start": v(-24.1, -25) * mm, "end": v(-25.9, -25) * mm});
            skLineSegment(sketch, "E2638", {"start": v(-25.9, -25) * mm, "end": v(-25.9, -24) * mm});
            skArc(sketch, "E2639", {"start": v(-24.8, -23) * mm, "mid": v(-25, -22.8) * mm, "end": v(-25.2, -23) * mm});
            skArc(sketch, "E2640", {"start": v(-25.2, -23) * mm, "mid": v(-25, -23.2) * mm, "end": v(-24.8, -23) * mm});
            skLineSegment(sketch, "E2641", {"start": v(-23.88, -21.12) * mm, "end": v(-23.88, -24.88) * mm});
            skLineSegment(sketch, "E2642", {"start": v(-24.25, -25.25) * mm, "end": v(-25.75, -25.25) * mm});
            skArc(sketch, "E2643", {"start": v(-24.25, -25.25) * mm, "mid": v(-23.99, -25.14) * mm, "end": v(-23.87, -24.88) * mm});
            skArc(sketch, "E2644", {"start": v(-25.75, -20.75) * mm, "mid": v(-26.01, -20.86) * mm, "end": v(-26.13, -21.12) * mm});
            skLineSegment(sketch, "E2645", {"start": v(-26.12, -24.88) * mm, "end": v(-26.12, -21.12) * mm});
            skLineSegment(sketch, "E2646", {"start": v(-25.75, -20.75) * mm, "end": v(-24.25, -20.75) * mm});
            skArc(sketch, "E2647", {"start": v(-24.25, -20.75) * mm, "mid": v(-23.99, -20.86) * mm, "end": v(-23.87, -21.12) * mm});
            skArc(sketch, "E2648", {"start": v(-25.75, -25.25) * mm, "mid": v(-26.01, -25.14) * mm, "end": v(-26.13, -24.88) * mm});
            skLineSegment(sketch, "E2649", {"start": v(-13.4, 24) * mm, "end": v(-11.6, 24) * mm});
            skLineSegment(sketch, "E2650", {"start": v(-11.6, 24) * mm, "end": v(-11.6, 23) * mm});
            skLineSegment(sketch, "E2651", {"start": v(-11.6, 23) * mm, "end": v(-13.4, 23) * mm});
            skLineSegment(sketch, "E2652", {"start": v(-13.4, 23) * mm, "end": v(-13.4, 24) * mm});
            skLineSegment(sketch, "E2653", {"start": v(-13.4, 21) * mm, "end": v(-11.6, 21) * mm});
            skLineSegment(sketch, "E2654", {"start": v(-11.6, 21) * mm, "end": v(-11.6, 20) * mm});
            skLineSegment(sketch, "E2655", {"start": v(-11.6, 20) * mm, "end": v(-13.4, 20) * mm});
            skLineSegment(sketch, "E2656", {"start": v(-13.4, 20) * mm, "end": v(-13.4, 21) * mm});
            skArc(sketch, "E2657", {"start": v(-12.3, 22) * mm, "mid": v(-12.5, 22.2) * mm, "end": v(-12.7, 22) * mm});
            skArc(sketch, "E2658", {"start": v(-12.7, 22) * mm, "mid": v(-12.5, 21.8) * mm, "end": v(-12.3, 22) * mm});
            skLineSegment(sketch, "E2659", {"start": v(-11.38, 23.88) * mm, "end": v(-11.38, 20.12) * mm});
            skLineSegment(sketch, "E2660", {"start": v(-11.75, 19.75) * mm, "end": v(-13.25, 19.75) * mm});
            skArc(sketch, "E2661", {"start": v(-11.75, 19.75) * mm, "mid": v(-11.49, 19.86) * mm, "end": v(-11.37, 20.12) * mm});
            skArc(sketch, "E2662", {"start": v(-13.25, 24.25) * mm, "mid": v(-13.51, 24.14) * mm, "end": v(-13.63, 23.88) * mm});
            skLineSegment(sketch, "E2663", {"start": v(-13.62, 20.12) * mm, "end": v(-13.62, 23.88) * mm});
            skLineSegment(sketch, "E2664", {"start": v(-13.25, 24.25) * mm, "end": v(-11.75, 24.25) * mm});
            skArc(sketch, "E2665", {"start": v(-11.75, 24.25) * mm, "mid": v(-11.49, 24.14) * mm, "end": v(-11.37, 23.88) * mm});
            skArc(sketch, "E2666", {"start": v(-13.25, 19.75) * mm, "mid": v(-13.51, 19.86) * mm, "end": v(-13.63, 20.12) * mm});
            skLineSegment(sketch, "E2667", {"start": v(3.9, -21) * mm, "end": v(2.1, -21) * mm});
            skLineSegment(sketch, "E2668", {"start": v(2.1, -21) * mm, "end": v(2.1, -20) * mm});
            skLineSegment(sketch, "E2669", {"start": v(2.1, -20) * mm, "end": v(3.9, -20) * mm});
            skLineSegment(sketch, "E2670", {"start": v(3.9, -20) * mm, "end": v(3.9, -21) * mm});
            skLineSegment(sketch, "E2671", {"start": v(3.9, -18) * mm, "end": v(2.1, -18) * mm});
            skLineSegment(sketch, "E2672", {"start": v(2.1, -18) * mm, "end": v(2.1, -17) * mm});
            skLineSegment(sketch, "E2673", {"start": v(2.1, -17) * mm, "end": v(3.9, -17) * mm});
            skLineSegment(sketch, "E2674", {"start": v(3.9, -17) * mm, "end": v(3.9, -18) * mm});
            skArc(sketch, "E2675", {"start": v(3.2, -19) * mm, "mid": v(3, -18.8) * mm, "end": v(2.8, -19) * mm});
            skArc(sketch, "E2676", {"start": v(2.8, -19) * mm, "mid": v(3, -19.2) * mm, "end": v(3.2, -19) * mm});
            skLineSegment(sketch, "E2677", {"start": v(1.88, -20.88) * mm, "end": v(1.88, -17.12) * mm});
            skLineSegment(sketch, "E2678", {"start": v(2.25, -16.75) * mm, "end": v(3.75, -16.75) * mm});
            skArc(sketch, "E2679", {"start": v(2.25, -16.75) * mm, "mid": v(1.99, -16.86) * mm, "end": v(1.87, -17.12) * mm});
            skArc(sketch, "E2680", {"start": v(3.75, -21.25) * mm, "mid": v(4.01, -21.14) * mm, "end": v(4.13, -20.88) * mm});
            skLineSegment(sketch, "E2681", {"start": v(4.12, -17.12) * mm, "end": v(4.12, -20.88) * mm});
            skLineSegment(sketch, "E2682", {"start": v(3.75, -21.25) * mm, "end": v(2.25, -21.25) * mm});
            skArc(sketch, "E2683", {"start": v(2.25, -21.25) * mm, "mid": v(1.99, -21.14) * mm, "end": v(1.87, -20.88) * mm});
            skArc(sketch, "E2684", {"start": v(3.75, -16.75) * mm, "mid": v(4.01, -16.86) * mm, "end": v(4.13, -17.12) * mm});
            skLineSegment(sketch, "E2685", {"start": v(0.4, -21) * mm, "end": v(-1.4, -21) * mm});
            skLineSegment(sketch, "E2686", {"start": v(-1.4, -21) * mm, "end": v(-1.4, -20) * mm});
            skLineSegment(sketch, "E2687", {"start": v(-1.4, -20) * mm, "end": v(0.4, -20) * mm});
            skLineSegment(sketch, "E2688", {"start": v(0.4, -20) * mm, "end": v(0.4, -21) * mm});
            skLineSegment(sketch, "E2689", {"start": v(0.4, -18) * mm, "end": v(-1.4, -18) * mm});
            skLineSegment(sketch, "E2690", {"start": v(-1.4, -18) * mm, "end": v(-1.4, -17) * mm});
            skLineSegment(sketch, "E2691", {"start": v(-1.4, -17) * mm, "end": v(0.4, -17) * mm});
            skLineSegment(sketch, "E2692", {"start": v(0.4, -17) * mm, "end": v(0.4, -18) * mm});
            skArc(sketch, "E2693", {"start": v(-0.3, -19) * mm, "mid": v(-0.5, -18.8) * mm, "end": v(-0.7, -19) * mm});
            skArc(sketch, "E2694", {"start": v(-0.7, -19) * mm, "mid": v(-0.5, -19.2) * mm, "end": v(-0.3, -19) * mm});
            skLineSegment(sketch, "E2695", {"start": v(-1.63, -20.88) * mm, "end": v(-1.63, -17.12) * mm});
            skLineSegment(sketch, "E2696", {"start": v(-1.25, -16.75) * mm, "end": v(0.25, -16.75) * mm});
            skArc(sketch, "E2697", {"start": v(-1.25, -16.75) * mm, "mid": v(-1.51, -16.86) * mm, "end": v(-1.63, -17.12) * mm});
            skArc(sketch, "E2698", {"start": v(0.25, -21.25) * mm, "mid": v(0.51, -21.14) * mm, "end": v(0.63, -20.88) * mm});
            skLineSegment(sketch, "E2699", {"start": v(0.62, -17.12) * mm, "end": v(0.62, -20.88) * mm});
            skLineSegment(sketch, "E2700", {"start": v(0.25, -21.25) * mm, "end": v(-1.25, -21.25) * mm});
            skArc(sketch, "E2701", {"start": v(-1.25, -21.25) * mm, "mid": v(-1.51, -21.14) * mm, "end": v(-1.63, -20.88) * mm});
            skArc(sketch, "E2702", {"start": v(0.25, -16.75) * mm, "mid": v(0.51, -16.86) * mm, "end": v(0.63, -17.12) * mm});
            skLineSegment(sketch, "E2703", {"start": v(-11.5, -25.6) * mm, "end": v(-11.5, -27.4) * mm});
            skLineSegment(sketch, "E2704", {"start": v(-11.5, -27.4) * mm, "end": v(-12.5, -27.4) * mm});
            skLineSegment(sketch, "E2705", {"start": v(-12.5, -27.4) * mm, "end": v(-12.5, -25.6) * mm});
            skLineSegment(sketch, "E2706", {"start": v(-12.5, -25.6) * mm, "end": v(-11.5, -25.6) * mm});
            skLineSegment(sketch, "E2707", {"start": v(-14.5, -25.6) * mm, "end": v(-14.5, -27.4) * mm});
            skLineSegment(sketch, "E2708", {"start": v(-14.5, -27.4) * mm, "end": v(-15.5, -27.4) * mm});
            skLineSegment(sketch, "E2709", {"start": v(-15.5, -27.4) * mm, "end": v(-15.5, -25.6) * mm});
            skLineSegment(sketch, "E2710", {"start": v(-15.5, -25.6) * mm, "end": v(-14.5, -25.6) * mm});
            skArc(sketch, "E2711", {"start": v(-13.3, -26.5) * mm, "mid": v(-13.5, -26.3) * mm, "end": v(-13.7, -26.5) * mm});
            skArc(sketch, "E2712", {"start": v(-13.7, -26.5) * mm, "mid": v(-13.5, -26.7) * mm, "end": v(-13.3, -26.5) * mm});
            skLineSegment(sketch, "E2713", {"start": v(-11.62, -27.62) * mm, "end": v(-15.38, -27.62) * mm});
            skLineSegment(sketch, "E2714", {"start": v(-15.75, -27.25) * mm, "end": v(-15.75, -25.75) * mm});
            skArc(sketch, "E2715", {"start": v(-15.75, -27.25) * mm, "mid": v(-15.64, -27.51) * mm, "end": v(-15.38, -27.63) * mm});
            skArc(sketch, "E2716", {"start": v(-11.25, -25.75) * mm, "mid": v(-11.36, -25.49) * mm, "end": v(-11.62, -25.37) * mm});
            skLineSegment(sketch, "E2717", {"start": v(-15.38, -25.38) * mm, "end": v(-11.62, -25.38) * mm});
            skLineSegment(sketch, "E2718", {"start": v(-11.25, -25.75) * mm, "end": v(-11.25, -27.25) * mm});
            skArc(sketch, "E2719", {"start": v(-11.25, -27.25) * mm, "mid": v(-11.36, -27.51) * mm, "end": v(-11.62, -27.63) * mm});
            skArc(sketch, "E2720", {"start": v(-15.75, -25.75) * mm, "mid": v(-15.64, -25.49) * mm, "end": v(-15.38, -25.37) * mm});
            skLineSegment(sketch, "E2721", {"start": v(-2.6, -27.5) * mm, "end": v(-4.4, -27.5) * mm});
            skLineSegment(sketch, "E2722", {"start": v(-4.4, -27.5) * mm, "end": v(-4.4, -26.5) * mm});
            skLineSegment(sketch, "E2723", {"start": v(-4.4, -26.5) * mm, "end": v(-2.6, -26.5) * mm});
            skLineSegment(sketch, "E2724", {"start": v(-2.6, -26.5) * mm, "end": v(-2.6, -27.5) * mm});
            skLineSegment(sketch, "E2725", {"start": v(-2.6, -24.5) * mm, "end": v(-4.4, -24.5) * mm});
            skLineSegment(sketch, "E2726", {"start": v(-4.4, -24.5) * mm, "end": v(-4.4, -23.5) * mm});
            skLineSegment(sketch, "E2727", {"start": v(-4.4, -23.5) * mm, "end": v(-2.6, -23.5) * mm});
            skLineSegment(sketch, "E2728", {"start": v(-2.6, -23.5) * mm, "end": v(-2.6, -24.5) * mm});
            skArc(sketch, "E2729", {"start": v(-3.3, -25.5) * mm, "mid": v(-3.5, -25.3) * mm, "end": v(-3.7, -25.5) * mm});
            skArc(sketch, "E2730", {"start": v(-3.7, -25.5) * mm, "mid": v(-3.5, -25.7) * mm, "end": v(-3.3, -25.5) * mm});
            skLineSegment(sketch, "E2731", {"start": v(-4.62, -27.38) * mm, "end": v(-4.62, -23.62) * mm});
            skLineSegment(sketch, "E2732", {"start": v(-4.25, -23.25) * mm, "end": v(-2.75, -23.25) * mm});
            skArc(sketch, "E2733", {"start": v(-4.25, -23.25) * mm, "mid": v(-4.51, -23.36) * mm, "end": v(-4.63, -23.62) * mm});
            skArc(sketch, "E2734", {"start": v(-2.75, -27.75) * mm, "mid": v(-2.49, -27.64) * mm, "end": v(-2.37, -27.38) * mm});
            skLineSegment(sketch, "E2735", {"start": v(-2.38, -23.62) * mm, "end": v(-2.38, -27.38) * mm});
            skLineSegment(sketch, "E2736", {"start": v(-2.75, -27.75) * mm, "end": v(-4.25, -27.75) * mm});
            skArc(sketch, "E2737", {"start": v(-4.25, -27.75) * mm, "mid": v(-4.51, -27.64) * mm, "end": v(-4.63, -27.38) * mm});
            skArc(sketch, "E2738", {"start": v(-2.75, -23.25) * mm, "mid": v(-2.49, -23.36) * mm, "end": v(-2.37, -23.62) * mm});
            skLineSegment(sketch, "E2739", {"start": v(-4, -10.9) * mm, "end": v(-4, -9.1) * mm});
            skLineSegment(sketch, "E2740", {"start": v(-4, -9.1) * mm, "end": v(-3, -9.1) * mm});
            skLineSegment(sketch, "E2741", {"start": v(-3, -9.1) * mm, "end": v(-3, -10.9) * mm});
            skLineSegment(sketch, "E2742", {"start": v(-3, -10.9) * mm, "end": v(-4, -10.9) * mm});
            skLineSegment(sketch, "E2743", {"start": v(-1, -10.9) * mm, "end": v(-1, -9.1) * mm});
            skLineSegment(sketch, "E2744", {"start": v(-1, -9.1) * mm, "end": v(0, -9.1) * mm});
            skLineSegment(sketch, "E2745", {"start": v(0, -9.1) * mm, "end": v(0, -10.9) * mm});
            skLineSegment(sketch, "E2746", {"start": v(0, -10.9) * mm, "end": v(-1, -10.9) * mm});
            skArc(sketch, "E2747", {"start": v(-1.8, -10) * mm, "mid": v(-2, -9.8) * mm, "end": v(-2.2, -10) * mm});
            skArc(sketch, "E2748", {"start": v(-2.2, -10) * mm, "mid": v(-2, -10.2) * mm, "end": v(-1.8, -10) * mm});
            skLineSegment(sketch, "E2749", {"start": v(-3.88, -8.88) * mm, "end": v(-0.13, -8.88) * mm});
            skLineSegment(sketch, "E2750", {"start": v(0.25, -9.25) * mm, "end": v(0.25, -10.75) * mm});
            skArc(sketch, "E2751", {"start": v(0.25, -9.25) * mm, "mid": v(0.14, -8.99) * mm, "end": v(-0.12, -8.87) * mm});
            skArc(sketch, "E2752", {"start": v(-4.25, -10.75) * mm, "mid": v(-4.14, -11.01) * mm, "end": v(-3.88, -11.13) * mm});
            skLineSegment(sketch, "E2753", {"start": v(-0.12, -11.12) * mm, "end": v(-3.88, -11.12) * mm});
            skLineSegment(sketch, "E2754", {"start": v(-4.25, -10.75) * mm, "end": v(-4.25, -9.25) * mm});
            skArc(sketch, "E2755", {"start": v(-4.25, -9.25) * mm, "mid": v(-4.14, -8.99) * mm, "end": v(-3.88, -8.87) * mm});
            skArc(sketch, "E2756", {"start": v(0.25, -10.75) * mm, "mid": v(0.14, -11.01) * mm, "end": v(-0.12, -11.13) * mm});
            skLineSegment(sketch, "E2757", {"start": v(-15.9, -9.5) * mm, "end": v(-14.1, -9.5) * mm});
            skLineSegment(sketch, "E2758", {"start": v(-14.1, -9.5) * mm, "end": v(-14.1, -10.5) * mm});
            skLineSegment(sketch, "E2759", {"start": v(-14.1, -10.5) * mm, "end": v(-15.9, -10.5) * mm});
            skLineSegment(sketch, "E2760", {"start": v(-15.9, -10.5) * mm, "end": v(-15.9, -9.5) * mm});
            skLineSegment(sketch, "E2761", {"start": v(-15.9, -12.5) * mm, "end": v(-14.1, -12.5) * mm});
            skLineSegment(sketch, "E2762", {"start": v(-14.1, -12.5) * mm, "end": v(-14.1, -13.5) * mm});
            skLineSegment(sketch, "E2763", {"start": v(-14.1, -13.5) * mm, "end": v(-15.9, -13.5) * mm});
            skLineSegment(sketch, "E2764", {"start": v(-15.9, -13.5) * mm, "end": v(-15.9, -12.5) * mm});
            skArc(sketch, "E2765", {"start": v(-14.8, -11.5) * mm, "mid": v(-15, -11.3) * mm, "end": v(-15.2, -11.5) * mm});
            skArc(sketch, "E2766", {"start": v(-15.2, -11.5) * mm, "mid": v(-15, -11.7) * mm, "end": v(-14.8, -11.5) * mm});
            skLineSegment(sketch, "E2767", {"start": v(-13.88, -9.62) * mm, "end": v(-13.88, -13.38) * mm});
            skLineSegment(sketch, "E2768", {"start": v(-14.25, -13.75) * mm, "end": v(-15.75, -13.75) * mm});
            skArc(sketch, "E2769", {"start": v(-14.25, -13.75) * mm, "mid": v(-13.99, -13.64) * mm, "end": v(-13.87, -13.38) * mm});
            skArc(sketch, "E2770", {"start": v(-15.75, -9.25) * mm, "mid": v(-16.01, -9.36) * mm, "end": v(-16.13, -9.62) * mm});
            skLineSegment(sketch, "E2771", {"start": v(-16.12, -13.38) * mm, "end": v(-16.12, -9.62) * mm});
            skLineSegment(sketch, "E2772", {"start": v(-15.75, -9.25) * mm, "end": v(-14.25, -9.25) * mm});
            skArc(sketch, "E2773", {"start": v(-14.25, -9.25) * mm, "mid": v(-13.99, -9.36) * mm, "end": v(-13.87, -9.62) * mm});
            skArc(sketch, "E2774", {"start": v(-15.75, -13.75) * mm, "mid": v(-16.01, -13.64) * mm, "end": v(-16.13, -13.38) * mm});
            skLineSegment(sketch, "E2775", {"start": v(-27.6, 6) * mm, "end": v(-29.4, 6) * mm});
            skLineSegment(sketch, "E2776", {"start": v(-29.4, 6) * mm, "end": v(-29.4, 7) * mm});
            skLineSegment(sketch, "E2777", {"start": v(-29.4, 7) * mm, "end": v(-27.6, 7) * mm});
            skLineSegment(sketch, "E2778", {"start": v(-27.6, 7) * mm, "end": v(-27.6, 6) * mm});
            skLineSegment(sketch, "E2779", {"start": v(-27.6, 9) * mm, "end": v(-29.4, 9) * mm});
            skLineSegment(sketch, "E2780", {"start": v(-29.4, 9) * mm, "end": v(-29.4, 10) * mm});
            skLineSegment(sketch, "E2781", {"start": v(-29.4, 10) * mm, "end": v(-27.6, 10) * mm});
            skLineSegment(sketch, "E2782", {"start": v(-27.6, 10) * mm, "end": v(-27.6, 9) * mm});
            skLineSegment(sketch, "E2783", {"start": v(-29.63, 7.62) * mm, "end": v(-29.63, 5.75) * mm});
            skLineSegment(sketch, "E2784", {"start": v(-29.63, 5.75) * mm, "end": v(-27.38, 5.75) * mm});
            skLineSegment(sketch, "E2785", {"start": v(-27.38, 5.75) * mm, "end": v(-27.38, 7.62) * mm});
            skArc(sketch, "E2786", {"start": v(-28.3, 8) * mm, "mid": v(-28.5, 8.2) * mm, "end": v(-28.7, 8) * mm});
            skArc(sketch, "E2787", {"start": v(-28.7, 8) * mm, "mid": v(-28.5, 7.8) * mm, "end": v(-28.3, 8) * mm});
            skLineSegment(sketch, "E2788", {"start": v(-27.38, 8.38) * mm, "end": v(-27.38, 10.25) * mm});
            skLineSegment(sketch, "E2789", {"start": v(-27.38, 10.25) * mm, "end": v(-29.63, 10.25) * mm});
            skLineSegment(sketch, "E2790", {"start": v(-29.63, 10.25) * mm, "end": v(-29.63, 8.38) * mm});
            skArc(sketch, "E2791", {"start": v(-29.63, 8.38) * mm, "mid": v(-29.25, 8) * mm, "end": v(-29.63, 7.62) * mm});
            skArc(sketch, "E2792", {"start": v(-27.38, 7.62) * mm, "mid": v(-27.75, 8) * mm, "end": v(-27.38, 8.38) * mm});
            skLineSegment(sketch, "E2793", {"start": v(-27.6, 22) * mm, "end": v(-29.4, 22) * mm});
            skLineSegment(sketch, "E2794", {"start": v(-29.4, 22) * mm, "end": v(-29.4, 23) * mm});
            skLineSegment(sketch, "E2795", {"start": v(-29.4, 23) * mm, "end": v(-27.6, 23) * mm});
            skLineSegment(sketch, "E2796", {"start": v(-27.6, 23) * mm, "end": v(-27.6, 22) * mm});
            skLineSegment(sketch, "E2797", {"start": v(-27.6, 25) * mm, "end": v(-29.4, 25) * mm});
            skLineSegment(sketch, "E2798", {"start": v(-29.4, 25) * mm, "end": v(-29.4, 26) * mm});
            skLineSegment(sketch, "E2799", {"start": v(-29.4, 26) * mm, "end": v(-27.6, 26) * mm});
            skLineSegment(sketch, "E2800", {"start": v(-27.6, 26) * mm, "end": v(-27.6, 25) * mm});
            skLineSegment(sketch, "E2801", {"start": v(-29.63, 23.62) * mm, "end": v(-29.63, 21.75) * mm});
            skLineSegment(sketch, "E2802", {"start": v(-29.63, 21.75) * mm, "end": v(-27.38, 21.75) * mm});
            skLineSegment(sketch, "E2803", {"start": v(-27.38, 21.75) * mm, "end": v(-27.38, 23.62) * mm});
            skArc(sketch, "E2804", {"start": v(-28.3, 24) * mm, "mid": v(-28.5, 24.2) * mm, "end": v(-28.7, 24) * mm});
            skArc(sketch, "E2805", {"start": v(-28.7, 24) * mm, "mid": v(-28.5, 23.8) * mm, "end": v(-28.3, 24) * mm});
            skLineSegment(sketch, "E2806", {"start": v(-27.38, 24.38) * mm, "end": v(-27.38, 26.25) * mm});
            skLineSegment(sketch, "E2807", {"start": v(-27.38, 26.25) * mm, "end": v(-29.63, 26.25) * mm});
            skLineSegment(sketch, "E2808", {"start": v(-29.63, 26.25) * mm, "end": v(-29.63, 24.38) * mm});
            skArc(sketch, "E2809", {"start": v(-29.63, 24.38) * mm, "mid": v(-29.25, 24) * mm, "end": v(-29.63, 23.62) * mm});
            skArc(sketch, "E2810", {"start": v(-27.38, 23.62) * mm, "mid": v(-27.75, 24) * mm, "end": v(-27.38, 24.38) * mm});
            skLineSegment(sketch, "E2811", {"start": v(-27.6, 30) * mm, "end": v(-29.4, 30) * mm});
            skLineSegment(sketch, "E2812", {"start": v(-29.4, 30) * mm, "end": v(-29.4, 31) * mm});
            skLineSegment(sketch, "E2813", {"start": v(-29.4, 31) * mm, "end": v(-27.6, 31) * mm});
            skLineSegment(sketch, "E2814", {"start": v(-27.6, 31) * mm, "end": v(-27.6, 30) * mm});
            skLineSegment(sketch, "E2815", {"start": v(-27.6, 33) * mm, "end": v(-29.4, 33) * mm});
            skLineSegment(sketch, "E2816", {"start": v(-29.4, 33) * mm, "end": v(-29.4, 34) * mm});
            skLineSegment(sketch, "E2817", {"start": v(-29.4, 34) * mm, "end": v(-27.6, 34) * mm});
            skLineSegment(sketch, "E2818", {"start": v(-27.6, 34) * mm, "end": v(-27.6, 33) * mm});
            skLineSegment(sketch, "E2819", {"start": v(-29.63, 31.62) * mm, "end": v(-29.63, 29.75) * mm});
            skLineSegment(sketch, "E2820", {"start": v(-29.63, 29.75) * mm, "end": v(-27.38, 29.75) * mm});
            skLineSegment(sketch, "E2821", {"start": v(-27.38, 29.75) * mm, "end": v(-27.38, 31.62) * mm});
            skArc(sketch, "E2822", {"start": v(-28.3, 32) * mm, "mid": v(-28.5, 32.2) * mm, "end": v(-28.7, 32) * mm});
            skArc(sketch, "E2823", {"start": v(-28.7, 32) * mm, "mid": v(-28.5, 31.8) * mm, "end": v(-28.3, 32) * mm});
            skLineSegment(sketch, "E2824", {"start": v(-27.38, 32.38) * mm, "end": v(-27.38, 34.25) * mm});
            skLineSegment(sketch, "E2825", {"start": v(-27.38, 34.25) * mm, "end": v(-29.63, 34.25) * mm});
            skLineSegment(sketch, "E2826", {"start": v(-29.63, 34.25) * mm, "end": v(-29.63, 32.38) * mm});
            skArc(sketch, "E2827", {"start": v(-29.63, 32.38) * mm, "mid": v(-29.25, 32) * mm, "end": v(-29.63, 31.62) * mm});
            skArc(sketch, "E2828", {"start": v(-27.38, 31.62) * mm, "mid": v(-27.75, 32) * mm, "end": v(-27.38, 32.38) * mm});
            skLineSegment(sketch, "E2829", {"start": v(-27.6, 14) * mm, "end": v(-29.4, 14) * mm});
            skLineSegment(sketch, "E2830", {"start": v(-29.4, 14) * mm, "end": v(-29.4, 15) * mm});
            skLineSegment(sketch, "E2831", {"start": v(-29.4, 15) * mm, "end": v(-27.6, 15) * mm});
            skLineSegment(sketch, "E2832", {"start": v(-27.6, 15) * mm, "end": v(-27.6, 14) * mm});
            skLineSegment(sketch, "E2833", {"start": v(-27.6, 17) * mm, "end": v(-29.4, 17) * mm});
            skLineSegment(sketch, "E2834", {"start": v(-29.4, 17) * mm, "end": v(-29.4, 18) * mm});
            skLineSegment(sketch, "E2835", {"start": v(-29.4, 18) * mm, "end": v(-27.6, 18) * mm});
            skLineSegment(sketch, "E2836", {"start": v(-27.6, 18) * mm, "end": v(-27.6, 17) * mm});
            skLineSegment(sketch, "E2837", {"start": v(-29.63, 15.62) * mm, "end": v(-29.63, 13.75) * mm});
            skLineSegment(sketch, "E2838", {"start": v(-29.63, 13.75) * mm, "end": v(-27.38, 13.75) * mm});
            skLineSegment(sketch, "E2839", {"start": v(-27.38, 13.75) * mm, "end": v(-27.38, 15.62) * mm});
            skArc(sketch, "E2840", {"start": v(-28.3, 16) * mm, "mid": v(-28.5, 16.2) * mm, "end": v(-28.7, 16) * mm});
            skArc(sketch, "E2841", {"start": v(-28.7, 16) * mm, "mid": v(-28.5, 15.8) * mm, "end": v(-28.3, 16) * mm});
            skLineSegment(sketch, "E2842", {"start": v(-27.38, 16.38) * mm, "end": v(-27.38, 18.25) * mm});
            skLineSegment(sketch, "E2843", {"start": v(-27.38, 18.25) * mm, "end": v(-29.63, 18.25) * mm});
            skLineSegment(sketch, "E2844", {"start": v(-29.63, 18.25) * mm, "end": v(-29.63, 16.38) * mm});
            skArc(sketch, "E2845", {"start": v(-29.63, 16.38) * mm, "mid": v(-29.25, 16) * mm, "end": v(-29.63, 15.62) * mm});
            skArc(sketch, "E2846", {"start": v(-27.38, 15.62) * mm, "mid": v(-27.75, 16) * mm, "end": v(-27.38, 16.38) * mm});
            skLineSegment(sketch, "E2847", {"start": v(-27.6, -2) * mm, "end": v(-29.4, -2) * mm});
            skLineSegment(sketch, "E2848", {"start": v(-29.4, -2) * mm, "end": v(-29.4, -1) * mm});
            skLineSegment(sketch, "E2849", {"start": v(-29.4, -1) * mm, "end": v(-27.6, -1) * mm});
            skLineSegment(sketch, "E2850", {"start": v(-27.6, -1) * mm, "end": v(-27.6, -2) * mm});
            skLineSegment(sketch, "E2851", {"start": v(-27.6, 1) * mm, "end": v(-29.4, 1) * mm});
            skLineSegment(sketch, "E2852", {"start": v(-29.4, 1) * mm, "end": v(-29.4, 2) * mm});
            skLineSegment(sketch, "E2853", {"start": v(-29.4, 2) * mm, "end": v(-27.6, 2) * mm});
            skLineSegment(sketch, "E2854", {"start": v(-27.6, 2) * mm, "end": v(-27.6, 1) * mm});
            skLineSegment(sketch, "E2855", {"start": v(-29.63, -0.38) * mm, "end": v(-29.63, -2.25) * mm});
            skLineSegment(sketch, "E2856", {"start": v(-29.63, -2.25) * mm, "end": v(-27.38, -2.25) * mm});
            skLineSegment(sketch, "E2857", {"start": v(-27.38, -2.25) * mm, "end": v(-27.38, -0.37) * mm});
            skArc(sketch, "E2858", {"start": v(-28.3, 0) * mm, "mid": v(-28.5, 0.2) * mm, "end": v(-28.7, 0) * mm});
            skArc(sketch, "E2859", {"start": v(-28.7, 0) * mm, "mid": v(-28.5, -0.2) * mm, "end": v(-28.3, 0) * mm});
            skLineSegment(sketch, "E2860", {"start": v(-27.38, 0.38) * mm, "end": v(-27.38, 2.25) * mm});
            skLineSegment(sketch, "E2861", {"start": v(-27.38, 2.25) * mm, "end": v(-29.63, 2.25) * mm});
            skLineSegment(sketch, "E2862", {"start": v(-29.63, 2.25) * mm, "end": v(-29.63, 0.37) * mm});
            skArc(sketch, "E2863", {"start": v(-29.63, 0.38) * mm, "mid": v(-29.25, 0) * mm, "end": v(-29.63, -0.38) * mm});
            skArc(sketch, "E2864", {"start": v(-27.38, -0.38) * mm, "mid": v(-27.75, 0) * mm, "end": v(-27.38, 0.38) * mm});
            skLineSegment(sketch, "E2865", {"start": v(-27.6, -10) * mm, "end": v(-29.4, -10) * mm});
            skLineSegment(sketch, "E2866", {"start": v(-29.4, -10) * mm, "end": v(-29.4, -9) * mm});
            skLineSegment(sketch, "E2867", {"start": v(-29.4, -9) * mm, "end": v(-27.6, -9) * mm});
            skLineSegment(sketch, "E2868", {"start": v(-27.6, -9) * mm, "end": v(-27.6, -10) * mm});
            skLineSegment(sketch, "E2869", {"start": v(-27.6, -7) * mm, "end": v(-29.4, -7) * mm});
            skLineSegment(sketch, "E2870", {"start": v(-29.4, -7) * mm, "end": v(-29.4, -6) * mm});
            skLineSegment(sketch, "E2871", {"start": v(-29.4, -6) * mm, "end": v(-27.6, -6) * mm});
            skLineSegment(sketch, "E2872", {"start": v(-27.6, -6) * mm, "end": v(-27.6, -7) * mm});
            skLineSegment(sketch, "E2873", {"start": v(-29.63, -8.38) * mm, "end": v(-29.63, -10.25) * mm});
            skLineSegment(sketch, "E2874", {"start": v(-29.63, -10.25) * mm, "end": v(-27.38, -10.25) * mm});
            skLineSegment(sketch, "E2875", {"start": v(-27.38, -10.25) * mm, "end": v(-27.38, -8.38) * mm});
            skArc(sketch, "E2876", {"start": v(-28.3, -8) * mm, "mid": v(-28.5, -7.8) * mm, "end": v(-28.7, -8) * mm});
            skArc(sketch, "E2877", {"start": v(-28.7, -8) * mm, "mid": v(-28.5, -8.2) * mm, "end": v(-28.3, -8) * mm});
            skLineSegment(sketch, "E2878", {"start": v(-27.38, -7.62) * mm, "end": v(-27.38, -5.75) * mm});
            skLineSegment(sketch, "E2879", {"start": v(-27.38, -5.75) * mm, "end": v(-29.63, -5.75) * mm});
            skLineSegment(sketch, "E2880", {"start": v(-29.63, -5.75) * mm, "end": v(-29.63, -7.62) * mm});
            skArc(sketch, "E2881", {"start": v(-29.63, -7.62) * mm, "mid": v(-29.25, -8) * mm, "end": v(-29.63, -8.38) * mm});
            skArc(sketch, "E2882", {"start": v(-27.38, -8.38) * mm, "mid": v(-27.75, -8) * mm, "end": v(-27.38, -7.62) * mm});
            skLineSegment(sketch, "E2883", {"start": v(-27.6, -18) * mm, "end": v(-29.4, -18) * mm});
            skLineSegment(sketch, "E2884", {"start": v(-29.4, -18) * mm, "end": v(-29.4, -17) * mm});
            skLineSegment(sketch, "E2885", {"start": v(-29.4, -17) * mm, "end": v(-27.6, -17) * mm});
            skLineSegment(sketch, "E2886", {"start": v(-27.6, -17) * mm, "end": v(-27.6, -18) * mm});
            skLineSegment(sketch, "E2887", {"start": v(-27.6, -15) * mm, "end": v(-29.4, -15) * mm});
            skLineSegment(sketch, "E2888", {"start": v(-29.4, -15) * mm, "end": v(-29.4, -14) * mm});
            skLineSegment(sketch, "E2889", {"start": v(-29.4, -14) * mm, "end": v(-27.6, -14) * mm});
            skLineSegment(sketch, "E2890", {"start": v(-27.6, -14) * mm, "end": v(-27.6, -15) * mm});
            skLineSegment(sketch, "E2891", {"start": v(-29.63, -16.38) * mm, "end": v(-29.63, -18.25) * mm});
            skLineSegment(sketch, "E2892", {"start": v(-29.63, -18.25) * mm, "end": v(-27.38, -18.25) * mm});
            skLineSegment(sketch, "E2893", {"start": v(-27.38, -18.25) * mm, "end": v(-27.38, -16.38) * mm});
            skArc(sketch, "E2894", {"start": v(-28.3, -16) * mm, "mid": v(-28.5, -15.8) * mm, "end": v(-28.7, -16) * mm});
            skArc(sketch, "E2895", {"start": v(-28.7, -16) * mm, "mid": v(-28.5, -16.2) * mm, "end": v(-28.3, -16) * mm});
            skLineSegment(sketch, "E2896", {"start": v(-27.38, -15.62) * mm, "end": v(-27.38, -13.75) * mm});
            skLineSegment(sketch, "E2897", {"start": v(-27.38, -13.75) * mm, "end": v(-29.63, -13.75) * mm});
            skLineSegment(sketch, "E2898", {"start": v(-29.63, -13.75) * mm, "end": v(-29.63, -15.62) * mm});
            skArc(sketch, "E2899", {"start": v(-29.63, -15.62) * mm, "mid": v(-29.25, -16) * mm, "end": v(-29.63, -16.38) * mm});
            skArc(sketch, "E2900", {"start": v(-27.38, -16.38) * mm, "mid": v(-27.75, -16) * mm, "end": v(-27.38, -15.62) * mm});
            skLineSegment(sketch, "E2901", {"start": v(4, -29.88) * mm, "end": v(4, -31.48) * mm});
            skLineSegment(sketch, "E2902", {"start": v(4, -31.48) * mm, "end": v(1, -31.48) * mm});
            skLineSegment(sketch, "E2903", {"start": v(1, -31.48) * mm, "end": v(1, -29.88) * mm});
            skLineSegment(sketch, "E2904", {"start": v(1, -29.88) * mm, "end": v(4, -29.88) * mm});
            skLineSegment(sketch, "E2905", {"start": v(0.79, -23.53) * mm, "end": v(0.79, -25.12) * mm});
            skLineSegment(sketch, "E2906", {"start": v(0.79, -25.12) * mm, "end": v(-0.41, -25.12) * mm});
            skLineSegment(sketch, "E2907", {"start": v(-0.41, -25.12) * mm, "end": v(-0.41, -23.53) * mm});
            skLineSegment(sketch, "E2908", {"start": v(-0.41, -23.53) * mm, "end": v(0.79, -23.53) * mm});
            skLineSegment(sketch, "E2909", {"start": v(3.1, -23.53) * mm, "end": v(3.1, -25.12) * mm});
            skLineSegment(sketch, "E2910", {"start": v(3.1, -25.12) * mm, "end": v(1.9, -25.12) * mm});
            skLineSegment(sketch, "E2911", {"start": v(1.9, -25.12) * mm, "end": v(1.9, -23.53) * mm});
            skLineSegment(sketch, "E2912", {"start": v(1.9, -23.53) * mm, "end": v(3.1, -23.53) * mm});
            skLineSegment(sketch, "E2913", {"start": v(5.41, -23.53) * mm, "end": v(5.41, -25.12) * mm});
            skLineSegment(sketch, "E2914", {"start": v(5.41, -25.12) * mm, "end": v(4.21, -25.12) * mm});
            skLineSegment(sketch, "E2915", {"start": v(4.21, -25.12) * mm, "end": v(4.21, -23.53) * mm});
            skLineSegment(sketch, "E2916", {"start": v(4.21, -23.53) * mm, "end": v(5.41, -23.53) * mm});
            skLineSegment(sketch, "E2917", {"start": v(-0.67, -25.85) * mm, "end": v(5.67, -25.85) * mm});
            skLineSegment(sketch, "E2918", {"start": v(-0.67, -29.15) * mm, "end": v(-0.67, -25.85) * mm});
            skLineSegment(sketch, "E2919", {"start": v(5.67, -29.15) * mm, "end": v(-0.67, -29.15) * mm});
            skLineSegment(sketch, "E2920", {"start": v(5.67, -25.85) * mm, "end": v(5.67, -29.15) * mm});
            skLineSegment(sketch, "E2921", {"start": v(-14.5, -21.25) * mm, "end": v(-15.5, -21.25) * mm});
            skLineSegment(sketch, "E2922", {"start": v(-15.5, -21.25) * mm, "end": v(-15.5, -20.25) * mm});
            skLineSegment(sketch, "E2923", {"start": v(-15.5, -20.25) * mm, "end": v(-14.5, -20.25) * mm});
            skLineSegment(sketch, "E2924", {"start": v(-14.5, -20.25) * mm, "end": v(-14.5, -21.25) * mm});
            skLineSegment(sketch, "E2925", {"start": v(-14.5, -19.75) * mm, "end": v(-15.5, -19.75) * mm});
            skLineSegment(sketch, "E2926", {"start": v(-15.5, -19.75) * mm, "end": v(-15.5, -18.75) * mm});
            skLineSegment(sketch, "E2927", {"start": v(-15.5, -18.75) * mm, "end": v(-14.5, -18.75) * mm});
            skLineSegment(sketch, "E2928", {"start": v(-14.5, -18.75) * mm, "end": v(-14.5, -19.75) * mm});
            skArc(sketch, "E2929", {"start": v(-14.6, -21.5) * mm, "mid": v(-14.39, -21.41) * mm, "end": v(-14.3, -21.2) * mm});
            skLineSegment(sketch, "E2930", {"start": v(-15.4, -21.5) * mm, "end": v(-14.6, -21.5) * mm});
            skArc(sketch, "E2931", {"start": v(-15.4, -21.5) * mm, "mid": v(-15.61, -21.41) * mm, "end": v(-15.7, -21.2) * mm});
            skLineSegment(sketch, "E2932", {"start": v(-14.3, -18.8) * mm, "end": v(-14.3, -21.2) * mm});
            skLineSegment(sketch, "E2933", {"start": v(-15.7, -21.2) * mm, "end": v(-15.7, -18.8) * mm});
            skArc(sketch, "E2934", {"start": v(-14.9, -20) * mm, "mid": v(-15, -19.9) * mm, "end": v(-15.1, -20) * mm});
            skArc(sketch, "E2935", {"start": v(-15.1, -20) * mm, "mid": v(-15, -20.1) * mm, "end": v(-14.9, -20) * mm});
            skArc(sketch, "E2936", {"start": v(-14.3, -18.8) * mm, "mid": v(-14.39, -18.59) * mm, "end": v(-14.6, -18.5) * mm});
            skArc(sketch, "E2937", {"start": v(-15.4, -18.5) * mm, "mid": v(-15.61, -18.59) * mm, "end": v(-15.7, -18.8) * mm});
            skLineSegment(sketch, "E2938", {"start": v(-14.6, -18.5) * mm, "end": v(-15.4, -18.5) * mm});
            skLineSegment(sketch, "E2939", {"start": v(6, -20.25) * mm, "end": v(5, -20.25) * mm});
            skLineSegment(sketch, "E2940", {"start": v(5, -20.25) * mm, "end": v(5, -19.25) * mm});
            skLineSegment(sketch, "E2941", {"start": v(5, -19.25) * mm, "end": v(6, -19.25) * mm});
            skLineSegment(sketch, "E2942", {"start": v(6, -19.25) * mm, "end": v(6, -20.25) * mm});
            skLineSegment(sketch, "E2943", {"start": v(6, -18.75) * mm, "end": v(5, -18.75) * mm});
            skLineSegment(sketch, "E2944", {"start": v(5, -18.75) * mm, "end": v(5, -17.75) * mm});
            skLineSegment(sketch, "E2945", {"start": v(5, -17.75) * mm, "end": v(6, -17.75) * mm});
            skLineSegment(sketch, "E2946", {"start": v(6, -17.75) * mm, "end": v(6, -18.75) * mm});
            skArc(sketch, "E2947", {"start": v(5.9, -20.5) * mm, "mid": v(6.11, -20.41) * mm, "end": v(6.2, -20.2) * mm});
            skLineSegment(sketch, "E2948", {"start": v(5.1, -20.5) * mm, "end": v(5.9, -20.5) * mm});
            skArc(sketch, "E2949", {"start": v(5.1, -20.5) * mm, "mid": v(4.89, -20.41) * mm, "end": v(4.8, -20.2) * mm});
            skLineSegment(sketch, "E2950", {"start": v(6.2, -17.8) * mm, "end": v(6.2, -20.2) * mm});
            skLineSegment(sketch, "E2951", {"start": v(4.8, -20.2) * mm, "end": v(4.8, -17.8) * mm});
            skArc(sketch, "E2952", {"start": v(5.6, -19) * mm, "mid": v(5.5, -18.9) * mm, "end": v(5.4, -19) * mm});
            skArc(sketch, "E2953", {"start": v(5.4, -19) * mm, "mid": v(5.5, -19.1) * mm, "end": v(5.6, -19) * mm});
            skArc(sketch, "E2954", {"start": v(6.2, -17.8) * mm, "mid": v(6.11, -17.59) * mm, "end": v(5.9, -17.5) * mm});
            skArc(sketch, "E2955", {"start": v(5.1, -17.5) * mm, "mid": v(4.89, -17.59) * mm, "end": v(4.8, -17.8) * mm});
            skLineSegment(sketch, "E2956", {"start": v(5.9, -17.5) * mm, "end": v(5.1, -17.5) * mm});
            skLineSegment(sketch, "E2957", {"start": v(-23.5, 33.75) * mm, "end": v(-22.5, 33.75) * mm});
            skLineSegment(sketch, "E2958", {"start": v(-22.5, 33.75) * mm, "end": v(-22.5, 32.75) * mm});
            skLineSegment(sketch, "E2959", {"start": v(-22.5, 32.75) * mm, "end": v(-23.5, 32.75) * mm});
            skLineSegment(sketch, "E2960", {"start": v(-23.5, 32.75) * mm, "end": v(-23.5, 33.75) * mm});
            skLineSegment(sketch, "E2961", {"start": v(-23.5, 32.25) * mm, "end": v(-22.5, 32.25) * mm});
            skLineSegment(sketch, "E2962", {"start": v(-22.5, 32.25) * mm, "end": v(-22.5, 31.25) * mm});
            skLineSegment(sketch, "E2963", {"start": v(-22.5, 31.25) * mm, "end": v(-23.5, 31.25) * mm});
            skLineSegment(sketch, "E2964", {"start": v(-23.5, 31.25) * mm, "end": v(-23.5, 32.25) * mm});
            skArc(sketch, "E2965", {"start": v(-23.4, 34) * mm, "mid": v(-23.61, 33.91) * mm, "end": v(-23.7, 33.7) * mm});
            skLineSegment(sketch, "E2966", {"start": v(-22.6, 34) * mm, "end": v(-23.4, 34) * mm});
            skArc(sketch, "E2967", {"start": v(-22.6, 34) * mm, "mid": v(-22.39, 33.91) * mm, "end": v(-22.3, 33.7) * mm});
            skLineSegment(sketch, "E2968", {"start": v(-23.7, 31.3) * mm, "end": v(-23.7, 33.7) * mm});
            skLineSegment(sketch, "E2969", {"start": v(-22.3, 33.7) * mm, "end": v(-22.3, 31.3) * mm});
            skArc(sketch, "E2970", {"start": v(-22.9, 32.5) * mm, "mid": v(-23, 32.6) * mm, "end": v(-23.1, 32.5) * mm});
            skArc(sketch, "E2971", {"start": v(-23.1, 32.5) * mm, "mid": v(-23, 32.4) * mm, "end": v(-22.9, 32.5) * mm});
            skArc(sketch, "E2972", {"start": v(-23.7, 31.3) * mm, "mid": v(-23.61, 31.09) * mm, "end": v(-23.4, 31) * mm});
            skArc(sketch, "E2973", {"start": v(-22.6, 31) * mm, "mid": v(-22.39, 31.09) * mm, "end": v(-22.3, 31.3) * mm});
            skLineSegment(sketch, "E2974", {"start": v(-23.4, 31) * mm, "end": v(-22.6, 31) * mm});
            skLineSegment(sketch, "E2975", {"start": v(-23.5, 25.75) * mm, "end": v(-22.5, 25.75) * mm});
            skLineSegment(sketch, "E2976", {"start": v(-22.5, 25.75) * mm, "end": v(-22.5, 24.75) * mm});
            skLineSegment(sketch, "E2977", {"start": v(-22.5, 24.75) * mm, "end": v(-23.5, 24.75) * mm});
            skLineSegment(sketch, "E2978", {"start": v(-23.5, 24.75) * mm, "end": v(-23.5, 25.75) * mm});
            skLineSegment(sketch, "E2979", {"start": v(-23.5, 24.25) * mm, "end": v(-22.5, 24.25) * mm});
            skLineSegment(sketch, "E2980", {"start": v(-22.5, 24.25) * mm, "end": v(-22.5, 23.25) * mm});
            skLineSegment(sketch, "E2981", {"start": v(-22.5, 23.25) * mm, "end": v(-23.5, 23.25) * mm});
            skLineSegment(sketch, "E2982", {"start": v(-23.5, 23.25) * mm, "end": v(-23.5, 24.25) * mm});
            skArc(sketch, "E2983", {"start": v(-23.4, 26) * mm, "mid": v(-23.61, 25.91) * mm, "end": v(-23.7, 25.7) * mm});
            skLineSegment(sketch, "E2984", {"start": v(-22.6, 26) * mm, "end": v(-23.4, 26) * mm});
            skArc(sketch, "E2985", {"start": v(-22.6, 26) * mm, "mid": v(-22.39, 25.91) * mm, "end": v(-22.3, 25.7) * mm});
            skLineSegment(sketch, "E2986", {"start": v(-23.7, 23.3) * mm, "end": v(-23.7, 25.7) * mm});
            skLineSegment(sketch, "E2987", {"start": v(-22.3, 25.7) * mm, "end": v(-22.3, 23.3) * mm});
            skArc(sketch, "E2988", {"start": v(-22.9, 24.5) * mm, "mid": v(-23, 24.6) * mm, "end": v(-23.1, 24.5) * mm});
            skArc(sketch, "E2989", {"start": v(-23.1, 24.5) * mm, "mid": v(-23, 24.4) * mm, "end": v(-22.9, 24.5) * mm});
            skArc(sketch, "E2990", {"start": v(-23.7, 23.3) * mm, "mid": v(-23.61, 23.09) * mm, "end": v(-23.4, 23) * mm});
            skArc(sketch, "E2991", {"start": v(-22.6, 23) * mm, "mid": v(-22.39, 23.09) * mm, "end": v(-22.3, 23.3) * mm});
            skLineSegment(sketch, "E2992", {"start": v(-23.4, 23) * mm, "end": v(-22.6, 23) * mm});
            skLineSegment(sketch, "E2993", {"start": v(-23.5, 17.75) * mm, "end": v(-22.5, 17.75) * mm});
            skLineSegment(sketch, "E2994", {"start": v(-22.5, 17.75) * mm, "end": v(-22.5, 16.75) * mm});
            skLineSegment(sketch, "E2995", {"start": v(-22.5, 16.75) * mm, "end": v(-23.5, 16.75) * mm});
            skLineSegment(sketch, "E2996", {"start": v(-23.5, 16.75) * mm, "end": v(-23.5, 17.75) * mm});
            skLineSegment(sketch, "E2997", {"start": v(-23.5, 16.25) * mm, "end": v(-22.5, 16.25) * mm});
            skLineSegment(sketch, "E2998", {"start": v(-22.5, 16.25) * mm, "end": v(-22.5, 15.25) * mm});
            skLineSegment(sketch, "E2999", {"start": v(-22.5, 15.25) * mm, "end": v(-23.5, 15.25) * mm});
            skLineSegment(sketch, "E3000", {"start": v(-23.5, 15.25) * mm, "end": v(-23.5, 16.25) * mm});
            skArc(sketch, "E3001", {"start": v(-23.4, 18) * mm, "mid": v(-23.61, 17.91) * mm, "end": v(-23.7, 17.7) * mm});
            skLineSegment(sketch, "E3002", {"start": v(-22.6, 18) * mm, "end": v(-23.4, 18) * mm});
            skArc(sketch, "E3003", {"start": v(-22.6, 18) * mm, "mid": v(-22.39, 17.91) * mm, "end": v(-22.3, 17.7) * mm});
            skLineSegment(sketch, "E3004", {"start": v(-23.7, 15.3) * mm, "end": v(-23.7, 17.7) * mm});
            skLineSegment(sketch, "E3005", {"start": v(-22.3, 17.7) * mm, "end": v(-22.3, 15.3) * mm});
            skArc(sketch, "E3006", {"start": v(-22.9, 16.5) * mm, "mid": v(-23, 16.6) * mm, "end": v(-23.1, 16.5) * mm});
            skArc(sketch, "E3007", {"start": v(-23.1, 16.5) * mm, "mid": v(-23, 16.4) * mm, "end": v(-22.9, 16.5) * mm});
            skArc(sketch, "E3008", {"start": v(-23.7, 15.3) * mm, "mid": v(-23.61, 15.09) * mm, "end": v(-23.4, 15) * mm});
            skArc(sketch, "E3009", {"start": v(-22.6, 15) * mm, "mid": v(-22.39, 15.09) * mm, "end": v(-22.3, 15.3) * mm});
            skLineSegment(sketch, "E3010", {"start": v(-23.4, 15) * mm, "end": v(-22.6, 15) * mm});
            skLineSegment(sketch, "E3011", {"start": v(-23.5, 9.75) * mm, "end": v(-22.5, 9.75) * mm});
            skLineSegment(sketch, "E3012", {"start": v(-22.5, 9.75) * mm, "end": v(-22.5, 8.75) * mm});
            skLineSegment(sketch, "E3013", {"start": v(-22.5, 8.75) * mm, "end": v(-23.5, 8.75) * mm});
            skLineSegment(sketch, "E3014", {"start": v(-23.5, 8.75) * mm, "end": v(-23.5, 9.75) * mm});
            skLineSegment(sketch, "E3015", {"start": v(-23.5, 8.25) * mm, "end": v(-22.5, 8.25) * mm});
            skLineSegment(sketch, "E3016", {"start": v(-22.5, 8.25) * mm, "end": v(-22.5, 7.25) * mm});
            skLineSegment(sketch, "E3017", {"start": v(-22.5, 7.25) * mm, "end": v(-23.5, 7.25) * mm});
            skLineSegment(sketch, "E3018", {"start": v(-23.5, 7.25) * mm, "end": v(-23.5, 8.25) * mm});
            skArc(sketch, "E3019", {"start": v(-23.4, 10) * mm, "mid": v(-23.61, 9.91) * mm, "end": v(-23.7, 9.7) * mm});
            skLineSegment(sketch, "E3020", {"start": v(-22.6, 10) * mm, "end": v(-23.4, 10) * mm});
            skArc(sketch, "E3021", {"start": v(-22.6, 10) * mm, "mid": v(-22.39, 9.91) * mm, "end": v(-22.3, 9.7) * mm});
            skLineSegment(sketch, "E3022", {"start": v(-23.7, 7.3) * mm, "end": v(-23.7, 9.7) * mm});
            skLineSegment(sketch, "E3023", {"start": v(-22.3, 9.7) * mm, "end": v(-22.3, 7.3) * mm});
            skArc(sketch, "E3024", {"start": v(-22.9, 8.5) * mm, "mid": v(-23, 8.6) * mm, "end": v(-23.1, 8.5) * mm});
            skArc(sketch, "E3025", {"start": v(-23.1, 8.5) * mm, "mid": v(-23, 8.4) * mm, "end": v(-22.9, 8.5) * mm});
            skArc(sketch, "E3026", {"start": v(-23.7, 7.3) * mm, "mid": v(-23.61, 7.09) * mm, "end": v(-23.4, 7) * mm});
            skArc(sketch, "E3027", {"start": v(-22.6, 7) * mm, "mid": v(-22.39, 7.09) * mm, "end": v(-22.3, 7.3) * mm});
            skLineSegment(sketch, "E3028", {"start": v(-23.4, 7) * mm, "end": v(-22.6, 7) * mm});
            skLineSegment(sketch, "E3029", {"start": v(-23.5, 1.75) * mm, "end": v(-22.5, 1.75) * mm});
            skLineSegment(sketch, "E3030", {"start": v(-22.5, 1.75) * mm, "end": v(-22.5, 0.75) * mm});
            skLineSegment(sketch, "E3031", {"start": v(-22.5, 0.75) * mm, "end": v(-23.5, 0.75) * mm});
            skLineSegment(sketch, "E3032", {"start": v(-23.5, 0.75) * mm, "end": v(-23.5, 1.75) * mm});
            skLineSegment(sketch, "E3033", {"start": v(-23.5, 0.25) * mm, "end": v(-22.5, 0.25) * mm});
            skLineSegment(sketch, "E3034", {"start": v(-22.5, 0.25) * mm, "end": v(-22.5, -0.75) * mm});
            skLineSegment(sketch, "E3035", {"start": v(-22.5, -0.75) * mm, "end": v(-23.5, -0.75) * mm});
            skLineSegment(sketch, "E3036", {"start": v(-23.5, -0.75) * mm, "end": v(-23.5, 0.25) * mm});
            skArc(sketch, "E3037", {"start": v(-23.4, 2) * mm, "mid": v(-23.61, 1.91) * mm, "end": v(-23.7, 1.7) * mm});
            skLineSegment(sketch, "E3038", {"start": v(-22.6, 2) * mm, "end": v(-23.4, 2) * mm});
            skArc(sketch, "E3039", {"start": v(-22.6, 2) * mm, "mid": v(-22.39, 1.91) * mm, "end": v(-22.3, 1.7) * mm});
            skLineSegment(sketch, "E3040", {"start": v(-23.7, -0.7) * mm, "end": v(-23.7, 1.7) * mm});
            skLineSegment(sketch, "E3041", {"start": v(-22.3, 1.7) * mm, "end": v(-22.3, -0.7) * mm});
            skArc(sketch, "E3042", {"start": v(-22.9, 0.5) * mm, "mid": v(-23, 0.6) * mm, "end": v(-23.1, 0.5) * mm});
            skArc(sketch, "E3043", {"start": v(-23.1, 0.5) * mm, "mid": v(-23, 0.4) * mm, "end": v(-22.9, 0.5) * mm});
            skArc(sketch, "E3044", {"start": v(-23.7, -0.7) * mm, "mid": v(-23.61, -0.91) * mm, "end": v(-23.4, -1) * mm});
            skArc(sketch, "E3045", {"start": v(-22.6, -1) * mm, "mid": v(-22.39, -0.91) * mm, "end": v(-22.3, -0.7) * mm});
            skLineSegment(sketch, "E3046", {"start": v(-23.4, -1) * mm, "end": v(-22.6, -1) * mm});
            skLineSegment(sketch, "E3047", {"start": v(-23.5, -6.25) * mm, "end": v(-22.5, -6.25) * mm});
            skLineSegment(sketch, "E3048", {"start": v(-22.5, -6.25) * mm, "end": v(-22.5, -7.25) * mm});
            skLineSegment(sketch, "E3049", {"start": v(-22.5, -7.25) * mm, "end": v(-23.5, -7.25) * mm});
            skLineSegment(sketch, "E3050", {"start": v(-23.5, -7.25) * mm, "end": v(-23.5, -6.25) * mm});
            skLineSegment(sketch, "E3051", {"start": v(-23.5, -7.75) * mm, "end": v(-22.5, -7.75) * mm});
            skLineSegment(sketch, "E3052", {"start": v(-22.5, -7.75) * mm, "end": v(-22.5, -8.75) * mm});
            skLineSegment(sketch, "E3053", {"start": v(-22.5, -8.75) * mm, "end": v(-23.5, -8.75) * mm});
            skLineSegment(sketch, "E3054", {"start": v(-23.5, -8.75) * mm, "end": v(-23.5, -7.75) * mm});
            skArc(sketch, "E3055", {"start": v(-23.4, -6) * mm, "mid": v(-23.61, -6.09) * mm, "end": v(-23.7, -6.3) * mm});
            skLineSegment(sketch, "E3056", {"start": v(-22.6, -6) * mm, "end": v(-23.4, -6) * mm});
            skArc(sketch, "E3057", {"start": v(-22.6, -6) * mm, "mid": v(-22.39, -6.09) * mm, "end": v(-22.3, -6.3) * mm});
            skLineSegment(sketch, "E3058", {"start": v(-23.7, -8.7) * mm, "end": v(-23.7, -6.3) * mm});
            skLineSegment(sketch, "E3059", {"start": v(-22.3, -6.3) * mm, "end": v(-22.3, -8.7) * mm});
            skArc(sketch, "E3060", {"start": v(-22.9, -7.5) * mm, "mid": v(-23, -7.4) * mm, "end": v(-23.1, -7.5) * mm});
            skArc(sketch, "E3061", {"start": v(-23.1, -7.5) * mm, "mid": v(-23, -7.6) * mm, "end": v(-22.9, -7.5) * mm});
            skArc(sketch, "E3062", {"start": v(-23.7, -8.7) * mm, "mid": v(-23.61, -8.91) * mm, "end": v(-23.4, -9) * mm});
            skArc(sketch, "E3063", {"start": v(-22.6, -9) * mm, "mid": v(-22.39, -8.91) * mm, "end": v(-22.3, -8.7) * mm});
            skLineSegment(sketch, "E3064", {"start": v(-23.4, -9) * mm, "end": v(-22.6, -9) * mm});
            skLineSegment(sketch, "E3065", {"start": v(-14.5, 36.75) * mm, "end": v(-15.5, 36.75) * mm});
            skLineSegment(sketch, "E3066", {"start": v(-15.5, 36.75) * mm, "end": v(-15.5, 37.75) * mm});
            skLineSegment(sketch, "E3067", {"start": v(-15.5, 37.75) * mm, "end": v(-14.5, 37.75) * mm});
            skLineSegment(sketch, "E3068", {"start": v(-14.5, 37.75) * mm, "end": v(-14.5, 36.75) * mm});
            skLineSegment(sketch, "E3069", {"start": v(-14.5, 38.25) * mm, "end": v(-15.5, 38.25) * mm});
            skLineSegment(sketch, "E3070", {"start": v(-15.5, 38.25) * mm, "end": v(-15.5, 39.25) * mm});
            skLineSegment(sketch, "E3071", {"start": v(-15.5, 39.25) * mm, "end": v(-14.5, 39.25) * mm});
            skLineSegment(sketch, "E3072", {"start": v(-14.5, 39.25) * mm, "end": v(-14.5, 38.25) * mm});
            skArc(sketch, "E3073", {"start": v(-14.6, 36.5) * mm, "mid": v(-14.39, 36.59) * mm, "end": v(-14.3, 36.8) * mm});
            skLineSegment(sketch, "E3074", {"start": v(-15.4, 36.5) * mm, "end": v(-14.6, 36.5) * mm});
            skArc(sketch, "E3075", {"start": v(-15.4, 36.5) * mm, "mid": v(-15.61, 36.59) * mm, "end": v(-15.7, 36.8) * mm});
            skLineSegment(sketch, "E3076", {"start": v(-14.3, 39.2) * mm, "end": v(-14.3, 36.8) * mm});
            skLineSegment(sketch, "E3077", {"start": v(-15.7, 36.8) * mm, "end": v(-15.7, 39.2) * mm});
            skArc(sketch, "E3078", {"start": v(-14.9, 38) * mm, "mid": v(-15, 38.1) * mm, "end": v(-15.1, 38) * mm});
            skArc(sketch, "E3079", {"start": v(-15.1, 38) * mm, "mid": v(-15, 37.9) * mm, "end": v(-14.9, 38) * mm});
            skArc(sketch, "E3080", {"start": v(-14.3, 39.2) * mm, "mid": v(-14.39, 39.41) * mm, "end": v(-14.6, 39.5) * mm});
            skArc(sketch, "E3081", {"start": v(-15.4, 39.5) * mm, "mid": v(-15.61, 39.41) * mm, "end": v(-15.7, 39.2) * mm});
            skLineSegment(sketch, "E3082", {"start": v(-14.6, 39.5) * mm, "end": v(-15.4, 39.5) * mm});
            skLineSegment(sketch, "E3083", {"start": v(-20, 33) * mm, "end": v(-19, 33) * mm});
            skLineSegment(sketch, "E3084", {"start": v(-19, 33) * mm, "end": v(-19, 32) * mm});
            skLineSegment(sketch, "E3085", {"start": v(-19, 32) * mm, "end": v(-20, 32) * mm});
            skLineSegment(sketch, "E3086", {"start": v(-20, 32) * mm, "end": v(-20, 33) * mm});
            skLineSegment(sketch, "E3087", {"start": v(-20, 31.5) * mm, "end": v(-19, 31.5) * mm});
            skLineSegment(sketch, "E3088", {"start": v(-19, 31.5) * mm, "end": v(-19, 30.5) * mm});
            skLineSegment(sketch, "E3089", {"start": v(-19, 30.5) * mm, "end": v(-20, 30.5) * mm});
            skLineSegment(sketch, "E3090", {"start": v(-20, 30.5) * mm, "end": v(-20, 31.5) * mm});
            skArc(sketch, "E3091", {"start": v(-19.9, 33.25) * mm, "mid": v(-20.11, 33.16) * mm, "end": v(-20.2, 32.95) * mm});
            skLineSegment(sketch, "E3092", {"start": v(-19.1, 33.25) * mm, "end": v(-19.9, 33.25) * mm});
            skArc(sketch, "E3093", {"start": v(-19.1, 33.25) * mm, "mid": v(-18.89, 33.16) * mm, "end": v(-18.8, 32.95) * mm});
            skLineSegment(sketch, "E3094", {"start": v(-20.2, 30.55) * mm, "end": v(-20.2, 32.95) * mm});
            skLineSegment(sketch, "E3095", {"start": v(-18.8, 32.95) * mm, "end": v(-18.8, 30.55) * mm});
            skArc(sketch, "E3096", {"start": v(-19.4, 31.75) * mm, "mid": v(-19.5, 31.85) * mm, "end": v(-19.6, 31.75) * mm});
            skArc(sketch, "E3097", {"start": v(-19.6, 31.75) * mm, "mid": v(-19.5, 31.65) * mm, "end": v(-19.4, 31.75) * mm});
            skArc(sketch, "E3098", {"start": v(-20.2, 30.55) * mm, "mid": v(-20.11, 30.34) * mm, "end": v(-19.9, 30.25) * mm});
            skArc(sketch, "E3099", {"start": v(-19.1, 30.25) * mm, "mid": v(-18.89, 30.34) * mm, "end": v(-18.8, 30.55) * mm});
            skLineSegment(sketch, "E3100", {"start": v(-19.9, 30.25) * mm, "end": v(-19.1, 30.25) * mm});
            skLineSegment(sketch, "E3101", {"start": v(-19, 27.25) * mm, "end": v(-20, 27.25) * mm});
            skLineSegment(sketch, "E3102", {"start": v(-20, 27.25) * mm, "end": v(-20, 28.25) * mm});
            skLineSegment(sketch, "E3103", {"start": v(-20, 28.25) * mm, "end": v(-19, 28.25) * mm});
            skLineSegment(sketch, "E3104", {"start": v(-19, 28.25) * mm, "end": v(-19, 27.25) * mm});
            skLineSegment(sketch, "E3105", {"start": v(-19, 28.75) * mm, "end": v(-20, 28.75) * mm});
            skLineSegment(sketch, "E3106", {"start": v(-20, 28.75) * mm, "end": v(-20, 29.75) * mm});
            skLineSegment(sketch, "E3107", {"start": v(-20, 29.75) * mm, "end": v(-19, 29.75) * mm});
            skLineSegment(sketch, "E3108", {"start": v(-19, 29.75) * mm, "end": v(-19, 28.75) * mm});
            skArc(sketch, "E3109", {"start": v(-19.1, 27) * mm, "mid": v(-18.89, 27.09) * mm, "end": v(-18.8, 27.3) * mm});
            skLineSegment(sketch, "E3110", {"start": v(-19.9, 27) * mm, "end": v(-19.1, 27) * mm});
            skArc(sketch, "E3111", {"start": v(-19.9, 27) * mm, "mid": v(-20.11, 27.09) * mm, "end": v(-20.2, 27.3) * mm});
            skLineSegment(sketch, "E3112", {"start": v(-18.8, 29.7) * mm, "end": v(-18.8, 27.3) * mm});
            skLineSegment(sketch, "E3113", {"start": v(-20.2, 27.3) * mm, "end": v(-20.2, 29.7) * mm});
            skArc(sketch, "E3114", {"start": v(-19.4, 28.5) * mm, "mid": v(-19.5, 28.6) * mm, "end": v(-19.6, 28.5) * mm});
            skArc(sketch, "E3115", {"start": v(-19.6, 28.5) * mm, "mid": v(-19.5, 28.4) * mm, "end": v(-19.4, 28.5) * mm});
            skArc(sketch, "E3116", {"start": v(-18.8, 29.7) * mm, "mid": v(-18.89, 29.91) * mm, "end": v(-19.1, 30) * mm});
            skArc(sketch, "E3117", {"start": v(-19.9, 30) * mm, "mid": v(-20.11, 29.91) * mm, "end": v(-20.2, 29.7) * mm});
            skLineSegment(sketch, "E3118", {"start": v(-19.1, 30) * mm, "end": v(-19.9, 30) * mm});
            skLineSegment(sketch, "E3119", {"start": v(-14.5, 20.75) * mm, "end": v(-15.5, 20.75) * mm});
            skLineSegment(sketch, "E3120", {"start": v(-15.5, 20.75) * mm, "end": v(-15.5, 21.75) * mm});
            skLineSegment(sketch, "E3121", {"start": v(-15.5, 21.75) * mm, "end": v(-14.5, 21.75) * mm});
            skLineSegment(sketch, "E3122", {"start": v(-14.5, 21.75) * mm, "end": v(-14.5, 20.75) * mm});
            skLineSegment(sketch, "E3123", {"start": v(-14.5, 22.25) * mm, "end": v(-15.5, 22.25) * mm});
            skLineSegment(sketch, "E3124", {"start": v(-15.5, 22.25) * mm, "end": v(-15.5, 23.25) * mm});
            skLineSegment(sketch, "E3125", {"start": v(-15.5, 23.25) * mm, "end": v(-14.5, 23.25) * mm});
            skLineSegment(sketch, "E3126", {"start": v(-14.5, 23.25) * mm, "end": v(-14.5, 22.25) * mm});
            skArc(sketch, "E3127", {"start": v(-14.6, 20.5) * mm, "mid": v(-14.39, 20.59) * mm, "end": v(-14.3, 20.8) * mm});
            skLineSegment(sketch, "E3128", {"start": v(-15.4, 20.5) * mm, "end": v(-14.6, 20.5) * mm});
            skArc(sketch, "E3129", {"start": v(-15.4, 20.5) * mm, "mid": v(-15.61, 20.59) * mm, "end": v(-15.7, 20.8) * mm});
            skLineSegment(sketch, "E3130", {"start": v(-14.3, 23.2) * mm, "end": v(-14.3, 20.8) * mm});
            skLineSegment(sketch, "E3131", {"start": v(-15.7, 20.8) * mm, "end": v(-15.7, 23.2) * mm});
            skArc(sketch, "E3132", {"start": v(-14.9, 22) * mm, "mid": v(-15, 22.1) * mm, "end": v(-15.1, 22) * mm});
            skArc(sketch, "E3133", {"start": v(-15.1, 22) * mm, "mid": v(-15, 21.9) * mm, "end": v(-14.9, 22) * mm});
            skArc(sketch, "E3134", {"start": v(-14.3, 23.2) * mm, "mid": v(-14.39, 23.41) * mm, "end": v(-14.6, 23.5) * mm});
            skArc(sketch, "E3135", {"start": v(-15.4, 23.5) * mm, "mid": v(-15.61, 23.41) * mm, "end": v(-15.7, 23.2) * mm});
            skLineSegment(sketch, "E3136", {"start": v(-14.6, 23.5) * mm, "end": v(-15.4, 23.5) * mm});
            skLineSegment(sketch, "E3137", {"start": v(-20, 17) * mm, "end": v(-19, 17) * mm});
            skLineSegment(sketch, "E3138", {"start": v(-19, 17) * mm, "end": v(-19, 16) * mm});
            skLineSegment(sketch, "E3139", {"start": v(-19, 16) * mm, "end": v(-20, 16) * mm});
            skLineSegment(sketch, "E3140", {"start": v(-20, 16) * mm, "end": v(-20, 17) * mm});
            skLineSegment(sketch, "E3141", {"start": v(-20, 15.5) * mm, "end": v(-19, 15.5) * mm});
            skLineSegment(sketch, "E3142", {"start": v(-19, 15.5) * mm, "end": v(-19, 14.5) * mm});
            skLineSegment(sketch, "E3143", {"start": v(-19, 14.5) * mm, "end": v(-20, 14.5) * mm});
            skLineSegment(sketch, "E3144", {"start": v(-20, 14.5) * mm, "end": v(-20, 15.5) * mm});
            skArc(sketch, "E3145", {"start": v(-19.9, 17.25) * mm, "mid": v(-20.11, 17.16) * mm, "end": v(-20.2, 16.95) * mm});
            skLineSegment(sketch, "E3146", {"start": v(-19.1, 17.25) * mm, "end": v(-19.9, 17.25) * mm});
            skArc(sketch, "E3147", {"start": v(-19.1, 17.25) * mm, "mid": v(-18.89, 17.16) * mm, "end": v(-18.8, 16.95) * mm});
            skLineSegment(sketch, "E3148", {"start": v(-20.2, 14.55) * mm, "end": v(-20.2, 16.95) * mm});
            skLineSegment(sketch, "E3149", {"start": v(-18.8, 16.95) * mm, "end": v(-18.8, 14.55) * mm});
            skArc(sketch, "E3150", {"start": v(-19.4, 15.75) * mm, "mid": v(-19.5, 15.85) * mm, "end": v(-19.6, 15.75) * mm});
            skArc(sketch, "E3151", {"start": v(-19.6, 15.75) * mm, "mid": v(-19.5, 15.65) * mm, "end": v(-19.4, 15.75) * mm});
            skArc(sketch, "E3152", {"start": v(-20.2, 14.55) * mm, "mid": v(-20.11, 14.34) * mm, "end": v(-19.9, 14.25) * mm});
            skArc(sketch, "E3153", {"start": v(-19.1, 14.25) * mm, "mid": v(-18.89, 14.34) * mm, "end": v(-18.8, 14.55) * mm});
            skLineSegment(sketch, "E3154", {"start": v(-19.9, 14.25) * mm, "end": v(-19.1, 14.25) * mm});
            skLineSegment(sketch, "E3155", {"start": v(-14.5, 4.75) * mm, "end": v(-15.5, 4.75) * mm});
            skLineSegment(sketch, "E3156", {"start": v(-15.5, 4.75) * mm, "end": v(-15.5, 5.75) * mm});
            skLineSegment(sketch, "E3157", {"start": v(-15.5, 5.75) * mm, "end": v(-14.5, 5.75) * mm});
            skLineSegment(sketch, "E3158", {"start": v(-14.5, 5.75) * mm, "end": v(-14.5, 4.75) * mm});
            skLineSegment(sketch, "E3159", {"start": v(-14.5, 6.25) * mm, "end": v(-15.5, 6.25) * mm});
            skLineSegment(sketch, "E3160", {"start": v(-15.5, 6.25) * mm, "end": v(-15.5, 7.25) * mm});
            skLineSegment(sketch, "E3161", {"start": v(-15.5, 7.25) * mm, "end": v(-14.5, 7.25) * mm});
            skLineSegment(sketch, "E3162", {"start": v(-14.5, 7.25) * mm, "end": v(-14.5, 6.25) * mm});
            skArc(sketch, "E3163", {"start": v(-14.6, 4.5) * mm, "mid": v(-14.39, 4.59) * mm, "end": v(-14.3, 4.8) * mm});
            skLineSegment(sketch, "E3164", {"start": v(-15.4, 4.5) * mm, "end": v(-14.6, 4.5) * mm});
            skArc(sketch, "E3165", {"start": v(-15.4, 4.5) * mm, "mid": v(-15.61, 4.59) * mm, "end": v(-15.7, 4.8) * mm});
            skLineSegment(sketch, "E3166", {"start": v(-14.3, 7.2) * mm, "end": v(-14.3, 4.8) * mm});
            skLineSegment(sketch, "E3167", {"start": v(-15.7, 4.8) * mm, "end": v(-15.7, 7.2) * mm});
            skArc(sketch, "E3168", {"start": v(-14.9, 6) * mm, "mid": v(-15, 6.1) * mm, "end": v(-15.1, 6) * mm});
            skArc(sketch, "E3169", {"start": v(-15.1, 6) * mm, "mid": v(-15, 5.9) * mm, "end": v(-14.9, 6) * mm});
            skArc(sketch, "E3170", {"start": v(-14.3, 7.2) * mm, "mid": v(-14.39, 7.41) * mm, "end": v(-14.6, 7.5) * mm});
            skArc(sketch, "E3171", {"start": v(-15.4, 7.5) * mm, "mid": v(-15.61, 7.41) * mm, "end": v(-15.7, 7.2) * mm});
            skLineSegment(sketch, "E3172", {"start": v(-14.6, 7.5) * mm, "end": v(-15.4, 7.5) * mm});
            skLineSegment(sketch, "E3173", {"start": v(-19, 11.25) * mm, "end": v(-20, 11.25) * mm});
            skLineSegment(sketch, "E3174", {"start": v(-20, 11.25) * mm, "end": v(-20, 12.25) * mm});
            skLineSegment(sketch, "E3175", {"start": v(-20, 12.25) * mm, "end": v(-19, 12.25) * mm});
            skLineSegment(sketch, "E3176", {"start": v(-19, 12.25) * mm, "end": v(-19, 11.25) * mm});
            skLineSegment(sketch, "E3177", {"start": v(-19, 12.75) * mm, "end": v(-20, 12.75) * mm});
            skLineSegment(sketch, "E3178", {"start": v(-20, 12.75) * mm, "end": v(-20, 13.75) * mm});
            skLineSegment(sketch, "E3179", {"start": v(-20, 13.75) * mm, "end": v(-19, 13.75) * mm});
            skLineSegment(sketch, "E3180", {"start": v(-19, 13.75) * mm, "end": v(-19, 12.75) * mm});
            skArc(sketch, "E3181", {"start": v(-19.1, 11) * mm, "mid": v(-18.89, 11.09) * mm, "end": v(-18.8, 11.3) * mm});
            skLineSegment(sketch, "E3182", {"start": v(-19.9, 11) * mm, "end": v(-19.1, 11) * mm});
            skArc(sketch, "E3183", {"start": v(-19.9, 11) * mm, "mid": v(-20.11, 11.09) * mm, "end": v(-20.2, 11.3) * mm});
            skLineSegment(sketch, "E3184", {"start": v(-18.8, 13.7) * mm, "end": v(-18.8, 11.3) * mm});
            skLineSegment(sketch, "E3185", {"start": v(-20.2, 11.3) * mm, "end": v(-20.2, 13.7) * mm});
            skArc(sketch, "E3186", {"start": v(-19.4, 12.5) * mm, "mid": v(-19.5, 12.6) * mm, "end": v(-19.6, 12.5) * mm});
            skArc(sketch, "E3187", {"start": v(-19.6, 12.5) * mm, "mid": v(-19.5, 12.4) * mm, "end": v(-19.4, 12.5) * mm});
            skArc(sketch, "E3188", {"start": v(-18.8, 13.7) * mm, "mid": v(-18.89, 13.91) * mm, "end": v(-19.1, 14) * mm});
            skArc(sketch, "E3189", {"start": v(-19.9, 14) * mm, "mid": v(-20.11, 13.91) * mm, "end": v(-20.2, 13.7) * mm});
            skLineSegment(sketch, "E3190", {"start": v(-19.1, 14) * mm, "end": v(-19.9, 14) * mm});
            skLineSegment(sketch, "E3191", {"start": v(-20, 1) * mm, "end": v(-19, 1) * mm});
            skLineSegment(sketch, "E3192", {"start": v(-19, 1) * mm, "end": v(-19, 0) * mm});
            skLineSegment(sketch, "E3193", {"start": v(-19, 0) * mm, "end": v(-20, 0) * mm});
            skLineSegment(sketch, "E3194", {"start": v(-20, 0) * mm, "end": v(-20, 1) * mm});
            skLineSegment(sketch, "E3195", {"start": v(-20, -0.5) * mm, "end": v(-19, -0.5) * mm});
            skLineSegment(sketch, "E3196", {"start": v(-19, -0.5) * mm, "end": v(-19, -1.5) * mm});
            skLineSegment(sketch, "E3197", {"start": v(-19, -1.5) * mm, "end": v(-20, -1.5) * mm});
            skLineSegment(sketch, "E3198", {"start": v(-20, -1.5) * mm, "end": v(-20, -0.5) * mm});
            skArc(sketch, "E3199", {"start": v(-19.9, 1.25) * mm, "mid": v(-20.11, 1.16) * mm, "end": v(-20.2, 0.95) * mm});
            skLineSegment(sketch, "E3200", {"start": v(-19.1, 1.25) * mm, "end": v(-19.9, 1.25) * mm});
            skArc(sketch, "E3201", {"start": v(-19.1, 1.25) * mm, "mid": v(-18.89, 1.16) * mm, "end": v(-18.8, 0.95) * mm});
            skLineSegment(sketch, "E3202", {"start": v(-20.2, -1.45) * mm, "end": v(-20.2, 0.95) * mm});
            skLineSegment(sketch, "E3203", {"start": v(-18.8, 0.95) * mm, "end": v(-18.8, -1.45) * mm});
            skArc(sketch, "E3204", {"start": v(-19.4, -0.25) * mm, "mid": v(-19.5, -0.15) * mm, "end": v(-19.6, -0.25) * mm});
            skArc(sketch, "E3205", {"start": v(-19.6, -0.25) * mm, "mid": v(-19.5, -0.35) * mm, "end": v(-19.4, -0.25) * mm});
            skArc(sketch, "E3206", {"start": v(-20.2, -1.45) * mm, "mid": v(-20.11, -1.66) * mm, "end": v(-19.9, -1.75) * mm});
            skArc(sketch, "E3207", {"start": v(-19.1, -1.75) * mm, "mid": v(-18.89, -1.66) * mm, "end": v(-18.8, -1.45) * mm});
            skLineSegment(sketch, "E3208", {"start": v(-19.9, -1.75) * mm, "end": v(-19.1, -1.75) * mm});
            skLineSegment(sketch, "E3209", {"start": v(-19, -4.75) * mm, "end": v(-20, -4.75) * mm});
            skLineSegment(sketch, "E3210", {"start": v(-20, -4.75) * mm, "end": v(-20, -3.75) * mm});
            skLineSegment(sketch, "E3211", {"start": v(-20, -3.75) * mm, "end": v(-19, -3.75) * mm});
            skLineSegment(sketch, "E3212", {"start": v(-19, -3.75) * mm, "end": v(-19, -4.75) * mm});
            skLineSegment(sketch, "E3213", {"start": v(-19, -3.25) * mm, "end": v(-20, -3.25) * mm});
            skLineSegment(sketch, "E3214", {"start": v(-20, -3.25) * mm, "end": v(-20, -2.25) * mm});
            skLineSegment(sketch, "E3215", {"start": v(-20, -2.25) * mm, "end": v(-19, -2.25) * mm});
            skLineSegment(sketch, "E3216", {"start": v(-19, -2.25) * mm, "end": v(-19, -3.25) * mm});
            skArc(sketch, "E3217", {"start": v(-19.1, -5) * mm, "mid": v(-18.89, -4.91) * mm, "end": v(-18.8, -4.7) * mm});
            skLineSegment(sketch, "E3218", {"start": v(-19.9, -5) * mm, "end": v(-19.1, -5) * mm});
            skArc(sketch, "E3219", {"start": v(-19.9, -5) * mm, "mid": v(-20.11, -4.91) * mm, "end": v(-20.2, -4.7) * mm});
            skLineSegment(sketch, "E3220", {"start": v(-18.8, -2.3) * mm, "end": v(-18.8, -4.7) * mm});
            skLineSegment(sketch, "E3221", {"start": v(-20.2, -4.7) * mm, "end": v(-20.2, -2.3) * mm});
            skArc(sketch, "E3222", {"start": v(-19.4, -3.5) * mm, "mid": v(-19.5, -3.4) * mm, "end": v(-19.6, -3.5) * mm});
            skArc(sketch, "E3223", {"start": v(-19.6, -3.5) * mm, "mid": v(-19.5, -3.6) * mm, "end": v(-19.4, -3.5) * mm});
            skArc(sketch, "E3224", {"start": v(-18.8, -2.3) * mm, "mid": v(-18.89, -2.09) * mm, "end": v(-19.1, -2) * mm});
            skArc(sketch, "E3225", {"start": v(-19.9, -2) * mm, "mid": v(-20.11, -2.09) * mm, "end": v(-20.2, -2.3) * mm});
            skLineSegment(sketch, "E3226", {"start": v(-19.1, -2) * mm, "end": v(-19.9, -2) * mm});
            skLineSegment(sketch, "E3227", {"start": v(-15.5, -5.5) * mm, "end": v(-14.5, -5.5) * mm});
            skLineSegment(sketch, "E3228", {"start": v(-14.5, -5.5) * mm, "end": v(-14.5, -6.5) * mm});
            skLineSegment(sketch, "E3229", {"start": v(-14.5, -6.5) * mm, "end": v(-15.5, -6.5) * mm});
            skLineSegment(sketch, "E3230", {"start": v(-15.5, -6.5) * mm, "end": v(-15.5, -5.5) * mm});
            skLineSegment(sketch, "E3231", {"start": v(-15.5, -7) * mm, "end": v(-14.5, -7) * mm});
            skLineSegment(sketch, "E3232", {"start": v(-14.5, -7) * mm, "end": v(-14.5, -8) * mm});
            skLineSegment(sketch, "E3233", {"start": v(-14.5, -8) * mm, "end": v(-15.5, -8) * mm});
            skLineSegment(sketch, "E3234", {"start": v(-15.5, -8) * mm, "end": v(-15.5, -7) * mm});
            skArc(sketch, "E3235", {"start": v(-15.4, -5.25) * mm, "mid": v(-15.61, -5.34) * mm, "end": v(-15.7, -5.55) * mm});
            skLineSegment(sketch, "E3236", {"start": v(-14.6, -5.25) * mm, "end": v(-15.4, -5.25) * mm});
            skArc(sketch, "E3237", {"start": v(-14.6, -5.25) * mm, "mid": v(-14.39, -5.34) * mm, "end": v(-14.3, -5.55) * mm});
            skLineSegment(sketch, "E3238", {"start": v(-15.7, -7.95) * mm, "end": v(-15.7, -5.55) * mm});
            skLineSegment(sketch, "E3239", {"start": v(-14.3, -5.55) * mm, "end": v(-14.3, -7.95) * mm});
            skArc(sketch, "E3240", {"start": v(-14.9, -6.75) * mm, "mid": v(-15, -6.65) * mm, "end": v(-15.1, -6.75) * mm});
            skArc(sketch, "E3241", {"start": v(-15.1, -6.75) * mm, "mid": v(-15, -6.85) * mm, "end": v(-14.9, -6.75) * mm});
            skArc(sketch, "E3242", {"start": v(-15.7, -7.95) * mm, "mid": v(-15.61, -8.16) * mm, "end": v(-15.4, -8.25) * mm});
            skArc(sketch, "E3243", {"start": v(-14.6, -8.25) * mm, "mid": v(-14.39, -8.16) * mm, "end": v(-14.3, -7.95) * mm});
            skLineSegment(sketch, "E3244", {"start": v(-15.4, -8.25) * mm, "end": v(-14.6, -8.25) * mm});
            skLineSegment(sketch, "E3245", {"start": v(-20, -15) * mm, "end": v(-19, -15) * mm});
            skLineSegment(sketch, "E3246", {"start": v(-19, -15) * mm, "end": v(-19, -16) * mm});
            skLineSegment(sketch, "E3247", {"start": v(-19, -16) * mm, "end": v(-20, -16) * mm});
            skLineSegment(sketch, "E3248", {"start": v(-20, -16) * mm, "end": v(-20, -15) * mm});
            skLineSegment(sketch, "E3249", {"start": v(-20, -16.5) * mm, "end": v(-19, -16.5) * mm});
            skLineSegment(sketch, "E3250", {"start": v(-19, -16.5) * mm, "end": v(-19, -17.5) * mm});
            skLineSegment(sketch, "E3251", {"start": v(-19, -17.5) * mm, "end": v(-20, -17.5) * mm});
            skLineSegment(sketch, "E3252", {"start": v(-20, -17.5) * mm, "end": v(-20, -16.5) * mm});
            skArc(sketch, "E3253", {"start": v(-19.9, -14.75) * mm, "mid": v(-20.11, -14.84) * mm, "end": v(-20.2, -15.05) * mm});
            skLineSegment(sketch, "E3254", {"start": v(-19.1, -14.75) * mm, "end": v(-19.9, -14.75) * mm});
            skArc(sketch, "E3255", {"start": v(-19.1, -14.75) * mm, "mid": v(-18.89, -14.84) * mm, "end": v(-18.8, -15.05) * mm});
            skLineSegment(sketch, "E3256", {"start": v(-20.2, -17.45) * mm, "end": v(-20.2, -15.05) * mm});
            skLineSegment(sketch, "E3257", {"start": v(-18.8, -15.05) * mm, "end": v(-18.8, -17.45) * mm});
            skArc(sketch, "E3258", {"start": v(-19.4, -16.25) * mm, "mid": v(-19.5, -16.15) * mm, "end": v(-19.6, -16.25) * mm});
            skArc(sketch, "E3259", {"start": v(-19.6, -16.25) * mm, "mid": v(-19.5, -16.35) * mm, "end": v(-19.4, -16.25) * mm});
            skArc(sketch, "E3260", {"start": v(-20.2, -17.45) * mm, "mid": v(-20.11, -17.66) * mm, "end": v(-19.9, -17.75) * mm});
            skArc(sketch, "E3261", {"start": v(-19.1, -17.75) * mm, "mid": v(-18.89, -17.66) * mm, "end": v(-18.8, -17.45) * mm});
            skLineSegment(sketch, "E3262", {"start": v(-19.9, -17.75) * mm, "end": v(-19.1, -17.75) * mm});
            skLineSegment(sketch, "E3263", {"start": v(-17.75, -32) * mm, "end": v(-17.75, -33) * mm});
            skLineSegment(sketch, "E3264", {"start": v(-17.75, -33) * mm, "end": v(-18.75, -33) * mm});
            skLineSegment(sketch, "E3265", {"start": v(-18.75, -33) * mm, "end": v(-18.75, -32) * mm});
            skLineSegment(sketch, "E3266", {"start": v(-18.75, -32) * mm, "end": v(-17.75, -32) * mm});
            skLineSegment(sketch, "E3267", {"start": v(-19.25, -32) * mm, "end": v(-19.25, -33) * mm});
            skLineSegment(sketch, "E3268", {"start": v(-19.25, -33) * mm, "end": v(-20.25, -33) * mm});
            skLineSegment(sketch, "E3269", {"start": v(-20.25, -33) * mm, "end": v(-20.25, -32) * mm});
            skLineSegment(sketch, "E3270", {"start": v(-20.25, -32) * mm, "end": v(-19.25, -32) * mm});
            skArc(sketch, "E3271", {"start": v(-17.5, -32.1) * mm, "mid": v(-17.59, -31.89) * mm, "end": v(-17.8, -31.8) * mm});
            skLineSegment(sketch, "E3272", {"start": v(-17.5, -32.9) * mm, "end": v(-17.5, -32.1) * mm});
            skArc(sketch, "E3273", {"start": v(-17.5, -32.9) * mm, "mid": v(-17.59, -33.11) * mm, "end": v(-17.8, -33.2) * mm});
            skLineSegment(sketch, "E3274", {"start": v(-20.2, -31.8) * mm, "end": v(-17.8, -31.8) * mm});
            skLineSegment(sketch, "E3275", {"start": v(-17.8, -33.2) * mm, "end": v(-20.2, -33.2) * mm});
            skArc(sketch, "E3276", {"start": v(-18.9, -32.5) * mm, "mid": v(-19, -32.4) * mm, "end": v(-19.1, -32.5) * mm});
            skArc(sketch, "E3277", {"start": v(-19.1, -32.5) * mm, "mid": v(-19, -32.6) * mm, "end": v(-18.9, -32.5) * mm});
            skArc(sketch, "E3278", {"start": v(-20.2, -31.8) * mm, "mid": v(-20.41, -31.89) * mm, "end": v(-20.5, -32.1) * mm});
            skArc(sketch, "E3279", {"start": v(-20.5, -32.9) * mm, "mid": v(-20.41, -33.11) * mm, "end": v(-20.2, -33.2) * mm});
            skLineSegment(sketch, "E3280", {"start": v(-20.5, -32.1) * mm, "end": v(-20.5, -32.9) * mm});
            skLineSegment(sketch, "E3281", {"start": v(-3.5, 15.25) * mm, "end": v(-4.5, 15.25) * mm});
            skLineSegment(sketch, "E3282", {"start": v(-4.5, 15.25) * mm, "end": v(-4.5, 16.25) * mm});
            skLineSegment(sketch, "E3283", {"start": v(-4.5, 16.25) * mm, "end": v(-3.5, 16.25) * mm});
            skLineSegment(sketch, "E3284", {"start": v(-3.5, 16.25) * mm, "end": v(-3.5, 15.25) * mm});
            skLineSegment(sketch, "E3285", {"start": v(-3.5, 16.75) * mm, "end": v(-4.5, 16.75) * mm});
            skLineSegment(sketch, "E3286", {"start": v(-4.5, 16.75) * mm, "end": v(-4.5, 17.75) * mm});
            skLineSegment(sketch, "E3287", {"start": v(-4.5, 17.75) * mm, "end": v(-3.5, 17.75) * mm});
            skLineSegment(sketch, "E3288", {"start": v(-3.5, 17.75) * mm, "end": v(-3.5, 16.75) * mm});
            skArc(sketch, "E3289", {"start": v(-3.6, 15) * mm, "mid": v(-3.39, 15.09) * mm, "end": v(-3.3, 15.3) * mm});
            skLineSegment(sketch, "E3290", {"start": v(-4.4, 15) * mm, "end": v(-3.6, 15) * mm});
            skArc(sketch, "E3291", {"start": v(-4.4, 15) * mm, "mid": v(-4.61, 15.09) * mm, "end": v(-4.7, 15.3) * mm});
            skLineSegment(sketch, "E3292", {"start": v(-3.3, 17.7) * mm, "end": v(-3.3, 15.3) * mm});
            skLineSegment(sketch, "E3293", {"start": v(-4.7, 15.3) * mm, "end": v(-4.7, 17.7) * mm});
            skArc(sketch, "E3294", {"start": v(-3.9, 16.5) * mm, "mid": v(-4, 16.6) * mm, "end": v(-4.1, 16.5) * mm});
            skArc(sketch, "E3295", {"start": v(-4.1, 16.5) * mm, "mid": v(-4, 16.4) * mm, "end": v(-3.9, 16.5) * mm});
            skArc(sketch, "E3296", {"start": v(-3.3, 17.7) * mm, "mid": v(-3.39, 17.91) * mm, "end": v(-3.6, 18) * mm});
            skArc(sketch, "E3297", {"start": v(-4.4, 18) * mm, "mid": v(-4.61, 17.91) * mm, "end": v(-4.7, 17.7) * mm});
            skLineSegment(sketch, "E3298", {"start": v(-3.6, 18) * mm, "end": v(-4.4, 18) * mm});
            skLineSegment(sketch, "E3299", {"start": v(-7.25, -41) * mm, "end": v(-7.25, -40) * mm});
            skLineSegment(sketch, "E3300", {"start": v(-7.25, -40) * mm, "end": v(-6.25, -40) * mm});
            skLineSegment(sketch, "E3301", {"start": v(-6.25, -40) * mm, "end": v(-6.25, -41) * mm});
            skLineSegment(sketch, "E3302", {"start": v(-6.25, -41) * mm, "end": v(-7.25, -41) * mm});
            skLineSegment(sketch, "E3303", {"start": v(-5.75, -41) * mm, "end": v(-5.75, -40) * mm});
            skLineSegment(sketch, "E3304", {"start": v(-5.75, -40) * mm, "end": v(-4.75, -40) * mm});
            skLineSegment(sketch, "E3305", {"start": v(-4.75, -40) * mm, "end": v(-4.75, -41) * mm});
            skLineSegment(sketch, "E3306", {"start": v(-4.75, -41) * mm, "end": v(-5.75, -41) * mm});
            skArc(sketch, "E3307", {"start": v(-7.5, -40.9) * mm, "mid": v(-7.41, -41.11) * mm, "end": v(-7.2, -41.2) * mm});
            skLineSegment(sketch, "E3308", {"start": v(-7.5, -40.1) * mm, "end": v(-7.5, -40.9) * mm});
            skArc(sketch, "E3309", {"start": v(-7.5, -40.1) * mm, "mid": v(-7.41, -39.89) * mm, "end": v(-7.2, -39.8) * mm});
            skLineSegment(sketch, "E3310", {"start": v(-4.8, -41.2) * mm, "end": v(-7.2, -41.2) * mm});
            skLineSegment(sketch, "E3311", {"start": v(-7.2, -39.8) * mm, "end": v(-4.8, -39.8) * mm});
            skArc(sketch, "E3312", {"start": v(-5.9, -40.5) * mm, "mid": v(-6, -40.4) * mm, "end": v(-6.1, -40.5) * mm});
            skArc(sketch, "E3313", {"start": v(-6.1, -40.5) * mm, "mid": v(-6, -40.6) * mm, "end": v(-5.9, -40.5) * mm});
            skArc(sketch, "E3314", {"start": v(-4.8, -41.2) * mm, "mid": v(-4.59, -41.11) * mm, "end": v(-4.5, -40.9) * mm});
            skArc(sketch, "E3315", {"start": v(-4.5, -40.1) * mm, "mid": v(-4.59, -39.89) * mm, "end": v(-4.8, -39.8) * mm});
            skLineSegment(sketch, "E3316", {"start": v(-4.5, -40.9) * mm, "end": v(-4.5, -40.1) * mm});
            skLineSegment(sketch, "E3317", {"start": v(11, -7.25) * mm, "end": v(12, -7.25) * mm});
            skLineSegment(sketch, "E3318", {"start": v(12, -7.25) * mm, "end": v(12, -8.25) * mm});
            skLineSegment(sketch, "E3319", {"start": v(12, -8.25) * mm, "end": v(11, -8.25) * mm});
            skLineSegment(sketch, "E3320", {"start": v(11, -8.25) * mm, "end": v(11, -7.25) * mm});
            skLineSegment(sketch, "E3321", {"start": v(11, -8.75) * mm, "end": v(12, -8.75) * mm});
            skLineSegment(sketch, "E3322", {"start": v(12, -8.75) * mm, "end": v(12, -9.75) * mm});
            skLineSegment(sketch, "E3323", {"start": v(12, -9.75) * mm, "end": v(11, -9.75) * mm});
            skLineSegment(sketch, "E3324", {"start": v(11, -9.75) * mm, "end": v(11, -8.75) * mm});
            skArc(sketch, "E3325", {"start": v(11.1, -7) * mm, "mid": v(10.89, -7.09) * mm, "end": v(10.8, -7.3) * mm});
            skLineSegment(sketch, "E3326", {"start": v(11.9, -7) * mm, "end": v(11.1, -7) * mm});
            skArc(sketch, "E3327", {"start": v(11.9, -7) * mm, "mid": v(12.11, -7.09) * mm, "end": v(12.2, -7.3) * mm});
            skLineSegment(sketch, "E3328", {"start": v(10.8, -9.7) * mm, "end": v(10.8, -7.3) * mm});
            skLineSegment(sketch, "E3329", {"start": v(12.2, -7.3) * mm, "end": v(12.2, -9.7) * mm});
            skArc(sketch, "E3330", {"start": v(11.6, -8.5) * mm, "mid": v(11.5, -8.4) * mm, "end": v(11.4, -8.5) * mm});
            skArc(sketch, "E3331", {"start": v(11.4, -8.5) * mm, "mid": v(11.5, -8.6) * mm, "end": v(11.6, -8.5) * mm});
            skArc(sketch, "E3332", {"start": v(10.8, -9.7) * mm, "mid": v(10.89, -9.91) * mm, "end": v(11.1, -10) * mm});
            skArc(sketch, "E3333", {"start": v(11.9, -10) * mm, "mid": v(12.11, -9.91) * mm, "end": v(12.2, -9.7) * mm});
            skLineSegment(sketch, "E3334", {"start": v(11.1, -10) * mm, "end": v(11.9, -10) * mm});
            skLineSegment(sketch, "E3335", {"start": v(10.25, -26.5) * mm, "end": v(10.25, -27.5) * mm});
            skLineSegment(sketch, "E3336", {"start": v(10.25, -27.5) * mm, "end": v(9.25, -27.5) * mm});
            skLineSegment(sketch, "E3337", {"start": v(9.25, -27.5) * mm, "end": v(9.25, -26.5) * mm});
            skLineSegment(sketch, "E3338", {"start": v(9.25, -26.5) * mm, "end": v(10.25, -26.5) * mm});
            skLineSegment(sketch, "E3339", {"start": v(8.75, -26.5) * mm, "end": v(8.75, -27.5) * mm});
            skLineSegment(sketch, "E3340", {"start": v(8.75, -27.5) * mm, "end": v(7.75, -27.5) * mm});
            skLineSegment(sketch, "E3341", {"start": v(7.75, -27.5) * mm, "end": v(7.75, -26.5) * mm});
            skLineSegment(sketch, "E3342", {"start": v(7.75, -26.5) * mm, "end": v(8.75, -26.5) * mm});
            skArc(sketch, "E3343", {"start": v(10.5, -26.6) * mm, "mid": v(10.41, -26.39) * mm, "end": v(10.2, -26.3) * mm});
            skLineSegment(sketch, "E3344", {"start": v(10.5, -27.4) * mm, "end": v(10.5, -26.6) * mm});
            skArc(sketch, "E3345", {"start": v(10.5, -27.4) * mm, "mid": v(10.41, -27.61) * mm, "end": v(10.2, -27.7) * mm});
            skLineSegment(sketch, "E3346", {"start": v(7.8, -26.3) * mm, "end": v(10.2, -26.3) * mm});
            skLineSegment(sketch, "E3347", {"start": v(10.2, -27.7) * mm, "end": v(7.8, -27.7) * mm});
            skArc(sketch, "E3348", {"start": v(9.1, -27) * mm, "mid": v(9, -26.9) * mm, "end": v(8.9, -27) * mm});
            skArc(sketch, "E3349", {"start": v(8.9, -27) * mm, "mid": v(9, -27.1) * mm, "end": v(9.1, -27) * mm});
            skArc(sketch, "E3350", {"start": v(7.8, -26.3) * mm, "mid": v(7.59, -26.39) * mm, "end": v(7.5, -26.6) * mm});
            skArc(sketch, "E3351", {"start": v(7.5, -27.4) * mm, "mid": v(7.59, -27.61) * mm, "end": v(7.8, -27.7) * mm});
            skLineSegment(sketch, "E3352", {"start": v(7.5, -26.6) * mm, "end": v(7.5, -27.4) * mm});
            skLineSegment(sketch, "E3353", {"start": v(3.5, 11.25) * mm, "end": v(2.5, 11.25) * mm});
            skLineSegment(sketch, "E3354", {"start": v(2.5, 11.25) * mm, "end": v(2.5, 12.25) * mm});
            skLineSegment(sketch, "E3355", {"start": v(2.5, 12.25) * mm, "end": v(3.5, 12.25) * mm});
            skLineSegment(sketch, "E3356", {"start": v(3.5, 12.25) * mm, "end": v(3.5, 11.25) * mm});
            skLineSegment(sketch, "E3357", {"start": v(3.5, 12.75) * mm, "end": v(2.5, 12.75) * mm});
            skLineSegment(sketch, "E3358", {"start": v(2.5, 12.75) * mm, "end": v(2.5, 13.75) * mm});
            skLineSegment(sketch, "E3359", {"start": v(2.5, 13.75) * mm, "end": v(3.5, 13.75) * mm});
            skLineSegment(sketch, "E3360", {"start": v(3.5, 13.75) * mm, "end": v(3.5, 12.75) * mm});
            skArc(sketch, "E3361", {"start": v(3.4, 11) * mm, "mid": v(3.61, 11.09) * mm, "end": v(3.7, 11.3) * mm});
            skLineSegment(sketch, "E3362", {"start": v(2.6, 11) * mm, "end": v(3.4, 11) * mm});
            skArc(sketch, "E3363", {"start": v(2.6, 11) * mm, "mid": v(2.39, 11.09) * mm, "end": v(2.3, 11.3) * mm});
            skLineSegment(sketch, "E3364", {"start": v(3.7, 13.7) * mm, "end": v(3.7, 11.3) * mm});
            skLineSegment(sketch, "E3365", {"start": v(2.3, 11.3) * mm, "end": v(2.3, 13.7) * mm});
            skArc(sketch, "E3366", {"start": v(3.1, 12.5) * mm, "mid": v(3, 12.6) * mm, "end": v(2.9, 12.5) * mm});
            skArc(sketch, "E3367", {"start": v(2.9, 12.5) * mm, "mid": v(3, 12.4) * mm, "end": v(3.1, 12.5) * mm});
            skArc(sketch, "E3368", {"start": v(3.7, 13.7) * mm, "mid": v(3.61, 13.91) * mm, "end": v(3.4, 14) * mm});
            skArc(sketch, "E3369", {"start": v(2.6, 14) * mm, "mid": v(2.39, 13.91) * mm, "end": v(2.3, 13.7) * mm});
            skLineSegment(sketch, "E3370", {"start": v(3.4, 14) * mm, "end": v(2.6, 14) * mm});
            skLineSegment(sketch, "E3371", {"start": v(6.5, 11.25) * mm, "end": v(5.5, 11.25) * mm});
            skLineSegment(sketch, "E3372", {"start": v(5.5, 11.25) * mm, "end": v(5.5, 12.25) * mm});
            skLineSegment(sketch, "E3373", {"start": v(5.5, 12.25) * mm, "end": v(6.5, 12.25) * mm});
            skLineSegment(sketch, "E3374", {"start": v(6.5, 12.25) * mm, "end": v(6.5, 11.25) * mm});
            skLineSegment(sketch, "E3375", {"start": v(6.5, 12.75) * mm, "end": v(5.5, 12.75) * mm});
            skLineSegment(sketch, "E3376", {"start": v(5.5, 12.75) * mm, "end": v(5.5, 13.75) * mm});
            skLineSegment(sketch, "E3377", {"start": v(5.5, 13.75) * mm, "end": v(6.5, 13.75) * mm});
            skLineSegment(sketch, "E3378", {"start": v(6.5, 13.75) * mm, "end": v(6.5, 12.75) * mm});
            skArc(sketch, "E3379", {"start": v(6.4, 11) * mm, "mid": v(6.61, 11.09) * mm, "end": v(6.7, 11.3) * mm});
            skLineSegment(sketch, "E3380", {"start": v(5.6, 11) * mm, "end": v(6.4, 11) * mm});
            skArc(sketch, "E3381", {"start": v(5.6, 11) * mm, "mid": v(5.39, 11.09) * mm, "end": v(5.3, 11.3) * mm});
            skLineSegment(sketch, "E3382", {"start": v(6.7, 13.7) * mm, "end": v(6.7, 11.3) * mm});
            skLineSegment(sketch, "E3383", {"start": v(5.3, 11.3) * mm, "end": v(5.3, 13.7) * mm});
            skArc(sketch, "E3384", {"start": v(6.1, 12.5) * mm, "mid": v(6, 12.6) * mm, "end": v(5.9, 12.5) * mm});
            skArc(sketch, "E3385", {"start": v(5.9, 12.5) * mm, "mid": v(6, 12.4) * mm, "end": v(6.1, 12.5) * mm});
            skArc(sketch, "E3386", {"start": v(6.7, 13.7) * mm, "mid": v(6.61, 13.91) * mm, "end": v(6.4, 14) * mm});
            skArc(sketch, "E3387", {"start": v(5.6, 14) * mm, "mid": v(5.39, 13.91) * mm, "end": v(5.3, 13.7) * mm});
            skLineSegment(sketch, "E3388", {"start": v(6.4, 14) * mm, "end": v(5.6, 14) * mm});
            skLineSegment(sketch, "E3389", {"start": v(-8.25, -22.25) * mm, "end": v(-9.25, -22.25) * mm});
            skLineSegment(sketch, "E3390", {"start": v(-9.25, -22.25) * mm, "end": v(-9.25, -21.25) * mm});
            skLineSegment(sketch, "E3391", {"start": v(-9.25, -21.25) * mm, "end": v(-8.25, -21.25) * mm});
            skLineSegment(sketch, "E3392", {"start": v(-8.25, -21.25) * mm, "end": v(-8.25, -22.25) * mm});
            skLineSegment(sketch, "E3393", {"start": v(-8.25, -20.75) * mm, "end": v(-9.25, -20.75) * mm});
            skLineSegment(sketch, "E3394", {"start": v(-9.25, -20.75) * mm, "end": v(-9.25, -19.75) * mm});
            skLineSegment(sketch, "E3395", {"start": v(-9.25, -19.75) * mm, "end": v(-8.25, -19.75) * mm});
            skLineSegment(sketch, "E3396", {"start": v(-8.25, -19.75) * mm, "end": v(-8.25, -20.75) * mm});
            skArc(sketch, "E3397", {"start": v(-8.35, -22.5) * mm, "mid": v(-8.14, -22.41) * mm, "end": v(-8.05, -22.2) * mm});
            skLineSegment(sketch, "E3398", {"start": v(-9.15, -22.5) * mm, "end": v(-8.35, -22.5) * mm});
            skArc(sketch, "E3399", {"start": v(-9.15, -22.5) * mm, "mid": v(-9.36, -22.41) * mm, "end": v(-9.45, -22.2) * mm});
            skLineSegment(sketch, "E3400", {"start": v(-8.05, -19.8) * mm, "end": v(-8.05, -22.2) * mm});
            skLineSegment(sketch, "E3401", {"start": v(-9.45, -22.2) * mm, "end": v(-9.45, -19.8) * mm});
            skArc(sketch, "E3402", {"start": v(-8.65, -21) * mm, "mid": v(-8.75, -20.9) * mm, "end": v(-8.85, -21) * mm});
            skArc(sketch, "E3403", {"start": v(-8.85, -21) * mm, "mid": v(-8.75, -21.1) * mm, "end": v(-8.65, -21) * mm});
            skArc(sketch, "E3404", {"start": v(-8.05, -19.8) * mm, "mid": v(-8.14, -19.59) * mm, "end": v(-8.35, -19.5) * mm});
            skArc(sketch, "E3405", {"start": v(-9.15, -19.5) * mm, "mid": v(-9.36, -19.59) * mm, "end": v(-9.45, -19.8) * mm});
            skLineSegment(sketch, "E3406", {"start": v(-8.35, -19.5) * mm, "end": v(-9.15, -19.5) * mm});
            skLineSegment(sketch, "E3407", {"start": v(18.5, -16.75) * mm, "end": v(19.5, -16.75) * mm});
            skLineSegment(sketch, "E3408", {"start": v(19.5, -16.75) * mm, "end": v(19.5, -17.75) * mm});
            skLineSegment(sketch, "E3409", {"start": v(19.5, -17.75) * mm, "end": v(18.5, -17.75) * mm});
            skLineSegment(sketch, "E3410", {"start": v(18.5, -17.75) * mm, "end": v(18.5, -16.75) * mm});
            skLineSegment(sketch, "E3411", {"start": v(18.5, -18.25) * mm, "end": v(19.5, -18.25) * mm});
            skLineSegment(sketch, "E3412", {"start": v(19.5, -18.25) * mm, "end": v(19.5, -19.25) * mm});
            skLineSegment(sketch, "E3413", {"start": v(19.5, -19.25) * mm, "end": v(18.5, -19.25) * mm});
            skLineSegment(sketch, "E3414", {"start": v(18.5, -19.25) * mm, "end": v(18.5, -18.25) * mm});
            skArc(sketch, "E3415", {"start": v(18.6, -16.5) * mm, "mid": v(18.39, -16.59) * mm, "end": v(18.3, -16.8) * mm});
            skLineSegment(sketch, "E3416", {"start": v(19.4, -16.5) * mm, "end": v(18.6, -16.5) * mm});
            skArc(sketch, "E3417", {"start": v(19.4, -16.5) * mm, "mid": v(19.61, -16.59) * mm, "end": v(19.7, -16.8) * mm});
            skLineSegment(sketch, "E3418", {"start": v(18.3, -19.2) * mm, "end": v(18.3, -16.8) * mm});
            skLineSegment(sketch, "E3419", {"start": v(19.7, -16.8) * mm, "end": v(19.7, -19.2) * mm});
            skArc(sketch, "E3420", {"start": v(19.1, -18) * mm, "mid": v(19, -17.9) * mm, "end": v(18.9, -18) * mm});
            skArc(sketch, "E3421", {"start": v(18.9, -18) * mm, "mid": v(19, -18.1) * mm, "end": v(19.1, -18) * mm});
            skArc(sketch, "E3422", {"start": v(18.3, -19.2) * mm, "mid": v(18.39, -19.41) * mm, "end": v(18.6, -19.5) * mm});
            skArc(sketch, "E3423", {"start": v(19.4, -19.5) * mm, "mid": v(19.61, -19.41) * mm, "end": v(19.7, -19.2) * mm});
            skLineSegment(sketch, "E3424", {"start": v(18.6, -19.5) * mm, "end": v(19.4, -19.5) * mm});
            skLineSegment(sketch, "E3425", {"start": v(10.25, -20.5) * mm, "end": v(10.25, -21.5) * mm});
            skLineSegment(sketch, "E3426", {"start": v(10.25, -21.5) * mm, "end": v(9.25, -21.5) * mm});
            skLineSegment(sketch, "E3427", {"start": v(9.25, -21.5) * mm, "end": v(9.25, -20.5) * mm});
            skLineSegment(sketch, "E3428", {"start": v(9.25, -20.5) * mm, "end": v(10.25, -20.5) * mm});
            skLineSegment(sketch, "E3429", {"start": v(8.75, -20.5) * mm, "end": v(8.75, -21.5) * mm});
            skLineSegment(sketch, "E3430", {"start": v(8.75, -21.5) * mm, "end": v(7.75, -21.5) * mm});
            skLineSegment(sketch, "E3431", {"start": v(7.75, -21.5) * mm, "end": v(7.75, -20.5) * mm});
            skLineSegment(sketch, "E3432", {"start": v(7.75, -20.5) * mm, "end": v(8.75, -20.5) * mm});
            skArc(sketch, "E3433", {"start": v(10.5, -20.6) * mm, "mid": v(10.41, -20.39) * mm, "end": v(10.2, -20.3) * mm});
            skLineSegment(sketch, "E3434", {"start": v(10.5, -21.4) * mm, "end": v(10.5, -20.6) * mm});
            skArc(sketch, "E3435", {"start": v(10.5, -21.4) * mm, "mid": v(10.41, -21.61) * mm, "end": v(10.2, -21.7) * mm});
            skLineSegment(sketch, "E3436", {"start": v(7.8, -20.3) * mm, "end": v(10.2, -20.3) * mm});
            skLineSegment(sketch, "E3437", {"start": v(10.2, -21.7) * mm, "end": v(7.8, -21.7) * mm});
            skArc(sketch, "E3438", {"start": v(9.1, -21) * mm, "mid": v(9, -20.9) * mm, "end": v(8.9, -21) * mm});
            skArc(sketch, "E3439", {"start": v(8.9, -21) * mm, "mid": v(9, -21.1) * mm, "end": v(9.1, -21) * mm});
            skArc(sketch, "E3440", {"start": v(7.8, -20.3) * mm, "mid": v(7.59, -20.39) * mm, "end": v(7.5, -20.6) * mm});
            skArc(sketch, "E3441", {"start": v(7.5, -21.4) * mm, "mid": v(7.59, -21.61) * mm, "end": v(7.8, -21.7) * mm});
            skLineSegment(sketch, "E3442", {"start": v(7.5, -20.6) * mm, "end": v(7.5, -21.4) * mm});
            skLineSegment(sketch, "E3443", {"start": v(-1, 10) * mm, "end": v(-1, 9) * mm});
            skLineSegment(sketch, "E3444", {"start": v(-1, 9) * mm, "end": v(-2, 9) * mm});
            skLineSegment(sketch, "E3445", {"start": v(-2, 9) * mm, "end": v(-2, 10) * mm});
            skLineSegment(sketch, "E3446", {"start": v(-2, 10) * mm, "end": v(-1, 10) * mm});
            skLineSegment(sketch, "E3447", {"start": v(-2.5, 10) * mm, "end": v(-2.5, 9) * mm});
            skLineSegment(sketch, "E3448", {"start": v(-2.5, 9) * mm, "end": v(-3.5, 9) * mm});
            skLineSegment(sketch, "E3449", {"start": v(-3.5, 9) * mm, "end": v(-3.5, 10) * mm});
            skLineSegment(sketch, "E3450", {"start": v(-3.5, 10) * mm, "end": v(-2.5, 10) * mm});
            skArc(sketch, "E3451", {"start": v(-0.75, 9.9) * mm, "mid": v(-0.84, 10.11) * mm, "end": v(-1.05, 10.2) * mm});
            skLineSegment(sketch, "E3452", {"start": v(-0.75, 9.1) * mm, "end": v(-0.75, 9.9) * mm});
            skArc(sketch, "E3453", {"start": v(-0.75, 9.1) * mm, "mid": v(-0.84, 8.89) * mm, "end": v(-1.05, 8.8) * mm});
            skLineSegment(sketch, "E3454", {"start": v(-3.45, 10.2) * mm, "end": v(-1.05, 10.2) * mm});
            skLineSegment(sketch, "E3455", {"start": v(-1.05, 8.8) * mm, "end": v(-3.45, 8.8) * mm});
            skArc(sketch, "E3456", {"start": v(-2.15, 9.5) * mm, "mid": v(-2.25, 9.6) * mm, "end": v(-2.35, 9.5) * mm});
            skArc(sketch, "E3457", {"start": v(-2.35, 9.5) * mm, "mid": v(-2.25, 9.4) * mm, "end": v(-2.15, 9.5) * mm});
            skArc(sketch, "E3458", {"start": v(-3.45, 10.2) * mm, "mid": v(-3.66, 10.11) * mm, "end": v(-3.75, 9.9) * mm});
            skArc(sketch, "E3459", {"start": v(-3.75, 9.1) * mm, "mid": v(-3.66, 8.89) * mm, "end": v(-3.45, 8.8) * mm});
            skLineSegment(sketch, "E3460", {"start": v(-3.75, 9.9) * mm, "end": v(-3.75, 9.1) * mm});
            skLineSegment(sketch, "E3461", {"start": v(-23.5, -14.25) * mm, "end": v(-22.5, -14.25) * mm});
            skLineSegment(sketch, "E3462", {"start": v(-22.5, -14.25) * mm, "end": v(-22.5, -15.25) * mm});
            skLineSegment(sketch, "E3463", {"start": v(-22.5, -15.25) * mm, "end": v(-23.5, -15.25) * mm});
            skLineSegment(sketch, "E3464", {"start": v(-23.5, -15.25) * mm, "end": v(-23.5, -14.25) * mm});
            skLineSegment(sketch, "E3465", {"start": v(-23.5, -15.75) * mm, "end": v(-22.5, -15.75) * mm});
            skLineSegment(sketch, "E3466", {"start": v(-22.5, -15.75) * mm, "end": v(-22.5, -16.75) * mm});
            skLineSegment(sketch, "E3467", {"start": v(-22.5, -16.75) * mm, "end": v(-23.5, -16.75) * mm});
            skLineSegment(sketch, "E3468", {"start": v(-23.5, -16.75) * mm, "end": v(-23.5, -15.75) * mm});
            skArc(sketch, "E3469", {"start": v(-23.4, -14) * mm, "mid": v(-23.61, -14.09) * mm, "end": v(-23.7, -14.3) * mm});
            skLineSegment(sketch, "E3470", {"start": v(-22.6, -14) * mm, "end": v(-23.4, -14) * mm});
            skArc(sketch, "E3471", {"start": v(-22.6, -14) * mm, "mid": v(-22.39, -14.09) * mm, "end": v(-22.3, -14.3) * mm});
            skLineSegment(sketch, "E3472", {"start": v(-23.7, -16.7) * mm, "end": v(-23.7, -14.3) * mm});
            skLineSegment(sketch, "E3473", {"start": v(-22.3, -14.3) * mm, "end": v(-22.3, -16.7) * mm});
            skArc(sketch, "E3474", {"start": v(-22.9, -15.5) * mm, "mid": v(-23, -15.4) * mm, "end": v(-23.1, -15.5) * mm});
            skArc(sketch, "E3475", {"start": v(-23.1, -15.5) * mm, "mid": v(-23, -15.6) * mm, "end": v(-22.9, -15.5) * mm});
            skArc(sketch, "E3476", {"start": v(-23.7, -16.7) * mm, "mid": v(-23.61, -16.91) * mm, "end": v(-23.4, -17) * mm});
            skArc(sketch, "E3477", {"start": v(-22.6, -17) * mm, "mid": v(-22.39, -16.91) * mm, "end": v(-22.3, -16.7) * mm});
            skLineSegment(sketch, "E3478", {"start": v(-23.4, -17) * mm, "end": v(-22.6, -17) * mm});
            skLineSegment(sketch, "E3479", {"start": v(2.5, 15.25) * mm, "end": v(1.5, 15.25) * mm});
            skLineSegment(sketch, "E3480", {"start": v(1.5, 15.25) * mm, "end": v(1.5, 16.25) * mm});
            skLineSegment(sketch, "E3481", {"start": v(1.5, 16.25) * mm, "end": v(2.5, 16.25) * mm});
            skLineSegment(sketch, "E3482", {"start": v(2.5, 16.25) * mm, "end": v(2.5, 15.25) * mm});
            skLineSegment(sketch, "E3483", {"start": v(2.5, 16.75) * mm, "end": v(1.5, 16.75) * mm});
            skLineSegment(sketch, "E3484", {"start": v(1.5, 16.75) * mm, "end": v(1.5, 17.75) * mm});
            skLineSegment(sketch, "E3485", {"start": v(1.5, 17.75) * mm, "end": v(2.5, 17.75) * mm});
            skLineSegment(sketch, "E3486", {"start": v(2.5, 17.75) * mm, "end": v(2.5, 16.75) * mm});
            skArc(sketch, "E3487", {"start": v(2.4, 15) * mm, "mid": v(2.61, 15.09) * mm, "end": v(2.7, 15.3) * mm});
            skLineSegment(sketch, "E3488", {"start": v(1.6, 15) * mm, "end": v(2.4, 15) * mm});
            skArc(sketch, "E3489", {"start": v(1.6, 15) * mm, "mid": v(1.39, 15.09) * mm, "end": v(1.3, 15.3) * mm});
            skLineSegment(sketch, "E3490", {"start": v(2.7, 17.7) * mm, "end": v(2.7, 15.3) * mm});
            skLineSegment(sketch, "E3491", {"start": v(1.3, 15.3) * mm, "end": v(1.3, 17.7) * mm});
            skArc(sketch, "E3492", {"start": v(2.1, 16.5) * mm, "mid": v(2, 16.6) * mm, "end": v(1.9, 16.5) * mm});
            skArc(sketch, "E3493", {"start": v(1.9, 16.5) * mm, "mid": v(2, 16.4) * mm, "end": v(2.1, 16.5) * mm});
            skArc(sketch, "E3494", {"start": v(2.7, 17.7) * mm, "mid": v(2.61, 17.91) * mm, "end": v(2.4, 18) * mm});
            skArc(sketch, "E3495", {"start": v(1.6, 18) * mm, "mid": v(1.39, 17.91) * mm, "end": v(1.3, 17.7) * mm});
            skLineSegment(sketch, "E3496", {"start": v(2.4, 18) * mm, "end": v(1.6, 18) * mm});
            skLineSegment(sketch, "E3497", {"start": v(-14.5, -24.75) * mm, "end": v(-15.5, -24.75) * mm});
            skLineSegment(sketch, "E3498", {"start": v(-15.5, -24.75) * mm, "end": v(-15.5, -23.75) * mm});
            skLineSegment(sketch, "E3499", {"start": v(-15.5, -23.75) * mm, "end": v(-14.5, -23.75) * mm});
            skLineSegment(sketch, "E3500", {"start": v(-14.5, -23.75) * mm, "end": v(-14.5, -24.75) * mm});
            skLineSegment(sketch, "E3501", {"start": v(-14.5, -23.25) * mm, "end": v(-15.5, -23.25) * mm});
            skLineSegment(sketch, "E3502", {"start": v(-15.5, -23.25) * mm, "end": v(-15.5, -22.25) * mm});
            skLineSegment(sketch, "E3503", {"start": v(-15.5, -22.25) * mm, "end": v(-14.5, -22.25) * mm});
            skLineSegment(sketch, "E3504", {"start": v(-14.5, -22.25) * mm, "end": v(-14.5, -23.25) * mm});
            skArc(sketch, "E3505", {"start": v(-14.6, -25) * mm, "mid": v(-14.39, -24.91) * mm, "end": v(-14.3, -24.7) * mm});
            skLineSegment(sketch, "E3506", {"start": v(-15.4, -25) * mm, "end": v(-14.6, -25) * mm});
            skArc(sketch, "E3507", {"start": v(-15.4, -25) * mm, "mid": v(-15.61, -24.91) * mm, "end": v(-15.7, -24.7) * mm});
            skLineSegment(sketch, "E3508", {"start": v(-14.3, -22.3) * mm, "end": v(-14.3, -24.7) * mm});
            skLineSegment(sketch, "E3509", {"start": v(-15.7, -24.7) * mm, "end": v(-15.7, -22.3) * mm});
            skArc(sketch, "E3510", {"start": v(-14.9, -23.5) * mm, "mid": v(-15, -23.4) * mm, "end": v(-15.1, -23.5) * mm});
            skArc(sketch, "E3511", {"start": v(-15.1, -23.5) * mm, "mid": v(-15, -23.6) * mm, "end": v(-14.9, -23.5) * mm});
            skArc(sketch, "E3512", {"start": v(-14.3, -22.3) * mm, "mid": v(-14.39, -22.09) * mm, "end": v(-14.6, -22) * mm});
            skArc(sketch, "E3513", {"start": v(-15.4, -22) * mm, "mid": v(-15.61, -22.09) * mm, "end": v(-15.7, -22.3) * mm});
            skLineSegment(sketch, "E3514", {"start": v(-14.6, -22) * mm, "end": v(-15.4, -22) * mm});
            skLineSegment(sketch, "E3515", {"start": v(10.25, -24.5) * mm, "end": v(10.25, -25.5) * mm});
            skLineSegment(sketch, "E3516", {"start": v(10.25, -25.5) * mm, "end": v(9.25, -25.5) * mm});
            skLineSegment(sketch, "E3517", {"start": v(9.25, -25.5) * mm, "end": v(9.25, -24.5) * mm});
            skLineSegment(sketch, "E3518", {"start": v(9.25, -24.5) * mm, "end": v(10.25, -24.5) * mm});
            skLineSegment(sketch, "E3519", {"start": v(8.75, -24.5) * mm, "end": v(8.75, -25.5) * mm});
            skLineSegment(sketch, "E3520", {"start": v(8.75, -25.5) * mm, "end": v(7.75, -25.5) * mm});
            skLineSegment(sketch, "E3521", {"start": v(7.75, -25.5) * mm, "end": v(7.75, -24.5) * mm});
            skLineSegment(sketch, "E3522", {"start": v(7.75, -24.5) * mm, "end": v(8.75, -24.5) * mm});
            skArc(sketch, "E3523", {"start": v(10.5, -24.6) * mm, "mid": v(10.41, -24.39) * mm, "end": v(10.2, -24.3) * mm});
            skLineSegment(sketch, "E3524", {"start": v(10.5, -25.4) * mm, "end": v(10.5, -24.6) * mm});
            skArc(sketch, "E3525", {"start": v(10.5, -25.4) * mm, "mid": v(10.41, -25.61) * mm, "end": v(10.2, -25.7) * mm});
            skLineSegment(sketch, "E3526", {"start": v(7.8, -24.3) * mm, "end": v(10.2, -24.3) * mm});
            skLineSegment(sketch, "E3527", {"start": v(10.2, -25.7) * mm, "end": v(7.8, -25.7) * mm});
            skArc(sketch, "E3528", {"start": v(9.1, -25) * mm, "mid": v(9, -24.9) * mm, "end": v(8.9, -25) * mm});
            skArc(sketch, "E3529", {"start": v(8.9, -25) * mm, "mid": v(9, -25.1) * mm, "end": v(9.1, -25) * mm});
            skArc(sketch, "E3530", {"start": v(7.8, -24.3) * mm, "mid": v(7.59, -24.39) * mm, "end": v(7.5, -24.6) * mm});
            skArc(sketch, "E3531", {"start": v(7.5, -25.4) * mm, "mid": v(7.59, -25.61) * mm, "end": v(7.8, -25.7) * mm});
            skLineSegment(sketch, "E3532", {"start": v(7.5, -24.6) * mm, "end": v(7.5, -25.4) * mm});
            skLineSegment(sketch, "E3533", {"start": v(-22.5, -24.25) * mm, "end": v(-23.5, -24.25) * mm});
            skLineSegment(sketch, "E3534", {"start": v(-23.5, -24.25) * mm, "end": v(-23.5, -23.25) * mm});
            skLineSegment(sketch, "E3535", {"start": v(-23.5, -23.25) * mm, "end": v(-22.5, -23.25) * mm});
            skLineSegment(sketch, "E3536", {"start": v(-22.5, -23.25) * mm, "end": v(-22.5, -24.25) * mm});
            skLineSegment(sketch, "E3537", {"start": v(-22.5, -22.75) * mm, "end": v(-23.5, -22.75) * mm});
            skLineSegment(sketch, "E3538", {"start": v(-23.5, -22.75) * mm, "end": v(-23.5, -21.75) * mm});
            skLineSegment(sketch, "E3539", {"start": v(-23.5, -21.75) * mm, "end": v(-22.5, -21.75) * mm});
            skLineSegment(sketch, "E3540", {"start": v(-22.5, -21.75) * mm, "end": v(-22.5, -22.75) * mm});
            skArc(sketch, "E3541", {"start": v(-22.6, -24.5) * mm, "mid": v(-22.39, -24.41) * mm, "end": v(-22.3, -24.2) * mm});
            skLineSegment(sketch, "E3542", {"start": v(-23.4, -24.5) * mm, "end": v(-22.6, -24.5) * mm});
            skArc(sketch, "E3543", {"start": v(-23.4, -24.5) * mm, "mid": v(-23.61, -24.41) * mm, "end": v(-23.7, -24.2) * mm});
            skLineSegment(sketch, "E3544", {"start": v(-22.3, -21.8) * mm, "end": v(-22.3, -24.2) * mm});
            skLineSegment(sketch, "E3545", {"start": v(-23.7, -24.2) * mm, "end": v(-23.7, -21.8) * mm});
            skArc(sketch, "E3546", {"start": v(-22.9, -23) * mm, "mid": v(-23, -22.9) * mm, "end": v(-23.1, -23) * mm});
            skArc(sketch, "E3547", {"start": v(-23.1, -23) * mm, "mid": v(-23, -23.1) * mm, "end": v(-22.9, -23) * mm});
            skArc(sketch, "E3548", {"start": v(-22.3, -21.8) * mm, "mid": v(-22.39, -21.59) * mm, "end": v(-22.6, -21.5) * mm});
            skArc(sketch, "E3549", {"start": v(-23.4, -21.5) * mm, "mid": v(-23.61, -21.59) * mm, "end": v(-23.7, -21.8) * mm});
            skLineSegment(sketch, "E3550", {"start": v(-22.6, -21.5) * mm, "end": v(-23.4, -21.5) * mm});
            skLineSegment(sketch, "E3551", {"start": v(-3.5, 8.25) * mm, "end": v(-2.5, 8.25) * mm});
            skLineSegment(sketch, "E3552", {"start": v(-2.5, 8.25) * mm, "end": v(-2.5, 7.25) * mm});
            skLineSegment(sketch, "E3553", {"start": v(-2.5, 7.25) * mm, "end": v(-3.5, 7.25) * mm});
            skLineSegment(sketch, "E3554", {"start": v(-3.5, 7.25) * mm, "end": v(-3.5, 8.25) * mm});
            skLineSegment(sketch, "E3555", {"start": v(-3.5, 6.75) * mm, "end": v(-2.5, 6.75) * mm});
            skLineSegment(sketch, "E3556", {"start": v(-2.5, 6.75) * mm, "end": v(-2.5, 5.75) * mm});
            skLineSegment(sketch, "E3557", {"start": v(-2.5, 5.75) * mm, "end": v(-3.5, 5.75) * mm});
            skLineSegment(sketch, "E3558", {"start": v(-3.5, 5.75) * mm, "end": v(-3.5, 6.75) * mm});
            skArc(sketch, "E3559", {"start": v(-3.4, 8.5) * mm, "mid": v(-3.61, 8.41) * mm, "end": v(-3.7, 8.2) * mm});
            skLineSegment(sketch, "E3560", {"start": v(-2.6, 8.5) * mm, "end": v(-3.4, 8.5) * mm});
            skArc(sketch, "E3561", {"start": v(-2.6, 8.5) * mm, "mid": v(-2.39, 8.41) * mm, "end": v(-2.3, 8.2) * mm});
            skLineSegment(sketch, "E3562", {"start": v(-3.7, 5.8) * mm, "end": v(-3.7, 8.2) * mm});
            skLineSegment(sketch, "E3563", {"start": v(-2.3, 8.2) * mm, "end": v(-2.3, 5.8) * mm});
            skArc(sketch, "E3564", {"start": v(-2.9, 7) * mm, "mid": v(-3, 7.1) * mm, "end": v(-3.1, 7) * mm});
            skArc(sketch, "E3565", {"start": v(-3.1, 7) * mm, "mid": v(-3, 6.9) * mm, "end": v(-2.9, 7) * mm});
            skArc(sketch, "E3566", {"start": v(-3.7, 5.8) * mm, "mid": v(-3.61, 5.59) * mm, "end": v(-3.4, 5.5) * mm});
            skArc(sketch, "E3567", {"start": v(-2.6, 5.5) * mm, "mid": v(-2.39, 5.59) * mm, "end": v(-2.3, 5.8) * mm});
            skLineSegment(sketch, "E3568", {"start": v(-3.4, 5.5) * mm, "end": v(-2.6, 5.5) * mm});
            skLineSegment(sketch, "E3569", {"start": v(-2.5, -1.25) * mm, "end": v(-3.5, -1.25) * mm});
            skLineSegment(sketch, "E3570", {"start": v(-3.5, -1.25) * mm, "end": v(-3.5, -0.25) * mm});
            skLineSegment(sketch, "E3571", {"start": v(-3.5, -0.25) * mm, "end": v(-2.5, -0.25) * mm});
            skLineSegment(sketch, "E3572", {"start": v(-2.5, -0.25) * mm, "end": v(-2.5, -1.25) * mm});
            skLineSegment(sketch, "E3573", {"start": v(-2.5, 0.25) * mm, "end": v(-3.5, 0.25) * mm});
            skLineSegment(sketch, "E3574", {"start": v(-3.5, 0.25) * mm, "end": v(-3.5, 1.25) * mm});
            skLineSegment(sketch, "E3575", {"start": v(-3.5, 1.25) * mm, "end": v(-2.5, 1.25) * mm});
            skLineSegment(sketch, "E3576", {"start": v(-2.5, 1.25) * mm, "end": v(-2.5, 0.25) * mm});
            skArc(sketch, "E3577", {"start": v(-2.6, -1.5) * mm, "mid": v(-2.39, -1.41) * mm, "end": v(-2.3, -1.2) * mm});
            skLineSegment(sketch, "E3578", {"start": v(-3.4, -1.5) * mm, "end": v(-2.6, -1.5) * mm});
            skArc(sketch, "E3579", {"start": v(-3.4, -1.5) * mm, "mid": v(-3.61, -1.41) * mm, "end": v(-3.7, -1.2) * mm});
            skLineSegment(sketch, "E3580", {"start": v(-2.3, 1.2) * mm, "end": v(-2.3, -1.2) * mm});
            skLineSegment(sketch, "E3581", {"start": v(-3.7, -1.2) * mm, "end": v(-3.7, 1.2) * mm});
            skArc(sketch, "E3582", {"start": v(-2.9, 0) * mm, "mid": v(-3, 0.1) * mm, "end": v(-3.1, 0) * mm});
            skArc(sketch, "E3583", {"start": v(-3.1, 0) * mm, "mid": v(-3, -0.1) * mm, "end": v(-2.9, 0) * mm});
            skArc(sketch, "E3584", {"start": v(-2.3, 1.2) * mm, "mid": v(-2.39, 1.41) * mm, "end": v(-2.6, 1.5) * mm});
            skArc(sketch, "E3585", {"start": v(-3.4, 1.5) * mm, "mid": v(-3.61, 1.41) * mm, "end": v(-3.7, 1.2) * mm});
            skLineSegment(sketch, "E3586", {"start": v(-2.6, 1.5) * mm, "end": v(-3.4, 1.5) * mm});
            skLineSegment(sketch, "E3587", {"start": v(-10.25, -32) * mm, "end": v(-10.25, -33) * mm});
            skLineSegment(sketch, "E3588", {"start": v(-10.25, -33) * mm, "end": v(-11.25, -33) * mm});
            skLineSegment(sketch, "E3589", {"start": v(-11.25, -33) * mm, "end": v(-11.25, -32) * mm});
            skLineSegment(sketch, "E3590", {"start": v(-11.25, -32) * mm, "end": v(-10.25, -32) * mm});
            skLineSegment(sketch, "E3591", {"start": v(-11.75, -32) * mm, "end": v(-11.75, -33) * mm});
            skLineSegment(sketch, "E3592", {"start": v(-11.75, -33) * mm, "end": v(-12.75, -33) * mm});
            skLineSegment(sketch, "E3593", {"start": v(-12.75, -33) * mm, "end": v(-12.75, -32) * mm});
            skLineSegment(sketch, "E3594", {"start": v(-12.75, -32) * mm, "end": v(-11.75, -32) * mm});
            skArc(sketch, "E3595", {"start": v(-10, -32.1) * mm, "mid": v(-10.09, -31.89) * mm, "end": v(-10.3, -31.8) * mm});
            skLineSegment(sketch, "E3596", {"start": v(-10, -32.9) * mm, "end": v(-10, -32.1) * mm});
            skArc(sketch, "E3597", {"start": v(-10, -32.9) * mm, "mid": v(-10.09, -33.11) * mm, "end": v(-10.3, -33.2) * mm});
            skLineSegment(sketch, "E3598", {"start": v(-12.7, -31.8) * mm, "end": v(-10.3, -31.8) * mm});
            skLineSegment(sketch, "E3599", {"start": v(-10.3, -33.2) * mm, "end": v(-12.7, -33.2) * mm});
            skArc(sketch, "E3600", {"start": v(-11.4, -32.5) * mm, "mid": v(-11.5, -32.4) * mm, "end": v(-11.6, -32.5) * mm});
            skArc(sketch, "E3601", {"start": v(-11.6, -32.5) * mm, "mid": v(-11.5, -32.6) * mm, "end": v(-11.4, -32.5) * mm});
            skArc(sketch, "E3602", {"start": v(-12.7, -31.8) * mm, "mid": v(-12.91, -31.89) * mm, "end": v(-13, -32.1) * mm});
            skArc(sketch, "E3603", {"start": v(-13, -32.9) * mm, "mid": v(-12.91, -33.11) * mm, "end": v(-12.7, -33.2) * mm});
            skLineSegment(sketch, "E3604", {"start": v(-13, -32.1) * mm, "end": v(-13, -32.9) * mm});
            skLineSegment(sketch, "E3605", {"start": v(3.25, -7.25) * mm, "end": v(4.25, -7.25) * mm});
            skLineSegment(sketch, "E3606", {"start": v(4.25, -7.25) * mm, "end": v(4.25, -8.25) * mm});
            skLineSegment(sketch, "E3607", {"start": v(4.25, -8.25) * mm, "end": v(3.25, -8.25) * mm});
            skLineSegment(sketch, "E3608", {"start": v(3.25, -8.25) * mm, "end": v(3.25, -7.25) * mm});
            skLineSegment(sketch, "E3609", {"start": v(3.25, -8.75) * mm, "end": v(4.25, -8.75) * mm});
            skLineSegment(sketch, "E3610", {"start": v(4.25, -8.75) * mm, "end": v(4.25, -9.75) * mm});
            skLineSegment(sketch, "E3611", {"start": v(4.25, -9.75) * mm, "end": v(3.25, -9.75) * mm});
            skLineSegment(sketch, "E3612", {"start": v(3.25, -9.75) * mm, "end": v(3.25, -8.75) * mm});
            skArc(sketch, "E3613", {"start": v(3.35, -7) * mm, "mid": v(3.14, -7.09) * mm, "end": v(3.05, -7.3) * mm});
            skLineSegment(sketch, "E3614", {"start": v(4.15, -7) * mm, "end": v(3.35, -7) * mm});
            skArc(sketch, "E3615", {"start": v(4.15, -7) * mm, "mid": v(4.36, -7.09) * mm, "end": v(4.45, -7.3) * mm});
            skLineSegment(sketch, "E3616", {"start": v(3.05, -9.7) * mm, "end": v(3.05, -7.3) * mm});
            skLineSegment(sketch, "E3617", {"start": v(4.45, -7.3) * mm, "end": v(4.45, -9.7) * mm});
            skArc(sketch, "E3618", {"start": v(3.85, -8.5) * mm, "mid": v(3.75, -8.4) * mm, "end": v(3.65, -8.5) * mm});
            skArc(sketch, "E3619", {"start": v(3.65, -8.5) * mm, "mid": v(3.75, -8.6) * mm, "end": v(3.85, -8.5) * mm});
            skArc(sketch, "E3620", {"start": v(3.05, -9.7) * mm, "mid": v(3.14, -9.91) * mm, "end": v(3.35, -10) * mm});
            skArc(sketch, "E3621", {"start": v(4.15, -10) * mm, "mid": v(4.36, -9.91) * mm, "end": v(4.45, -9.7) * mm});
            skLineSegment(sketch, "E3622", {"start": v(3.35, -10) * mm, "end": v(4.15, -10) * mm});
            skLineSegment(sketch, "E3623", {"start": v(13, -7.25) * mm, "end": v(14, -7.25) * mm});
            skLineSegment(sketch, "E3624", {"start": v(14, -7.25) * mm, "end": v(14, -8.25) * mm});
            skLineSegment(sketch, "E3625", {"start": v(14, -8.25) * mm, "end": v(13, -8.25) * mm});
            skLineSegment(sketch, "E3626", {"start": v(13, -8.25) * mm, "end": v(13, -7.25) * mm});
            skLineSegment(sketch, "E3627", {"start": v(13, -8.75) * mm, "end": v(14, -8.75) * mm});
            skLineSegment(sketch, "E3628", {"start": v(14, -8.75) * mm, "end": v(14, -9.75) * mm});
            skLineSegment(sketch, "E3629", {"start": v(14, -9.75) * mm, "end": v(13, -9.75) * mm});
            skLineSegment(sketch, "E3630", {"start": v(13, -9.75) * mm, "end": v(13, -8.75) * mm});
            skArc(sketch, "E3631", {"start": v(13.1, -7) * mm, "mid": v(12.89, -7.09) * mm, "end": v(12.8, -7.3) * mm});
            skLineSegment(sketch, "E3632", {"start": v(13.9, -7) * mm, "end": v(13.1, -7) * mm});
            skArc(sketch, "E3633", {"start": v(13.9, -7) * mm, "mid": v(14.11, -7.09) * mm, "end": v(14.2, -7.3) * mm});
            skLineSegment(sketch, "E3634", {"start": v(12.8, -9.7) * mm, "end": v(12.8, -7.3) * mm});
            skLineSegment(sketch, "E3635", {"start": v(14.2, -7.3) * mm, "end": v(14.2, -9.7) * mm});
            skArc(sketch, "E3636", {"start": v(13.6, -8.5) * mm, "mid": v(13.5, -8.4) * mm, "end": v(13.4, -8.5) * mm});
            skArc(sketch, "E3637", {"start": v(13.4, -8.5) * mm, "mid": v(13.5, -8.6) * mm, "end": v(13.6, -8.5) * mm});
            skArc(sketch, "E3638", {"start": v(12.8, -9.7) * mm, "mid": v(12.89, -9.91) * mm, "end": v(13.1, -10) * mm});
            skArc(sketch, "E3639", {"start": v(13.9, -10) * mm, "mid": v(14.11, -9.91) * mm, "end": v(14.2, -9.7) * mm});
            skLineSegment(sketch, "E3640", {"start": v(13.1, -10) * mm, "end": v(13.9, -10) * mm});
            skLineSegment(sketch, "E3641", {"start": v(-1.5, -5.75) * mm, "end": v(-0.5, -5.75) * mm});
            skLineSegment(sketch, "E3642", {"start": v(-0.5, -5.75) * mm, "end": v(-0.5, -6.75) * mm});
            skLineSegment(sketch, "E3643", {"start": v(-0.5, -6.75) * mm, "end": v(-1.5, -6.75) * mm});
            skLineSegment(sketch, "E3644", {"start": v(-1.5, -6.75) * mm, "end": v(-1.5, -5.75) * mm});
            skLineSegment(sketch, "E3645", {"start": v(-1.5, -7.25) * mm, "end": v(-0.5, -7.25) * mm});
            skLineSegment(sketch, "E3646", {"start": v(-0.5, -7.25) * mm, "end": v(-0.5, -8.25) * mm});
            skLineSegment(sketch, "E3647", {"start": v(-0.5, -8.25) * mm, "end": v(-1.5, -8.25) * mm});
            skLineSegment(sketch, "E3648", {"start": v(-1.5, -8.25) * mm, "end": v(-1.5, -7.25) * mm});
            skArc(sketch, "E3649", {"start": v(-1.4, -5.5) * mm, "mid": v(-1.61, -5.59) * mm, "end": v(-1.7, -5.8) * mm});
            skLineSegment(sketch, "E3650", {"start": v(-0.6, -5.5) * mm, "end": v(-1.4, -5.5) * mm});
            skArc(sketch, "E3651", {"start": v(-0.6, -5.5) * mm, "mid": v(-0.39, -5.59) * mm, "end": v(-0.3, -5.8) * mm});
            skLineSegment(sketch, "E3652", {"start": v(-1.7, -8.2) * mm, "end": v(-1.7, -5.8) * mm});
            skLineSegment(sketch, "E3653", {"start": v(-0.3, -5.8) * mm, "end": v(-0.3, -8.2) * mm});
            skArc(sketch, "E3654", {"start": v(-0.9, -7) * mm, "mid": v(-1, -6.9) * mm, "end": v(-1.1, -7) * mm});
            skArc(sketch, "E3655", {"start": v(-1.1, -7) * mm, "mid": v(-1, -7.1) * mm, "end": v(-0.9, -7) * mm});
            skArc(sketch, "E3656", {"start": v(-1.7, -8.2) * mm, "mid": v(-1.61, -8.41) * mm, "end": v(-1.4, -8.5) * mm});
            skArc(sketch, "E3657", {"start": v(-0.6, -8.5) * mm, "mid": v(-0.39, -8.41) * mm, "end": v(-0.3, -8.2) * mm});
            skLineSegment(sketch, "E3658", {"start": v(-1.4, -8.5) * mm, "end": v(-0.6, -8.5) * mm});
            skLineSegment(sketch, "E3659", {"start": v(16, 6.75) * mm, "end": v(17, 6.75) * mm});
            skLineSegment(sketch, "E3660", {"start": v(17, 6.75) * mm, "end": v(17, 5.75) * mm});
            skLineSegment(sketch, "E3661", {"start": v(17, 5.75) * mm, "end": v(16, 5.75) * mm});
            skLineSegment(sketch, "E3662", {"start": v(16, 5.75) * mm, "end": v(16, 6.75) * mm});
            skLineSegment(sketch, "E3663", {"start": v(16, 5.25) * mm, "end": v(17, 5.25) * mm});
            skLineSegment(sketch, "E3664", {"start": v(17, 5.25) * mm, "end": v(17, 4.25) * mm});
            skLineSegment(sketch, "E3665", {"start": v(17, 4.25) * mm, "end": v(16, 4.25) * mm});
            skLineSegment(sketch, "E3666", {"start": v(16, 4.25) * mm, "end": v(16, 5.25) * mm});
            skArc(sketch, "E3667", {"start": v(16.1, 7) * mm, "mid": v(15.89, 6.91) * mm, "end": v(15.8, 6.7) * mm});
            skLineSegment(sketch, "E3668", {"start": v(16.9, 7) * mm, "end": v(16.1, 7) * mm});
            skArc(sketch, "E3669", {"start": v(16.9, 7) * mm, "mid": v(17.11, 6.91) * mm, "end": v(17.2, 6.7) * mm});
            skLineSegment(sketch, "E3670", {"start": v(15.8, 4.3) * mm, "end": v(15.8, 6.7) * mm});
            skLineSegment(sketch, "E3671", {"start": v(17.2, 6.7) * mm, "end": v(17.2, 4.3) * mm});
            skArc(sketch, "E3672", {"start": v(16.6, 5.5) * mm, "mid": v(16.5, 5.6) * mm, "end": v(16.4, 5.5) * mm});
            skArc(sketch, "E3673", {"start": v(16.4, 5.5) * mm, "mid": v(16.5, 5.4) * mm, "end": v(16.6, 5.5) * mm});
            skArc(sketch, "E3674", {"start": v(15.8, 4.3) * mm, "mid": v(15.89, 4.09) * mm, "end": v(16.1, 4) * mm});
            skArc(sketch, "E3675", {"start": v(16.9, 4) * mm, "mid": v(17.11, 4.09) * mm, "end": v(17.2, 4.3) * mm});
            skLineSegment(sketch, "E3676", {"start": v(16.1, 4) * mm, "end": v(16.9, 4) * mm});
            skLineSegment(sketch, "E3677", {"start": v(7.75, -23.5) * mm, "end": v(7.75, -22.5) * mm});
            skLineSegment(sketch, "E3678", {"start": v(7.75, -22.5) * mm, "end": v(8.75, -22.5) * mm});
            skLineSegment(sketch, "E3679", {"start": v(8.75, -22.5) * mm, "end": v(8.75, -23.5) * mm});
            skLineSegment(sketch, "E3680", {"start": v(8.75, -23.5) * mm, "end": v(7.75, -23.5) * mm});
            skLineSegment(sketch, "E3681", {"start": v(9.25, -23.5) * mm, "end": v(9.25, -22.5) * mm});
            skLineSegment(sketch, "E3682", {"start": v(9.25, -22.5) * mm, "end": v(10.25, -22.5) * mm});
            skLineSegment(sketch, "E3683", {"start": v(10.25, -22.5) * mm, "end": v(10.25, -23.5) * mm});
            skLineSegment(sketch, "E3684", {"start": v(10.25, -23.5) * mm, "end": v(9.25, -23.5) * mm});
            skArc(sketch, "E3685", {"start": v(7.5, -23.4) * mm, "mid": v(7.59, -23.61) * mm, "end": v(7.8, -23.7) * mm});
            skLineSegment(sketch, "E3686", {"start": v(7.5, -22.6) * mm, "end": v(7.5, -23.4) * mm});
            skArc(sketch, "E3687", {"start": v(7.5, -22.6) * mm, "mid": v(7.59, -22.39) * mm, "end": v(7.8, -22.3) * mm});
            skLineSegment(sketch, "E3688", {"start": v(10.2, -23.7) * mm, "end": v(7.8, -23.7) * mm});
            skLineSegment(sketch, "E3689", {"start": v(7.8, -22.3) * mm, "end": v(10.2, -22.3) * mm});
            skArc(sketch, "E3690", {"start": v(9.1, -23) * mm, "mid": v(9, -22.9) * mm, "end": v(8.9, -23) * mm});
            skArc(sketch, "E3691", {"start": v(8.9, -23) * mm, "mid": v(9, -23.1) * mm, "end": v(9.1, -23) * mm});
            skArc(sketch, "E3692", {"start": v(10.2, -23.7) * mm, "mid": v(10.41, -23.61) * mm, "end": v(10.5, -23.4) * mm});
            skArc(sketch, "E3693", {"start": v(10.5, -22.6) * mm, "mid": v(10.41, -22.39) * mm, "end": v(10.2, -22.3) * mm});
            skLineSegment(sketch, "E3694", {"start": v(10.5, -23.4) * mm, "end": v(10.5, -22.6) * mm});
            skLineSegment(sketch, "E3695", {"start": v(22.22, -10.07) * mm, "end": v(23.5, -10.07) * mm});
            skLineSegment(sketch, "E3696", {"start": v(23.5, -10.07) * mm, "end": v(23.5, -10.83) * mm});
            skLineSegment(sketch, "E3697", {"start": v(23.5, -10.83) * mm, "end": v(22.22, -10.83) * mm});
            skLineSegment(sketch, "E3698", {"start": v(22.22, -10.83) * mm, "end": v(22.22, -10.07) * mm});
            skLineSegment(sketch, "E3699", {"start": v(22.22, -8.17) * mm, "end": v(23.5, -8.17) * mm});
            skLineSegment(sketch, "E3700", {"start": v(23.5, -8.17) * mm, "end": v(23.5, -8.93) * mm});
            skLineSegment(sketch, "E3701", {"start": v(23.5, -8.93) * mm, "end": v(22.22, -8.93) * mm});
            skLineSegment(sketch, "E3702", {"start": v(22.22, -8.93) * mm, "end": v(22.22, -8.17) * mm});
            skLineSegment(sketch, "E3703", {"start": v(24.5, -9.12) * mm, "end": v(25.78, -9.12) * mm});
            skLineSegment(sketch, "E3704", {"start": v(25.78, -9.12) * mm, "end": v(25.78, -9.88) * mm});
            skLineSegment(sketch, "E3705", {"start": v(25.78, -9.88) * mm, "end": v(24.5, -9.88) * mm});
            skLineSegment(sketch, "E3706", {"start": v(24.5, -9.88) * mm, "end": v(24.5, -9.12) * mm});
            skArc(sketch, "E3707", {"start": v(24.25, -9.5) * mm, "mid": v(24, -9.25) * mm, "end": v(23.75, -9.5) * mm});
            skArc(sketch, "E3708", {"start": v(23.75, -9.5) * mm, "mid": v(24, -9.75) * mm, "end": v(24.25, -9.5) * mm});
            skLineSegment(sketch, "E3709", {"start": v(26, -7.88) * mm, "end": v(26, -11.12) * mm});
            skLineSegment(sketch, "E3710", {"start": v(26, -11.12) * mm, "end": v(22, -11.12) * mm});
            skLineSegment(sketch, "E3711", {"start": v(22, -11.12) * mm, "end": v(22, -8.12) * mm});
            skLineSegment(sketch, "E3712", {"start": v(22, -8.12) * mm, "end": v(22.25, -7.88) * mm});
            skLineSegment(sketch, "E3713", {"start": v(22.25, -7.88) * mm, "end": v(26, -7.88) * mm});
            skLineSegment(sketch, "E3714", {"start": v(22.22, -4.07) * mm, "end": v(23.5, -4.07) * mm});
            skLineSegment(sketch, "E3715", {"start": v(23.5, -4.07) * mm, "end": v(23.5, -4.83) * mm});
            skLineSegment(sketch, "E3716", {"start": v(23.5, -4.83) * mm, "end": v(22.22, -4.83) * mm});
            skLineSegment(sketch, "E3717", {"start": v(22.22, -4.83) * mm, "end": v(22.22, -4.07) * mm});
            skLineSegment(sketch, "E3718", {"start": v(22.22, -2.17) * mm, "end": v(23.5, -2.17) * mm});
            skLineSegment(sketch, "E3719", {"start": v(23.5, -2.17) * mm, "end": v(23.5, -2.93) * mm});
            skLineSegment(sketch, "E3720", {"start": v(23.5, -2.93) * mm, "end": v(22.22, -2.93) * mm});
            skLineSegment(sketch, "E3721", {"start": v(22.22, -2.93) * mm, "end": v(22.22, -2.17) * mm});
            skLineSegment(sketch, "E3722", {"start": v(24.5, -3.12) * mm, "end": v(25.78, -3.12) * mm});
            skLineSegment(sketch, "E3723", {"start": v(25.78, -3.12) * mm, "end": v(25.78, -3.88) * mm});
            skLineSegment(sketch, "E3724", {"start": v(25.78, -3.88) * mm, "end": v(24.5, -3.88) * mm});
            skLineSegment(sketch, "E3725", {"start": v(24.5, -3.88) * mm, "end": v(24.5, -3.12) * mm});
            skArc(sketch, "E3726", {"start": v(24.25, -3.5) * mm, "mid": v(24, -3.25) * mm, "end": v(23.75, -3.5) * mm});
            skArc(sketch, "E3727", {"start": v(23.75, -3.5) * mm, "mid": v(24, -3.75) * mm, "end": v(24.25, -3.5) * mm});
            skLineSegment(sketch, "E3728", {"start": v(26, -1.88) * mm, "end": v(26, -5.12) * mm});
            skLineSegment(sketch, "E3729", {"start": v(26, -5.12) * mm, "end": v(22, -5.12) * mm});
            skLineSegment(sketch, "E3730", {"start": v(22, -5.12) * mm, "end": v(22, -2.12) * mm});
            skLineSegment(sketch, "E3731", {"start": v(22, -2.12) * mm, "end": v(22.25, -1.88) * mm});
            skLineSegment(sketch, "E3732", {"start": v(22.25, -1.88) * mm, "end": v(26, -1.88) * mm});
            skLineSegment(sketch, "E3733", {"start": v(3.93, 18.28) * mm, "end": v(3.93, 17) * mm});
            skLineSegment(sketch, "E3734", {"start": v(3.93, 17) * mm, "end": v(3.17, 17) * mm});
            skLineSegment(sketch, "E3735", {"start": v(3.17, 17) * mm, "end": v(3.17, 18.28) * mm});
            skLineSegment(sketch, "E3736", {"start": v(3.17, 18.28) * mm, "end": v(3.93, 18.28) * mm});
            skLineSegment(sketch, "E3737", {"start": v(5.83, 18.28) * mm, "end": v(5.83, 17) * mm});
            skLineSegment(sketch, "E3738", {"start": v(5.83, 17) * mm, "end": v(5.07, 17) * mm});
            skLineSegment(sketch, "E3739", {"start": v(5.07, 17) * mm, "end": v(5.07, 18.28) * mm});
            skLineSegment(sketch, "E3740", {"start": v(5.07, 18.28) * mm, "end": v(5.83, 18.28) * mm});
            skLineSegment(sketch, "E3741", {"start": v(4.88, 16) * mm, "end": v(4.88, 14.72) * mm});
            skLineSegment(sketch, "E3742", {"start": v(4.88, 14.72) * mm, "end": v(4.12, 14.72) * mm});
            skLineSegment(sketch, "E3743", {"start": v(4.12, 14.72) * mm, "end": v(4.12, 16) * mm});
            skLineSegment(sketch, "E3744", {"start": v(4.12, 16) * mm, "end": v(4.88, 16) * mm});
            skArc(sketch, "E3745", {"start": v(4.75, 16.5) * mm, "mid": v(4.5, 16.75) * mm, "end": v(4.25, 16.5) * mm});
            skArc(sketch, "E3746", {"start": v(4.25, 16.5) * mm, "mid": v(4.5, 16.25) * mm, "end": v(4.75, 16.5) * mm});
            skLineSegment(sketch, "E3747", {"start": v(6.12, 14.5) * mm, "end": v(2.88, 14.5) * mm});
            skLineSegment(sketch, "E3748", {"start": v(2.88, 14.5) * mm, "end": v(2.88, 18.5) * mm});
            skLineSegment(sketch, "E3749", {"start": v(2.88, 18.5) * mm, "end": v(5.88, 18.5) * mm});
            skLineSegment(sketch, "E3750", {"start": v(5.88, 18.5) * mm, "end": v(6.12, 18.25) * mm});
            skLineSegment(sketch, "E3751", {"start": v(6.12, 18.25) * mm, "end": v(6.12, 14.5) * mm});
            skLineSegment(sketch, "E3752", {"start": v(22.22, -14.07) * mm, "end": v(23.5, -14.07) * mm});
            skLineSegment(sketch, "E3753", {"start": v(23.5, -14.07) * mm, "end": v(23.5, -14.83) * mm});
            skLineSegment(sketch, "E3754", {"start": v(23.5, -14.83) * mm, "end": v(22.22, -14.83) * mm});
            skLineSegment(sketch, "E3755", {"start": v(22.22, -14.83) * mm, "end": v(22.22, -14.07) * mm});
            skLineSegment(sketch, "E3756", {"start": v(22.22, -12.17) * mm, "end": v(23.5, -12.17) * mm});
            skLineSegment(sketch, "E3757", {"start": v(23.5, -12.17) * mm, "end": v(23.5, -12.93) * mm});
            skLineSegment(sketch, "E3758", {"start": v(23.5, -12.93) * mm, "end": v(22.22, -12.93) * mm});
            skLineSegment(sketch, "E3759", {"start": v(22.22, -12.93) * mm, "end": v(22.22, -12.17) * mm});
            skLineSegment(sketch, "E3760", {"start": v(24.5, -13.12) * mm, "end": v(25.78, -13.12) * mm});
            skLineSegment(sketch, "E3761", {"start": v(25.78, -13.12) * mm, "end": v(25.78, -13.88) * mm});
            skLineSegment(sketch, "E3762", {"start": v(25.78, -13.88) * mm, "end": v(24.5, -13.88) * mm});
            skLineSegment(sketch, "E3763", {"start": v(24.5, -13.88) * mm, "end": v(24.5, -13.12) * mm});
            skArc(sketch, "E3764", {"start": v(24.25, -13.5) * mm, "mid": v(24, -13.25) * mm, "end": v(23.75, -13.5) * mm});
            skArc(sketch, "E3765", {"start": v(23.75, -13.5) * mm, "mid": v(24, -13.75) * mm, "end": v(24.25, -13.5) * mm});
            skLineSegment(sketch, "E3766", {"start": v(26, -11.88) * mm, "end": v(26, -15.12) * mm});
            skLineSegment(sketch, "E3767", {"start": v(26, -15.12) * mm, "end": v(22, -15.12) * mm});
            skLineSegment(sketch, "E3768", {"start": v(22, -15.12) * mm, "end": v(22, -12.12) * mm});
            skLineSegment(sketch, "E3769", {"start": v(22, -12.12) * mm, "end": v(22.25, -11.88) * mm});
            skLineSegment(sketch, "E3770", {"start": v(22.25, -11.88) * mm, "end": v(26, -11.88) * mm});
            skLineSegment(sketch, "E3771", {"start": v(-6.43, -15.78) * mm, "end": v(-6.43, -14.5) * mm});
            skLineSegment(sketch, "E3772", {"start": v(-6.43, -14.5) * mm, "end": v(-5.67, -14.5) * mm});
            skLineSegment(sketch, "E3773", {"start": v(-5.67, -14.5) * mm, "end": v(-5.67, -15.78) * mm});
            skLineSegment(sketch, "E3774", {"start": v(-5.67, -15.78) * mm, "end": v(-6.43, -15.78) * mm});
            skLineSegment(sketch, "E3775", {"start": v(-8.33, -15.78) * mm, "end": v(-8.33, -14.5) * mm});
            skLineSegment(sketch, "E3776", {"start": v(-8.33, -14.5) * mm, "end": v(-7.57, -14.5) * mm});
            skLineSegment(sketch, "E3777", {"start": v(-7.57, -14.5) * mm, "end": v(-7.57, -15.78) * mm});
            skLineSegment(sketch, "E3778", {"start": v(-7.57, -15.78) * mm, "end": v(-8.33, -15.78) * mm});
            skLineSegment(sketch, "E3779", {"start": v(-7.38, -13.5) * mm, "end": v(-7.38, -12.22) * mm});
            skLineSegment(sketch, "E3780", {"start": v(-7.38, -12.22) * mm, "end": v(-6.62, -12.22) * mm});
            skLineSegment(sketch, "E3781", {"start": v(-6.62, -12.22) * mm, "end": v(-6.62, -13.5) * mm});
            skLineSegment(sketch, "E3782", {"start": v(-6.62, -13.5) * mm, "end": v(-7.38, -13.5) * mm});
            skArc(sketch, "E3783", {"start": v(-6.75, -14) * mm, "mid": v(-7, -13.75) * mm, "end": v(-7.25, -14) * mm});
            skArc(sketch, "E3784", {"start": v(-7.25, -14) * mm, "mid": v(-7, -14.25) * mm, "end": v(-6.75, -14) * mm});
            skLineSegment(sketch, "E3785", {"start": v(-8.62, -12) * mm, "end": v(-5.38, -12) * mm});
            skLineSegment(sketch, "E3786", {"start": v(-5.38, -12) * mm, "end": v(-5.38, -16) * mm});
            skLineSegment(sketch, "E3787", {"start": v(-5.38, -16) * mm, "end": v(-8.38, -16) * mm});
            skLineSegment(sketch, "E3788", {"start": v(-8.38, -16) * mm, "end": v(-8.62, -15.75) * mm});
            skLineSegment(sketch, "E3789", {"start": v(-8.62, -15.75) * mm, "end": v(-8.62, -12) * mm});
            skLineSegment(sketch, "E3790", {"start": v(-39.75, -7) * mm, "end": v(-40, -6) * mm});
            skLineSegment(sketch, "E3791", {"start": v(-40, -6) * mm, "end": v(-40.25, -7) * mm});
            skLineSegment(sketch, "E3792", {"start": v(-40.25, -7) * mm, "end": v(-39.75, -7) * mm});
            skLineSegment(sketch, "E3793", {"start": v(-40, -8.2) * mm, "end": v(-40, -6) * mm});
            skLineSegment(sketch, "E3794", {"start": v(-40.25, -13) * mm, "end": v(-40, -14) * mm});
            skLineSegment(sketch, "E3795", {"start": v(-40, -14) * mm, "end": v(-39.75, -13) * mm});
            skLineSegment(sketch, "E3796", {"start": v(-39.75, -13) * mm, "end": v(-40.25, -13) * mm});
            skLineSegment(sketch, "E3797", {"start": v(-40, -11.8) * mm, "end": v(-40, -14) * mm});
            skLineSegment(sketch, "E3798", {"start": v(-33.5, -14) * mm, "end": v(-40.5, -14) * mm});
            skLineSegment(sketch, "E3799", {"start": v(-33.5, -6) * mm, "end": v(-40.5, -6) * mm});
            skLineSegment(sketch, "E3800", {"start": v(-39.75, -15) * mm, "end": v(-40, -14) * mm});
            skLineSegment(sketch, "E3801", {"start": v(-40, -14) * mm, "end": v(-40.25, -15) * mm});
            skLineSegment(sketch, "E3802", {"start": v(-40.25, -15) * mm, "end": v(-39.75, -15) * mm});
            skLineSegment(sketch, "E3803", {"start": v(-40, -19.4) * mm, "end": v(-40, -14) * mm});
            skLineSegment(sketch, "E3804", {"start": v(-40.25, -30) * mm, "end": v(-40, -31) * mm});
            skLineSegment(sketch, "E3805", {"start": v(-40, -31) * mm, "end": v(-39.75, -30) * mm});
            skLineSegment(sketch, "E3806", {"start": v(-39.75, -30) * mm, "end": v(-40.25, -30) * mm});
            skLineSegment(sketch, "E3807", {"start": v(-40, -24.6) * mm, "end": v(-40, -31) * mm});
            skLineSegment(sketch, "E3808", {"start": v(-33.5, -31) * mm, "end": v(-40.5, -31) * mm});
            skLineSegment(sketch, "E3809", {"start": v(-39.75, 1) * mm, "end": v(-40, 2) * mm});
            skLineSegment(sketch, "E3810", {"start": v(-40, 2) * mm, "end": v(-40.25, 1) * mm});
            skLineSegment(sketch, "E3811", {"start": v(-40.25, 1) * mm, "end": v(-39.75, 1) * mm});
            skLineSegment(sketch, "E3812", {"start": v(-40, -0.2) * mm, "end": v(-40, 2) * mm});
            skLineSegment(sketch, "E3813", {"start": v(-40.25, -5) * mm, "end": v(-40, -6) * mm});
            skLineSegment(sketch, "E3814", {"start": v(-40, -6) * mm, "end": v(-39.75, -5) * mm});
            skLineSegment(sketch, "E3815", {"start": v(-39.75, -5) * mm, "end": v(-40.25, -5) * mm});
            skLineSegment(sketch, "E3816", {"start": v(-40, -3.8) * mm, "end": v(-40, -6) * mm});
            skLineSegment(sketch, "E3817", {"start": v(-33.5, 2) * mm, "end": v(-40.5, 2) * mm});
            skLineSegment(sketch, "E3818", {"start": v(-39.75, 9) * mm, "end": v(-40, 10) * mm});
            skLineSegment(sketch, "E3819", {"start": v(-40, 10) * mm, "end": v(-40.25, 9) * mm});
            skLineSegment(sketch, "E3820", {"start": v(-40.25, 9) * mm, "end": v(-39.75, 9) * mm});
            skLineSegment(sketch, "E3821", {"start": v(-40, 7.8) * mm, "end": v(-40, 10) * mm});
            skLineSegment(sketch, "E3822", {"start": v(-40.25, 3) * mm, "end": v(-40, 2) * mm});
            skLineSegment(sketch, "E3823", {"start": v(-40, 2) * mm, "end": v(-39.75, 3) * mm});
            skLineSegment(sketch, "E3824", {"start": v(-39.75, 3) * mm, "end": v(-40.25, 3) * mm});
            skLineSegment(sketch, "E3825", {"start": v(-40, 4.2) * mm, "end": v(-40, 2) * mm});
            skLineSegment(sketch, "E3826", {"start": v(-33.5, 10) * mm, "end": v(-40.5, 10) * mm});
            skLineSegment(sketch, "E3827", {"start": v(-39.75, 17) * mm, "end": v(-40, 18) * mm});
            skLineSegment(sketch, "E3828", {"start": v(-40, 18) * mm, "end": v(-40.25, 17) * mm});
            skLineSegment(sketch, "E3829", {"start": v(-40.25, 17) * mm, "end": v(-39.75, 17) * mm});
            skLineSegment(sketch, "E3830", {"start": v(-40, 15.8) * mm, "end": v(-40, 18) * mm});
            skLineSegment(sketch, "E3831", {"start": v(-40.25, 11) * mm, "end": v(-40, 10) * mm});
            skLineSegment(sketch, "E3832", {"start": v(-40, 10) * mm, "end": v(-39.75, 11) * mm});
            skLineSegment(sketch, "E3833", {"start": v(-39.75, 11) * mm, "end": v(-40.25, 11) * mm});
            skLineSegment(sketch, "E3834", {"start": v(-40, 12.2) * mm, "end": v(-40, 10) * mm});
            skLineSegment(sketch, "E3835", {"start": v(-33.5, 18) * mm, "end": v(-40.5, 18) * mm});
            skLineSegment(sketch, "E3836", {"start": v(-39.75, 25) * mm, "end": v(-40, 26) * mm});
            skLineSegment(sketch, "E3837", {"start": v(-40, 26) * mm, "end": v(-40.25, 25) * mm});
            skLineSegment(sketch, "E3838", {"start": v(-40.25, 25) * mm, "end": v(-39.75, 25) * mm});
            skLineSegment(sketch, "E3839", {"start": v(-40, 23.8) * mm, "end": v(-40, 26) * mm});
            skLineSegment(sketch, "E3840", {"start": v(-40.25, 19) * mm, "end": v(-40, 18) * mm});
            skLineSegment(sketch, "E3841", {"start": v(-40, 18) * mm, "end": v(-39.75, 19) * mm});
            skLineSegment(sketch, "E3842", {"start": v(-39.75, 19) * mm, "end": v(-40.25, 19) * mm});
            skLineSegment(sketch, "E3843", {"start": v(-40, 20.2) * mm, "end": v(-40, 18) * mm});
            skLineSegment(sketch, "E3844", {"start": v(-33.5, 26) * mm, "end": v(-40.5, 26) * mm});
            skLineSegment(sketch, "E3845", {"start": v(-39.75, 33) * mm, "end": v(-40, 34) * mm});
            skLineSegment(sketch, "E3846", {"start": v(-40, 34) * mm, "end": v(-40.25, 33) * mm});
            skLineSegment(sketch, "E3847", {"start": v(-40.25, 33) * mm, "end": v(-39.75, 33) * mm});
            skLineSegment(sketch, "E3848", {"start": v(-40, 31.8) * mm, "end": v(-40, 34) * mm});
            skLineSegment(sketch, "E3849", {"start": v(-40.25, 27) * mm, "end": v(-40, 26) * mm});
            skLineSegment(sketch, "E3850", {"start": v(-40, 26) * mm, "end": v(-39.75, 27) * mm});
            skLineSegment(sketch, "E3851", {"start": v(-39.75, 27) * mm, "end": v(-40.25, 27) * mm});
            skLineSegment(sketch, "E3852", {"start": v(-40, 28.2) * mm, "end": v(-40, 26) * mm});
            skLineSegment(sketch, "E3853", {"start": v(-33.5, 34) * mm, "end": v(-40.5, 34) * mm});
            skLineSegment(sketch, "E3854", {"start": v(37.25, -14.5) * mm, "end": v(37, -13.5) * mm});
            skLineSegment(sketch, "E3855", {"start": v(37, -13.5) * mm, "end": v(36.75, -14.5) * mm});
            skLineSegment(sketch, "E3856", {"start": v(36.75, -14.5) * mm, "end": v(37.25, -14.5) * mm});
            skLineSegment(sketch, "E3857", {"start": v(37, -16.8) * mm, "end": v(37, -13.5) * mm});
            skLineSegment(sketch, "E3858", {"start": v(36.75, -29) * mm, "end": v(37, -30) * mm});
            skLineSegment(sketch, "E3859", {"start": v(37, -30) * mm, "end": v(37.25, -29) * mm});
            skLineSegment(sketch, "E3860", {"start": v(37.25, -29) * mm, "end": v(36.75, -29) * mm});
            skLineSegment(sketch, "E3861", {"start": v(37, -25.2) * mm, "end": v(37, -30) * mm});
            skLineSegment(sketch, "E3862", {"start": v(29.5, -30) * mm, "end": v(37.5, -30) * mm});
            skLineSegment(sketch, "E3863", {"start": v(29, -13.5) * mm, "end": v(37.5, -13.5) * mm});
            skLineSegment(sketch, "E3864", {"start": v(37.25, -31) * mm, "end": v(37, -30) * mm});
            skLineSegment(sketch, "E3865", {"start": v(37, -30) * mm, "end": v(36.75, -31) * mm});
            skLineSegment(sketch, "E3866", {"start": v(36.75, -31) * mm, "end": v(37.25, -31) * mm});
            skLineSegment(sketch, "E3867", {"start": v(37, -32.2) * mm, "end": v(37, -30) * mm});
            skLineSegment(sketch, "E3868", {"start": v(36.75, -37) * mm, "end": v(37, -38) * mm});
            skLineSegment(sketch, "E3869", {"start": v(37, -38) * mm, "end": v(37.25, -37) * mm});
            skLineSegment(sketch, "E3870", {"start": v(37.25, -37) * mm, "end": v(36.75, -37) * mm});
            skLineSegment(sketch, "E3871", {"start": v(37, -35.8) * mm, "end": v(37, -38) * mm});
            skLineSegment(sketch, "E3872", {"start": v(29.5, -38) * mm, "end": v(37.5, -38) * mm});
            skLineSegment(sketch, "E3873", {"start": v(37.25, -39) * mm, "end": v(37, -38) * mm});
            skLineSegment(sketch, "E3874", {"start": v(37, -38) * mm, "end": v(36.75, -39) * mm});
            skLineSegment(sketch, "E3875", {"start": v(36.75, -39) * mm, "end": v(37.25, -39) * mm});
            skLineSegment(sketch, "E3876", {"start": v(37, -39.2) * mm, "end": v(37, -38) * mm});
            skLineSegment(sketch, "E3877", {"start": v(36.75, -43) * mm, "end": v(37, -44) * mm});
            skLineSegment(sketch, "E3878", {"start": v(37, -44) * mm, "end": v(37.25, -43) * mm});
            skLineSegment(sketch, "E3879", {"start": v(37.25, -43) * mm, "end": v(36.75, -43) * mm});
            skLineSegment(sketch, "E3880", {"start": v(37, -42.8) * mm, "end": v(37, -44) * mm});
            skLineSegment(sketch, "E3881", {"start": v(29.5, -44) * mm, "end": v(37.5, -44) * mm});
            skLineSegment(sketch, "E3882", {"start": v(32, -51.25) * mm, "end": v(33, -51) * mm});
            skLineSegment(sketch, "E3883", {"start": v(33, -51) * mm, "end": v(32, -50.75) * mm});
            skLineSegment(sketch, "E3884", {"start": v(32, -50.75) * mm, "end": v(32, -51.25) * mm});
            skLineSegment(sketch, "E3885", {"start": v(35, -51) * mm, "end": v(33, -51) * mm});
            skLineSegment(sketch, "E3886", {"start": v(30, -50.75) * mm, "end": v(29, -51) * mm});
            skLineSegment(sketch, "E3887", {"start": v(29, -51) * mm, "end": v(30, -51.25) * mm});
            skLineSegment(sketch, "E3888", {"start": v(30, -51.25) * mm, "end": v(30, -50.75) * mm});
            skLineSegment(sketch, "E3889", {"start": v(33, -51) * mm, "end": v(29, -51) * mm});
            skLineSegment(sketch, "E3890", {"start": v(33, -48.5) * mm, "end": v(33, -51.5) * mm});
            skLineSegment(sketch, "E3891", {"start": v(29, -38.5) * mm, "end": v(29, -51.5) * mm});
            skLineSegment(sketch, "E3892", {"start": v(40.25, 44) * mm, "end": v(40, 45) * mm});
            skLineSegment(sketch, "E3893", {"start": v(40, 45) * mm, "end": v(39.75, 44) * mm});
            skLineSegment(sketch, "E3894", {"start": v(39.75, 44) * mm, "end": v(40.25, 44) * mm});
            skLineSegment(sketch, "E3895", {"start": v(40, 1.6) * mm, "end": v(40, 45) * mm});
            skLineSegment(sketch, "E3896", {"start": v(39.75, -47) * mm, "end": v(40, -48) * mm});
            skLineSegment(sketch, "E3897", {"start": v(40, -48) * mm, "end": v(40.25, -47) * mm});
            skLineSegment(sketch, "E3898", {"start": v(40.25, -47) * mm, "end": v(39.75, -47) * mm});
            skLineSegment(sketch, "E3899", {"start": v(40, -3.6) * mm, "end": v(40, -48) * mm});
            skLineSegment(sketch, "E3900", {"start": v(33.5, -48) * mm, "end": v(40.5, -48) * mm});
            skLineSegment(sketch, "E3901", {"start": v(33.5, 45) * mm, "end": v(40.5, 45) * mm});
            skLineSegment(sketch, "E3902", {"start": v(30, 46.75) * mm, "end": v(29, 46.5) * mm});
            skLineSegment(sketch, "E3903", {"start": v(29, 46.5) * mm, "end": v(30, 46.25) * mm});
            skLineSegment(sketch, "E3904", {"start": v(30, 46.25) * mm, "end": v(30, 46.75) * mm});
            skLineSegment(sketch, "E3905", {"start": v(31, 46.5) * mm, "end": v(29, 46.5) * mm});
            skLineSegment(sketch, "E3906", {"start": v(27.5, 46.25) * mm, "end": v(28.5, 46.5) * mm});
            skLineSegment(sketch, "E3907", {"start": v(28.5, 46.5) * mm, "end": v(27.5, 46.75) * mm});
            skLineSegment(sketch, "E3908", {"start": v(27.5, 46.75) * mm, "end": v(27.5, 46.25) * mm});
            skLineSegment(sketch, "E3909", {"start": v(25.4, 46.5) * mm, "end": v(28.5, 46.5) * mm});
            skLineSegment(sketch, "E3910", {"start": v(29, 41.5) * mm, "end": v(29, 47) * mm});
            skLineSegment(sketch, "E3911", {"start": v(28.5, -13) * mm, "end": v(28.5, 47) * mm});
            skLineSegment(sketch, "E3912", {"start": v(37.25, -45) * mm, "end": v(37, -44) * mm});
            skLineSegment(sketch, "E3913", {"start": v(37, -44) * mm, "end": v(36.75, -45) * mm});
            skLineSegment(sketch, "E3914", {"start": v(36.75, -45) * mm, "end": v(37.25, -45) * mm});
            skLineSegment(sketch, "E3915", {"start": v(37, -44.2) * mm, "end": v(37, -44) * mm});
            skLineSegment(sketch, "E3916", {"start": v(36.75, -47) * mm, "end": v(37, -48) * mm});
            skLineSegment(sketch, "E3917", {"start": v(37, -48) * mm, "end": v(37.25, -47) * mm});
            skLineSegment(sketch, "E3918", {"start": v(37.25, -47) * mm, "end": v(36.75, -47) * mm});
            skLineSegment(sketch, "E3919", {"start": v(37, -47.8) * mm, "end": v(37, -48) * mm});
            skLineSegment(sketch, "E3920", {"start": v(33.5, -48) * mm, "end": v(37.5, -48) * mm});
            skLineSegment(sketch, "E3921", {"start": v(37.25, -1) * mm, "end": v(37, 0) * mm});
            skLineSegment(sketch, "E3922", {"start": v(37, 0) * mm, "end": v(36.75, -1) * mm});
            skLineSegment(sketch, "E3923", {"start": v(36.75, -1) * mm, "end": v(37.25, -1) * mm});
            skLineSegment(sketch, "E3924", {"start": v(37, -2.8) * mm, "end": v(37, 0) * mm});
            skLineSegment(sketch, "E3925", {"start": v(36.75, -12.5) * mm, "end": v(37, -13.5) * mm});
            skLineSegment(sketch, "E3926", {"start": v(37, -13.5) * mm, "end": v(37.25, -12.5) * mm});
            skLineSegment(sketch, "E3927", {"start": v(37.25, -12.5) * mm, "end": v(36.75, -12.5) * mm});
            skLineSegment(sketch, "E3928", {"start": v(37, -11.2) * mm, "end": v(37, -13.5) * mm});
            skLineSegment(sketch, "E3929", {"start": v(29, 0) * mm, "end": v(37.5, 0) * mm});
            skLineSegment(sketch, "E3930", {"start": v(37.25, 12.5) * mm, "end": v(37, 13.5) * mm});
            skLineSegment(sketch, "E3931", {"start": v(37, 13.5) * mm, "end": v(36.75, 12.5) * mm});
            skLineSegment(sketch, "E3932", {"start": v(36.75, 12.5) * mm, "end": v(37.25, 12.5) * mm});
            skLineSegment(sketch, "E3933", {"start": v(37, 11.2) * mm, "end": v(37, 13.5) * mm});
            skLineSegment(sketch, "E3934", {"start": v(36.75, 1) * mm, "end": v(37, 0) * mm});
            skLineSegment(sketch, "E3935", {"start": v(37, 0) * mm, "end": v(37.25, 1) * mm});
            skLineSegment(sketch, "E3936", {"start": v(37.25, 1) * mm, "end": v(36.75, 1) * mm});
            skLineSegment(sketch, "E3937", {"start": v(37, 2.8) * mm, "end": v(37, 0) * mm});
            skLineSegment(sketch, "E3938", {"start": v(29, 13.5) * mm, "end": v(37.5, 13.5) * mm});
            skLineSegment(sketch, "E3939", {"start": v(37.25, 26) * mm, "end": v(37, 27) * mm});
            skLineSegment(sketch, "E3940", {"start": v(37, 27) * mm, "end": v(36.75, 26) * mm});
            skLineSegment(sketch, "E3941", {"start": v(36.75, 26) * mm, "end": v(37.25, 26) * mm});
            skLineSegment(sketch, "E3942", {"start": v(37, 24.2) * mm, "end": v(37, 27) * mm});
            skLineSegment(sketch, "E3943", {"start": v(36.75, 14.5) * mm, "end": v(37, 13.5) * mm});
            skLineSegment(sketch, "E3944", {"start": v(37, 13.5) * mm, "end": v(37.25, 14.5) * mm});
            skLineSegment(sketch, "E3945", {"start": v(37.25, 14.5) * mm, "end": v(36.75, 14.5) * mm});
            skLineSegment(sketch, "E3946", {"start": v(37, 15.8) * mm, "end": v(37, 13.5) * mm});
            skLineSegment(sketch, "E3947", {"start": v(29, 27) * mm, "end": v(37.5, 27) * mm});
            skLineSegment(sketch, "E3948", {"start": v(37.25, 40) * mm, "end": v(37, 41) * mm});
            skLineSegment(sketch, "E3949", {"start": v(37, 41) * mm, "end": v(36.75, 40) * mm});
            skLineSegment(sketch, "E3950", {"start": v(36.75, 40) * mm, "end": v(37.25, 40) * mm});
            skLineSegment(sketch, "E3951", {"start": v(37, 36.6) * mm, "end": v(37, 41) * mm});
            skLineSegment(sketch, "E3952", {"start": v(36.75, 28) * mm, "end": v(37, 27) * mm});
            skLineSegment(sketch, "E3953", {"start": v(37, 27) * mm, "end": v(37.25, 28) * mm});
            skLineSegment(sketch, "E3954", {"start": v(37.25, 28) * mm, "end": v(36.75, 28) * mm});
            skLineSegment(sketch, "E3955", {"start": v(37, 31.4) * mm, "end": v(37, 27) * mm});
            skLineSegment(sketch, "E3956", {"start": v(29.5, 41) * mm, "end": v(37.5, 41) * mm});
            skLineSegment(sketch, "E3957", {"start": v(37.25, 44) * mm, "end": v(37, 45) * mm});
            skLineSegment(sketch, "E3958", {"start": v(37, 45) * mm, "end": v(36.75, 44) * mm});
            skLineSegment(sketch, "E3959", {"start": v(36.75, 44) * mm, "end": v(37.25, 44) * mm});
            skLineSegment(sketch, "E3960", {"start": v(37, 44.8) * mm, "end": v(37, 45) * mm});
            skLineSegment(sketch, "E3961", {"start": v(36.75, 42) * mm, "end": v(37, 41) * mm});
            skLineSegment(sketch, "E3962", {"start": v(37, 41) * mm, "end": v(37.25, 42) * mm});
            skLineSegment(sketch, "E3963", {"start": v(37.25, 42) * mm, "end": v(36.75, 42) * mm});
            skLineSegment(sketch, "E3964", {"start": v(37, 41.2) * mm, "end": v(37, 41) * mm});
            skLineSegment(sketch, "E3965", {"start": v(33.5, 45) * mm, "end": v(37.5, 45) * mm});
            skLineSegment(sketch, "E3966", {"start": v(32, 50.75) * mm, "end": v(33, 51) * mm});
            skLineSegment(sketch, "E3967", {"start": v(33, 51) * mm, "end": v(32, 51.25) * mm});
            skLineSegment(sketch, "E3968", {"start": v(32, 51.25) * mm, "end": v(32, 50.75) * mm});
            skLineSegment(sketch, "E3969", {"start": v(0.6, 51) * mm, "end": v(33, 51) * mm});
            skLineSegment(sketch, "E3970", {"start": v(-36, 51.25) * mm, "end": v(-37, 51) * mm});
            skLineSegment(sketch, "E3971", {"start": v(-37, 51) * mm, "end": v(-36, 50.75) * mm});
            skLineSegment(sketch, "E3972", {"start": v(-36, 50.75) * mm, "end": v(-36, 51.25) * mm});
            skLineSegment(sketch, "E3973", {"start": v(-4.6, 51) * mm, "end": v(-37, 51) * mm});
            skLineSegment(sketch, "E3974", {"start": v(33, 45.5) * mm, "end": v(33, 51.5) * mm});
            skLineSegment(sketch, "E3975", {"start": v(-37, 45.5) * mm, "end": v(-37, 51.5) * mm});
            skLineSegment(sketch, "E3976", {"start": v(32, 47.75) * mm, "end": v(33, 48) * mm});
            skLineSegment(sketch, "E3977", {"start": v(33, 48) * mm, "end": v(32, 48.25) * mm});
            skLineSegment(sketch, "E3978", {"start": v(32, 48.25) * mm, "end": v(32, 47.75) * mm});
            skLineSegment(sketch, "E3979", {"start": v(32.8, 48) * mm, "end": v(33, 48) * mm});
            skLineSegment(sketch, "E3980", {"start": v(30, 48.25) * mm, "end": v(29, 48) * mm});
            skLineSegment(sketch, "E3981", {"start": v(29, 48) * mm, "end": v(30, 47.75) * mm});
            skLineSegment(sketch, "E3982", {"start": v(30, 47.75) * mm, "end": v(30, 48.25) * mm});
            skLineSegment(sketch, "E3983", {"start": v(29.2, 48) * mm, "end": v(29, 48) * mm});
            skLineSegment(sketch, "E3984", {"start": v(33, 45.5) * mm, "end": v(33, 48.5) * mm});
            skLineSegment(sketch, "E3985", {"start": v(29, 41.5) * mm, "end": v(29, 48.5) * mm});
            skLineSegment(sketch, "E3986", {"start": v(28, 47.75) * mm, "end": v(29, 48) * mm});
            skLineSegment(sketch, "E3987", {"start": v(29, 48) * mm, "end": v(28, 48.25) * mm});
            skLineSegment(sketch, "E3988", {"start": v(28, 48.25) * mm, "end": v(28, 47.75) * mm});
            skLineSegment(sketch, "E3989", {"start": v(0.6, 48) * mm, "end": v(29, 48) * mm});
            skLineSegment(sketch, "E3990", {"start": v(-32, 48.25) * mm, "end": v(-33, 48) * mm});
            skLineSegment(sketch, "E3991", {"start": v(-33, 48) * mm, "end": v(-32, 47.75) * mm});
            skLineSegment(sketch, "E3992", {"start": v(-32, 47.75) * mm, "end": v(-32, 48.25) * mm});
            skLineSegment(sketch, "E3993", {"start": v(-4.6, 48) * mm, "end": v(-33, 48) * mm});
            skLineSegment(sketch, "E3994", {"start": v(-33, 41.5) * mm, "end": v(-33, 48.5) * mm});
            skLineSegment(sketch, "E3995", {"start": v(-39.75, -45) * mm, "end": v(-40, -44) * mm});
            skLineSegment(sketch, "E3996", {"start": v(-40, -44) * mm, "end": v(-40.25, -45) * mm});
            skLineSegment(sketch, "E3997", {"start": v(-40.25, -45) * mm, "end": v(-39.75, -45) * mm});
            skLineSegment(sketch, "E3998", {"start": v(-40, -44.2) * mm, "end": v(-40, -44) * mm});
            skLineSegment(sketch, "E3999", {"start": v(-40.25, -47) * mm, "end": v(-40, -48) * mm});
            skLineSegment(sketch, "E4000", {"start": v(-40, -48) * mm, "end": v(-39.75, -47) * mm});
            skLineSegment(sketch, "E4001", {"start": v(-39.75, -47) * mm, "end": v(-40.25, -47) * mm});
            skLineSegment(sketch, "E4002", {"start": v(-40, -47.8) * mm, "end": v(-40, -48) * mm});
            skLineSegment(sketch, "E4003", {"start": v(-37.5, -48) * mm, "end": v(-40.5, -48) * mm});
            skLineSegment(sketch, "E4004", {"start": v(-33.5, -44) * mm, "end": v(-40.5, -44) * mm});
            skLineSegment(sketch, "E4005", {"start": v(-39.75, -32) * mm, "end": v(-40, -31) * mm});
            skLineSegment(sketch, "E4006", {"start": v(-40, -31) * mm, "end": v(-40.25, -32) * mm});
            skLineSegment(sketch, "E4007", {"start": v(-40.25, -32) * mm, "end": v(-39.75, -32) * mm});
            skLineSegment(sketch, "E4008", {"start": v(-40, -34.4) * mm, "end": v(-40, -31) * mm});
            skLineSegment(sketch, "E4009", {"start": v(-40.25, -43) * mm, "end": v(-40, -44) * mm});
            skLineSegment(sketch, "E4010", {"start": v(-40, -44) * mm, "end": v(-39.75, -43) * mm});
            skLineSegment(sketch, "E4011", {"start": v(-39.75, -43) * mm, "end": v(-40.25, -43) * mm});
            skLineSegment(sketch, "E4012", {"start": v(-40, -39.6) * mm, "end": v(-40, -44) * mm});
            skLineSegment(sketch, "E4013", {"start": v(-39.75, 40) * mm, "end": v(-40, 41) * mm});
            skLineSegment(sketch, "E4014", {"start": v(-40, 41) * mm, "end": v(-40.25, 40) * mm});
            skLineSegment(sketch, "E4015", {"start": v(-40.25, 40) * mm, "end": v(-39.75, 40) * mm});
            skLineSegment(sketch, "E4016", {"start": v(-40, 39.8) * mm, "end": v(-40, 41) * mm});
            skLineSegment(sketch, "E4017", {"start": v(-40.25, 35) * mm, "end": v(-40, 34) * mm});
            skLineSegment(sketch, "E4018", {"start": v(-40, 34) * mm, "end": v(-39.75, 35) * mm});
            skLineSegment(sketch, "E4019", {"start": v(-39.75, 35) * mm, "end": v(-40.25, 35) * mm});
            skLineSegment(sketch, "E4020", {"start": v(-40, 36.2) * mm, "end": v(-40, 34) * mm});
            skLineSegment(sketch, "E4021", {"start": v(-33.5, 41) * mm, "end": v(-40.5, 41) * mm});
            skLineSegment(sketch, "E4022", {"start": v(-39.75, 44) * mm, "end": v(-40, 45) * mm});
            skLineSegment(sketch, "E4023", {"start": v(-40, 45) * mm, "end": v(-40.25, 44) * mm});
            skLineSegment(sketch, "E4024", {"start": v(-40.25, 44) * mm, "end": v(-39.75, 44) * mm});
            skLineSegment(sketch, "E4025", {"start": v(-40, 44.8) * mm, "end": v(-40, 45) * mm});
            skLineSegment(sketch, "E4026", {"start": v(-40.25, 42) * mm, "end": v(-40, 41) * mm});
            skLineSegment(sketch, "E4027", {"start": v(-40, 41) * mm, "end": v(-39.75, 42) * mm});
            skLineSegment(sketch, "E4028", {"start": v(-39.75, 42) * mm, "end": v(-40.25, 42) * mm});
            skLineSegment(sketch, "E4029", {"start": v(-40, 41.2) * mm, "end": v(-40, 41) * mm});
            skLineSegment(sketch, "E4030", {"start": v(-37.5, 45) * mm, "end": v(-40.5, 45) * mm});
            skLineSegment(sketch, "E4031", {"start": v(-34, 47.75) * mm, "end": v(-33, 48) * mm});
            skLineSegment(sketch, "E4032", {"start": v(-33, 48) * mm, "end": v(-34, 48.25) * mm});
            skLineSegment(sketch, "E4033", {"start": v(-34, 48.25) * mm, "end": v(-34, 47.75) * mm});
            skLineSegment(sketch, "E4034", {"start": v(-33.2, 48) * mm, "end": v(-33, 48) * mm});
            skLineSegment(sketch, "E4035", {"start": v(-36, 48.25) * mm, "end": v(-37, 48) * mm});
            skLineSegment(sketch, "E4036", {"start": v(-37, 48) * mm, "end": v(-36, 47.75) * mm});
            skLineSegment(sketch, "E4037", {"start": v(-36, 47.75) * mm, "end": v(-36, 48.25) * mm});
            skLineSegment(sketch, "E4038", {"start": v(-36.8, 48) * mm, "end": v(-37, 48) * mm});
            skLineSegment(sketch, "E4039", {"start": v(-33, -37.5) * mm, "end": v(-33, 48.5) * mm});
            skLineSegment(sketch, "E4040", {"start": v(-37, -47.5) * mm, "end": v(-37, 48.5) * mm});
            skLineSegment(sketch, "E4041", {"start": v(-34, -51.25) * mm, "end": v(-33, -51) * mm});
            skLineSegment(sketch, "E4042", {"start": v(-33, -51) * mm, "end": v(-34, -50.75) * mm});
            skLineSegment(sketch, "E4043", {"start": v(-34, -50.75) * mm, "end": v(-34, -51.25) * mm});
            skLineSegment(sketch, "E4044", {"start": v(-33.2, -51) * mm, "end": v(-33, -51) * mm});
            skLineSegment(sketch, "E4045", {"start": v(-36, -50.75) * mm, "end": v(-37, -51) * mm});
            skLineSegment(sketch, "E4046", {"start": v(-37, -51) * mm, "end": v(-36, -51.25) * mm});
            skLineSegment(sketch, "E4047", {"start": v(-36, -51.25) * mm, "end": v(-36, -50.75) * mm});
            skLineSegment(sketch, "E4048", {"start": v(-36.8, -51) * mm, "end": v(-37, -51) * mm});
            skLineSegment(sketch, "E4049", {"start": v(-33, -44.5) * mm, "end": v(-33, -51.5) * mm});
            skLineSegment(sketch, "E4050", {"start": v(-37, -48.5) * mm, "end": v(-37, -51.5) * mm});
            skLineSegment(sketch, "E4051", {"start": v(-26, 38.5) * mm, "end": v(-26.75, 37.75) * mm});
            skLineSegment(sketch, "E4052", {"start": v(-26.75, 37.75) * mm, "end": v(-26.75, 35) * mm});
            skLineSegment(sketch, "E4053", {"start": v(-9.75, -28.5) * mm, "end": v(-9.75, -24.75) * mm});
            skLineSegment(sketch, "E4054", {"start": v(-9.75, -24.75) * mm, "end": v(-11, -23.5) * mm});
            skLineSegment(sketch, "E4055", {"start": v(-37, -48) * mm, "end": v(33, -48) * mm});
            skLineSegment(sketch, "E4056", {"start": v(33, -48) * mm, "end": v(33, 45) * mm});
            skLineSegment(sketch, "E4057", {"start": v(33, 45) * mm, "end": v(-37, 45) * mm});
            skLineSegment(sketch, "E4058", {"start": v(-37, 45) * mm, "end": v(-37, -48) * mm});
            skSolve(sketch);
        }
        {
            var Q0;
            Q0=qCreatedBy(makeId("Top.planeOp"),FACE);
            var sketch = newSketch(context, id + "F1", { "sketchPlane" : qUnion([Q0])});
            skLineSegment(sketch, "E4059.0", {"start": v(35.5, 47.5) * mm, "end": v(-39.5, 47.5) * mm});
            skLineSegment(sketch, "E4059.1", {"start": v(35.5, -50.5) * mm, "end": v(35.5, 47.5) * mm});
            skLineSegment(sketch, "E4059.2", {"start": v(-39.5, -50.5) * mm, "end": v(35.5, -50.5) * mm});
            skLineSegment(sketch, "E4059.3", {"start": v(-39.5, 47.5) * mm, "end": v(-39.5, -50.5) * mm});
            skSolve(sketch);
        }
        {
            var Q0;
            Q0=makeQuery(id+"F1.imprint","IMPRINT",FACE,{"disambiguationData":[TD([[makeQuery(id+"F1.imprint","IMPRINT",EDGE,{"derivedFrom":sQuery(id+"F1.wireOp",EDGE,"E4059.0")}),1.0]])]});
            extrude(context, id + "F2", {"entities" : qUnion([Q0]), "depth" : 1.5 * mm, "offsetDistance" : 25 * mm});
        }
        {
            var Q0;
            Q0=makeQuery(id+"F2.opExtrude","CAP_FACE",FACE,{"disambiguationData":[OSD([sQuery(id+"F1.wireOp",EDGE,"E4059.0"),sQuery(id+"F1.wireOp",EDGE,"E4059.1"),sQuery(id+"F1.wireOp",EDGE,"E4059.2"),sQuery(id+"F1.wireOp",EDGE,"E4059.3")])],"isStart":true});
            var sketch = newSketch(context, id + "F3", { "sketchPlane" : qUnion([Q0])});
            skLineSegment(sketch, "E4060.0", {"start": v(25.5, -45.5) * mm, "end": v(-29.5, -45.5) * mm});
            skLineSegment(sketch, "E4060.1", {"start": v(33.5, 40.5) * mm, "end": v(33.5, -37.5) * mm});
            skLineSegment(sketch, "E4060.2", {"start": v(-29.5, 48.5) * mm, "end": v(25.5, 48.5) * mm});
            skLineSegment(sketch, "E4060.3", {"start": v(-37.5, -37.5) * mm, "end": v(-37.5, 40.5) * mm});
            skLineSegment(sketch, "E4061.top", {"start": v(33.5, -37.5) * mm, "end": v(25.5, -37.5) * mm});
            skLineSegment(sketch, "E4061.right", {"start": v(25.5, -45.5) * mm, "end": v(25.5, -37.5) * mm});
            skLineSegment(sketch, "E4062.top", {"start": v(-37.5, -37.5) * mm, "end": v(-29.5, -37.5) * mm});
            skLineSegment(sketch, "E4062.right", {"start": v(-29.5, -45.5) * mm, "end": v(-29.5, -37.5) * mm});
            skLineSegment(sketch, "E4063.top", {"start": v(-37.5, 40.5) * mm, "end": v(-29.5, 40.5) * mm});
            skLineSegment(sketch, "E4063.right", {"start": v(-29.5, 48.5) * mm, "end": v(-29.5, 40.5) * mm});
            skLineSegment(sketch, "E4064.top", {"start": v(33.5, 40.5) * mm, "end": v(25.5, 40.5) * mm});
            skLineSegment(sketch, "E4064.right", {"start": v(25.5, 48.5) * mm, "end": v(25.5, 40.5) * mm});
            skSolve(sketch);
        }
        {
            var Q0;
            Q0=makeQuery(id+"F3.imprint","IMPRINT",FACE,{"disambiguationData":[TD([[makeQuery(id+"F3.imprint","IMPRINT",EDGE,{"derivedFrom":sQuery(id+"F3.wireOp",EDGE,"E4060.0")}),1.0]])]});
            extrude(context, id + "F4", {"entities" : qUnion([Q0]), "operationType" : NewBodyOperationType.ADD, "depth" : (8.2 - 1.5) * mm, "offsetDistance" : 25 * mm});
        }
        {
            var Q0;
            Q0=makeQuery(id+"F4.opExtrude","CAP_FACE",FACE,{"disambiguationData":[OSD([sQuery(id+"F1.wireOp",EDGE,"E4059.0"),sQuery(id+"F1.wireOp",EDGE,"E4059.1"),sQuery(id+"F1.wireOp",EDGE,"E4059.2"),sQuery(id+"F1.wireOp",EDGE,"E4059.3"),sQuery(id+"F3.wireOp",EDGE,"E4060.0"),sQuery(id+"F3.wireOp",EDGE,"E4060.1"),sQuery(id+"F3.wireOp",EDGE,"E4060.2"),sQuery(id+"F3.wireOp",EDGE,"E4060.3")])],"isStart":false});
            var sketch = newSketch(context, id + "F5", { "sketchPlane" : qUnion([Q0])});
            skLineSegment(sketch, "E4065.bottom", {"start": v(-39.5, -36.25) * mm, "end": v(-29.8, -36.25) * mm});
            skLineSegment(sketch, "E4065.top", {"start": v(-39.5, 19.75) * mm, "end": v(-29.8, 19.75) * mm});
            skLineSegment(sketch, "E4065.left", {"start": v(-39.5, -36.25) * mm, "end": v(-39.5, 19.75) * mm});
            skLineSegment(sketch, "E4065.right", {"start": v(-29.8, -36.25) * mm, "end": v(-29.8, 19.75) * mm});
            skLineSegment(sketch, "E4066.bottom", {"start": v(-39.5, 28.75) * mm, "end": v(-29.8, 28.75) * mm});
            skLineSegment(sketch, "E4066.top", {"start": v(-39.5, 40.25) * mm, "end": v(-29.8, 40.25) * mm});
            skLineSegment(sketch, "E4066.left", {"start": v(-39.5, 28.75) * mm, "end": v(-39.5, 40.25) * mm});
            skLineSegment(sketch, "E4066.right", {"start": v(-29.8, 28.75) * mm, "end": v(-29.8, 40.25) * mm});
            skLineSegment(sketch, "E4067.bottom", {"start": v(35.5, 17.25) * mm, "end": v(25.8, 17.25) * mm});
            skLineSegment(sketch, "E4067.top", {"start": v(35.5, 40.25) * mm, "end": v(25.8, 40.25) * mm});
            skLineSegment(sketch, "E4067.left", {"start": v(35.5, 17.25) * mm, "end": v(35.5, 40.25) * mm});
            skLineSegment(sketch, "E4067.right", {"start": v(25.8, 17.25) * mm, "end": v(25.8, 40.25) * mm});
            skSolve(sketch);
        }
        {
            var Q0;
            {var subQ0=sQuery(id+"F5.wireOp",EDGE,"E4065.left");Q0=makeQuery(id+"F5.imprint","IMPRINT",FACE,{"disambiguationData":[TD([[makeQuery(id+"F5.imprint","IMPRINT",EDGE,{"derivedFrom":subQ0}),-1.0]])]});}
            var Q1;
            {var subQ0=sQuery(id+"F5.wireOp",EDGE,"E4065.right");Q1=makeQuery(id+"F5.imprint","IMPRINT",FACE,{"disambiguationData":[TD([[makeQuery(id+"F5.imprint","IMPRINT",EDGE,{"derivedFrom":subQ0}),1.0]])]});}
            var Q2;
            {var subQ0=sQuery(id+"F5.wireOp",EDGE,"E4066.left");Q2=makeQuery(id+"F5.imprint","IMPRINT",FACE,{"disambiguationData":[TD([[makeQuery(id+"F5.imprint","IMPRINT",EDGE,{"derivedFrom":subQ0}),-1.0]])]});}
            var Q3;
            {var subQ0=sQuery(id+"F5.wireOp",EDGE,"E4066.right");Q3=makeQuery(id+"F5.imprint","IMPRINT",FACE,{"disambiguationData":[TD([[makeQuery(id+"F5.imprint","IMPRINT",EDGE,{"derivedFrom":subQ0}),1.0]])]});}
            var Q4;
            {var subQ0=sQuery(id+"F5.wireOp",EDGE,"E4067.left");Q4=makeQuery(id+"F5.imprint","IMPRINT",FACE,{"disambiguationData":[TD([[makeQuery(id+"F5.imprint","IMPRINT",EDGE,{"derivedFrom":subQ0}),-1.0]])]});}
            var Q5;
            {var subQ0=sQuery(id+"F5.wireOp",EDGE,"E4067.right");Q5=makeQuery(id+"F5.imprint","IMPRINT",FACE,{"disambiguationData":[TD([[makeQuery(id+"F5.imprint","IMPRINT",EDGE,{"derivedFrom":subQ0}),-1.0]])]});}
            extrude(context, id + "F6", {"entities" : qUnion([Q0, Q1, Q2, Q3, Q4, Q5]), "operationType" : NewBodyOperationType.REMOVE, "oppositeDirection" : true, "depth" : 25 * mm, "offsetDistance" : 25 * mm});
        }
        {
            var Q0;
            {var subQ0=sQuery(id+"F3.wireOp",EDGE,"E4062.right");var subQ1=sQuery(id+"F3.wireOp",EDGE,"E4062.top");var subQ2=sQuery(id+"F3.wireOp",EDGE,"E4061.right");var subQ3=sQuery(id+"F3.wireOp",EDGE,"E4061.top");var subQ4=sQuery(id+"F3.wireOp",EDGE,"E4060.3");var subQ5=sQuery(id+"F3.wireOp",EDGE,"E4060.1");var subQ6=sQuery(id+"F1.wireOp",EDGE,"E4059.0");var subQ7=sQuery(id+"F1.wireOp",EDGE,"E4059.3");var subQ8=sQuery(id+"F1.wireOp",EDGE,"E4059.1");var subQ9=sQuery(id+"F3.wireOp",EDGE,"E4060.0");Q0=makeQuery(id+"F6.boolean.opBoolean","SPLIT",FACE,{"disambiguationData":[TD([makeQuery(id+"F2.opExtrude","SWEPT_FACE",FACE,{"disambiguationData":[OSD([subQ6])]})])],"derivedFrom":makeQuery(id+"F4.opExtrude","CAP_FACE",FACE,{"disambiguationData":[OSD([subQ6,subQ8,sQuery(id+"F1.wireOp",EDGE,"E4059.2"),subQ7,subQ9,subQ5,sQuery(id+"F3.wireOp",EDGE,"E4060.2"),subQ4,subQ3,subQ2,subQ1,subQ0,sQuery(id+"F3.wireOp",EDGE,"E4063.top"),sQuery(id+"F3.wireOp",EDGE,"E4063.right"),sQuery(id+"F3.wireOp",EDGE,"E4064.top"),sQuery(id+"F3.wireOp",EDGE,"E4064.right")])],"isStart":false})});}
            var sketch = newSketch(context, id + "F7", { "sketchPlane" : qUnion([Q0])});
            skCircle(sketch, "E4068", {"center": v(29, -41) * mm, "radius": 1.6 * mm});
            skCircle(sketch, "E4069", {"center": v(-33, -41) * mm, "radius": 1.6 * mm});
            skSolve(sketch);
        }
        {
            var Q0;
            {var subQ0=sQuery(id+"F3.wireOp",EDGE,"E4064.top");var subQ1=sQuery(id+"F3.wireOp",EDGE,"E4063.right");var subQ2=sQuery(id+"F3.wireOp",EDGE,"E4063.top");var subQ3=sQuery(id+"F3.wireOp",EDGE,"E4060.3");var subQ4=sQuery(id+"F3.wireOp",EDGE,"E4064.right");var subQ5=sQuery(id+"F1.wireOp",EDGE,"E4059.1");var subQ6=sQuery(id+"F3.wireOp",EDGE,"E4060.2");var subQ7=sQuery(id+"F1.wireOp",EDGE,"E4059.3");var subQ8=sQuery(id+"F1.wireOp",EDGE,"E4059.2");var subQ9=sQuery(id+"F3.wireOp",EDGE,"E4060.1");Q0=makeQuery(id+"F6.boolean.opBoolean","SPLIT",FACE,{"disambiguationData":[TD([makeQuery(id+"F2.opExtrude","SWEPT_FACE",FACE,{"disambiguationData":[OSD([subQ8])]})])],"derivedFrom":makeQuery(id+"F4.opExtrude","CAP_FACE",FACE,{"disambiguationData":[OSD([sQuery(id+"F1.wireOp",EDGE,"E4059.0"),subQ5,subQ8,subQ7,sQuery(id+"F3.wireOp",EDGE,"E4060.0"),subQ9,subQ6,subQ3,sQuery(id+"F3.wireOp",EDGE,"E4061.top"),sQuery(id+"F3.wireOp",EDGE,"E4061.right"),sQuery(id+"F3.wireOp",EDGE,"E4062.top"),sQuery(id+"F3.wireOp",EDGE,"E4062.right"),subQ2,subQ1,subQ0,subQ4])],"isStart":false})});}
            var sketch = newSketch(context, id + "F8", { "sketchPlane" : qUnion([Q0])});
            skCircle(sketch, "E4070", {"center": v(-33, 44) * mm, "radius": 1.6 * mm});
            skCircle(sketch, "E4071", {"center": v(29, 44) * mm, "radius": 1.6 * mm});
            skSolve(sketch);
        }
        {
            var Q0;
            Q0=makeQuery(id+"F7.imprint","IMPRINT",FACE,{"disambiguationData":[TD([[makeQuery(id+"F7.imprint","IMPRINT",EDGE,{"derivedFrom":sQuery(id+"F7.wireOp",EDGE,"E4068")}),1.0]])]});
            var Q1;
            Q1=makeQuery(id+"F7.imprint","IMPRINT",FACE,{"disambiguationData":[TD([[makeQuery(id+"F7.imprint","IMPRINT",EDGE,{"derivedFrom":sQuery(id+"F7.wireOp",EDGE,"E4069")}),1.0]])]});
            var Q2;
            Q2=makeQuery(id+"F8.imprint","IMPRINT",FACE,{"disambiguationData":[TD([[makeQuery(id+"F8.imprint","IMPRINT",EDGE,{"derivedFrom":sQuery(id+"F8.wireOp",EDGE,"E4070")}),1.0]])]});
            var Q3;
            Q3=makeQuery(id+"F8.imprint","IMPRINT",FACE,{"disambiguationData":[TD([[makeQuery(id+"F8.imprint","IMPRINT",EDGE,{"derivedFrom":sQuery(id+"F8.wireOp",EDGE,"E4071")}),1.0]])]});
            extrude(context, id + "F9", {"entities" : qUnion([Q0, Q1, Q2, Q3]), "operationType" : NewBodyOperationType.REMOVE, "oppositeDirection" : true, "depth" : 25 * mm, "offsetDistance" : 25 * mm});
        }
        {
            var Q0;
            {var subQ0=sQuery(id+"F3.wireOp",EDGE,"E4062.right");var subQ1=sQuery(id+"F3.wireOp",EDGE,"E4062.top");var subQ2=sQuery(id+"F3.wireOp",EDGE,"E4061.right");var subQ3=sQuery(id+"F3.wireOp",EDGE,"E4061.top");var subQ4=sQuery(id+"F3.wireOp",EDGE,"E4060.3");var subQ5=sQuery(id+"F3.wireOp",EDGE,"E4060.1");var subQ6=sQuery(id+"F1.wireOp",EDGE,"E4059.0");var subQ7=sQuery(id+"F1.wireOp",EDGE,"E4059.3");var subQ8=sQuery(id+"F1.wireOp",EDGE,"E4059.1");var subQ9=sQuery(id+"F3.wireOp",EDGE,"E4060.0");Q0=makeQuery(id+"F6.boolean.opBoolean","SPLIT",FACE,{"disambiguationData":[TD([makeQuery(id+"F2.opExtrude","SWEPT_FACE",FACE,{"disambiguationData":[OSD([subQ6])]})])],"derivedFrom":makeQuery(id+"F4.opExtrude","CAP_FACE",FACE,{"disambiguationData":[OSD([subQ6,subQ8,sQuery(id+"F1.wireOp",EDGE,"E4059.2"),subQ7,subQ9,subQ5,sQuery(id+"F3.wireOp",EDGE,"E4060.2"),subQ4,subQ3,subQ2,subQ1,subQ0,sQuery(id+"F3.wireOp",EDGE,"E4063.top"),sQuery(id+"F3.wireOp",EDGE,"E4063.right"),sQuery(id+"F3.wireOp",EDGE,"E4064.top"),sQuery(id+"F3.wireOp",EDGE,"E4064.right")])],"isStart":false})});}
            var sketch = newSketch(context, id + "F10", { "sketchPlane" : qUnion([Q0])});
            skLineSegment(sketch, "E4072.bottom", {"start": v(33.5, -37.5) * mm, "end": v(35.5, -37.5) * mm});
            skLineSegment(sketch, "E4072.top", {"start": v(33.5, 17.25) * mm, "end": v(35.5, 17.25) * mm});
            skLineSegment(sketch, "E4072.left", {"start": v(33.5, -37.5) * mm, "end": v(33.5, 17.25) * mm});
            skLineSegment(sketch, "E4072.right", {"start": v(35.5, -37.5) * mm, "end": v(35.5, 17.25) * mm});
            skSolve(sketch);
        }
        {
            var Q0;
            Q0=makeQuery(id+"F10.imprint","IMPRINT",FACE,{"disambiguationData":[TD([[makeQuery(id+"F10.imprint","IMPRINT",EDGE,{"derivedFrom":sQuery(id+"F10.wireOp",EDGE,"E4072.bottom")}),1.0]])]});
            extrude(context, id + "F11", {"entities" : qUnion([Q0]), "operationType" : NewBodyOperationType.REMOVE, "oppositeDirection" : true, "depth" : 5 * mm, "offsetDistance" : 25 * mm});
        }
        {
            var Q0;
            {var subQ0=sQuery(id+"F1.wireOp",EDGE,"E4059.3");var subQ1=sQuery(id+"F1.wireOp",EDGE,"E4059.0");Q0=makeQuery(id+"F4.boolean.opBoolean","MERGE",EDGE,{"derivedFrom":[makeQuery(id+"F2.opExtrude","SWEPT_EDGE",EDGE,{"disambiguationData":[OSD([subQ1,subQ0])]}),makeQuery(id+"F4.opExtrude","SWEPT_EDGE",EDGE,{"disambiguationData":[OSD([subQ1,subQ0])]})]});}
            var Q1;
            {var subQ0=sQuery(id+"F1.wireOp",EDGE,"E4059.1");var subQ1=sQuery(id+"F1.wireOp",EDGE,"E4059.0");Q1=makeQuery(id+"F4.boolean.opBoolean","MERGE",EDGE,{"derivedFrom":[makeQuery(id+"F2.opExtrude","SWEPT_EDGE",EDGE,{"disambiguationData":[OSD([subQ1,subQ0])]}),makeQuery(id+"F4.opExtrude","SWEPT_EDGE",EDGE,{"disambiguationData":[OSD([subQ1,subQ0])]})]});}
            var Q2;
            {var subQ0=sQuery(id+"F1.wireOp",EDGE,"E4059.3");var subQ1=sQuery(id+"F1.wireOp",EDGE,"E4059.2");Q2=makeQuery(id+"F4.boolean.opBoolean","MERGE",EDGE,{"derivedFrom":[makeQuery(id+"F2.opExtrude","SWEPT_EDGE",EDGE,{"disambiguationData":[OSD([subQ1,subQ0])]}),makeQuery(id+"F4.opExtrude","SWEPT_EDGE",EDGE,{"disambiguationData":[OSD([subQ1,subQ0])]})]});}
            var Q3;
            {var subQ0=sQuery(id+"F1.wireOp",EDGE,"E4059.2");var subQ1=sQuery(id+"F1.wireOp",EDGE,"E4059.1");Q3=makeQuery(id+"F4.boolean.opBoolean","MERGE",EDGE,{"derivedFrom":[makeQuery(id+"F2.opExtrude","SWEPT_EDGE",EDGE,{"disambiguationData":[OSD([subQ1,subQ0])]}),makeQuery(id+"F4.opExtrude","SWEPT_EDGE",EDGE,{"disambiguationData":[OSD([subQ1,subQ0])]})]});}
            fillet(context, id + "F12", {"entities" : qUnion([Q0, Q1, Q2, Q3]), "radius" : 2 * mm, "tangentPropagation" : true, "allowEdgeOverflow" : false});
        }
    });
